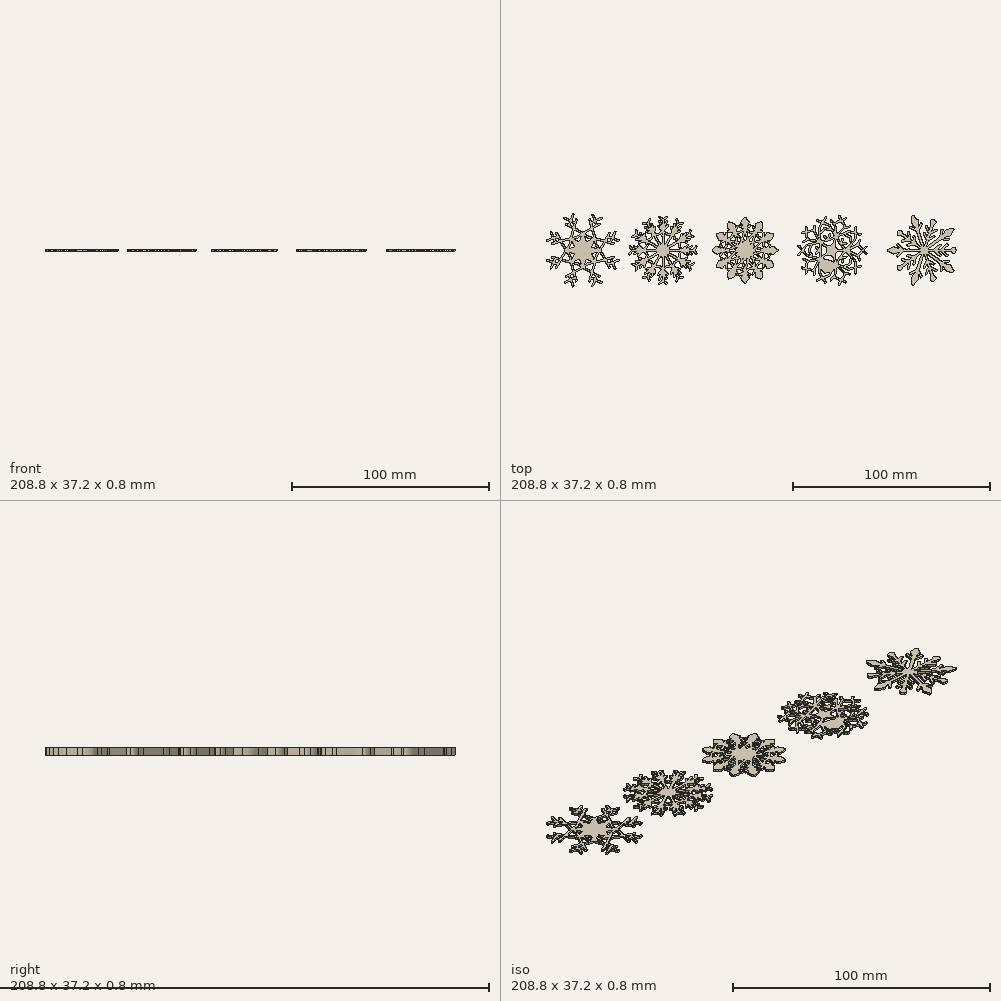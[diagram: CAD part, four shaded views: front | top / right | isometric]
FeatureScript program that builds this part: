
annotation { "Feature Type Name" : "Feature", "Feature Type Description" : "" }
export const myFeature = defineFeature(function(context is Context, id is Id, definition is map)
    precondition{}
    {
        {
            var Q0;
            Q0=qCreatedBy(makeId("Top.planeOp"),FACE);
            var sketch = newSketch(context, id + "F0", { "sketchPlane" : qUnion([Q0])});
            skFitSpline(sketch, "E0", {"points": [v(19, 0) * mm, v(18.91, 0.07) * mm, v(18.86, 0.12) * mm, v(18.83, 0.12) * mm]});
            skFitSpline(sketch, "E1", {"points": [v(18.83, 0.12) * mm, v(18.78, 0.1) * mm, v(18.72, 0.05) * mm, v(18.7, 0) * mm]});
            skFitSpline(sketch, "E2", {"points": [v(18.7, 0) * mm, v(18.68, -0.05) * mm, v(18.77, -0.14) * mm, v(18.83, -0.12) * mm]});
            skFitSpline(sketch, "E3", {"points": [v(18.83, -0.12) * mm, v(18.88, -0.1) * mm, v(18.92, -0.05) * mm, v(19, 0) * mm]});
            skFitSpline(sketch, "E4", {"points": [v(18, -11.04) * mm, v(17.67, -11.1) * mm, v(17.39, -11.14) * mm, v(17.1, -11.2) * mm]});
            skFitSpline(sketch, "E5", {"points": [v(17.1, -11.2) * mm, v(16.6, -11.32) * mm, v(16.09, -11.45) * mm, v(15.58, -11.59) * mm]});
            skFitSpline(sketch, "E6", {"points": [v(15.58, -11.59) * mm, v(15.26, -11.67) * mm, v(15, -11.51) * mm, v(14.74, -11.39) * mm]});
            skFitSpline(sketch, "E7", {"points": [v(14.74, -11.39) * mm, v(14.72, -11.38) * mm, v(14.7, -11.35) * mm, v(14.68, -11.32) * mm]});
            skFitSpline(sketch, "E8", {"points": [v(14.68, -11.32) * mm, v(14.51, -11.12) * mm, v(14.36, -10.92) * mm, v(14.2, -10.73) * mm]});
            skFitSpline(sketch, "E9", {"points": [v(14.2, -10.73) * mm, v(13.83, -10.31) * mm, v(13.46, -9.9) * mm, v(13.08, -9.5) * mm]});
            skFitSpline(sketch, "E10", {"points": [v(13.08, -9.5) * mm, v(13.07, -9.48) * mm, v(13.05, -9.48) * mm, v(13, -9.46) * mm]});
            skFitSpline(sketch, "E11", {"points": [v(13, -9.46) * mm, v(13, -9.5) * mm, v(13, -9.53) * mm, v(13, -9.56) * mm]});
            skFitSpline(sketch, "E12", {"points": [v(13, -9.56) * mm, v(12.96, -9.94) * mm, v(12.93, -10.33) * mm, v(12.9, -10.72) * mm]});
            skFitSpline(sketch, "E13", {"points": [v(12.9, -10.72) * mm, v(12.87, -10.96) * mm, v(12.92, -11.17) * mm, v(13.06, -11.37) * mm]});
            skFitSpline(sketch, "E14", {"points": [v(13.06, -11.37) * mm, v(13.44, -11.95) * mm, v(13.8, -12.55) * mm, v(14.18, -13.13) * mm]});
            skFitSpline(sketch, "E15", {"points": [v(14.18, -13.13) * mm, v(14.26, -13.26) * mm, v(14.36, -13.37) * mm, v(14.46, -13.5) * mm]});
            skFitSpline(sketch, "E16", {"points": [v(14.46, -13.5) * mm, v(14.84, -13.36) * mm, v(15.2, -13.22) * mm, v(15.56, -13.07) * mm]});
            skFitSpline(sketch, "E17", {"points": [v(15.56, -13.07) * mm, v(16.03, -12.9) * mm, v(16.5, -12.7) * mm, v(16.96, -12.52) * mm]});
            skFitSpline(sketch, "E18", {"points": [v(16.96, -12.52) * mm, v(17.05, -12.48) * mm, v(17.13, -12.42) * mm, v(17.18, -12.34) * mm]});
            skFitSpline(sketch, "E19", {"points": [v(17.18, -12.34) * mm, v(17.45, -11.93) * mm, v(17.7, -11.5) * mm, v(18, -11.04) * mm]});
            skFitSpline(sketch, "E20", {"points": [v(8.01, -2.6) * mm, v(8.03, -2.6) * mm, v(8.04, -2.57) * mm, v(8.06, -2.56) * mm]});
            skFitSpline(sketch, "E21", {"points": [v(8.06, -2.56) * mm, v(7.78, -2.08) * mm, v(7.5, -1.6) * mm, v(7.21, -1.12) * mm]});
            skFitSpline(sketch, "E22", {"points": [v(7.21, -1.12) * mm, v(7.08, -0.9) * mm, v(6.92, -0.68) * mm, v(6.78, -0.45) * mm]});
            skFitSpline(sketch, "E23", {"points": [v(6.78, -0.45) * mm, v(6.73, -0.36) * mm, v(6.71, -0.25) * mm, v(6.7, -0.14) * mm]});
            skFitSpline(sketch, "E24", {"points": [v(6.7, -0.14) * mm, v(6.68, -0.07) * mm, v(6.7, 0) * mm, v(6.7, 0.08) * mm]});
            skFitSpline(sketch, "E25", {"points": [v(6.7, 0.08) * mm, v(6.68, 0.23) * mm, v(6.73, 0.37) * mm, v(6.81, 0.5) * mm]});
            skFitSpline(sketch, "E26", {"points": [v(6.81, 0.5) * mm, v(7.2, 1.12) * mm, v(7.56, 1.74) * mm, v(7.94, 2.37) * mm]});
            skFitSpline(sketch, "E27", {"points": [v(7.94, 2.37) * mm, v(7.97, 2.43) * mm, v(8, 2.5) * mm, v(8.05, 2.6) * mm]});
            skFitSpline(sketch, "E28", {"points": [v(8.05, 2.6) * mm, v(7.98, 2.6) * mm, v(7.95, 2.6) * mm, v(7.9, 2.59) * mm]});
            skFitSpline(sketch, "E29", {"points": [v(7.9, 2.59) * mm, v(7.55, 2.5) * mm, v(7.2, 2.4) * mm, v(6.84, 2.33) * mm]});
            skFitSpline(sketch, "E30", {"points": [v(6.84, 2.33) * mm, v(6.57, 2.27) * mm, v(6.36, 2.15) * mm, v(6.19, 1.93) * mm]});
            skFitSpline(sketch, "E31", {"points": [v(6.19, 1.93) * mm, v(5.77, 1.4) * mm, v(5.34, 0.9) * mm, v(4.91, 0.38) * mm]});
            skFitSpline(sketch, "E32", {"points": [v(4.91, 0.38) * mm, v(4.81, 0.26) * mm, v(4.73, 0.12) * mm, v(4.63, -0.02) * mm]});
            skFitSpline(sketch, "E33", {"points": [v(4.63, -0.02) * mm, v(4.98, -0.45) * mm, v(5.31, -0.86) * mm, v(5.65, -1.28) * mm]});
            skFitSpline(sketch, "E34", {"points": [v(5.65, -1.28) * mm, v(5.88, -1.55) * mm, v(6.12, -1.82) * mm, v(6.35, -2.1) * mm]});
            skFitSpline(sketch, "E35", {"points": [v(6.35, -2.1) * mm, v(6.42, -2.18) * mm, v(6.5, -2.24) * mm, v(6.6, -2.26) * mm]});
            skFitSpline(sketch, "E36", {"points": [v(6.6, -2.26) * mm, v(6.92, -2.33) * mm, v(7.24, -2.41) * mm, v(7.55, -2.5) * mm]});
            skFitSpline(sketch, "E37", {"points": [v(7.55, -2.5) * mm, v(7.7, -2.53) * mm, v(7.86, -2.57) * mm, v(8.01, -2.6) * mm]});
            skFitSpline(sketch, "E38", {"points": [v(17.95, 11.02) * mm, v(17.96, 11.04) * mm, v(17.96, 11.06) * mm, v(17.97, 11.08) * mm]});
            skFitSpline(sketch, "E39", {"points": [v(17.97, 11.08) * mm, v(17.72, 11.48) * mm, v(17.46, 11.89) * mm, v(17.22, 12.3) * mm]});
            skFitSpline(sketch, "E40", {"points": [v(17.22, 12.3) * mm, v(17.15, 12.41) * mm, v(17.06, 12.49) * mm, v(16.93, 12.53) * mm]});
            skFitSpline(sketch, "E41", {"points": [v(16.93, 12.53) * mm, v(16.23, 12.8) * mm, v(15.54, 13.1) * mm, v(14.84, 13.37) * mm]});
            skFitSpline(sketch, "E42", {"points": [v(14.84, 13.37) * mm, v(14.71, 13.42) * mm, v(14.57, 13.45) * mm, v(14.42, 13.5) * mm]});
            skFitSpline(sketch, "E43", {"points": [v(14.42, 13.5) * mm, v(14.22, 13.18) * mm, v(14.03, 12.88) * mm, v(13.83, 12.58) * mm]});
            skFitSpline(sketch, "E44", {"points": [v(13.83, 12.58) * mm, v(13.55, 12.12) * mm, v(13.26, 11.67) * mm, v(12.97, 11.22) * mm]});
            skFitSpline(sketch, "E45", {"points": [v(12.97, 11.22) * mm, v(12.91, 11.13) * mm, v(12.89, 11.04) * mm, v(12.9, 10.93) * mm]});
            skFitSpline(sketch, "E46", {"points": [v(12.9, 10.93) * mm, v(12.93, 10.5) * mm, v(12.96, 10.06) * mm, v(12.99, 9.62) * mm]});
            skFitSpline(sketch, "E47", {"points": [v(12.99, 9.62) * mm, v(13, 9.57) * mm, v(13, 9.52) * mm, v(13.02, 9.43) * mm]});
            skFitSpline(sketch, "E48", {"points": [v(13.02, 9.43) * mm, v(13.3, 9.73) * mm, v(13.57, 10) * mm, v(13.81, 10.27) * mm]});
            skFitSpline(sketch, "E49", {"points": [v(13.81, 10.27) * mm, v(14.1, 10.6) * mm, v(14.37, 10.95) * mm, v(14.65, 11.29) * mm]});
            skFitSpline(sketch, "E50", {"points": [v(14.65, 11.29) * mm, v(14.74, 11.4) * mm, v(14.85, 11.49) * mm, v(15, 11.52) * mm]});
            skFitSpline(sketch, "E51", {"points": [v(15, 11.52) * mm, v(15.06, 11.53) * mm, v(15.12, 11.56) * mm, v(15.18, 11.57) * mm]});
            skFitSpline(sketch, "E52", {"points": [v(15.18, 11.57) * mm, v(15.3, 11.59) * mm, v(15.42, 11.62) * mm, v(15.53, 11.6) * mm]});
            skFitSpline(sketch, "E53", {"points": [v(15.53, 11.6) * mm, v(15.78, 11.55) * mm, v(16.01, 11.46) * mm, v(16.25, 11.4) * mm]});
            skFitSpline(sketch, "E54", {"points": [v(16.25, 11.4) * mm, v(16.82, 11.28) * mm, v(17.38, 11.15) * mm, v(17.95, 11.02) * mm]});
            skFitSpline(sketch, "E55", {"points": [v(26.01, 8.4) * mm, v(26.54, 8.18) * mm, v(27.04, 7.95) * mm, v(27.54, 7.74) * mm]});
            skFitSpline(sketch, "E56", {"points": [v(27.54, 7.74) * mm, v(27.8, 7.63) * mm, v(28.05, 7.55) * mm, v(28.3, 7.44) * mm]});
            skFitSpline(sketch, "E57", {"points": [v(28.3, 7.44) * mm, v(28.4, 7.4) * mm, v(28.49, 7.3) * mm, v(28.57, 7.22) * mm]});
            skFitSpline(sketch, "E58", {"points": [v(28.57, 7.22) * mm, v(28.62, 7.18) * mm, v(28.65, 7.1) * mm, v(28.7, 7.05) * mm]});
            skFitSpline(sketch, "E59", {"points": [v(28.7, 7.05) * mm, v(28.78, 6.96) * mm, v(28.82, 6.85) * mm, v(28.83, 6.73) * mm]});
            skFitSpline(sketch, "E60", {"points": [v(28.83, 6.73) * mm, v(28.85, 6.29) * mm, v(28.87, 5.85) * mm, v(28.9, 5.41) * mm]});
            skFitSpline(sketch, "E61", {"points": [v(28.9, 5.41) * mm, v(28.95, 5.02) * mm, v(29, 4.63) * mm, v(29.06, 4.24) * mm]});
            skFitSpline(sketch, "E62", {"points": [v(29.06, 4.24) * mm, v(29.1, 4.25) * mm, v(29.12, 4.26) * mm, v(29.13, 4.27) * mm]});
            skFitSpline(sketch, "E63", {"points": [v(29.13, 4.27) * mm, v(29.44, 4.64) * mm, v(29.76, 5.02) * mm, v(30.08, 5.4) * mm]});
            skFitSpline(sketch, "E64", {"points": [v(30.08, 5.4) * mm, v(30.11, 5.45) * mm, v(30.14, 5.51) * mm, v(30.15, 5.57) * mm]});
            skFitSpline(sketch, "E65", {"points": [v(30.15, 5.57) * mm, v(30.17, 5.74) * mm, v(30.19, 5.9) * mm, v(30.2, 6.07) * mm]});
            skFitSpline(sketch, "E66", {"points": [v(30.2, 6.07) * mm, v(30.23, 6.6) * mm, v(30.27, 7.14) * mm, v(30.3, 7.67) * mm]});
            skFitSpline(sketch, "E67", {"points": [v(30.3, 7.67) * mm, v(30.3, 7.9) * mm, v(30.3, 8.11) * mm, v(30.3, 8.34) * mm]});
            skFitSpline(sketch, "E68", {"points": [v(30.3, 8.34) * mm, v(30.19, 8.38) * mm, v(30.08, 8.42) * mm, v(29.97, 8.45) * mm]});
            skFitSpline(sketch, "E69", {"points": [v(29.97, 8.45) * mm, v(29.2, 8.65) * mm, v(28.41, 8.85) * mm, v(27.63, 9.04) * mm]});
            skFitSpline(sketch, "E70", {"points": [v(27.63, 9.04) * mm, v(27.57, 9.06) * mm, v(27.49, 9.05) * mm, v(27.43, 9.03) * mm]});
            skFitSpline(sketch, "E71", {"points": [v(27.43, 9.03) * mm, v(26.97, 8.85) * mm, v(26.52, 8.67) * mm, v(26.07, 8.48) * mm]});
            skFitSpline(sketch, "E72", {"points": [v(26.07, 8.48) * mm, v(26.06, 8.48) * mm, v(26.06, 8.46) * mm, v(26.01, 8.4) * mm]});
            skFitSpline(sketch, "E73", {"points": [v(29.1, -4.23) * mm, v(29.08, -4.24) * mm, v(29.06, -4.24) * mm, v(29.05, -4.24) * mm]});
            skFitSpline(sketch, "E74", {"points": [v(29.05, -4.24) * mm, v(28.99, -4.77) * mm, v(28.92, -5.3) * mm, v(28.88, -5.82) * mm]});
            skFitSpline(sketch, "E75", {"points": [v(28.88, -5.82) * mm, v(28.85, -6.14) * mm, v(28.85, -6.46) * mm, v(28.82, -6.78) * mm]});
            skFitSpline(sketch, "E76", {"points": [v(28.82, -6.78) * mm, v(28.81, -6.87) * mm, v(28.75, -6.95) * mm, v(28.71, -7.04) * mm]});
            skFitSpline(sketch, "E77", {"points": [v(28.71, -7.04) * mm, v(28.68, -7.1) * mm, v(28.62, -7.15) * mm, v(28.59, -7.2) * mm]});
            skFitSpline(sketch, "E78", {"points": [v(28.59, -7.2) * mm, v(28.52, -7.32) * mm, v(28.42, -7.4) * mm, v(28.3, -7.45) * mm]});
            skFitSpline(sketch, "E79", {"points": [v(28.3, -7.45) * mm, v(28.13, -7.52) * mm, v(27.96, -7.58) * mm, v(27.79, -7.65) * mm]});
            skFitSpline(sketch, "E80", {"points": [v(27.79, -7.65) * mm, v(27.23, -7.9) * mm, v(26.68, -8.13) * mm, v(26.12, -8.38) * mm]});
            skFitSpline(sketch, "E81", {"points": [v(26.12, -8.38) * mm, v(26.09, -8.4) * mm, v(26.06, -8.42) * mm, v(26.02, -8.45) * mm]});
            skFitSpline(sketch, "E82", {"points": [v(26.02, -8.45) * mm, v(26.48, -8.64) * mm, v(26.92, -8.82) * mm, v(27.36, -9) * mm]});
            skFitSpline(sketch, "E83", {"points": [v(27.36, -9) * mm, v(27.48, -9.06) * mm, v(27.59, -9.06) * mm, v(27.7, -9.03) * mm]});
            skFitSpline(sketch, "E84", {"points": [v(27.7, -9.03) * mm, v(28.44, -8.84) * mm, v(29.18, -8.66) * mm, v(29.91, -8.47) * mm]});
            skFitSpline(sketch, "E85", {"points": [v(29.91, -8.47) * mm, v(30.04, -8.44) * mm, v(30.17, -8.38) * mm, v(30.31, -8.33) * mm]});
            skFitSpline(sketch, "E86", {"points": [v(30.31, -8.33) * mm, v(30.31, -8.25) * mm, v(30.32, -8.17) * mm, v(30.31, -8.1) * mm]});
            skFitSpline(sketch, "E87", {"points": [v(30.31, -8.1) * mm, v(30.3, -7.84) * mm, v(30.28, -7.59) * mm, v(30.26, -7.33) * mm]});
            skFitSpline(sketch, "E88", {"points": [v(30.26, -7.33) * mm, v(30.23, -6.76) * mm, v(30.2, -6.19) * mm, v(30.15, -5.61) * mm]});
            skFitSpline(sketch, "E89", {"points": [v(30.15, -5.61) * mm, v(30.15, -5.53) * mm, v(30.1, -5.44) * mm, v(30.06, -5.38) * mm]});
            skFitSpline(sketch, "E90", {"points": [v(30.06, -5.38) * mm, v(29.85, -5.13) * mm, v(29.64, -4.88) * mm, v(29.42, -4.63) * mm]});
            skFitSpline(sketch, "E91", {"points": [v(29.42, -4.63) * mm, v(29.31, -4.5) * mm, v(29.2, -4.36) * mm, v(29.1, -4.23) * mm]});
            skFitSpline(sketch, "E92", {"points": [v(21.23, -5.73) * mm, v(21.28, -5.66) * mm, v(21.32, -5.61) * mm, v(21.35, -5.56) * mm]});
            skFitSpline(sketch, "E93", {"points": [v(21.35, -5.56) * mm, v(21.82, -4.8) * mm, v(22.27, -4.03) * mm, v(22.74, -3.26) * mm]});
            skFitSpline(sketch, "E94", {"points": [v(22.74, -3.26) * mm, v(22.85, -3.08) * mm, v(22.98, -2.9) * mm, v(23.11, -2.74) * mm]});
            skFitSpline(sketch, "E95", {"points": [v(23.11, -2.74) * mm, v(23.3, -2.52) * mm, v(23.49, -2.3) * mm, v(23.68, -2.09) * mm]});
            skFitSpline(sketch, "E96", {"points": [v(23.68, -2.09) * mm, v(24.08, -1.62) * mm, v(24.5, -1.15) * mm, v(24.9, -0.68) * mm]});
            skFitSpline(sketch, "E97", {"points": [v(24.9, -0.68) * mm, v(24.94, -0.63) * mm, v(24.97, -0.58) * mm, v(25.02, -0.5) * mm]});
            skFitSpline(sketch, "E98", {"points": [v(25.02, -0.5) * mm, v(24.9, -0.5) * mm, v(24.82, -0.5) * mm, v(24.74, -0.5) * mm]});
            skFitSpline(sketch, "E99", {"points": [v(24.74, -0.5) * mm, v(24.43, -0.51) * mm, v(24.1, -0.52) * mm, v(23.79, -0.52) * mm]});
            skFitSpline(sketch, "E100", {"points": [v(23.79, -0.52) * mm, v(23.37, -0.52) * mm, v(22.96, -0.5) * mm, v(22.54, -0.5) * mm]});
            skFitSpline(sketch, "E101", {"points": [v(22.54, -0.5) * mm, v(22.4, -0.5) * mm, v(22.26, -0.51) * mm, v(22.13, -0.6) * mm]});
            skFitSpline(sketch, "E102", {"points": [v(22.13, -0.6) * mm, v(21.76, -0.86) * mm, v(21.38, -1.12) * mm, v(21, -1.36) * mm]});
            skFitSpline(sketch, "E103", {"points": [v(21, -1.36) * mm, v(20.9, -1.43) * mm, v(20.83, -1.52) * mm, v(20.8, -1.64) * mm]});
            skFitSpline(sketch, "E104", {"points": [v(20.8, -1.64) * mm, v(20.68, -2.08) * mm, v(20.55, -2.52) * mm, v(20.42, -2.95) * mm]});
            skFitSpline(sketch, "E105", {"points": [v(20.42, -2.95) * mm, v(20.4, -3.06) * mm, v(20.4, -3.16) * mm, v(20.43, -3.26) * mm]});
            skFitSpline(sketch, "E106", {"points": [v(20.43, -3.26) * mm, v(20.69, -4.07) * mm, v(20.95, -4.88) * mm, v(21.23, -5.73) * mm]});
            skFitSpline(sketch, "E107", {"points": [v(20.24, -6.06) * mm, v(20.24, -6) * mm, v(20.24, -5.97) * mm, v(20.23, -5.95) * mm]});
            skFitSpline(sketch, "E108", {"points": [v(20.23, -5.95) * mm, v(19.97, -5.17) * mm, v(19.71, -4.38) * mm, v(19.45, -3.6) * mm]});
            skFitSpline(sketch, "E109", {"points": [v(19.45, -3.6) * mm, v(19.41, -3.5) * mm, v(19.34, -3.4) * mm, v(19.26, -3.33) * mm]});
            skFitSpline(sketch, "E110", {"points": [v(19.26, -3.33) * mm, v(18.92, -3.05) * mm, v(18.57, -2.78) * mm, v(18.23, -2.5) * mm]});
            skFitSpline(sketch, "E111", {"points": [v(18.23, -2.5) * mm, v(18.1, -2.41) * mm, v(17.98, -2.37) * mm, v(17.83, -2.38) * mm]});
            skFitSpline(sketch, "E112", {"points": [v(17.83, -2.38) * mm, v(17.44, -2.4) * mm, v(17.05, -2.42) * mm, v(16.66, -2.42) * mm]});
            skFitSpline(sketch, "E113", {"points": [v(16.66, -2.42) * mm, v(16.46, -2.42) * mm, v(16.3, -2.48) * mm, v(16.13, -2.6) * mm]});
            skFitSpline(sketch, "E114", {"points": [v(16.13, -2.6) * mm, v(15.5, -3.06) * mm, v(14.86, -3.5) * mm, v(14.22, -3.97) * mm]});
            skFitSpline(sketch, "E115", {"points": [v(14.22, -3.97) * mm, v(14.19, -3.99) * mm, v(14.16, -4.02) * mm, v(14.12, -4.06) * mm]});
            skFitSpline(sketch, "E116", {"points": [v(14.12, -4.06) * mm, v(14.2, -4.09) * mm, v(14.26, -4.1) * mm, v(14.32, -4.12) * mm]});
            skFitSpline(sketch, "E117", {"points": [v(14.32, -4.12) * mm, v(14.71, -4.2) * mm, v(15.1, -4.29) * mm, v(15.5, -4.38) * mm]});
            skFitSpline(sketch, "E118", {"points": [v(15.5, -4.38) * mm, v(16, -4.5) * mm, v(16.52, -4.62) * mm, v(17.03, -4.75) * mm]});
            skFitSpline(sketch, "E119", {"points": [v(17.03, -4.75) * mm, v(17.23, -4.8) * mm, v(17.43, -4.89) * mm, v(17.63, -4.96) * mm]});
            skFitSpline(sketch, "E120", {"points": [v(17.63, -4.96) * mm, v(17.83, -5.04) * mm, v(18.03, -5.13) * mm, v(18.23, -5.22) * mm]});
            skFitSpline(sketch, "E121", {"points": [v(18.23, -5.22) * mm, v(18.64, -5.39) * mm, v(19.05, -5.56) * mm, v(19.46, -5.74) * mm]});
            skFitSpline(sketch, "E122", {"points": [v(19.46, -5.74) * mm, v(19.7, -5.84) * mm, v(19.96, -5.95) * mm, v(20.24, -6.06) * mm]});
            skFitSpline(sketch, "E123", {"points": [v(13.52, -3.2) * mm, v(13.55, -3.2) * mm, v(13.57, -3.2) * mm, v(13.58, -3.19) * mm]});
            skFitSpline(sketch, "E124", {"points": [v(13.58, -3.19) * mm, v(14.26, -2.69) * mm, v(14.94, -2.19) * mm, v(15.62, -1.68) * mm]});
            skFitSpline(sketch, "E125", {"points": [v(15.62, -1.68) * mm, v(15.7, -1.62) * mm, v(15.76, -1.53) * mm, v(15.8, -1.44) * mm]});
            skFitSpline(sketch, "E126", {"points": [v(15.8, -1.44) * mm, v(15.95, -1.04) * mm, v(16.09, -0.64) * mm, v(16.24, -0.25) * mm]});
            skFitSpline(sketch, "E127", {"points": [v(16.24, -0.25) * mm, v(16.3, -0.08) * mm, v(16.31, 0.07) * mm, v(16.25, 0.24) * mm]});
            skFitSpline(sketch, "E128", {"points": [v(16.25, 0.24) * mm, v(16.1, 0.6) * mm, v(15.97, 0.95) * mm, v(15.85, 1.32) * mm]});
            skFitSpline(sketch, "E129", {"points": [v(15.85, 1.32) * mm, v(15.78, 1.52) * mm, v(15.67, 1.66) * mm, v(15.5, 1.78) * mm]});
            skFitSpline(sketch, "E130", {"points": [v(15.5, 1.78) * mm, v(14.87, 2.23) * mm, v(14.25, 2.7) * mm, v(13.63, 3.16) * mm]});
            skFitSpline(sketch, "E131", {"points": [v(13.63, 3.16) * mm, v(13.6, 3.18) * mm, v(13.56, 3.2) * mm, v(13.5, 3.23) * mm]});
            skFitSpline(sketch, "E132", {"points": [v(13.5, 3.23) * mm, v(13.51, 3) * mm, v(13.52, 2.8) * mm, v(13.54, 2.6) * mm]});
            skFitSpline(sketch, "E133", {"points": [v(13.54, 2.6) * mm, v(13.57, 2.24) * mm, v(13.62, 1.87) * mm, v(13.65, 1.5) * mm]});
            skFitSpline(sketch, "E134", {"points": [v(13.65, 1.5) * mm, v(13.68, 1.16) * mm, v(13.7, 0.8) * mm, v(13.72, 0.46) * mm]});
            skFitSpline(sketch, "E135", {"points": [v(13.72, 0.46) * mm, v(13.74, 0.21) * mm, v(13.76, -0.03) * mm, v(13.75, -0.28) * mm]});
            skFitSpline(sketch, "E136", {"points": [v(13.75, -0.28) * mm, v(13.73, -0.65) * mm, v(13.7, -1.03) * mm, v(13.66, -1.4) * mm]});
            skFitSpline(sketch, "E137", {"points": [v(13.66, -1.4) * mm, v(13.62, -1.82) * mm, v(13.56, -2.24) * mm, v(13.53, -2.66) * mm]});
            skFitSpline(sketch, "E138", {"points": [v(13.53, -2.66) * mm, v(13.51, -2.84) * mm, v(13.52, -3.02) * mm, v(13.52, -3.2) * mm]});
            skFitSpline(sketch, "E139", {"points": [v(14.11, 4.07) * mm, v(14.15, 4.03) * mm, v(14.16, 4) * mm, v(14.18, 4) * mm]});
            skFitSpline(sketch, "E140", {"points": [v(14.18, 4) * mm, v(14.85, 3.52) * mm, v(15.52, 3.04) * mm, v(16.18, 2.56) * mm]});
            skFitSpline(sketch, "E141", {"points": [v(16.18, 2.56) * mm, v(16.32, 2.46) * mm, v(16.46, 2.42) * mm, v(16.63, 2.42) * mm]});
            skFitSpline(sketch, "E142", {"points": [v(16.63, 2.42) * mm, v(16.97, 2.41) * mm, v(17.3, 2.4) * mm, v(17.63, 2.37) * mm]});
            skFitSpline(sketch, "E143", {"points": [v(17.63, 2.37) * mm, v(17.89, 2.36) * mm, v(18.11, 2.4) * mm, v(18.32, 2.57) * mm]});
            skFitSpline(sketch, "E144", {"points": [v(18.32, 2.57) * mm, v(18.6, 2.82) * mm, v(18.9, 3.05) * mm, v(19.2, 3.27) * mm]});
            skFitSpline(sketch, "E145", {"points": [v(19.2, 3.27) * mm, v(19.33, 3.37) * mm, v(19.42, 3.5) * mm, v(19.47, 3.65) * mm]});
            skFitSpline(sketch, "E146", {"points": [v(19.47, 3.65) * mm, v(19.71, 4.4) * mm, v(19.97, 5.15) * mm, v(20.22, 5.9) * mm]});
            skFitSpline(sketch, "E147", {"points": [v(20.22, 5.9) * mm, v(20.23, 5.94) * mm, v(20.23, 5.99) * mm, v(20.24, 6.06) * mm]});
            skFitSpline(sketch, "E148", {"points": [v(20.24, 6.06) * mm, v(20.11, 6) * mm, v(20, 5.97) * mm, v(19.9, 5.93) * mm]});
            skFitSpline(sketch, "E149", {"points": [v(19.9, 5.93) * mm, v(19.39, 5.7) * mm, v(18.86, 5.48) * mm, v(18.34, 5.26) * mm]});
            skFitSpline(sketch, "E150", {"points": [v(18.34, 5.26) * mm, v(18.08, 5.15) * mm, v(17.82, 5.03) * mm, v(17.55, 4.93) * mm]});
            skFitSpline(sketch, "E151", {"points": [v(17.55, 4.93) * mm, v(17.32, 4.84) * mm, v(17.08, 4.78) * mm, v(16.85, 4.7) * mm]});
            skFitSpline(sketch, "E152", {"points": [v(16.85, 4.7) * mm, v(16.67, 4.66) * mm, v(16.49, 4.63) * mm, v(16.3, 4.59) * mm]});
            skFitSpline(sketch, "E153", {"points": [v(16.3, 4.59) * mm, v(15.84, 4.48) * mm, v(15.38, 4.37) * mm, v(14.91, 4.26) * mm]});
            skFitSpline(sketch, "E154", {"points": [v(14.91, 4.26) * mm, v(14.65, 4.2) * mm, v(14.4, 4.14) * mm, v(14.11, 4.07) * mm]});
            skFitSpline(sketch, "E155", {"points": [v(25.03, 0.52) * mm, v(24.94, 0.63) * mm, v(24.87, 0.72) * mm, v(24.8, 0.8) * mm]});
            skFitSpline(sketch, "E156", {"points": [v(24.8, 0.8) * mm, v(24.4, 1.25) * mm, v(24.02, 1.7) * mm, v(23.63, 2.14) * mm]});
            skFitSpline(sketch, "E157", {"points": [v(23.63, 2.14) * mm, v(23.5, 2.3) * mm, v(23.37, 2.44) * mm, v(23.25, 2.6) * mm]});
            skFitSpline(sketch, "E158", {"points": [v(23.25, 2.6) * mm, v(23.05, 2.85) * mm, v(22.86, 3.1) * mm, v(22.68, 3.37) * mm]});
            skFitSpline(sketch, "E159", {"points": [v(22.68, 3.37) * mm, v(22.58, 3.5) * mm, v(22.5, 3.67) * mm, v(22.4, 3.82) * mm]});
            skFitSpline(sketch, "E160", {"points": [v(22.4, 3.82) * mm, v(22.16, 4.22) * mm, v(21.92, 4.62) * mm, v(21.68, 5.03) * mm]});
            skFitSpline(sketch, "E161", {"points": [v(21.68, 5.03) * mm, v(21.56, 5.22) * mm, v(21.45, 5.4) * mm, v(21.33, 5.6) * mm]});
            skFitSpline(sketch, "E162", {"points": [v(21.33, 5.6) * mm, v(21.3, 5.64) * mm, v(21.26, 5.67) * mm, v(21.22, 5.71) * mm]});
            skFitSpline(sketch, "E163", {"points": [v(21.22, 5.71) * mm, v(20.95, 4.88) * mm, v(20.69, 4.07) * mm, v(20.43, 3.26) * mm]});
            skFitSpline(sketch, "E164", {"points": [v(20.43, 3.26) * mm, v(20.4, 3.15) * mm, v(20.4, 3.06) * mm, v(20.42, 2.95) * mm]});
            skFitSpline(sketch, "E165", {"points": [v(20.42, 2.95) * mm, v(20.55, 2.52) * mm, v(20.68, 2.08) * mm, v(20.8, 1.64) * mm]});
            skFitSpline(sketch, "E166", {"points": [v(20.8, 1.64) * mm, v(20.83, 1.53) * mm, v(20.88, 1.44) * mm, v(20.98, 1.38) * mm]});
            skFitSpline(sketch, "E167", {"points": [v(20.98, 1.38) * mm, v(21.37, 1.12) * mm, v(21.75, 0.86) * mm, v(22.14, 0.6) * mm]});
            skFitSpline(sketch, "E168", {"points": [v(22.14, 0.6) * mm, v(22.23, 0.55) * mm, v(22.35, 0.51) * mm, v(22.45, 0.51) * mm]});
            skFitSpline(sketch, "E169", {"points": [v(22.45, 0.51) * mm, v(22.88, 0.5) * mm, v(23.3, 0.51) * mm, v(23.72, 0.52) * mm]});
            skFitSpline(sketch, "E170", {"points": [v(23.72, 0.52) * mm, v(23.82, 0.52) * mm, v(23.91, 0.52) * mm, v(24.01, 0.52) * mm]});
            skFitSpline(sketch, "E171", {"points": [v(24.01, 0.52) * mm, v(24.34, 0.52) * mm, v(24.66, 0.52) * mm, v(25.03, 0.52) * mm]});
            skFitSpline(sketch, "E172", {"points": [v(9.44, -9.57) * mm, v(9.7, -9.07) * mm, v(9.94, -8.58) * mm, v(10.2, -8.09) * mm]});
            skFitSpline(sketch, "E173", {"points": [v(10.2, -8.09) * mm, v(10.44, -7.6) * mm, v(10.7, -7.12) * mm, v(10.93, -6.64) * mm]});
            skFitSpline(sketch, "E174", {"points": [v(10.93, -6.64) * mm, v(11.18, -6.15) * mm, v(11.47, -5.7) * mm, v(11.72, -5.17) * mm]});
            skFitSpline(sketch, "E175", {"points": [v(11.72, -5.17) * mm, v(10.05, -5.45) * mm, v(8.43, -5.71) * mm, v(6.82, -5.98) * mm]});
            skFitSpline(sketch, "E176", {"points": [v(6.82, -5.98) * mm, v(6.6, -6.96) * mm, v(6.43, -7.93) * mm, v(6.57, -8.92) * mm]});
            skFitSpline(sketch, "E177", {"points": [v(6.57, -8.92) * mm, v(7.47, -9.3) * mm, v(8.43, -9.49) * mm, v(9.44, -9.57) * mm]});
            skFitSpline(sketch, "E178", {"points": [v(32.05, -2.22) * mm, v(32.8, -1.57) * mm, v(33.48, -0.86) * mm, v(34, 0) * mm]});
            skFitSpline(sketch, "E179", {"points": [v(34, 0) * mm, v(33.48, 0.86) * mm, v(32.8, 1.57) * mm, v(32.05, 2.22) * mm]});
            skFitSpline(sketch, "E180", {"points": [v(32.05, 2.22) * mm, v(30.57, 1.48) * mm, v(29.1, 0.74) * mm, v(27.63, 0) * mm]});
            skFitSpline(sketch, "E181", {"points": [v(27.63, 0) * mm, v(29.1, -0.74) * mm, v(30.58, -1.48) * mm, v(32.05, -2.22) * mm]});
            skFitSpline(sketch, "E182", {"points": [v(20.8, -13.26) * mm, v(21.67, -13.78) * mm, v(22.55, -14.2) * mm, v(23.51, -14.42) * mm]});
            skFitSpline(sketch, "E183", {"points": [v(23.51, -14.42) * mm, v(24.17, -13.67) * mm, v(24.64, -12.8) * mm, v(25.03, -11.87) * mm]});
            skFitSpline(sketch, "E184", {"points": [v(25.03, -11.87) * mm, v(24.64, -11.48) * mm, v(24.25, -11.1) * mm, v(23.86, -10.7) * mm]});
            skFitSpline(sketch, "E185", {"points": [v(23.86, -10.7) * mm, v(23.47, -10.32) * mm, v(23.08, -9.92) * mm, v(22.69, -9.54) * mm]});
            skFitSpline(sketch, "E186", {"points": [v(22.69, -9.54) * mm, v(22.3, -9.16) * mm, v(21.96, -8.73) * mm, v(21.54, -8.36) * mm]});
            skFitSpline(sketch, "E187", {"points": [v(21.54, -8.36) * mm, v(21.3, -10.01) * mm, v(21.05, -11.63) * mm, v(20.8, -13.26) * mm]});
            skFitSpline(sketch, "E188", {"points": [v(21.54, 8.37) * mm, v(22.7, 9.55) * mm, v(23.86, 10.72) * mm, v(25.02, 11.9) * mm]});
            skFitSpline(sketch, "E189", {"points": [v(25.02, 11.9) * mm, v(24.64, 12.8) * mm, v(24.17, 13.67) * mm, v(23.51, 14.42) * mm]});
            skFitSpline(sketch, "E190", {"points": [v(23.51, 14.42) * mm, v(22.54, 14.2) * mm, v(21.65, 13.78) * mm, v(20.8, 13.26) * mm]});
            skFitSpline(sketch, "E191", {"points": [v(20.8, 13.26) * mm, v(21.05, 11.63) * mm, v(21.3, 10) * mm, v(21.54, 8.37) * mm]});
            skFitSpline(sketch, "E192", {"points": [v(11.7, 5.17) * mm, v(10.94, 6.64) * mm, v(10.19, 8.1) * mm, v(9.43, 9.56) * mm]});
            skFitSpline(sketch, "E193", {"points": [v(9.43, 9.56) * mm, v(8.43, 9.5) * mm, v(7.46, 9.3) * mm, v(6.57, 8.92) * mm]});
            skFitSpline(sketch, "E194", {"points": [v(6.57, 8.92) * mm, v(6.43, 7.9) * mm, v(6.61, 6.94) * mm, v(6.82, 5.98) * mm]});
            skFitSpline(sketch, "E195", {"points": [v(6.82, 5.98) * mm, v(8.45, 5.7) * mm, v(10.07, 5.44) * mm, v(11.7, 5.17) * mm]});
            skFitSpline(sketch, "E196", {"points": [v(12.08, 0) * mm, v(11.97, 0.08) * mm, v(11.9, 0.13) * mm, v(11.83, 0.18) * mm]});
            skFitSpline(sketch, "E197", {"points": [v(11.83, 0.18) * mm, v(11.46, 0.47) * mm, v(11.08, 0.75) * mm, v(10.71, 1.04) * mm]});
            skFitSpline(sketch, "E198", {"points": [v(10.71, 1.04) * mm, v(10.64, 1.1) * mm, v(10.57, 1.17) * mm, v(10.52, 1.25) * mm]});
            skFitSpline(sketch, "E199", {"points": [v(10.52, 1.25) * mm, v(10.38, 1.46) * mm, v(10.43, 1.75) * mm, v(10.62, 1.9) * mm]});
            skFitSpline(sketch, "E200", {"points": [v(10.62, 1.9) * mm, v(10.82, 2.06) * mm, v(11.05, 2.04) * mm, v(11.26, 1.87) * mm]});
            skFitSpline(sketch, "E201", {"points": [v(11.26, 1.87) * mm, v(11.67, 1.54) * mm, v(12.1, 1.21) * mm, v(12.52, 0.89) * mm]});
            skFitSpline(sketch, "E202", {"points": [v(12.52, 0.89) * mm, v(12.57, 0.85) * mm, v(12.63, 0.82) * mm, v(12.7, 0.77) * mm]});
            skFitSpline(sketch, "E203", {"points": [v(12.7, 0.77) * mm, v(12.71, 1.74) * mm, v(12.51, 2.66) * mm, v(12.51, 3.6) * mm]});
            skFitSpline(sketch, "E204", {"points": [v(12.51, 3.6) * mm, v(11.3, 3.4) * mm, v(10.12, 3.1) * mm, v(8.94, 2.8) * mm]});
            skFitSpline(sketch, "E205", {"points": [v(8.94, 2.8) * mm, v(9.06, 2.6) * mm, v(9.08, 2.41) * mm, v(8.96, 2.22) * mm]});
            skFitSpline(sketch, "E206", {"points": [v(8.96, 2.22) * mm, v(8.61, 1.62) * mm, v(8.27, 1.02) * mm, v(7.91, 0.42) * mm]});
            skFitSpline(sketch, "E207", {"points": [v(7.91, 0.42) * mm, v(7.83, 0.28) * mm, v(7.74, 0.14) * mm, v(7.66, 0) * mm]});
            skFitSpline(sketch, "E208", {"points": [v(7.66, 0) * mm, v(7.71, -0.1) * mm, v(7.75, -0.19) * mm, v(7.81, -0.26) * mm]});
            skFitSpline(sketch, "E209", {"points": [v(7.81, -0.26) * mm, v(8.22, -0.83) * mm, v(8.55, -1.46) * mm, v(8.89, -2.07) * mm]});
            skFitSpline(sketch, "E210", {"points": [v(8.89, -2.07) * mm, v(9.02, -2.31) * mm, v(9.12, -2.55) * mm, v(8.94, -2.81) * mm]});
            skFitSpline(sketch, "E211", {"points": [v(8.94, -2.81) * mm, v(10.13, -3.1) * mm, v(11.3, -3.41) * mm, v(12.51, -3.6) * mm]});
            skFitSpline(sketch, "E212", {"points": [v(12.51, -3.6) * mm, v(12.51, -2.65) * mm, v(12.72, -1.73) * mm, v(12.7, -0.76) * mm]});
            skFitSpline(sketch, "E213", {"points": [v(12.7, -0.76) * mm, v(12.6, -0.83) * mm, v(12.55, -0.86) * mm, v(12.5, -0.9) * mm]});
            skFitSpline(sketch, "E214", {"points": [v(12.5, -0.9) * mm, v(12.08, -1.23) * mm, v(11.66, -1.55) * mm, v(11.25, -1.88) * mm]});
            skFitSpline(sketch, "E215", {"points": [v(11.25, -1.88) * mm, v(11.08, -2.01) * mm, v(10.9, -2.06) * mm, v(10.71, -1.96) * mm]});
            skFitSpline(sketch, "E216", {"points": [v(10.71, -1.96) * mm, v(10.53, -1.86) * mm, v(10.44, -1.7) * mm, v(10.45, -1.49) * mm]});
            skFitSpline(sketch, "E217", {"points": [v(10.45, -1.49) * mm, v(10.45, -1.31) * mm, v(10.54, -1.18) * mm, v(10.67, -1.08) * mm]});
            skFitSpline(sketch, "E218", {"points": [v(10.67, -1.08) * mm, v(10.98, -0.83) * mm, v(11.3, -0.58) * mm, v(11.61, -0.34) * mm]});
            skFitSpline(sketch, "E219", {"points": [v(11.61, -0.34) * mm, v(11.75, -0.23) * mm, v(11.9, -0.13) * mm, v(12.08, 0) * mm]});
            skFitSpline(sketch, "E220", {"points": [v(21.82, -6.62) * mm, v(22.45, -6.96) * mm, v(24.85, -7.99) * mm, v(25.17, -8.06) * mm]});
            skFitSpline(sketch, "E221", {"points": [v(25.17, -8.06) * mm, v(25.19, -7.84) * mm, v(25.3, -7.68) * mm, v(25.5, -7.6) * mm]});
            skFitSpline(sketch, "E222", {"points": [v(25.5, -7.6) * mm, v(26.12, -7.32) * mm, v(26.75, -7.04) * mm, v(27.38, -6.76) * mm]});
            skFitSpline(sketch, "E223", {"points": [v(27.38, -6.76) * mm, v(27.54, -6.7) * mm, v(27.7, -6.63) * mm, v(27.86, -6.57) * mm]});
            skFitSpline(sketch, "E224", {"points": [v(27.86, -6.57) * mm, v(27.88, -6.42) * mm, v(27.9, -6.3) * mm, v(27.9, -6.17) * mm]});
            skFitSpline(sketch, "E225", {"points": [v(27.9, -6.17) * mm, v(27.9, -5.95) * mm, v(27.9, -5.74) * mm, v(27.92, -5.52) * mm]});
            skFitSpline(sketch, "E226", {"points": [v(27.92, -5.52) * mm, v(27.97, -5.05) * mm, v(28.04, -4.59) * mm, v(28.09, -4.12) * mm]});
            skFitSpline(sketch, "E227", {"points": [v(28.09, -4.12) * mm, v(28.12, -3.85) * mm, v(28.2, -3.64) * mm, v(28.47, -3.53) * mm]});
            skFitSpline(sketch, "E228", {"points": [v(28.47, -3.53) * mm, v(27.68, -2.6) * mm, v(26.92, -1.66) * mm, v(26.04, -0.8) * mm]});
            skFitSpline(sketch, "E229", {"points": [v(26.04, -0.8) * mm, v(25.49, -1.58) * mm, v(24.78, -2.2) * mm, v(24.24, -2.96) * mm]});
            skFitSpline(sketch, "E230", {"points": [v(24.24, -2.96) * mm, v(24.27, -2.98) * mm, v(24.28, -3) * mm, v(24.3, -3) * mm]});
            skFitSpline(sketch, "E231", {"points": [v(24.3, -3) * mm, v(24.87, -3) * mm, v(25.44, -3.03) * mm, v(26.01, -2.94) * mm]});
            skFitSpline(sketch, "E232", {"points": [v(26.01, -2.94) * mm, v(26.28, -2.9) * mm, v(26.51, -3.04) * mm, v(26.58, -3.3) * mm]});
            skFitSpline(sketch, "E233", {"points": [v(26.58, -3.3) * mm, v(26.64, -3.54) * mm, v(26.5, -3.8) * mm, v(26.25, -3.88) * mm]});
            skFitSpline(sketch, "E234", {"points": [v(26.25, -3.88) * mm, v(26.15, -3.91) * mm, v(26.04, -3.93) * mm, v(25.94, -3.93) * mm]});
            skFitSpline(sketch, "E235", {"points": [v(25.94, -3.93) * mm, v(25.49, -3.94) * mm, v(25.03, -3.95) * mm, v(24.58, -3.96) * mm]});
            skFitSpline(sketch, "E236", {"points": [v(24.58, -3.96) * mm, v(24.5, -3.96) * mm, v(24.4, -3.96) * mm, v(24.29, -3.96) * mm]});
            skFitSpline(sketch, "E237", {"points": [v(24.29, -3.96) * mm, v(24.35, -4.17) * mm, v(24.41, -4.34) * mm, v(24.46, -4.51) * mm]});
            skFitSpline(sketch, "E238", {"points": [v(24.46, -4.51) * mm, v(24.58, -4.94) * mm, v(24.71, -5.36) * mm, v(24.8, -5.78) * mm]});
            skFitSpline(sketch, "E239", {"points": [v(24.8, -5.78) * mm, v(24.88, -6.14) * mm, v(24.53, -6.44) * mm, v(24.18, -6.33) * mm]});
            skFitSpline(sketch, "E240", {"points": [v(24.18, -6.33) * mm, v(23.96, -6.27) * mm, v(23.87, -6.1) * mm, v(23.83, -5.89) * mm]});
            skFitSpline(sketch, "E241", {"points": [v(23.83, -5.89) * mm, v(23.73, -5.32) * mm, v(23.52, -4.78) * mm, v(23.33, -4.2) * mm]});
            skFitSpline(sketch, "E242", {"points": [v(23.33, -4.2) * mm, v(22.76, -4.99) * mm, v(22.38, -5.85) * mm, v(21.82, -6.62) * mm]});
            skFitSpline(sketch, "E243", {"points": [v(18.44, 10.27) * mm, v(18.25, 10.04) * mm, v(18.01, 10.03) * mm, v(17.76, 10.08) * mm]});
            skFitSpline(sketch, "E244", {"points": [v(17.76, 10.08) * mm, v(17.05, 10.23) * mm, v(16.34, 10.33) * mm, v(15.66, 10.56) * mm]});
            skFitSpline(sketch, "E245", {"points": [v(15.66, 10.56) * mm, v(15.45, 10.63) * mm, v(15.3, 10.6) * mm, v(15.17, 10.4) * mm]});
            skFitSpline(sketch, "E246", {"points": [v(15.17, 10.4) * mm, v(14.77, 9.83) * mm, v(14.27, 9.33) * mm, v(13.79, 8.82) * mm]});
            skFitSpline(sketch, "E247", {"points": [v(13.79, 8.82) * mm, v(13.6, 8.61) * mm, v(13.4, 8.45) * mm, v(13.1, 8.54) * mm]});
            skFitSpline(sketch, "E248", {"points": [v(13.1, 8.54) * mm, v(13.18, 7.3) * mm, v(13.26, 6.1) * mm, v(13.45, 4.9) * mm]});
            skFitSpline(sketch, "E249", {"points": [v(13.45, 4.9) * mm, v(14.35, 5.19) * mm, v(15.3, 5.28) * mm, v(16.22, 5.59) * mm]});
            skFitSpline(sketch, "E250", {"points": [v(16.22, 5.59) * mm, v(15.7, 5.95) * mm, v(15.25, 6.33) * mm, v(14.73, 6.61) * mm]});
            skFitSpline(sketch, "E251", {"points": [v(14.73, 6.61) * mm, v(14.47, 6.75) * mm, v(14.38, 7.02) * mm, v(14.5, 7.26) * mm]});
            skFitSpline(sketch, "E252", {"points": [v(14.5, 7.26) * mm, v(14.62, 7.49) * mm, v(14.89, 7.6) * mm, v(15.14, 7.5) * mm]});
            skFitSpline(sketch, "E253", {"points": [v(15.14, 7.5) * mm, v(15.23, 7.46) * mm, v(15.31, 7.41) * mm, v(15.4, 7.36) * mm]});
            skFitSpline(sketch, "E254", {"points": [v(15.4, 7.36) * mm, v(15.76, 7.1) * mm, v(16.13, 6.85) * mm, v(16.5, 6.6) * mm]});
            skFitSpline(sketch, "E255", {"points": [v(16.5, 6.6) * mm, v(16.57, 6.54) * mm, v(16.65, 6.49) * mm, v(16.74, 6.42) * mm]});
            skFitSpline(sketch, "E256", {"points": [v(16.74, 6.42) * mm, v(16.77, 6.53) * mm, v(16.8, 6.6) * mm, v(16.83, 6.69) * mm]});
            skFitSpline(sketch, "E257", {"points": [v(16.83, 6.69) * mm, v(16.99, 7.13) * mm, v(17.14, 7.58) * mm, v(17.3, 8.02) * mm]});
            skFitSpline(sketch, "E258", {"points": [v(17.3, 8.02) * mm, v(17.33, 8.1) * mm, v(17.38, 8.2) * mm, v(17.43, 8.27) * mm]});
            skFitSpline(sketch, "E259", {"points": [v(17.43, 8.27) * mm, v(17.59, 8.47) * mm, v(17.87, 8.52) * mm, v(18.08, 8.4) * mm]});
            skFitSpline(sketch, "E260", {"points": [v(18.08, 8.4) * mm, v(18.3, 8.27) * mm, v(18.36, 8.02) * mm, v(18.27, 7.77) * mm]});
            skFitSpline(sketch, "E261", {"points": [v(18.27, 7.77) * mm, v(18.07, 7.25) * mm, v(17.88, 6.72) * mm, v(17.7, 6.2) * mm]});
            skFitSpline(sketch, "E262", {"points": [v(17.7, 6.2) * mm, v(17.68, 6.16) * mm, v(17.69, 6.11) * mm, v(17.68, 6.04) * mm]});
            skFitSpline(sketch, "E263", {"points": [v(17.68, 6.04) * mm, v(18.57, 6.41) * mm, v(19.42, 6.77) * mm, v(20.28, 7.13) * mm]});
            skFitSpline(sketch, "E264", {"points": [v(20.28, 7.13) * mm, v(19.74, 8.22) * mm, v(19.1, 9.23) * mm, v(18.44, 10.27) * mm]});
            skFitSpline(sketch, "E265", {"points": [v(24.22, 2.97) * mm, v(24.8, 2.2) * mm, v(25.5, 1.56) * mm, v(26.07, 0.77) * mm]});
            skFitSpline(sketch, "E266", {"points": [v(26.07, 0.77) * mm, v(26.9, 1.7) * mm, v(27.69, 2.61) * mm, v(28.5, 3.53) * mm]});
            skFitSpline(sketch, "E267", {"points": [v(28.5, 3.53) * mm, v(28.25, 3.63) * mm, v(28.13, 3.78) * mm, v(28.1, 4) * mm]});
            skFitSpline(sketch, "E268", {"points": [v(28.1, 4) * mm, v(28.03, 4.66) * mm, v(27.91, 5.3) * mm, v(27.91, 5.96) * mm]});
            skFitSpline(sketch, "E269", {"points": [v(27.91, 5.96) * mm, v(27.91, 6.16) * mm, v(27.88, 6.37) * mm, v(27.86, 6.57) * mm]});
            skFitSpline(sketch, "E270", {"points": [v(27.86, 6.57) * mm, v(27.74, 6.62) * mm, v(27.65, 6.67) * mm, v(27.55, 6.7) * mm]});
            skFitSpline(sketch, "E271", {"points": [v(27.55, 6.7) * mm, v(26.9, 6.91) * mm, v(26.3, 7.2) * mm, v(25.69, 7.5) * mm]});
            skFitSpline(sketch, "E272", {"points": [v(25.69, 7.5) * mm, v(25.56, 7.56) * mm, v(25.43, 7.62) * mm, v(25.34, 7.7) * mm]});
            skFitSpline(sketch, "E273", {"points": [v(25.34, 7.7) * mm, v(25.25, 7.8) * mm, v(25.2, 7.95) * mm, v(25.13, 8.07) * mm]});
            skFitSpline(sketch, "E274", {"points": [v(25.13, 8.07) * mm, v(24.03, 7.62) * mm, v(22.9, 7.19) * mm, v(21.84, 6.62) * mm]});
            skFitSpline(sketch, "E275", {"points": [v(21.84, 6.62) * mm, v(22.09, 6.21) * mm, v(22.34, 5.82) * mm, v(22.57, 5.42) * mm]});
            skFitSpline(sketch, "E276", {"points": [v(22.57, 5.42) * mm, v(22.8, 5.02) * mm, v(23.04, 4.62) * mm, v(23.33, 4.2) * mm]});
            skFitSpline(sketch, "E277", {"points": [v(23.33, 4.2) * mm, v(23.52, 4.8) * mm, v(23.74, 5.34) * mm, v(23.84, 5.91) * mm]});
            skFitSpline(sketch, "E278", {"points": [v(23.84, 5.91) * mm, v(23.9, 6.23) * mm, v(24.12, 6.4) * mm, v(24.42, 6.35) * mm]});
            skFitSpline(sketch, "E279", {"points": [v(24.42, 6.35) * mm, v(24.68, 6.3) * mm, v(24.87, 6.04) * mm, v(24.8, 5.76) * mm]});
            skFitSpline(sketch, "E280", {"points": [v(24.8, 5.76) * mm, v(24.69, 5.3) * mm, v(24.56, 4.86) * mm, v(24.43, 4.42) * mm]});
            skFitSpline(sketch, "E281", {"points": [v(24.43, 4.42) * mm, v(24.39, 4.28) * mm, v(24.34, 4.13) * mm, v(24.29, 3.97) * mm]});
            skFitSpline(sketch, "E282", {"points": [v(24.29, 3.97) * mm, v(24.4, 3.96) * mm, v(24.47, 3.96) * mm, v(24.55, 3.96) * mm]});
            skFitSpline(sketch, "E283", {"points": [v(24.55, 3.96) * mm, v(24.86, 3.96) * mm, v(25.17, 3.96) * mm, v(25.49, 3.95) * mm]});
            skFitSpline(sketch, "E284", {"points": [v(25.49, 3.95) * mm, v(25.72, 3.95) * mm, v(25.96, 3.93) * mm, v(26.2, 3.9) * mm]});
            skFitSpline(sketch, "E285", {"points": [v(26.2, 3.9) * mm, v(26.46, 3.85) * mm, v(26.63, 3.6) * mm, v(26.6, 3.35) * mm]});
            skFitSpline(sketch, "E286", {"points": [v(26.6, 3.35) * mm, v(26.55, 3.08) * mm, v(26.32, 2.9) * mm, v(26.04, 2.94) * mm]});
            skFitSpline(sketch, "E287", {"points": [v(26.04, 2.94) * mm, v(25.95, 2.95) * mm, v(25.87, 2.97) * mm, v(25.78, 2.97) * mm]});
            skFitSpline(sketch, "E288", {"points": [v(25.78, 2.97) * mm, v(25.32, 2.98) * mm, v(24.85, 3) * mm, v(24.4, 3) * mm]});
            skFitSpline(sketch, "E289", {"points": [v(24.4, 3) * mm, v(24.35, 3) * mm, v(24.3, 2.98) * mm, v(24.22, 2.97) * mm]});
            skFitSpline(sketch, "E290", {"points": [v(13.41, -4.9) * mm, v(13.3, -6.12) * mm, v(13.2, -7.31) * mm, v(13.08, -8.5) * mm]});
            skFitSpline(sketch, "E291", {"points": [v(13.08, -8.5) * mm, v(13.51, -8.53) * mm, v(13.51, -8.53) * mm, v(13.81, -8.84) * mm]});
            skFitSpline(sketch, "E292", {"points": [v(13.81, -8.84) * mm, v(14.29, -9.35) * mm, v(14.78, -9.84) * mm, v(15.18, -10.41) * mm]});
            skFitSpline(sketch, "E293", {"points": [v(15.18, -10.41) * mm, v(15.3, -10.59) * mm, v(15.44, -10.63) * mm, v(15.65, -10.57) * mm]});
            skFitSpline(sketch, "E294", {"points": [v(15.65, -10.57) * mm, v(16.33, -10.34) * mm, v(17.03, -10.22) * mm, v(17.73, -10.1) * mm]});
            skFitSpline(sketch, "E295", {"points": [v(17.73, -10.1) * mm, v(18, -10.05) * mm, v(18.25, -10.02) * mm, v(18.44, -10.27) * mm]});
            skFitSpline(sketch, "E296", {"points": [v(18.44, -10.27) * mm, v(18.89, -9.64) * mm, v(20.15, -7.48) * mm, v(20.28, -7.1) * mm]});
            skFitSpline(sketch, "E297", {"points": [v(20.28, -7.1) * mm, v(19.4, -6.83) * mm, v(18.58, -6.35) * mm, v(17.67, -6.06) * mm]});
            skFitSpline(sketch, "E298", {"points": [v(17.67, -6.06) * mm, v(17.69, -6.14) * mm, v(17.7, -6.2) * mm, v(17.71, -6.24) * mm]});
            skFitSpline(sketch, "E299", {"points": [v(17.71, -6.24) * mm, v(17.9, -6.76) * mm, v(18.08, -7.28) * mm, v(18.27, -7.8) * mm]});
            skFitSpline(sketch, "E300", {"points": [v(18.27, -7.8) * mm, v(18.36, -8.02) * mm, v(18.3, -8.24) * mm, v(18.12, -8.37) * mm]});
            skFitSpline(sketch, "E301", {"points": [v(18.12, -8.37) * mm, v(17.94, -8.5) * mm, v(17.67, -8.5) * mm, v(17.5, -8.34) * mm]});
            skFitSpline(sketch, "E302", {"points": [v(17.5, -8.34) * mm, v(17.42, -8.26) * mm, v(17.36, -8.16) * mm, v(17.32, -8.06) * mm]});
            skFitSpline(sketch, "E303", {"points": [v(17.32, -8.06) * mm, v(17.2, -7.74) * mm, v(17.08, -7.42) * mm, v(16.96, -7.1) * mm]});
            skFitSpline(sketch, "E304", {"points": [v(16.96, -7.1) * mm, v(16.89, -6.88) * mm, v(16.82, -6.66) * mm, v(16.74, -6.42) * mm]});
            skFitSpline(sketch, "E305", {"points": [v(16.74, -6.42) * mm, v(16.65, -6.49) * mm, v(16.57, -6.54) * mm, v(16.5, -6.6) * mm]});
            skFitSpline(sketch, "E306", {"points": [v(16.5, -6.6) * mm, v(16.13, -6.85) * mm, v(15.76, -7.1) * mm, v(15.4, -7.36) * mm]});
            skFitSpline(sketch, "E307", {"points": [v(15.4, -7.36) * mm, v(15.3, -7.42) * mm, v(15.21, -7.47) * mm, v(15.11, -7.5) * mm]});
            skFitSpline(sketch, "E308", {"points": [v(15.11, -7.5) * mm, v(14.86, -7.59) * mm, v(14.6, -7.47) * mm, v(14.5, -7.24) * mm]});
            skFitSpline(sketch, "E309", {"points": [v(14.5, -7.24) * mm, v(14.4, -7) * mm, v(14.49, -6.76) * mm, v(14.71, -6.62) * mm]});
            skFitSpline(sketch, "E310", {"points": [v(14.71, -6.62) * mm, v(15.18, -6.3) * mm, v(15.65, -5.98) * mm, v(16.12, -5.66) * mm]});
            skFitSpline(sketch, "E311", {"points": [v(16.12, -5.66) * mm, v(16.14, -5.64) * mm, v(16.16, -5.6) * mm, v(16.2, -5.56) * mm]});
            skFitSpline(sketch, "E312", {"points": [v(16.2, -5.56) * mm, v(15.27, -5.34) * mm, v(14.36, -5.13) * mm, v(13.41, -4.9) * mm]});
            skFitSpline(sketch, "E313", {"points": [v(31.35, -9.1) * mm, v(31.36, -9.3) * mm, v(31.36, -9.49) * mm, v(31.38, -9.67) * mm]});
            skFitSpline(sketch, "E314", {"points": [v(31.38, -9.67) * mm, v(31.41, -10.03) * mm, v(31.45, -10.4) * mm, v(31.5, -10.76) * mm]});
            skFitSpline(sketch, "E315", {"points": [v(31.5, -10.76) * mm, v(31.52, -11) * mm, v(31.56, -11.22) * mm, v(31.59, -11.45) * mm]});
            skFitSpline(sketch, "E316", {"points": [v(31.59, -11.45) * mm, v(31.62, -11.73) * mm, v(31.43, -12) * mm, v(31.18, -12.04) * mm]});
            skFitSpline(sketch, "E317", {"points": [v(31.18, -12.04) * mm, v(30.88, -12.08) * mm, v(30.64, -11.9) * mm, v(30.6, -11.6) * mm]});
            skFitSpline(sketch, "E318", {"points": [v(30.6, -11.6) * mm, v(30.56, -11.23) * mm, v(30.54, -10.87) * mm, v(30.5, -10.5) * mm]});
            skFitSpline(sketch, "E319", {"points": [v(30.5, -10.5) * mm, v(30.46, -10.13) * mm, v(30.42, -9.75) * mm, v(30.38, -9.35) * mm]});
            skFitSpline(sketch, "E320", {"points": [v(30.38, -9.35) * mm, v(29.8, -9.5) * mm, v(29.22, -9.66) * mm, v(28.65, -9.8) * mm]});
            skFitSpline(sketch, "E321", {"points": [v(28.65, -9.8) * mm, v(28.39, -9.87) * mm, v(28.13, -9.94) * mm, v(27.86, -10) * mm]});
            skFitSpline(sketch, "E322", {"points": [v(27.86, -10) * mm, v(27.57, -10.05) * mm, v(27.3, -10.04) * mm, v(27.02, -9.92) * mm]});
            skFitSpline(sketch, "E323", {"points": [v(27.02, -9.92) * mm, v(26.13, -9.54) * mm, v(25.24, -9.16) * mm, v(24.35, -8.8) * mm]});
            skFitSpline(sketch, "E324", {"points": [v(24.35, -8.8) * mm, v(23.83, -8.58) * mm, v(23.3, -8.37) * mm, v(22.73, -8.14) * mm]});
            skFitSpline(sketch, "E325", {"points": [v(22.73, -8.14) * mm, v(22.8, -8.23) * mm, v(22.84, -8.29) * mm, v(22.88, -8.33) * mm]});
            skFitSpline(sketch, "E326", {"points": [v(22.88, -8.33) * mm, v(23.42, -8.88) * mm, v(23.96, -9.43) * mm, v(24.5, -9.98) * mm]});
            skFitSpline(sketch, "E327", {"points": [v(24.5, -9.98) * mm, v(24.8, -10.29) * mm, v(25.11, -10.6) * mm, v(25.43, -10.9) * mm]});
            skFitSpline(sketch, "E328", {"points": [v(25.43, -10.9) * mm, v(25.51, -10.98) * mm, v(25.62, -11.06) * mm, v(25.73, -11.08) * mm]});
            skFitSpline(sketch, "E329", {"points": [v(25.73, -11.08) * mm, v(26.23, -11.2) * mm, v(26.73, -11.3) * mm, v(27.23, -11.41) * mm]});
            skFitSpline(sketch, "E330", {"points": [v(27.23, -11.41) * mm, v(27.43, -11.45) * mm, v(27.64, -11.47) * mm, v(27.84, -11.51) * mm]});
            skFitSpline(sketch, "E331", {"points": [v(27.84, -11.51) * mm, v(27.94, -11.53) * mm, v(28.04, -11.56) * mm, v(28.13, -11.61) * mm]});
            skFitSpline(sketch, "E332", {"points": [v(28.13, -11.61) * mm, v(28.34, -11.72) * mm, v(28.42, -11.95) * mm, v(28.36, -12.17) * mm]});
            skFitSpline(sketch, "E333", {"points": [v(28.36, -12.17) * mm, v(28.3, -12.37) * mm, v(28.12, -12.51) * mm, v(27.89, -12.5) * mm]});
            skFitSpline(sketch, "E334", {"points": [v(27.89, -12.5) * mm, v(27.67, -12.48) * mm, v(27.46, -12.44) * mm, v(27.25, -12.4) * mm]});
            skFitSpline(sketch, "E335", {"points": [v(27.25, -12.4) * mm, v(26.87, -12.33) * mm, v(26.5, -12.26) * mm, v(26.12, -12.19) * mm]});
            skFitSpline(sketch, "E336", {"points": [v(26.12, -12.19) * mm, v(26.08, -12.18) * mm, v(26.03, -12.18) * mm, v(25.97, -12.18) * mm]});
            skFitSpline(sketch, "E337", {"points": [v(25.97, -12.18) * mm, v(25.54, -13.12) * mm, v(25.11, -14.05) * mm, v(24.42, -14.84) * mm]});
            skFitSpline(sketch, "E338", {"points": [v(24.42, -14.84) * mm, v(24.63, -14.95) * mm, v(24.8, -15.05) * mm, v(25, -15.14) * mm]});
            skFitSpline(sketch, "E339", {"points": [v(25, -15.14) * mm, v(25.34, -15.32) * mm, v(25.69, -15.5) * mm, v(26.04, -15.67) * mm]});
            skFitSpline(sketch, "E340", {"points": [v(26.04, -15.67) * mm, v(26.3, -15.8) * mm, v(26.4, -16.08) * mm, v(26.28, -16.33) * mm]});
            skFitSpline(sketch, "E341", {"points": [v(26.28, -16.33) * mm, v(26.15, -16.6) * mm, v(25.85, -16.69) * mm, v(25.59, -16.55) * mm]});
            skFitSpline(sketch, "E342", {"points": [v(25.59, -16.55) * mm, v(25.17, -16.33) * mm, v(24.76, -16.1) * mm, v(24.34, -15.9) * mm]});
            skFitSpline(sketch, "E343", {"points": [v(24.34, -15.9) * mm, v(24.22, -15.83) * mm, v(24.08, -15.8) * mm, v(23.96, -15.76) * mm]});
            skFitSpline(sketch, "E344", {"points": [v(23.96, -15.76) * mm, v(23.7, -16.01) * mm, v(23.6, -16.33) * mm, v(23.45, -16.62) * mm]});
            skFitSpline(sketch, "E345", {"points": [v(23.45, -16.62) * mm, v(23.31, -16.88) * mm, v(23.2, -17.15) * mm, v(23.06, -17.41) * mm]});
            skFitSpline(sketch, "E346", {"points": [v(23.06, -17.41) * mm, v(22.93, -17.64) * mm, v(22.64, -17.72) * mm, v(22.41, -17.6) * mm]});
            skFitSpline(sketch, "E347", {"points": [v(22.41, -17.6) * mm, v(22.17, -17.48) * mm, v(22.07, -17.2) * mm, v(22.19, -16.95) * mm]});
            skFitSpline(sketch, "E348", {"points": [v(22.19, -16.95) * mm, v(22.34, -16.63) * mm, v(22.5, -16.32) * mm, v(22.66, -16) * mm]});
            skFitSpline(sketch, "E349", {"points": [v(22.66, -16) * mm, v(22.78, -15.78) * mm, v(22.9, -15.56) * mm, v(23.01, -15.33) * mm]});
            skFitSpline(sketch, "E350", {"points": [v(23.01, -15.33) * mm, v(22.54, -15.15) * mm, v(22.05, -15) * mm, v(21.59, -14.78) * mm]});
            skFitSpline(sketch, "E351", {"points": [v(21.59, -14.78) * mm, v(21.11, -14.57) * mm, v(20.66, -14.3) * mm, v(20.19, -14.06) * mm]});
            skFitSpline(sketch, "E352", {"points": [v(20.19, -14.06) * mm, v(20.15, -14.1) * mm, v(20.1, -14.13) * mm, v(20.06, -14.18) * mm]});
            skFitSpline(sketch, "E353", {"points": [v(20.06, -14.18) * mm, v(19.68, -14.58) * mm, v(19.3, -14.98) * mm, v(18.92, -15.38) * mm]});
            skFitSpline(sketch, "E354", {"points": [v(18.92, -15.38) * mm, v(18.73, -15.58) * mm, v(18.46, -15.6) * mm, v(18.25, -15.44) * mm]});
            skFitSpline(sketch, "E355", {"points": [v(18.25, -15.44) * mm, v(18.06, -15.28) * mm, v(18.02, -15.01) * mm, v(18.16, -14.79) * mm]});
            skFitSpline(sketch, "E356", {"points": [v(18.16, -14.79) * mm, v(18.2, -14.7) * mm, v(18.27, -14.63) * mm, v(18.34, -14.57) * mm]});
            skFitSpline(sketch, "E357", {"points": [v(18.34, -14.57) * mm, v(18.73, -14.15) * mm, v(19.12, -13.74) * mm, v(19.51, -13.33) * mm]});
            skFitSpline(sketch, "E358", {"points": [v(19.51, -13.33) * mm, v(19.58, -13.26) * mm, v(19.64, -13.19) * mm, v(19.7, -13.11) * mm]});
            skFitSpline(sketch, "E359", {"points": [v(19.7, -13.11) * mm, v(19.82, -12.97) * mm, v(19.88, -12.8) * mm, v(19.9, -12.62) * mm]});
            skFitSpline(sketch, "E360", {"points": [v(19.9, -12.62) * mm, v(20.06, -11.57) * mm, v(20.24, -10.52) * mm, v(20.4, -9.47) * mm]});
            skFitSpline(sketch, "E361", {"points": [v(20.4, -9.47) * mm, v(20.43, -9.3) * mm, v(20.44, -9.12) * mm, v(20.47, -8.91) * mm]});
            skFitSpline(sketch, "E362", {"points": [v(20.47, -8.91) * mm, v(20.43, -8.94) * mm, v(20.4, -8.95) * mm, v(20.4, -8.97) * mm]});
            skFitSpline(sketch, "E363", {"points": [v(20.4, -8.97) * mm, v(20.03, -9.56) * mm, v(19.67, -10.16) * mm, v(19.3, -10.75) * mm]});
            skFitSpline(sketch, "E364", {"points": [v(19.3, -10.75) * mm, v(19.01, -11.23) * mm, v(18.72, -11.72) * mm, v(18.42, -12.2) * mm]});
            skFitSpline(sketch, "E365", {"points": [v(18.42, -12.2) * mm, v(18.29, -12.41) * mm, v(18.14, -12.61) * mm, v(18.03, -12.83) * mm]});
            skFitSpline(sketch, "E366", {"points": [v(18.03, -12.83) * mm, v(17.89, -13.12) * mm, v(17.65, -13.28) * mm, v(17.38, -13.4) * mm]});
            skFitSpline(sketch, "E367", {"points": [v(17.38, -13.4) * mm, v(17, -13.57) * mm, v(16.6, -13.71) * mm, v(16.22, -13.87) * mm]});
            skFitSpline(sketch, "E368", {"points": [v(16.22, -13.87) * mm, v(15.81, -14.03) * mm, v(15.4, -14.19) * mm, v(14.98, -14.36) * mm]});
            skFitSpline(sketch, "E369", {"points": [v(14.98, -14.36) * mm, v(15.17, -14.69) * mm, v(15.35, -15) * mm, v(15.53, -15.33) * mm]});
            skFitSpline(sketch, "E370", {"points": [v(15.53, -15.33) * mm, v(15.72, -15.65) * mm, v(15.92, -15.97) * mm, v(16.1, -16.3) * mm]});
            skFitSpline(sketch, "E371", {"points": [v(16.1, -16.3) * mm, v(16.25, -16.56) * mm, v(16.18, -16.84) * mm, v(15.95, -16.98) * mm]});
            skFitSpline(sketch, "E372", {"points": [v(15.95, -16.98) * mm, v(15.7, -17.13) * mm, v(15.4, -17.04) * mm, v(15.25, -16.77) * mm]});
            skFitSpline(sketch, "E373", {"points": [v(15.25, -16.77) * mm, v(14.98, -16.31) * mm, v(14.71, -15.85) * mm, v(14.45, -15.38) * mm]});
            skFitSpline(sketch, "E374", {"points": [v(14.45, -15.38) * mm, v(14.32, -15.16) * mm, v(14.19, -14.95) * mm, v(14.05, -14.71) * mm]});
            skFitSpline(sketch, "E375", {"points": [v(14.05, -14.71) * mm, v(13.82, -14.8) * mm, v(13.62, -14.89) * mm, v(13.42, -14.98) * mm]});
            skFitSpline(sketch, "E376", {"points": [v(13.42, -14.98) * mm, v(13.1, -15.11) * mm, v(12.77, -15.25) * mm, v(12.45, -15.4) * mm]});
            skFitSpline(sketch, "E377", {"points": [v(12.45, -15.4) * mm, v(12.3, -15.47) * mm, v(12.14, -15.55) * mm, v(11.97, -15.62) * mm]});
            skFitSpline(sketch, "E378", {"points": [v(11.97, -15.62) * mm, v(11.86, -15.66) * mm, v(11.75, -15.7) * mm, v(11.63, -15.71) * mm]});
            skFitSpline(sketch, "E379", {"points": [v(11.63, -15.71) * mm, v(11.38, -15.73) * mm, v(11.22, -15.6) * mm, v(11.15, -15.37) * mm]});
            skFitSpline(sketch, "E380", {"points": [v(11.15, -15.37) * mm, v(11.09, -15.15) * mm, v(11.18, -14.93) * mm, v(11.38, -14.82) * mm]});
            skFitSpline(sketch, "E381", {"points": [v(11.38, -14.82) * mm, v(11.58, -14.71) * mm, v(11.79, -14.62) * mm, v(11.99, -14.53) * mm]});
            skFitSpline(sketch, "E382", {"points": [v(11.99, -14.53) * mm, v(12.45, -14.33) * mm, v(12.91, -14.13) * mm, v(13.37, -13.93) * mm]});
            skFitSpline(sketch, "E383", {"points": [v(13.37, -13.93) * mm, v(13.4, -13.92) * mm, v(13.44, -13.9) * mm, v(13.49, -13.86) * mm]});
            skFitSpline(sketch, "E384", {"points": [v(13.49, -13.86) * mm, v(13.3, -13.55) * mm, v(13.1, -13.25) * mm, v(12.91, -12.95) * mm]});
            skFitSpline(sketch, "E385", {"points": [v(12.91, -12.95) * mm, v(12.69, -12.6) * mm, v(12.48, -12.24) * mm, v(12.24, -11.9) * mm]});
            skFitSpline(sketch, "E386", {"points": [v(12.24, -11.9) * mm, v(11.93, -11.47) * mm, v(11.9, -11) * mm, v(11.94, -10.5) * mm]});
            skFitSpline(sketch, "E387", {"points": [v(11.94, -10.5) * mm, v(11.98, -10.15) * mm, v(12, -9.8) * mm, v(12.03, -9.44) * mm]});
            skFitSpline(sketch, "E388", {"points": [v(12.03, -9.44) * mm, v(12.06, -9.07) * mm, v(12.1, -8.7) * mm, v(12.13, -8.34) * mm]});
            skFitSpline(sketch, "E389", {"points": [v(12.13, -8.34) * mm, v(12.16, -7.92) * mm, v(12.2, -7.5) * mm, v(12.22, -7.08) * mm]});
            skFitSpline(sketch, "E390", {"points": [v(12.22, -7.08) * mm, v(12.25, -6.8) * mm, v(12.27, -6.54) * mm, v(12.3, -6.2) * mm]});
            skFitSpline(sketch, "E391", {"points": [v(12.3, -6.2) * mm, v(12.23, -6.3) * mm, v(12.2, -6.36) * mm, v(12.16, -6.42) * mm]});
            skFitSpline(sketch, "E392", {"points": [v(12.16, -6.42) * mm, v(11.8, -7.1) * mm, v(11.45, -7.78) * mm, v(11.1, -8.46) * mm]});
            skFitSpline(sketch, "E393", {"points": [v(11.1, -8.46) * mm, v(10.9, -8.84) * mm, v(10.73, -9.22) * mm, v(10.52, -9.6) * mm]});
            skFitSpline(sketch, "E394", {"points": [v(10.52, -9.6) * mm, v(10.4, -9.8) * mm, v(10.38, -10) * mm, v(10.4, -10.21) * mm]});
            skFitSpline(sketch, "E395", {"points": [v(10.4, -10.21) * mm, v(10.49, -10.84) * mm, v(10.58, -11.46) * mm, v(10.66, -12.09) * mm]});
            skFitSpline(sketch, "E396", {"points": [v(10.66, -12.09) * mm, v(10.67, -12.19) * mm, v(10.68, -12.3) * mm, v(10.67, -12.4) * mm]});
            skFitSpline(sketch, "E397", {"points": [v(10.67, -12.4) * mm, v(10.64, -12.65) * mm, v(10.42, -12.84) * mm, v(10.18, -12.83) * mm]});
            skFitSpline(sketch, "E398", {"points": [v(10.18, -12.83) * mm, v(9.94, -12.82) * mm, v(9.75, -12.64) * mm, v(9.71, -12.4) * mm]});
            skFitSpline(sketch, "E399", {"points": [v(9.71, -12.4) * mm, v(9.63, -11.8) * mm, v(9.55, -11.2) * mm, v(9.46, -10.57) * mm]});
            skFitSpline(sketch, "E400", {"points": [v(9.46, -10.57) * mm, v(8.45, -10.43) * mm, v(7.41, -10.33) * mm, v(6.42, -9.9) * mm]});
            skFitSpline(sketch, "E401", {"points": [v(6.42, -9.9) * mm, v(6.41, -10.02) * mm, v(6.41, -10.11) * mm, v(6.4, -10.2) * mm]});
            skFitSpline(sketch, "E402", {"points": [v(6.4, -10.2) * mm, v(6.33, -10.62) * mm, v(6.25, -11.03) * mm, v(6.18, -11.45) * mm]});
            skFitSpline(sketch, "E403", {"points": [v(6.18, -11.45) * mm, v(6.17, -11.52) * mm, v(6.17, -11.6) * mm, v(6.16, -11.66) * mm]});
            skFitSpline(sketch, "E404", {"points": [v(6.16, -11.66) * mm, v(6.12, -11.98) * mm, v(5.88, -12.18) * mm, v(5.58, -12.13) * mm]});
            skFitSpline(sketch, "E405", {"points": [v(5.58, -12.13) * mm, v(5.3, -12.1) * mm, v(5.12, -11.81) * mm, v(5.17, -11.5) * mm]});
            skFitSpline(sketch, "E406", {"points": [v(5.17, -11.5) * mm, v(5.26, -11.03) * mm, v(5.35, -10.55) * mm, v(5.43, -10.07) * mm]});
            skFitSpline(sketch, "E407", {"points": [v(5.43, -10.07) * mm, v(5.45, -9.97) * mm, v(5.41, -9.86) * mm, v(5.4, -9.74) * mm]});
            skFitSpline(sketch, "E408", {"points": [v(5.4, -9.74) * mm, v(5.08, -9.6) * mm, v(4.74, -9.59) * mm, v(4.42, -9.53) * mm]});
            skFitSpline(sketch, "E409", {"points": [v(4.42, -9.53) * mm, v(4.14, -9.48) * mm, v(3.86, -9.46) * mm, v(3.6, -9.4) * mm]});
            skFitSpline(sketch, "E410", {"points": [v(3.6, -9.4) * mm, v(3.3, -9.35) * mm, v(3.14, -9.1) * mm, v(3.2, -8.82) * mm]});
            skFitSpline(sketch, "E411", {"points": [v(3.2, -8.82) * mm, v(3.25, -8.56) * mm, v(3.5, -8.4) * mm, v(3.78, -8.44) * mm]});
            skFitSpline(sketch, "E412", {"points": [v(3.78, -8.44) * mm, v(4.28, -8.51) * mm, v(4.78, -8.6) * mm, v(5.29, -8.67) * mm]});
            skFitSpline(sketch, "E413", {"points": [v(5.29, -8.67) * mm, v(5.37, -8.68) * mm, v(5.46, -8.71) * mm, v(5.57, -8.74) * mm]});
            skFitSpline(sketch, "E414", {"points": [v(5.57, -8.74) * mm, v(5.47, -7.68) * mm, v(5.69, -6.66) * mm, v(5.89, -5.64) * mm]});
            skFitSpline(sketch, "E415", {"points": [v(5.89, -5.64) * mm, v(5.52, -5.47) * mm, v(5.16, -5.3) * mm, v(4.8, -5.12) * mm]});
            skFitSpline(sketch, "E416", {"points": [v(4.8, -5.12) * mm, v(4.6, -5.03) * mm, v(4.41, -4.94) * mm, v(4.22, -4.84) * mm]});
            skFitSpline(sketch, "E417", {"points": [v(4.22, -4.84) * mm, v(4, -4.72) * mm, v(3.89, -4.5) * mm, v(3.96, -4.26) * mm]});
            skFitSpline(sketch, "E418", {"points": [v(3.96, -4.26) * mm, v(4.04, -4.01) * mm, v(4.25, -3.88) * mm, v(4.52, -3.93) * mm]});
            skFitSpline(sketch, "E419", {"points": [v(4.52, -3.93) * mm, v(4.63, -3.95) * mm, v(4.74, -4) * mm, v(4.85, -4.06) * mm]});
            skFitSpline(sketch, "E420", {"points": [v(4.85, -4.06) * mm, v(5.35, -4.3) * mm, v(5.85, -4.53) * mm, v(6.34, -4.77) * mm]});
            skFitSpline(sketch, "E421", {"points": [v(6.34, -4.77) * mm, v(6.42, -4.8) * mm, v(6.5, -4.83) * mm, v(6.59, -4.87) * mm]});
            skFitSpline(sketch, "E422", {"points": [v(6.59, -4.87) * mm, v(6.78, -4.96) * mm, v(6.98, -4.96) * mm, v(7.2, -4.93) * mm]});
            skFitSpline(sketch, "E423", {"points": [v(7.2, -4.93) * mm, v(8.33, -4.73) * mm, v(9.48, -4.55) * mm, v(10.62, -4.36) * mm]});
            skFitSpline(sketch, "E424", {"points": [v(10.62, -4.36) * mm, v(10.7, -4.35) * mm, v(10.79, -4.33) * mm, v(10.92, -4.3) * mm]});
            skFitSpline(sketch, "E425", {"points": [v(10.92, -4.3) * mm, v(10.68, -4.24) * mm, v(10.5, -4.2) * mm, v(10.32, -4.15) * mm]});
            skFitSpline(sketch, "E426", {"points": [v(10.32, -4.15) * mm, v(9.2, -3.89) * mm, v(8.1, -3.62) * mm, v(6.99, -3.35) * mm]});
            skFitSpline(sketch, "E427", {"points": [v(6.99, -3.35) * mm, v(6.79, -3.3) * mm, v(6.59, -3.24) * mm, v(6.38, -3.21) * mm]});
            skFitSpline(sketch, "E428", {"points": [v(6.38, -3.21) * mm, v(6.06, -3.17) * mm, v(5.83, -2.98) * mm, v(5.62, -2.75) * mm]});
            skFitSpline(sketch, "E429", {"points": [v(5.62, -2.75) * mm, v(5.35, -2.44) * mm, v(5.09, -2.12) * mm, v(4.82, -1.8) * mm]});
            skFitSpline(sketch, "E430", {"points": [v(4.82, -1.8) * mm, v(4.55, -1.46) * mm, v(4.27, -1.13) * mm, v(3.98, -0.78) * mm]});
            skFitSpline(sketch, "E431", {"points": [v(3.98, -0.78) * mm, v(3.72, -1.07) * mm, v(3.46, -1.36) * mm, v(3.2, -1.65) * mm]});
            skFitSpline(sketch, "E432", {"points": [v(3.2, -1.65) * mm, v(2.95, -1.93) * mm, v(2.71, -2.2) * mm, v(2.46, -2.47) * mm]});
            skFitSpline(sketch, "E433", {"points": [v(2.46, -2.47) * mm, v(2.27, -2.67) * mm, v(2.01, -2.69) * mm, v(1.8, -2.53) * mm]});
            skFitSpline(sketch, "E434", {"points": [v(1.8, -2.53) * mm, v(1.61, -2.38) * mm, v(1.56, -2.12) * mm, v(1.7, -1.89) * mm]});
            skFitSpline(sketch, "E435", {"points": [v(1.7, -1.89) * mm, v(1.73, -1.82) * mm, v(1.8, -1.76) * mm, v(1.84, -1.7) * mm]});
            skFitSpline(sketch, "E436", {"points": [v(1.84, -1.7) * mm, v(2.05, -1.47) * mm, v(2.26, -1.24) * mm, v(2.47, -1) * mm]});
            skFitSpline(sketch, "E437", {"points": [v(2.47, -1) * mm, v(2.7, -0.74) * mm, v(2.94, -0.48) * mm, v(3.17, -0.22) * mm]});
            skFitSpline(sketch, "E438", {"points": [v(3.17, -0.22) * mm, v(3.23, -0.15) * mm, v(3.28, -0.09) * mm, v(3.35, 0) * mm]});
            skFitSpline(sketch, "E439", {"points": [v(3.35, 0) * mm, v(3.2, 0.18) * mm, v(3.04, 0.37) * mm, v(2.89, 0.54) * mm]});
            skFitSpline(sketch, "E440", {"points": [v(2.89, 0.54) * mm, v(2.66, 0.8) * mm, v(2.43, 1.06) * mm, v(2.2, 1.31) * mm]});
            skFitSpline(sketch, "E441", {"points": [v(2.2, 1.31) * mm, v(2.1, 1.44) * mm, v(1.97, 1.56) * mm, v(1.86, 1.68) * mm]});
            skFitSpline(sketch, "E442", {"points": [v(1.86, 1.68) * mm, v(1.8, 1.75) * mm, v(1.74, 1.81) * mm, v(1.7, 1.89) * mm]});
            skFitSpline(sketch, "E443", {"points": [v(1.7, 1.89) * mm, v(1.56, 2.11) * mm, v(1.61, 2.38) * mm, v(1.8, 2.53) * mm]});
            skFitSpline(sketch, "E444", {"points": [v(1.8, 2.53) * mm, v(2, 2.69) * mm, v(2.27, 2.67) * mm, v(2.46, 2.48) * mm]});
            skFitSpline(sketch, "E445", {"points": [v(2.46, 2.48) * mm, v(2.71, 2.2) * mm, v(2.95, 1.93) * mm, v(3.2, 1.66) * mm]});
            skFitSpline(sketch, "E446", {"points": [v(3.2, 1.66) * mm, v(3.45, 1.37) * mm, v(3.71, 1.08) * mm, v(3.98, 0.78) * mm]});
            skFitSpline(sketch, "E447", {"points": [v(3.98, 0.78) * mm, v(4.47, 1.38) * mm, v(4.95, 1.96) * mm, v(5.43, 2.53) * mm]});
            skFitSpline(sketch, "E448", {"points": [v(5.43, 2.53) * mm, v(5.54, 2.67) * mm, v(5.67, 2.8) * mm, v(5.79, 2.92) * mm]});
            skFitSpline(sketch, "E449", {"points": [v(5.79, 2.92) * mm, v(6, 3.14) * mm, v(6.28, 3.2) * mm, v(6.56, 3.26) * mm]});
            skFitSpline(sketch, "E450", {"points": [v(6.56, 3.26) * mm, v(7.1, 3.4) * mm, v(7.65, 3.53) * mm, v(8.2, 3.66) * mm]});
            skFitSpline(sketch, "E451", {"points": [v(8.2, 3.66) * mm, v(8.56, 3.74) * mm, v(8.93, 3.8) * mm, v(9.3, 3.9) * mm]});
            skFitSpline(sketch, "E452", {"points": [v(9.3, 3.9) * mm, v(9.82, 4.02) * mm, v(10.34, 4.16) * mm, v(10.87, 4.32) * mm]});
            skFitSpline(sketch, "E453", {"points": [v(10.87, 4.32) * mm, v(10.51, 4.38) * mm, v(10.15, 4.45) * mm, v(9.8, 4.5) * mm]});
            skFitSpline(sketch, "E454", {"points": [v(9.8, 4.5) * mm, v(9.21, 4.6) * mm, v(8.63, 4.7) * mm, v(8.05, 4.8) * mm]});
            skFitSpline(sketch, "E455", {"points": [v(8.05, 4.8) * mm, v(7.7, 4.85) * mm, v(7.37, 4.9) * mm, v(7.03, 4.94) * mm]});
            skFitSpline(sketch, "E456", {"points": [v(7.03, 4.94) * mm, v(6.93, 4.95) * mm, v(6.82, 4.95) * mm, v(6.73, 4.9) * mm]});
            skFitSpline(sketch, "E457", {"points": [v(6.73, 4.9) * mm, v(6.35, 4.76) * mm, v(5.97, 4.6) * mm, v(5.6, 4.43) * mm]});
            skFitSpline(sketch, "E458", {"points": [v(5.6, 4.43) * mm, v(5.34, 4.31) * mm, v(5.1, 4.17) * mm, v(4.83, 4.04) * mm]});
            skFitSpline(sketch, "E459", {"points": [v(4.83, 4.04) * mm, v(4.75, 4) * mm, v(4.67, 3.97) * mm, v(4.6, 3.94) * mm]});
            skFitSpline(sketch, "E460", {"points": [v(4.6, 3.94) * mm, v(4.32, 3.86) * mm, v(4.06, 3.98) * mm, v(3.97, 4.24) * mm]});
            skFitSpline(sketch, "E461", {"points": [v(3.97, 4.24) * mm, v(3.88, 4.48) * mm, v(3.99, 4.73) * mm, v(4.24, 4.85) * mm]});
            skFitSpline(sketch, "E462", {"points": [v(4.24, 4.85) * mm, v(4.76, 5.1) * mm, v(5.28, 5.34) * mm, v(5.8, 5.6) * mm]});
            skFitSpline(sketch, "E463", {"points": [v(5.8, 5.6) * mm, v(5.82, 5.6) * mm, v(5.85, 5.62) * mm, v(5.88, 5.64) * mm]});
            skFitSpline(sketch, "E464", {"points": [v(5.88, 5.64) * mm, v(5.7, 6.66) * mm, v(5.47, 7.68) * mm, v(5.57, 8.72) * mm]});
            skFitSpline(sketch, "E465", {"points": [v(5.57, 8.72) * mm, v(5.12, 8.65) * mm, v(4.69, 8.58) * mm, v(4.25, 8.51) * mm]});
            skFitSpline(sketch, "E466", {"points": [v(4.25, 8.51) * mm, v(4.08, 8.49) * mm, v(3.9, 8.45) * mm, v(3.74, 8.43) * mm]});
            skFitSpline(sketch, "E467", {"points": [v(3.74, 8.43) * mm, v(3.48, 8.4) * mm, v(3.23, 8.58) * mm, v(3.2, 8.83) * mm]});
            skFitSpline(sketch, "E468", {"points": [v(3.2, 8.83) * mm, v(3.15, 9.1) * mm, v(3.31, 9.35) * mm, v(3.58, 9.4) * mm]});
            skFitSpline(sketch, "E469", {"points": [v(3.58, 9.4) * mm, v(3.79, 9.45) * mm, v(4, 9.48) * mm, v(4.2, 9.5) * mm]});
            skFitSpline(sketch, "E470", {"points": [v(4.2, 9.5) * mm, v(4.44, 9.54) * mm, v(4.69, 9.56) * mm, v(4.93, 9.6) * mm]});
            skFitSpline(sketch, "E471", {"points": [v(4.93, 9.6) * mm, v(5.09, 9.63) * mm, v(5.24, 9.68) * mm, v(5.38, 9.72) * mm]});
            skFitSpline(sketch, "E472", {"points": [v(5.38, 9.72) * mm, v(5.45, 9.9) * mm, v(5.44, 10.06) * mm, v(5.4, 10.23) * mm]});
            skFitSpline(sketch, "E473", {"points": [v(5.4, 10.23) * mm, v(5.34, 10.5) * mm, v(5.31, 10.8) * mm, v(5.27, 11.08) * mm]});
            skFitSpline(sketch, "E474", {"points": [v(5.27, 11.08) * mm, v(5.24, 11.22) * mm, v(5.2, 11.36) * mm, v(5.18, 11.5) * mm]});
            skFitSpline(sketch, "E475", {"points": [v(5.18, 11.5) * mm, v(5.11, 11.8) * mm, v(5.3, 12.09) * mm, v(5.57, 12.13) * mm]});
            skFitSpline(sketch, "E476", {"points": [v(5.57, 12.13) * mm, v(5.87, 12.19) * mm, v(6.12, 11.98) * mm, v(6.16, 11.65) * mm]});
            skFitSpline(sketch, "E477", {"points": [v(6.16, 11.65) * mm, v(6.23, 11.2) * mm, v(6.3, 10.77) * mm, v(6.37, 10.33) * mm]});
            skFitSpline(sketch, "E478", {"points": [v(6.37, 10.33) * mm, v(6.4, 10.2) * mm, v(6.4, 10.08) * mm, v(6.42, 9.94) * mm]});
            skFitSpline(sketch, "E479", {"points": [v(6.42, 9.94) * mm, v(6.92, 10.08) * mm, v(7.4, 10.24) * mm, v(7.91, 10.34) * mm]});
            skFitSpline(sketch, "E480", {"points": [v(7.91, 10.34) * mm, v(8.42, 10.44) * mm, v(8.93, 10.5) * mm, v(9.47, 10.57) * mm]});
            skFitSpline(sketch, "E481", {"points": [v(9.47, 10.57) * mm, v(9.49, 10.72) * mm, v(9.5, 10.88) * mm, v(9.52, 11.04) * mm]});
            skFitSpline(sketch, "E482", {"points": [v(9.52, 11.04) * mm, v(9.59, 11.5) * mm, v(9.65, 11.98) * mm, v(9.72, 12.46) * mm]});
            skFitSpline(sketch, "E483", {"points": [v(9.72, 12.46) * mm, v(9.76, 12.68) * mm, v(9.99, 12.84) * mm, v(10.22, 12.83) * mm]});
            skFitSpline(sketch, "E484", {"points": [v(10.22, 12.83) * mm, v(10.45, 12.81) * mm, v(10.64, 12.63) * mm, v(10.67, 12.4) * mm]});
            skFitSpline(sketch, "E485", {"points": [v(10.67, 12.4) * mm, v(10.68, 12.3) * mm, v(10.67, 12.18) * mm, v(10.66, 12.07) * mm]});
            skFitSpline(sketch, "E486", {"points": [v(10.66, 12.07) * mm, v(10.57, 11.45) * mm, v(10.48, 10.82) * mm, v(10.4, 10.2) * mm]});
            skFitSpline(sketch, "E487", {"points": [v(10.4, 10.2) * mm, v(10.38, 10) * mm, v(10.41, 9.8) * mm, v(10.52, 9.6) * mm]});
            skFitSpline(sketch, "E488", {"points": [v(10.52, 9.6) * mm, v(11.06, 8.56) * mm, v(11.6, 7.51) * mm, v(12.13, 6.47) * mm]});
            skFitSpline(sketch, "E489", {"points": [v(12.13, 6.47) * mm, v(12.17, 6.4) * mm, v(12.22, 6.32) * mm, v(12.3, 6.26) * mm]});
            skFitSpline(sketch, "E490", {"points": [v(12.3, 6.26) * mm, v(12.23, 7.05) * mm, v(12.16, 7.85) * mm, v(12.09, 8.64) * mm]});
            skFitSpline(sketch, "E491", {"points": [v(12.09, 8.64) * mm, v(12.06, 8.95) * mm, v(12.04, 9.25) * mm, v(12.02, 9.55) * mm]});
            skFitSpline(sketch, "E492", {"points": [v(12.02, 9.55) * mm, v(11.99, 10) * mm, v(11.97, 10.44) * mm, v(11.93, 10.89) * mm]});
            skFitSpline(sketch, "E493", {"points": [v(11.93, 10.89) * mm, v(11.9, 11.17) * mm, v(11.97, 11.43) * mm, v(12.1, 11.66) * mm]});
            skFitSpline(sketch, "E494", {"points": [v(12.1, 11.66) * mm, v(12.36, 12.09) * mm, v(12.63, 12.5) * mm, v(12.9, 12.92) * mm]});
            skFitSpline(sketch, "E495", {"points": [v(12.9, 12.92) * mm, v(13.09, 13.23) * mm, v(13.28, 13.54) * mm, v(13.5, 13.87) * mm]});
            skFitSpline(sketch, "E496", {"points": [v(13.5, 13.87) * mm, v(13.21, 14) * mm, v(12.95, 14.13) * mm, v(12.68, 14.25) * mm]});
            skFitSpline(sketch, "E497", {"points": [v(12.68, 14.25) * mm, v(12.27, 14.43) * mm, v(11.86, 14.6) * mm, v(11.45, 14.78) * mm]});
            skFitSpline(sketch, "E498", {"points": [v(11.45, 14.78) * mm, v(11.2, 14.9) * mm, v(11.08, 15.13) * mm, v(11.15, 15.36) * mm]});
            skFitSpline(sketch, "E499", {"points": [v(11.15, 15.36) * mm, v(11.25, 15.72) * mm, v(11.58, 15.79) * mm, v(11.86, 15.67) * mm]});
            skFitSpline(sketch, "E500", {"points": [v(11.86, 15.67) * mm, v(12.36, 15.47) * mm, v(12.84, 15.24) * mm, v(13.33, 15.02) * mm]});
            skFitSpline(sketch, "E501", {"points": [v(13.33, 15.02) * mm, v(13.55, 14.92) * mm, v(13.78, 14.82) * mm, v(14.03, 14.71) * mm]});
            skFitSpline(sketch, "E502", {"points": [v(14.03, 14.71) * mm, v(14.08, 14.79) * mm, v(14.14, 14.85) * mm, v(14.18, 14.93) * mm]});
            skFitSpline(sketch, "E503", {"points": [v(14.18, 14.93) * mm, v(14.46, 15.4) * mm, v(14.75, 15.87) * mm, v(15.03, 16.35) * mm]});
            skFitSpline(sketch, "E504", {"points": [v(15.03, 16.35) * mm, v(15.08, 16.44) * mm, v(15.13, 16.55) * mm, v(15.18, 16.64) * mm]});
            skFitSpline(sketch, "E505", {"points": [v(15.18, 16.64) * mm, v(15.23, 16.73) * mm, v(15.27, 16.81) * mm, v(15.34, 16.88) * mm]});
            skFitSpline(sketch, "E506", {"points": [v(15.34, 16.88) * mm, v(15.5, 17.07) * mm, v(15.77, 17.1) * mm, v(15.97, 16.97) * mm]});
            skFitSpline(sketch, "E507", {"points": [v(15.97, 16.97) * mm, v(16.17, 16.83) * mm, v(16.25, 16.57) * mm, v(16.13, 16.34) * mm]});
            skFitSpline(sketch, "E508", {"points": [v(16.13, 16.34) * mm, v(15.95, 16.02) * mm, v(15.76, 15.7) * mm, v(15.58, 15.38) * mm]});
            skFitSpline(sketch, "E509", {"points": [v(15.58, 15.38) * mm, v(15.38, 15.05) * mm, v(15.18, 14.71) * mm, v(14.98, 14.36) * mm]});
            skFitSpline(sketch, "E510", {"points": [v(14.98, 14.36) * mm, v(15.32, 14.23) * mm, v(15.63, 14.1) * mm, v(15.95, 13.97) * mm]});
            skFitSpline(sketch, "E511", {"points": [v(15.95, 13.97) * mm, v(16.37, 13.8) * mm, v(16.8, 13.65) * mm, v(17.22, 13.47) * mm]});
            skFitSpline(sketch, "E512", {"points": [v(17.22, 13.47) * mm, v(17.42, 13.38) * mm, v(17.6, 13.27) * mm, v(17.78, 13.15) * mm]});
            skFitSpline(sketch, "E513", {"points": [v(17.78, 13.15) * mm, v(17.85, 13.11) * mm, v(17.9, 13.05) * mm, v(17.94, 12.98) * mm]});
            skFitSpline(sketch, "E514", {"points": [v(17.94, 12.98) * mm, v(18.46, 12.13) * mm, v(18.98, 11.27) * mm, v(19.5, 10.42) * mm]});
            skFitSpline(sketch, "E515", {"points": [v(19.5, 10.42) * mm, v(19.8, 9.92) * mm, v(20.11, 9.43) * mm, v(20.46, 8.94) * mm]});
            skFitSpline(sketch, "E516", {"points": [v(20.46, 8.94) * mm, v(20.45, 9.02) * mm, v(20.44, 9.1) * mm, v(20.43, 9.2) * mm]});
            skFitSpline(sketch, "E517", {"points": [v(20.43, 9.2) * mm, v(20.42, 9.28) * mm, v(20.42, 9.37) * mm, v(20.4, 9.45) * mm]});
            skFitSpline(sketch, "E518", {"points": [v(20.4, 9.45) * mm, v(20.23, 10.56) * mm, v(20.06, 11.66) * mm, v(19.88, 12.76) * mm]});
            skFitSpline(sketch, "E519", {"points": [v(19.88, 12.76) * mm, v(19.87, 12.84) * mm, v(19.83, 12.93) * mm, v(19.78, 13) * mm]});
            skFitSpline(sketch, "E520", {"points": [v(19.78, 13) * mm, v(19.52, 13.3) * mm, v(19.26, 13.6) * mm, v(19, 13.9) * mm]});
            skFitSpline(sketch, "E521", {"points": [v(19, 13.9) * mm, v(18.78, 14.13) * mm, v(18.55, 14.34) * mm, v(18.34, 14.57) * mm]});
            skFitSpline(sketch, "E522", {"points": [v(18.34, 14.57) * mm, v(18.27, 14.64) * mm, v(18.2, 14.72) * mm, v(18.15, 14.81) * mm]});
            skFitSpline(sketch, "E523", {"points": [v(18.15, 14.81) * mm, v(18.01, 15.04) * mm, v(18.07, 15.3) * mm, v(18.27, 15.45) * mm]});
            skFitSpline(sketch, "E524", {"points": [v(18.27, 15.45) * mm, v(18.47, 15.6) * mm, v(18.73, 15.58) * mm, v(18.9, 15.4) * mm]});
            skFitSpline(sketch, "E525", {"points": [v(18.9, 15.4) * mm, v(19.28, 15.02) * mm, v(19.64, 14.63) * mm, v(20, 14.25) * mm]});
            skFitSpline(sketch, "E526", {"points": [v(20, 14.25) * mm, v(20.06, 14.19) * mm, v(20.12, 14.12) * mm, v(20.19, 14.05) * mm]});
            skFitSpline(sketch, "E527", {"points": [v(20.19, 14.05) * mm, v(21.1, 14.57) * mm, v(22, 15.06) * mm, v(23.03, 15.3) * mm]});
            skFitSpline(sketch, "E528", {"points": [v(23.03, 15.3) * mm, v(22.75, 15.84) * mm, v(22.49, 16.36) * mm, v(22.22, 16.89) * mm]});
            skFitSpline(sketch, "E529", {"points": [v(22.22, 16.89) * mm, v(22.07, 17.17) * mm, v(22.15, 17.47) * mm, v(22.41, 17.6) * mm]});
            skFitSpline(sketch, "E530", {"points": [v(22.41, 17.6) * mm, v(22.67, 17.73) * mm, v(22.95, 17.63) * mm, v(23.1, 17.35) * mm]});
            skFitSpline(sketch, "E531", {"points": [v(23.1, 17.35) * mm, v(23.3, 16.93) * mm, v(23.5, 16.52) * mm, v(23.7, 16.1) * mm]});
            skFitSpline(sketch, "E532", {"points": [v(23.7, 16.1) * mm, v(23.76, 16) * mm, v(23.85, 15.9) * mm, v(23.93, 15.77) * mm]});
            skFitSpline(sketch, "E533", {"points": [v(23.93, 15.77) * mm, v(24.05, 15.8) * mm, v(24.17, 15.81) * mm, v(24.27, 15.86) * mm]});
            skFitSpline(sketch, "E534", {"points": [v(24.27, 15.86) * mm, v(24.48, 15.96) * mm, v(24.68, 16.08) * mm, v(24.89, 16.19) * mm]});
            skFitSpline(sketch, "E535", {"points": [v(24.89, 16.19) * mm, v(25.13, 16.32) * mm, v(25.38, 16.45) * mm, v(25.63, 16.57) * mm]});
            skFitSpline(sketch, "E536", {"points": [v(25.63, 16.57) * mm, v(25.88, 16.69) * mm, v(26.16, 16.58) * mm, v(26.28, 16.33) * mm]});
            skFitSpline(sketch, "E537", {"points": [v(26.28, 16.33) * mm, v(26.4, 16.1) * mm, v(26.31, 15.82) * mm, v(26.08, 15.7) * mm]});
            skFitSpline(sketch, "E538", {"points": [v(26.08, 15.7) * mm, v(25.75, 15.52) * mm, v(25.42, 15.36) * mm, v(25.1, 15.19) * mm]});
            skFitSpline(sketch, "E539", {"points": [v(25.1, 15.19) * mm, v(24.88, 15.08) * mm, v(24.66, 14.97) * mm, v(24.42, 14.85) * mm]});
            skFitSpline(sketch, "E540", {"points": [v(24.42, 14.85) * mm, v(25.1, 14.06) * mm, v(25.54, 13.12) * mm, v(25.98, 12.17) * mm]});
            skFitSpline(sketch, "E541", {"points": [v(25.98, 12.17) * mm, v(26.07, 12.18) * mm, v(26.15, 12.2) * mm, v(26.23, 12.21) * mm]});
            skFitSpline(sketch, "E542", {"points": [v(26.23, 12.21) * mm, v(26.74, 12.3) * mm, v(27.25, 12.4) * mm, v(27.77, 12.49) * mm]});
            skFitSpline(sketch, "E543", {"points": [v(27.77, 12.49) * mm, v(27.9, 12.51) * mm, v(28.05, 12.51) * mm, v(28.18, 12.42) * mm]});
            skFitSpline(sketch, "E544", {"points": [v(28.18, 12.42) * mm, v(28.49, 12.2) * mm, v(28.43, 11.73) * mm, v(28.07, 11.58) * mm]});
            skFitSpline(sketch, "E545", {"points": [v(28.07, 11.58) * mm, v(27.92, 11.52) * mm, v(27.75, 11.5) * mm, v(27.58, 11.47) * mm]});
            skFitSpline(sketch, "E546", {"points": [v(27.58, 11.47) * mm, v(26.96, 11.34) * mm, v(26.33, 11.22) * mm, v(25.71, 11.08) * mm]});
            skFitSpline(sketch, "E547", {"points": [v(25.71, 11.08) * mm, v(25.62, 11.06) * mm, v(25.52, 11) * mm, v(25.45, 10.92) * mm]});
            skFitSpline(sketch, "E548", {"points": [v(25.45, 10.92) * mm, v(24.6, 10.07) * mm, v(23.75, 9.21) * mm, v(22.9, 8.35) * mm]});
            skFitSpline(sketch, "E549", {"points": [v(22.9, 8.35) * mm, v(22.85, 8.3) * mm, v(22.8, 8.25) * mm, v(22.72, 8.16) * mm]});
            skFitSpline(sketch, "E550", {"points": [v(22.72, 8.16) * mm, v(22.82, 8.18) * mm, v(22.87, 8.2) * mm, v(22.9, 8.21) * mm]});
            skFitSpline(sketch, "E551", {"points": [v(22.9, 8.21) * mm, v(24.08, 8.7) * mm, v(25.24, 9.18) * mm, v(26.4, 9.66) * mm]});
            skFitSpline(sketch, "E552", {"points": [v(26.4, 9.66) * mm, v(26.62, 9.75) * mm, v(26.84, 9.83) * mm, v(27.04, 9.93) * mm]});
            skFitSpline(sketch, "E553", {"points": [v(27.04, 9.93) * mm, v(27.3, 10.06) * mm, v(27.56, 10.06) * mm, v(27.81, 10) * mm]});
            skFitSpline(sketch, "E554", {"points": [v(27.81, 10) * mm, v(28.37, 9.87) * mm, v(28.93, 9.72) * mm, v(29.49, 9.58) * mm]});
            skFitSpline(sketch, "E555", {"points": [v(29.49, 9.58) * mm, v(29.78, 9.5) * mm, v(30.07, 9.43) * mm, v(30.38, 9.36) * mm]});
            skFitSpline(sketch, "E556", {"points": [v(30.38, 9.36) * mm, v(30.42, 9.78) * mm, v(30.46, 10.18) * mm, v(30.5, 10.58) * mm]});
            skFitSpline(sketch, "E557", {"points": [v(30.5, 10.58) * mm, v(30.54, 10.93) * mm, v(30.56, 11.28) * mm, v(30.6, 11.63) * mm]});
            skFitSpline(sketch, "E558", {"points": [v(30.6, 11.63) * mm, v(30.65, 11.91) * mm, v(30.9, 12.08) * mm, v(31.18, 12.04) * mm]});
            skFitSpline(sketch, "E559", {"points": [v(31.18, 12.04) * mm, v(31.43, 12) * mm, v(31.62, 11.74) * mm, v(31.59, 11.47) * mm]});
            skFitSpline(sketch, "E560", {"points": [v(31.59, 11.47) * mm, v(31.52, 10.86) * mm, v(31.44, 10.25) * mm, v(31.37, 9.64) * mm]});
            skFitSpline(sketch, "E561", {"points": [v(31.37, 9.64) * mm, v(31.36, 9.47) * mm, v(31.37, 9.3) * mm, v(31.37, 9.09) * mm]});
            skFitSpline(sketch, "E562", {"points": [v(31.37, 9.09) * mm, v(31.58, 9.04) * mm, v(31.8, 8.98) * mm, v(32.02, 8.93) * mm]});
            skFitSpline(sketch, "E563", {"points": [v(32.02, 8.93) * mm, v(32.36, 8.85) * mm, v(32.7, 8.78) * mm, v(33.03, 8.71) * mm]});
            skFitSpline(sketch, "E564", {"points": [v(33.03, 8.71) * mm, v(33.22, 8.67) * mm, v(33.4, 8.63) * mm, v(33.6, 8.6) * mm]});
            skFitSpline(sketch, "E565", {"points": [v(33.6, 8.6) * mm, v(33.65, 8.58) * mm, v(33.72, 8.57) * mm, v(33.78, 8.55) * mm]});
            skFitSpline(sketch, "E566", {"points": [v(33.78, 8.55) * mm, v(34.03, 8.45) * mm, v(34.16, 8.2) * mm, v(34.08, 7.95) * mm]});
            skFitSpline(sketch, "E567", {"points": [v(34.08, 7.95) * mm, v(34, 7.72) * mm, v(33.77, 7.57) * mm, v(33.51, 7.62) * mm]});
            skFitSpline(sketch, "E568", {"points": [v(33.51, 7.62) * mm, v(33.15, 7.69) * mm, v(32.8, 7.77) * mm, v(32.44, 7.85) * mm]});
            skFitSpline(sketch, "E569", {"points": [v(32.44, 7.85) * mm, v(32.07, 7.93) * mm, v(31.7, 8) * mm, v(31.32, 8.09) * mm]});
            skFitSpline(sketch, "E570", {"points": [v(31.32, 8.09) * mm, v(31.3, 8.05) * mm, v(31.28, 8.03) * mm, v(31.28, 8.01) * mm]});
            skFitSpline(sketch, "E571", {"points": [v(31.28, 8.01) * mm, v(31.25, 7.55) * mm, v(31.24, 7.09) * mm, v(31.2, 6.62) * mm]});
            skFitSpline(sketch, "E572", {"points": [v(31.2, 6.62) * mm, v(31.18, 6.23) * mm, v(31.16, 5.83) * mm, v(31.1, 5.43) * mm]});
            skFitSpline(sketch, "E573", {"points": [v(31.1, 5.43) * mm, v(31.08, 5.15) * mm, v(30.96, 4.91) * mm, v(30.76, 4.69) * mm]});
            skFitSpline(sketch, "E574", {"points": [v(30.76, 4.69) * mm, v(30.23, 4.1) * mm, v(29.72, 3.48) * mm, v(29.2, 2.87) * mm]});
            skFitSpline(sketch, "E575", {"points": [v(29.2, 2.87) * mm, v(28.76, 2.35) * mm, v(28.3, 1.83) * mm, v(27.86, 1.3) * mm]});
            skFitSpline(sketch, "E576", {"points": [v(27.86, 1.3) * mm, v(27.84, 1.28) * mm, v(27.83, 1.26) * mm, v(27.78, 1.18) * mm]});
            skFitSpline(sketch, "E577", {"points": [v(27.78, 1.18) * mm, v(28.05, 1.3) * mm, v(28.26, 1.4) * mm, v(28.48, 1.5) * mm]});
            skFitSpline(sketch, "E578", {"points": [v(28.48, 1.5) * mm, v(29.4, 1.97) * mm, v(30.33, 2.45) * mm, v(31.25, 2.92) * mm]});
            skFitSpline(sketch, "E579", {"points": [v(31.25, 2.92) * mm, v(31.34, 2.97) * mm, v(31.44, 3.05) * mm, v(31.5, 3.13) * mm]});
            skFitSpline(sketch, "E580", {"points": [v(31.5, 3.13) * mm, v(31.83, 3.71) * mm, v(32.16, 4.3) * mm, v(32.49, 4.88) * mm]});
            skFitSpline(sketch, "E581", {"points": [v(32.49, 4.88) * mm, v(32.54, 4.98) * mm, v(32.6, 5.08) * mm, v(32.66, 5.17) * mm]});
            skFitSpline(sketch, "E582", {"points": [v(32.66, 5.17) * mm, v(32.83, 5.4) * mm, v(33.12, 5.46) * mm, v(33.34, 5.31) * mm]});
            skFitSpline(sketch, "E583", {"points": [v(33.34, 5.31) * mm, v(33.56, 5.16) * mm, v(33.6, 4.9) * mm, v(33.47, 4.63) * mm]});
            skFitSpline(sketch, "E584", {"points": [v(33.47, 4.63) * mm, v(33.18, 4.1) * mm, v(32.9, 3.58) * mm, v(32.61, 3.04) * mm]});
            skFitSpline(sketch, "E585", {"points": [v(32.61, 3.04) * mm, v(33.38, 2.34) * mm, v(34.14, 1.63) * mm, v(34.67, 0.73) * mm]});
            skFitSpline(sketch, "E586", {"points": [v(34.67, 0.73) * mm, v(35.1, 1.17) * mm, v(35.53, 1.6) * mm, v(35.95, 2.01) * mm]});
            skFitSpline(sketch, "E587", {"points": [v(35.95, 2.01) * mm, v(36.16, 2.22) * mm, v(36.46, 2.23) * mm, v(36.66, 2.04) * mm]});
            skFitSpline(sketch, "E588", {"points": [v(36.66, 2.04) * mm, v(36.87, 1.84) * mm, v(36.87, 1.54) * mm, v(36.66, 1.32) * mm]});
            skFitSpline(sketch, "E589", {"points": [v(36.66, 1.32) * mm, v(36.35, 1) * mm, v(36.03, 0.7) * mm, v(35.72, 0.4) * mm]});
            skFitSpline(sketch, "E590", {"points": [v(35.72, 0.4) * mm, v(35.6, 0.28) * mm, v(35.5, 0.16) * mm, v(35.4, 0.02) * mm]});
            skFitSpline(sketch, "E591", {"points": [v(35.4, 0.02) * mm, v(35.47, -0.1) * mm, v(35.52, -0.2) * mm, v(35.6, -0.29) * mm]});
            skFitSpline(sketch, "E592", {"points": [v(35.6, -0.29) * mm, v(35.76, -0.45) * mm, v(35.93, -0.6) * mm, v(36.1, -0.77) * mm]});
            skFitSpline(sketch, "E593", {"points": [v(36.1, -0.77) * mm, v(36.3, -0.96) * mm, v(36.5, -1.15) * mm, v(36.7, -1.36) * mm]});
            skFitSpline(sketch, "E594", {"points": [v(36.7, -1.36) * mm, v(36.87, -1.56) * mm, v(36.86, -1.85) * mm, v(36.67, -2.03) * mm]});
            skFitSpline(sketch, "E595", {"points": [v(36.67, -2.03) * mm, v(36.48, -2.22) * mm, v(36.18, -2.23) * mm, v(35.98, -2.04) * mm]});
            skFitSpline(sketch, "E596", {"points": [v(35.98, -2.04) * mm, v(35.72, -1.79) * mm, v(35.46, -1.52) * mm, v(35.2, -1.26) * mm]});
            skFitSpline(sketch, "E597", {"points": [v(35.2, -1.26) * mm, v(35.03, -1.1) * mm, v(34.87, -0.92) * mm, v(34.68, -0.73) * mm]});
            skFitSpline(sketch, "E598", {"points": [v(34.68, -0.73) * mm, v(34.14, -1.62) * mm, v(33.39, -2.33) * mm, v(32.6, -3.04) * mm]});
            skFitSpline(sketch, "E599", {"points": [v(32.6, -3.04) * mm, v(32.63, -3.09) * mm, v(32.66, -3.14) * mm, v(32.68, -3.19) * mm]});
            skFitSpline(sketch, "E600", {"points": [v(32.68, -3.19) * mm, v(32.95, -3.68) * mm, v(33.22, -4.17) * mm, v(33.48, -4.66) * mm]});
            skFitSpline(sketch, "E601", {"points": [v(33.48, -4.66) * mm, v(33.61, -4.9) * mm, v(33.54, -5.18) * mm, v(33.33, -5.31) * mm]});
            skFitSpline(sketch, "E602", {"points": [v(33.33, -5.31) * mm, v(33.12, -5.45) * mm, v(32.84, -5.4) * mm, v(32.67, -5.19) * mm]});
            skFitSpline(sketch, "E603", {"points": [v(32.67, -5.19) * mm, v(32.6, -5.1) * mm, v(32.56, -5.01) * mm, v(32.5, -4.92) * mm]});
            skFitSpline(sketch, "E604", {"points": [v(32.5, -4.92) * mm, v(32.23, -4.42) * mm, v(31.96, -3.9) * mm, v(31.68, -3.4) * mm]});
            skFitSpline(sketch, "E605", {"points": [v(31.68, -3.4) * mm, v(31.54, -3.14) * mm, v(31.34, -2.95) * mm, v(31.06, -2.81) * mm]});
            skFitSpline(sketch, "E606", {"points": [v(31.06, -2.81) * mm, v(30.05, -2.32) * mm, v(29.06, -1.8) * mm, v(28.06, -1.3) * mm]});
            skFitSpline(sketch, "E607", {"points": [v(28.06, -1.3) * mm, v(27.98, -1.27) * mm, v(27.9, -1.24) * mm, v(27.8, -1.23) * mm]});
            skFitSpline(sketch, "E608", {"points": [v(27.8, -1.23) * mm, v(27.95, -1.41) * mm, v(28.1, -1.59) * mm, v(28.26, -1.77) * mm]});
            skFitSpline(sketch, "E609", {"points": [v(28.26, -1.77) * mm, v(28.94, -2.56) * mm, v(29.62, -3.36) * mm, v(30.3, -4.15) * mm]});
            skFitSpline(sketch, "E610", {"points": [v(30.3, -4.15) * mm, v(30.47, -4.35) * mm, v(30.62, -4.56) * mm, v(30.8, -4.73) * mm]});
            skFitSpline(sketch, "E611", {"points": [v(30.8, -4.73) * mm, v(31, -4.94) * mm, v(31.09, -5.2) * mm, v(31.11, -5.47) * mm]});
            skFitSpline(sketch, "E612", {"points": [v(31.11, -5.47) * mm, v(31.16, -6.04) * mm, v(31.19, -6.61) * mm, v(31.22, -7.18) * mm]});
            skFitSpline(sketch, "E613", {"points": [v(31.22, -7.18) * mm, v(31.24, -7.48) * mm, v(31.27, -7.77) * mm, v(31.29, -8.08) * mm]});
            skFitSpline(sketch, "E614", {"points": [v(31.29, -8.08) * mm, v(31.36, -8.07) * mm, v(31.42, -8.07) * mm, v(31.48, -8.06) * mm]});
            skFitSpline(sketch, "E615", {"points": [v(31.48, -8.06) * mm, v(31.93, -7.96) * mm, v(32.38, -7.85) * mm, v(32.84, -7.76) * mm]});
            skFitSpline(sketch, "E616", {"points": [v(32.84, -7.76) * mm, v(33.07, -7.7) * mm, v(33.3, -7.65) * mm, v(33.54, -7.62) * mm]});
            skFitSpline(sketch, "E617", {"points": [v(33.54, -7.62) * mm, v(33.8, -7.58) * mm, v(34.01, -7.72) * mm, v(34.08, -7.95) * mm]});
            skFitSpline(sketch, "E618", {"points": [v(34.08, -7.95) * mm, v(34.15, -8.19) * mm, v(34.04, -8.44) * mm, v(33.8, -8.54) * mm]});
            skFitSpline(sketch, "E619", {"points": [v(33.8, -8.54) * mm, v(33.7, -8.58) * mm, v(33.61, -8.6) * mm, v(33.52, -8.61) * mm]});
            skFitSpline(sketch, "E620", {"points": [v(33.52, -8.61) * mm, v(32.84, -8.76) * mm, v(32.16, -8.9) * mm, v(31.49, -9.06) * mm]});
            skFitSpline(sketch, "E621", {"points": [v(31.49, -9.06) * mm, v(31.45, -9.06) * mm, v(31.41, -9.08) * mm, v(31.35, -9.1) * mm]});
            skFitSpline(sketch, "E622", {"points": [v(116.86, 7.45) * mm, v(116.25, 6.67) * mm, v(115.63, 5.9) * mm, v(114.98, 5.07) * mm]});
            skFitSpline(sketch, "E623", {"points": [v(114.98, 5.07) * mm, v(115.97, 5.44) * mm, v(116.9, 5.78) * mm, v(117.82, 6.12) * mm]});
            skFitSpline(sketch, "E624", {"points": [v(117.82, 6.12) * mm, v(117.9, 6.65) * mm, v(118.18, 7.06) * mm, v(118.37, 7.53) * mm]});
            skFitSpline(sketch, "E625", {"points": [v(118.37, 7.53) * mm, v(117.85, 7.49) * mm, v(117.37, 7.37) * mm, v(116.86, 7.45) * mm]});
            skFitSpline(sketch, "E626", {"points": [v(99.3, -0.02) * mm, v(99.3, 0) * mm, v(99.3, 0) * mm, v(99.31, 0.02) * mm]});
            skFitSpline(sketch, "E627", {"points": [v(99.31, 0.02) * mm, v(98.36, 0.29) * mm, v(97.4, 0.55) * mm, v(96.46, 0.82) * mm]});
            skFitSpline(sketch, "E628", {"points": [v(96.46, 0.82) * mm, v(96.1, 0.43) * mm, v(95.61, 0.28) * mm, v(95.19, 0) * mm]});
            skFitSpline(sketch, "E629", {"points": [v(95.19, 0) * mm, v(95.62, -0.27) * mm, v(96.1, -0.44) * mm, v(96.46, -0.82) * mm]});
            skFitSpline(sketch, "E630", {"points": [v(96.46, -0.82) * mm, v(97.4, -0.56) * mm, v(98.35, -0.29) * mm, v(99.3, -0.02) * mm]});
            skFitSpline(sketch, "E631", {"points": [v(105.33, -8.3) * mm, v(105.32, -8.29) * mm, v(105.3, -8.28) * mm, v(105.29, -8.28) * mm]});
            skFitSpline(sketch, "E632", {"points": [v(105.29, -8.28) * mm, v(104.74, -9.1) * mm, v(104.19, -9.92) * mm, v(103.66, -10.71) * mm]});
            skFitSpline(sketch, "E633", {"points": [v(103.66, -10.71) * mm, v(103.73, -10.88) * mm, v(103.8, -11.01) * mm, v(103.83, -11.15) * mm]});
            skFitSpline(sketch, "E634", {"points": [v(103.83, -11.15) * mm, v(103.9, -11.44) * mm, v(103.94, -11.74) * mm, v(104, -12.04) * mm]});
            skFitSpline(sketch, "E635", {"points": [v(104, -12.04) * mm, v(104, -12.09) * mm, v(104.03, -12.13) * mm, v(104.05, -12.18) * mm]});
            skFitSpline(sketch, "E636", {"points": [v(104.05, -12.18) * mm, v(104.44, -11.85) * mm, v(104.74, -11.44) * mm, v(105.22, -11.24) * mm]});
            skFitSpline(sketch, "E637", {"points": [v(105.22, -11.24) * mm, v(105.26, -10.26) * mm, v(105.3, -9.28) * mm, v(105.33, -8.3) * mm]});
            skFitSpline(sketch, "E638", {"points": [v(118.37, -7.53) * mm, v(118.17, -7.05) * mm, v(117.9, -6.63) * mm, v(117.82, -6.12) * mm]});
            skFitSpline(sketch, "E639", {"points": [v(117.82, -6.12) * mm, v(116.9, -5.78) * mm, v(115.96, -5.43) * mm, v(114.98, -5.07) * mm]});
            skFitSpline(sketch, "E640", {"points": [v(114.98, -5.07) * mm, v(115.63, -5.9) * mm, v(116.25, -6.68) * mm, v(116.86, -7.45) * mm]});
            skFitSpline(sketch, "E641", {"points": [v(116.86, -7.45) * mm, v(117.38, -7.36) * mm, v(117.86, -7.5) * mm, v(118.37, -7.53) * mm]});
            skFitSpline(sketch, "E642", {"points": [v(103.65, 10.72) * mm, v(104.2, 9.91) * mm, v(104.74, 9.1) * mm, v(105.29, 8.28) * mm]});
            skFitSpline(sketch, "E643", {"points": [v(105.29, 8.28) * mm, v(105.3, 8.28) * mm, v(105.32, 8.29) * mm, v(105.33, 8.3) * mm]});
            skFitSpline(sketch, "E644", {"points": [v(105.33, 8.3) * mm, v(105.3, 9.28) * mm, v(105.26, 10.26) * mm, v(105.22, 11.24) * mm]});
            skFitSpline(sketch, "E645", {"points": [v(105.22, 11.24) * mm, v(104.74, 11.45) * mm, v(104.43, 11.86) * mm, v(104.04, 12.18) * mm]});
            skFitSpline(sketch, "E646", {"points": [v(104.04, 12.18) * mm, v(103.91, 11.7) * mm, v(103.91, 11.2) * mm, v(103.65, 10.72) * mm]});
            skFitSpline(sketch, "E647", {"points": [v(91.84, 0.02) * mm, v(91.86, -0.01) * mm, v(91.86, -0.03) * mm, v(91.87, -0.04) * mm]});
            skFitSpline(sketch, "E648", {"points": [v(91.87, -0.04) * mm, v(92.7, -0.47) * mm, v(93.53, -0.9) * mm, v(94.36, -1.33) * mm]});
            skFitSpline(sketch, "E649", {"points": [v(94.36, -1.33) * mm, v(94.4, -1.35) * mm, v(94.45, -1.37) * mm, v(94.5, -1.36) * mm]});
            skFitSpline(sketch, "E650", {"points": [v(94.5, -1.36) * mm, v(94.73, -1.3) * mm, v(94.97, -1.27) * mm, v(95.22, -1.14) * mm]});
            skFitSpline(sketch, "E651", {"points": [v(95.22, -1.14) * mm, v(95.1, -1.07) * mm, v(95, -1.01) * mm, v(94.9, -0.96) * mm]});
            skFitSpline(sketch, "E652", {"points": [v(94.9, -0.96) * mm, v(94.7, -0.86) * mm, v(94.5, -0.77) * mm, v(94.3, -0.67) * mm]});
            skFitSpline(sketch, "E653", {"points": [v(94.3, -0.67) * mm, v(94.22, -0.63) * mm, v(94.14, -0.56) * mm, v(94.07, -0.5) * mm]});
            skFitSpline(sketch, "E654", {"points": [v(94.07, -0.5) * mm, v(93.88, -0.29) * mm, v(94.05, -0.02) * mm, v(93.98, 0.21) * mm]});
            skFitSpline(sketch, "E655", {"points": [v(93.98, 0.21) * mm, v(93.95, 0.3) * mm, v(94.02, 0.42) * mm, v(94.08, 0.5) * mm]});
            skFitSpline(sketch, "E656", {"points": [v(94.08, 0.5) * mm, v(94.15, 0.58) * mm, v(94.25, 0.64) * mm, v(94.34, 0.7) * mm]});
            skFitSpline(sketch, "E657", {"points": [v(94.34, 0.7) * mm, v(94.63, 0.84) * mm, v(94.91, 0.97) * mm, v(95.24, 1.14) * mm]});
            skFitSpline(sketch, "E658", {"points": [v(95.24, 1.14) * mm, v(94.97, 1.26) * mm, v(94.73, 1.3) * mm, v(94.49, 1.36) * mm]});
            skFitSpline(sketch, "E659", {"points": [v(94.49, 1.36) * mm, v(94.44, 1.37) * mm, v(94.38, 1.34) * mm, v(94.34, 1.31) * mm]});
            skFitSpline(sketch, "E660", {"points": [v(94.34, 1.31) * mm, v(93.81, 1.05) * mm, v(93.3, 0.8) * mm, v(92.78, 0.52) * mm]});
            skFitSpline(sketch, "E661", {"points": [v(92.78, 0.52) * mm, v(92.46, 0.36) * mm, v(92.15, 0.19) * mm, v(91.84, 0.02) * mm]});
            skFitSpline(sketch, "E662", {"points": [v(119, 6.57) * mm, v(119.16, 6.62) * mm, v(119.26, 6.66) * mm, v(119.37, 6.69) * mm]});
            skFitSpline(sketch, "E663", {"points": [v(119.37, 6.69) * mm, v(119.62, 6.77) * mm, v(119.81, 6.89) * mm, v(119.93, 7.17) * mm]});
            skFitSpline(sketch, "E664", {"points": [v(119.93, 7.17) * mm, v(120.16, 7.69) * mm, v(120.45, 8.18) * mm, v(120.7, 8.68) * mm]});
            skFitSpline(sketch, "E665", {"points": [v(120.7, 8.68) * mm, v(120.84, 8.95) * mm, v(120.96, 9.22) * mm, v(121.08, 9.5) * mm]});
            skFitSpline(sketch, "E666", {"points": [v(121.08, 9.5) * mm, v(121.05, 9.5) * mm, v(121.03, 9.5) * mm, v(121, 9.5) * mm]});
            skFitSpline(sketch, "E667", {"points": [v(121, 9.5) * mm, v(120.09, 9.37) * mm, v(119.17, 9.23) * mm, v(118.26, 9.1) * mm]});
            skFitSpline(sketch, "E668", {"points": [v(118.26, 9.1) * mm, v(118.22, 9.08) * mm, v(118.16, 9.07) * mm, v(118.13, 9.04) * mm]});
            skFitSpline(sketch, "E669", {"points": [v(118.13, 9.04) * mm, v(117.97, 8.86) * mm, v(117.8, 8.68) * mm, v(117.66, 8.43) * mm]});
            skFitSpline(sketch, "E670", {"points": [v(117.66, 8.43) * mm, v(117.8, 8.45) * mm, v(117.9, 8.45) * mm, v(118, 8.47) * mm]});
            skFitSpline(sketch, "E671", {"points": [v(118, 8.47) * mm, v(118.24, 8.51) * mm, v(118.48, 8.56) * mm, v(118.71, 8.6) * mm]});
            skFitSpline(sketch, "E672", {"points": [v(118.71, 8.6) * mm, v(119, 8.64) * mm, v(119.15, 8.56) * mm, v(119.28, 8.3) * mm]});
            skFitSpline(sketch, "E673", {"points": [v(119.28, 8.3) * mm, v(119.31, 8.25) * mm, v(119.35, 8.2) * mm, v(119.4, 8.16) * mm]});
            skFitSpline(sketch, "E674", {"points": [v(119.4, 8.16) * mm, v(119.59, 7.95) * mm, v(119.62, 7.78) * mm, v(119.5, 7.53) * mm]});
            skFitSpline(sketch, "E675", {"points": [v(119.5, 7.53) * mm, v(119.39, 7.33) * mm, v(119.28, 7.13) * mm, v(119.17, 6.94) * mm]});
            skFitSpline(sketch, "E676", {"points": [v(119.17, 6.94) * mm, v(119.12, 6.83) * mm, v(119.08, 6.73) * mm, v(119, 6.57) * mm]});
            skFitSpline(sketch, "E677", {"points": [v(121.1, -9.53) * mm, v(121.06, -9.43) * mm, v(121.03, -9.38) * mm, v(121, -9.33) * mm]});
            skFitSpline(sketch, "E678", {"points": [v(121, -9.33) * mm, v(120.61, -8.54) * mm, v(120.22, -7.75) * mm, v(119.82, -6.96) * mm]});
            skFitSpline(sketch, "E679", {"points": [v(119.82, -6.96) * mm, v(119.8, -6.9) * mm, v(119.76, -6.85) * mm, v(119.72, -6.83) * mm]});
            skFitSpline(sketch, "E680", {"points": [v(119.72, -6.83) * mm, v(119.5, -6.74) * mm, v(119.28, -6.66) * mm, v(119.06, -6.58) * mm]});
            skFitSpline(sketch, "E681", {"points": [v(119.06, -6.58) * mm, v(119.05, -6.6) * mm, v(119.04, -6.61) * mm, v(119.03, -6.63) * mm]});
            skFitSpline(sketch, "E682", {"points": [v(119.03, -6.63) * mm, v(119.07, -6.72) * mm, v(119.1, -6.81) * mm, v(119.15, -6.9) * mm]});
            skFitSpline(sketch, "E683", {"points": [v(119.15, -6.9) * mm, v(119.26, -7.1) * mm, v(119.38, -7.3) * mm, v(119.48, -7.51) * mm]});
            skFitSpline(sketch, "E684", {"points": [v(119.48, -7.51) * mm, v(119.62, -7.78) * mm, v(119.6, -7.95) * mm, v(119.39, -8.16) * mm]});
            skFitSpline(sketch, "E685", {"points": [v(119.39, -8.16) * mm, v(119.34, -8.2) * mm, v(119.3, -8.26) * mm, v(119.28, -8.31) * mm]});
            skFitSpline(sketch, "E686", {"points": [v(119.28, -8.31) * mm, v(119.15, -8.56) * mm, v(118.99, -8.64) * mm, v(118.7, -8.6) * mm]});
            skFitSpline(sketch, "E687", {"points": [v(118.7, -8.6) * mm, v(118.46, -8.56) * mm, v(118.2, -8.5) * mm, v(117.95, -8.47) * mm]});
            skFitSpline(sketch, "E688", {"points": [v(117.95, -8.47) * mm, v(117.87, -8.45) * mm, v(117.79, -8.45) * mm, v(117.64, -8.43) * mm]});
            skFitSpline(sketch, "E689", {"points": [v(117.64, -8.43) * mm, v(117.8, -8.64) * mm, v(117.94, -8.8) * mm, v(118.06, -8.97) * mm]});
            skFitSpline(sketch, "E690", {"points": [v(118.06, -8.97) * mm, v(118.13, -9.06) * mm, v(118.21, -9.1) * mm, v(118.32, -9.1) * mm]});
            skFitSpline(sketch, "E691", {"points": [v(118.32, -9.1) * mm, v(118.72, -9.16) * mm, v(119.12, -9.23) * mm, v(119.52, -9.3) * mm]});
            skFitSpline(sketch, "E692", {"points": [v(119.52, -9.3) * mm, v(120.04, -9.37) * mm, v(120.55, -9.45) * mm, v(121.1, -9.53) * mm]});
            skFitSpline(sketch, "E693", {"points": [v(103, 15.42) * mm, v(102.9, 14.92) * mm, v(102.83, 14.49) * mm, v(102.76, 14.05) * mm]});
            skFitSpline(sketch, "E694", {"points": [v(102.76, 14.05) * mm, v(102.67, 13.55) * mm, v(102.6, 13.04) * mm, v(102.51, 12.54) * mm]});
            skFitSpline(sketch, "E695", {"points": [v(102.51, 12.54) * mm, v(102.5, 12.51) * mm, v(102.5, 12.47) * mm, v(102.52, 12.45) * mm]});
            skFitSpline(sketch, "E696", {"points": [v(102.52, 12.45) * mm, v(102.65, 12.23) * mm, v(102.77, 12.01) * mm, v(102.97, 11.8) * mm]});
            skFitSpline(sketch, "E697", {"points": [v(102.97, 11.8) * mm, v(103, 11.91) * mm, v(103.01, 12) * mm, v(103.02, 12.07) * mm]});
            skFitSpline(sketch, "E698", {"points": [v(103.02, 12.07) * mm, v(103.06, 12.32) * mm, v(103.1, 12.57) * mm, v(103.13, 12.83) * mm]});
            skFitSpline(sketch, "E699", {"points": [v(103.13, 12.83) * mm, v(103.17, 13.1) * mm, v(103.3, 13.25) * mm, v(103.59, 13.3) * mm]});
            skFitSpline(sketch, "E700", {"points": [v(103.59, 13.3) * mm, v(103.64, 13.3) * mm, v(103.7, 13.32) * mm, v(103.74, 13.34) * mm]});
            skFitSpline(sketch, "E701", {"points": [v(103.74, 13.34) * mm, v(104.04, 13.49) * mm, v(104.2, 13.46) * mm, v(104.42, 13.22) * mm]});
            skFitSpline(sketch, "E702", {"points": [v(104.42, 13.22) * mm, v(104.58, 13.06) * mm, v(104.74, 12.89) * mm, v(104.9, 12.72) * mm]});
            skFitSpline(sketch, "E703", {"points": [v(104.9, 12.72) * mm, v(104.97, 12.65) * mm, v(105.05, 12.6) * mm, v(105.12, 12.53) * mm]});
            skFitSpline(sketch, "E704", {"points": [v(105.12, 12.53) * mm, v(105.14, 12.54) * mm, v(105.15, 12.54) * mm, v(105.17, 12.55) * mm]});
            skFitSpline(sketch, "E705", {"points": [v(105.17, 12.55) * mm, v(105.16, 12.8) * mm, v(105.14, 13.04) * mm, v(105.12, 13.28) * mm]});
            skFitSpline(sketch, "E706", {"points": [v(105.12, 13.28) * mm, v(105.12, 13.32) * mm, v(105.07, 13.36) * mm, v(105.04, 13.4) * mm]});
            skFitSpline(sketch, "E707", {"points": [v(105.04, 13.4) * mm, v(104.71, 13.72) * mm, v(104.39, 14.05) * mm, v(104.06, 14.37) * mm]});
            skFitSpline(sketch, "E708", {"points": [v(104.06, 14.37) * mm, v(103.72, 14.7) * mm, v(103.38, 15.04) * mm, v(103, 15.42) * mm]});
            skFitSpline(sketch, "E709", {"points": [v(102.98, -15.4) * mm, v(103.15, -15.25) * mm, v(103.28, -15.14) * mm, v(103.4, -15.02) * mm]});
            skFitSpline(sketch, "E710", {"points": [v(103.4, -15.02) * mm, v(103.95, -14.48) * mm, v(104.5, -13.93) * mm, v(105.05, -13.38) * mm]});
            skFitSpline(sketch, "E711", {"points": [v(105.05, -13.38) * mm, v(105.09, -13.34) * mm, v(105.12, -13.28) * mm, v(105.13, -13.22) * mm]});
            skFitSpline(sketch, "E712", {"points": [v(105.13, -13.22) * mm, v(105.15, -13.03) * mm, v(105.16, -12.84) * mm, v(105.17, -12.65) * mm]});
            skFitSpline(sketch, "E713", {"points": [v(105.17, -12.65) * mm, v(105.17, -12.61) * mm, v(105.14, -12.57) * mm, v(105.12, -12.52) * mm]});
            skFitSpline(sketch, "E714", {"points": [v(105.12, -12.52) * mm, v(105.07, -12.57) * mm, v(105.03, -12.6) * mm, v(105, -12.63) * mm]});
            skFitSpline(sketch, "E715", {"points": [v(105, -12.63) * mm, v(104.8, -12.83) * mm, v(104.61, -13.03) * mm, v(104.42, -13.23) * mm]});
            skFitSpline(sketch, "E716", {"points": [v(104.42, -13.23) * mm, v(104.2, -13.46) * mm, v(104.03, -13.49) * mm, v(103.75, -13.35) * mm]});
            skFitSpline(sketch, "E717", {"points": [v(103.75, -13.35) * mm, v(103.7, -13.32) * mm, v(103.64, -13.3) * mm, v(103.58, -13.29) * mm]});
            skFitSpline(sketch, "E718", {"points": [v(103.58, -13.29) * mm, v(103.31, -13.25) * mm, v(103.17, -13.1) * mm, v(103.13, -12.84) * mm]});
            skFitSpline(sketch, "E719", {"points": [v(103.13, -12.84) * mm, v(103.1, -12.59) * mm, v(103.06, -12.33) * mm, v(103.03, -12.08) * mm]});
            skFitSpline(sketch, "E720", {"points": [v(103.03, -12.08) * mm, v(103.01, -12) * mm, v(103, -11.92) * mm, v(102.97, -11.84) * mm]});
            skFitSpline(sketch, "E721", {"points": [v(102.97, -11.84) * mm, v(102.96, -11.83) * mm, v(102.94, -11.83) * mm, v(102.92, -11.82) * mm]});
            skFitSpline(sketch, "E722", {"points": [v(102.92, -11.82) * mm, v(102.79, -12.03) * mm, v(102.65, -12.23) * mm, v(102.52, -12.44) * mm]});
            skFitSpline(sketch, "E723", {"points": [v(102.52, -12.44) * mm, v(102.5, -12.47) * mm, v(102.51, -12.51) * mm, v(102.52, -12.55) * mm]});
            skFitSpline(sketch, "E724", {"points": [v(102.52, -12.55) * mm, v(102.54, -12.73) * mm, v(102.57, -12.91) * mm, v(102.6, -13.1) * mm]});
            skFitSpline(sketch, "E725", {"points": [v(102.6, -13.1) * mm, v(102.73, -13.85) * mm, v(102.85, -14.6) * mm, v(102.98, -15.4) * mm]});
            skFitSpline(sketch, "E726", {"points": [v(113.55, -12.28) * mm, v(112.83, -11.55) * mm, v(112.07, -10.88) * mm, v(111.3, -10.22) * mm]});
            skFitSpline(sketch, "E727", {"points": [v(111.3, -10.22) * mm, v(111.1, -11.22) * mm, v(110.91, -12.2) * mm, v(110.71, -13.16) * mm]});
            skFitSpline(sketch, "E728", {"points": [v(110.71, -13.16) * mm, v(111.1, -13.5) * mm, v(112.44, -14.39) * mm, v(112.73, -14.47) * mm]});
            skFitSpline(sketch, "E729", {"points": [v(112.73, -14.47) * mm, v(113.03, -13.75) * mm, v(113.34, -13.02) * mm, v(113.55, -12.28) * mm]});
            skFitSpline(sketch, "E730", {"points": [v(121.4, 1.5) * mm, v(120.49, 1) * mm, v(119.62, 0.5) * mm, v(118.73, 0) * mm]});
            skFitSpline(sketch, "E731", {"points": [v(118.73, 0) * mm, v(119.63, -0.51) * mm, v(120.5, -1) * mm, v(121.36, -1.49) * mm]});
            skFitSpline(sketch, "E732", {"points": [v(121.36, -1.49) * mm, v(121.93, -1.15) * mm, v(123.1, -0.2) * mm, v(123.23, 0.05) * mm]});
            skFitSpline(sketch, "E733", {"points": [v(123.23, 0.05) * mm, v(122.62, 0.53) * mm, v(122.01, 1.02) * mm, v(121.4, 1.5) * mm]});
            skFitSpline(sketch, "E734", {"points": [v(112.7, 14.48) * mm, v(112.34, 14.33) * mm, v(110.96, 13.4) * mm, v(110.72, 13.16) * mm]});
            skFitSpline(sketch, "E735", {"points": [v(110.72, 13.16) * mm, v(110.91, 12.18) * mm, v(111.1, 11.2) * mm, v(111.31, 10.2) * mm]});
            skFitSpline(sketch, "E736", {"points": [v(111.31, 10.2) * mm, v(112.07, 10.9) * mm, v(112.82, 11.58) * mm, v(113.55, 12.25) * mm]});
            skFitSpline(sketch, "E737", {"points": [v(113.55, 12.25) * mm, v(113.37, 12.91) * mm, v(112.87, 14.24) * mm, v(112.7, 14.48) * mm]});
            skFitSpline(sketch, "E738", {"points": [v(95.65, 8.97) * mm, v(95.85, 8.17) * mm, v(96.03, 7.4) * mm, v(96.3, 6.65) * mm]});
            skFitSpline(sketch, "E739", {"points": [v(96.3, 6.65) * mm, v(97.31, 6.53) * mm, v(98.3, 6.42) * mm, v(99.32, 6.3) * mm]});
            skFitSpline(sketch, "E740", {"points": [v(99.32, 6.3) * mm, v(98.9, 7.24) * mm, v(98.48, 8.15) * mm, v(98.06, 9.06) * mm]});
            skFitSpline(sketch, "E741", {"points": [v(98.06, 9.06) * mm, v(97.26, 9.11) * mm, v(96.48, 9.03) * mm, v(95.65, 8.97) * mm]});
            skFitSpline(sketch, "E742", {"points": [v(99.32, -6.3) * mm, v(98.3, -6.42) * mm, v(97.3, -6.54) * mm, v(96.33, -6.65) * mm]});
            skFitSpline(sketch, "E743", {"points": [v(96.33, -6.65) * mm, v(96.15, -7) * mm, v(95.7, -8.64) * mm, v(95.69, -8.97) * mm]});
            skFitSpline(sketch, "E744", {"points": [v(95.69, -8.97) * mm, v(96.48, -9.03) * mm, v(97.26, -9.12) * mm, v(98.06, -9.07) * mm]});
            skFitSpline(sketch, "E745", {"points": [v(98.06, -9.07) * mm, v(98.48, -8.14) * mm, v(98.9, -7.23) * mm, v(99.32, -6.3) * mm]});
            skFitSpline(sketch, "E746", {"points": [v(102.36, 17.36) * mm, v(102.4, 17.56) * mm, v(102.43, 17.7) * mm, v(102.45, 17.84) * mm]});
            skFitSpline(sketch, "E747", {"points": [v(102.45, 17.84) * mm, v(102.55, 18.37) * mm, v(102.65, 18.9) * mm, v(102.75, 19.44) * mm]});
            skFitSpline(sketch, "E748", {"points": [v(102.75, 19.44) * mm, v(102.8, 19.71) * mm, v(103, 19.87) * mm, v(103.25, 19.86) * mm]});
            skFitSpline(sketch, "E749", {"points": [v(103.25, 19.86) * mm, v(103.48, 19.85) * mm, v(103.67, 19.69) * mm, v(103.72, 19.45) * mm]});
            skFitSpline(sketch, "E750", {"points": [v(103.72, 19.45) * mm, v(103.73, 19.38) * mm, v(103.72, 19.3) * mm, v(103.7, 19.24) * mm]});
            skFitSpline(sketch, "E751", {"points": [v(103.7, 19.24) * mm, v(103.57, 18.51) * mm, v(103.43, 17.78) * mm, v(103.3, 17.05) * mm]});
            skFitSpline(sketch, "E752", {"points": [v(103.3, 17.05) * mm, v(103.28, 17) * mm, v(103.29, 16.92) * mm, v(103.26, 16.87) * mm]});
            skFitSpline(sketch, "E753", {"points": [v(103.26, 16.87) * mm, v(103.15, 16.6) * mm, v(103.3, 16.47) * mm, v(103.47, 16.3) * mm]});
            skFitSpline(sketch, "E754", {"points": [v(103.47, 16.3) * mm, v(103.94, 15.87) * mm, v(104.39, 15.41) * mm, v(104.84, 14.96) * mm]});
            skFitSpline(sketch, "E755", {"points": [v(104.84, 14.96) * mm, v(104.9, 14.9) * mm, v(104.97, 14.84) * mm, v(105.04, 14.77) * mm]});
            skFitSpline(sketch, "E756", {"points": [v(105.04, 14.77) * mm, v(105.05, 14.87) * mm, v(105.05, 14.94) * mm, v(105.06, 15) * mm]});
            skFitSpline(sketch, "E757", {"points": [v(105.06, 15) * mm, v(105.12, 15.27) * mm, v(105.33, 15.42) * mm, v(105.58, 15.4) * mm]});
            skFitSpline(sketch, "E758", {"points": [v(105.58, 15.4) * mm, v(105.83, 15.38) * mm, v(106.02, 15.18) * mm, v(106.04, 14.92) * mm]});
            skFitSpline(sketch, "E759", {"points": [v(106.04, 14.92) * mm, v(106.05, 14.76) * mm, v(106.05, 14.59) * mm, v(106.05, 14.42) * mm]});
            skFitSpline(sketch, "E760", {"points": [v(106.05, 14.42) * mm, v(106.07, 14.02) * mm, v(106.09, 13.6) * mm, v(106.1, 13.2) * mm]});
            skFitSpline(sketch, "E761", {"points": [v(106.1, 13.2) * mm, v(106.13, 12.53) * mm, v(106.16, 11.85) * mm, v(106.19, 11.17) * mm]});
            skFitSpline(sketch, "E762", {"points": [v(106.19, 11.17) * mm, v(106.2, 10.63) * mm, v(106.22, 10.09) * mm, v(106.25, 9.54) * mm]});
            skFitSpline(sketch, "E763", {"points": [v(106.25, 9.54) * mm, v(106.27, 9.12) * mm, v(106.3, 8.7) * mm, v(106.32, 8.28) * mm]});
            skFitSpline(sketch, "E764", {"points": [v(106.32, 8.28) * mm, v(106.35, 7.9) * mm, v(106.37, 7.53) * mm, v(106.39, 7.16) * mm]});
            skFitSpline(sketch, "E765", {"points": [v(106.39, 7.16) * mm, v(106.4, 6.96) * mm, v(106.4, 6.76) * mm, v(106.43, 6.56) * mm]});
            skFitSpline(sketch, "E766", {"points": [v(106.43, 6.56) * mm, v(106.43, 6.5) * mm, v(106.46, 6.42) * mm, v(106.5, 6.36) * mm]});
            skFitSpline(sketch, "E767", {"points": [v(106.5, 6.36) * mm, v(106.77, 5.93) * mm, v(107.04, 5.5) * mm, v(107.33, 5.07) * mm]});
            skFitSpline(sketch, "E768", {"points": [v(107.33, 5.07) * mm, v(107.69, 4.53) * mm, v(108.06, 4) * mm, v(108.44, 3.45) * mm]});
            skFitSpline(sketch, "E769", {"points": [v(108.44, 3.45) * mm, v(108.46, 3.41) * mm, v(108.5, 3.38) * mm, v(108.55, 3.3) * mm]});
            skFitSpline(sketch, "E770", {"points": [v(108.55, 3.3) * mm, v(108.62, 3.56) * mm, v(108.68, 3.77) * mm, v(108.73, 4) * mm]});
            skFitSpline(sketch, "E771", {"points": [v(108.73, 4) * mm, v(108.74, 4.04) * mm, v(108.69, 4.1) * mm, v(108.65, 4.16) * mm]});
            skFitSpline(sketch, "E772", {"points": [v(108.65, 4.16) * mm, v(108.17, 4.96) * mm, v(107.69, 5.76) * mm, v(107.2, 6.56) * mm]});
            skFitSpline(sketch, "E773", {"points": [v(107.2, 6.56) * mm, v(107.12, 6.7) * mm, v(107.06, 6.85) * mm, v(107.12, 7.01) * mm]});
            skFitSpline(sketch, "E774", {"points": [v(107.12, 7.01) * mm, v(107.23, 7.38) * mm, v(107.68, 7.49) * mm, v(107.94, 7.2) * mm]});
            skFitSpline(sketch, "E775", {"points": [v(107.94, 7.2) * mm, v(107.99, 7.16) * mm, v(108.02, 7.1) * mm, v(108.05, 7.05) * mm]});
            skFitSpline(sketch, "E776", {"points": [v(108.05, 7.05) * mm, v(108.39, 6.5) * mm, v(108.72, 5.94) * mm, v(109.06, 5.4) * mm]});
            skFitSpline(sketch, "E777", {"points": [v(109.06, 5.4) * mm, v(109.08, 5.36) * mm, v(109.1, 5.33) * mm, v(109.14, 5.28) * mm]});
            skFitSpline(sketch, "E778", {"points": [v(109.14, 5.28) * mm, v(109.23, 5.55) * mm, v(109.3, 5.79) * mm, v(109.37, 6.03) * mm]});
            skFitSpline(sketch, "E779", {"points": [v(109.37, 6.03) * mm, v(109.39, 6.08) * mm, v(109.37, 6.16) * mm, v(109.35, 6.2) * mm]});
            skFitSpline(sketch, "E780", {"points": [v(109.35, 6.2) * mm, v(109.15, 6.62) * mm, v(108.95, 7.03) * mm, v(108.75, 7.43) * mm]});
            skFitSpline(sketch, "E781", {"points": [v(108.75, 7.43) * mm, v(108.5, 7.91) * mm, v(108.25, 8.38) * mm, v(108, 8.86) * mm]});
            skFitSpline(sketch, "E782", {"points": [v(108, 8.86) * mm, v(107.9, 9.08) * mm, v(107.78, 9.3) * mm, v(107.7, 9.53) * mm]});
            skFitSpline(sketch, "E783", {"points": [v(107.7, 9.53) * mm, v(107.6, 9.78) * mm, v(107.73, 10.05) * mm, v(107.96, 10.15) * mm]});
            skFitSpline(sketch, "E784", {"points": [v(107.96, 10.15) * mm, v(108.2, 10.25) * mm, v(108.46, 10.16) * mm, v(108.58, 9.93) * mm]});
            skFitSpline(sketch, "E785", {"points": [v(108.58, 9.93) * mm, v(108.96, 9.19) * mm, v(109.32, 8.45) * mm, v(109.7, 7.7) * mm]});
            skFitSpline(sketch, "E786", {"points": [v(109.7, 7.7) * mm, v(109.74, 7.62) * mm, v(109.77, 7.54) * mm, v(109.83, 7.4) * mm]});
            skFitSpline(sketch, "E787", {"points": [v(109.83, 7.4) * mm, v(109.99, 7.79) * mm, v(110.14, 8.1) * mm, v(110, 8.5) * mm]});
            skFitSpline(sketch, "E788", {"points": [v(110, 8.5) * mm, v(109.67, 9.4) * mm, v(109.3, 10.3) * mm, v(108.84, 11.15) * mm]});
            skFitSpline(sketch, "E789", {"points": [v(108.84, 11.15) * mm, v(108.82, 11.19) * mm, v(108.8, 11.22) * mm, v(108.79, 11.26) * mm]});
            skFitSpline(sketch, "E790", {"points": [v(108.79, 11.26) * mm, v(108.6, 11.65) * mm, v(108.4, 12.05) * mm, v(108.22, 12.44) * mm]});
            skFitSpline(sketch, "E791", {"points": [v(108.22, 12.44) * mm, v(108.16, 12.55) * mm, v(108.1, 12.66) * mm, v(108.03, 12.77) * mm]});
            skFitSpline(sketch, "E792", {"points": [v(108.03, 12.77) * mm, v(107.9, 13.01) * mm, v(107.95, 13.3) * mm, v(108.16, 13.46) * mm]});
            skFitSpline(sketch, "E793", {"points": [v(108.16, 13.46) * mm, v(108.38, 13.61) * mm, v(108.66, 13.56) * mm, v(108.84, 13.34) * mm]});
            skFitSpline(sketch, "E794", {"points": [v(108.84, 13.34) * mm, v(108.88, 13.28) * mm, v(108.93, 13.22) * mm, v(108.96, 13.16) * mm]});
            skFitSpline(sketch, "E795", {"points": [v(108.96, 13.16) * mm, v(109.12, 12.85) * mm, v(109.29, 12.54) * mm, v(109.44, 12.22) * mm]});
            skFitSpline(sketch, "E796", {"points": [v(109.44, 12.22) * mm, v(109.67, 11.73) * mm, v(109.9, 11.24) * mm, v(110.13, 10.75) * mm]});
            skFitSpline(sketch, "E797", {"points": [v(110.13, 10.75) * mm, v(110.16, 10.68) * mm, v(110.2, 10.62) * mm, v(110.26, 10.57) * mm]});
            skFitSpline(sketch, "E798", {"points": [v(110.26, 10.57) * mm, v(110.24, 10.67) * mm, v(110.2, 10.78) * mm, v(110.18, 10.89) * mm]});
            skFitSpline(sketch, "E799", {"points": [v(110.18, 10.89) * mm, v(110.1, 11.35) * mm, v(110.01, 11.81) * mm, v(109.92, 12.27) * mm]});
            skFitSpline(sketch, "E800", {"points": [v(109.92, 12.27) * mm, v(109.87, 12.49) * mm, v(109.82, 12.7) * mm, v(109.75, 12.92) * mm]});
            skFitSpline(sketch, "E801", {"points": [v(109.75, 12.92) * mm, v(109.58, 13.48) * mm, v(109.73, 13.7) * mm, v(110.08, 13.93) * mm]});
            skFitSpline(sketch, "E802", {"points": [v(110.08, 13.93) * mm, v(110.78, 14.4) * mm, v(111.5, 14.87) * mm, v(112.2, 15.34) * mm]});
            skFitSpline(sketch, "E803", {"points": [v(112.2, 15.34) * mm, v(112.21, 15.35) * mm, v(112.23, 15.37) * mm, v(112.25, 15.39) * mm]});
            skFitSpline(sketch, "E804", {"points": [v(112.25, 15.39) * mm, v(112.08, 15.76) * mm, v(111.91, 16.13) * mm, v(111.73, 16.5) * mm]});
            skFitSpline(sketch, "E805", {"points": [v(111.73, 16.5) * mm, v(111.57, 16.81) * mm, v(111.4, 17.13) * mm, v(111.24, 17.45) * mm]});
            skFitSpline(sketch, "E806", {"points": [v(111.24, 17.45) * mm, v(111.2, 17.53) * mm, v(111.18, 17.62) * mm, v(111.18, 17.7) * mm]});
            skFitSpline(sketch, "E807", {"points": [v(111.18, 17.7) * mm, v(111.17, 17.9) * mm, v(111.3, 18.1) * mm, v(111.5, 18.16) * mm]});
            skFitSpline(sketch, "E808", {"points": [v(111.5, 18.16) * mm, v(111.69, 18.23) * mm, v(111.9, 18.17) * mm, v(112.03, 18) * mm]});
            skFitSpline(sketch, "E809", {"points": [v(112.03, 18) * mm, v(112.08, 17.95) * mm, v(112.11, 17.89) * mm, v(112.14, 17.82) * mm]});
            skFitSpline(sketch, "E810", {"points": [v(112.14, 17.82) * mm, v(112.38, 17.35) * mm, v(112.61, 16.88) * mm, v(112.85, 16.4) * mm]});
            skFitSpline(sketch, "E811", {"points": [v(112.85, 16.4) * mm, v(112.94, 16.22) * mm, v(113.04, 16.03) * mm, v(113.14, 15.81) * mm]});
            skFitSpline(sketch, "E812", {"points": [v(113.14, 15.81) * mm, v(113.34, 15.92) * mm, v(113.52, 16.02) * mm, v(113.7, 16.11) * mm]});
            skFitSpline(sketch, "E813", {"points": [v(113.7, 16.11) * mm, v(114.18, 16.36) * mm, v(114.65, 16.6) * mm, v(115.13, 16.85) * mm]});
            skFitSpline(sketch, "E814", {"points": [v(115.13, 16.85) * mm, v(115.2, 16.9) * mm, v(115.29, 16.93) * mm, v(115.37, 16.94) * mm]});
            skFitSpline(sketch, "E815", {"points": [v(115.37, 16.94) * mm, v(115.59, 16.98) * mm, v(115.78, 16.89) * mm, v(115.88, 16.7) * mm]});
            skFitSpline(sketch, "E816", {"points": [v(115.88, 16.7) * mm, v(115.98, 16.52) * mm, v(115.95, 16.28) * mm, v(115.79, 16.13) * mm]});
            skFitSpline(sketch, "E817", {"points": [v(115.79, 16.13) * mm, v(115.73, 16.07) * mm, v(115.65, 16.03) * mm, v(115.57, 15.99) * mm]});
            skFitSpline(sketch, "E818", {"points": [v(115.57, 15.99) * mm, v(114.94, 15.65) * mm, v(114.3, 15.32) * mm, v(113.66, 14.99) * mm]});
            skFitSpline(sketch, "E819", {"points": [v(113.66, 14.99) * mm, v(113.64, 14.97) * mm, v(113.63, 14.96) * mm, v(113.6, 14.94) * mm]});
            skFitSpline(sketch, "E820", {"points": [v(113.6, 14.94) * mm, v(113.76, 14.54) * mm, v(113.92, 14.15) * mm, v(114.06, 13.76) * mm]});
            skFitSpline(sketch, "E821", {"points": [v(114.06, 13.76) * mm, v(114.23, 13.31) * mm, v(114.39, 12.87) * mm, v(114.53, 12.42) * mm]});
            skFitSpline(sketch, "E822", {"points": [v(114.53, 12.42) * mm, v(114.66, 12.01) * mm, v(114.56, 11.78) * mm, v(114.22, 11.5) * mm]});
            skFitSpline(sketch, "E823", {"points": [v(114.22, 11.5) * mm, v(113.97, 11.32) * mm, v(113.75, 11.1) * mm, v(113.52, 10.89) * mm]});
            skFitSpline(sketch, "E824", {"points": [v(113.52, 10.89) * mm, v(113.22, 10.62) * mm, v(112.93, 10.35) * mm, v(112.63, 10.09) * mm]});
            skFitSpline(sketch, "E825", {"points": [v(112.63, 10.09) * mm, v(112.56, 10.03) * mm, v(112.5, 9.98) * mm, v(112.45, 9.9) * mm]});
            skFitSpline(sketch, "E826", {"points": [v(112.45, 9.9) * mm, v(112.48, 9.9) * mm, v(112.53, 9.9) * mm, v(112.56, 9.92) * mm]});
            skFitSpline(sketch, "E827", {"points": [v(112.56, 9.92) * mm, v(112.86, 10.08) * mm, v(113.16, 10.23) * mm, v(113.45, 10.4) * mm]});
            skFitSpline(sketch, "E828", {"points": [v(113.45, 10.4) * mm, v(113.6, 10.48) * mm, v(113.73, 10.58) * mm, v(113.88, 10.66) * mm]});
            skFitSpline(sketch, "E829", {"points": [v(113.88, 10.66) * mm, v(114.25, 10.85) * mm, v(114.63, 11.04) * mm, v(115.01, 11.23) * mm]});
            skFitSpline(sketch, "E830", {"points": [v(115.01, 11.23) * mm, v(115.1, 11.27) * mm, v(115.21, 11.29) * mm, v(115.31, 11.3) * mm]});
            skFitSpline(sketch, "E831", {"points": [v(115.31, 11.3) * mm, v(115.57, 11.3) * mm, v(115.73, 11.17) * mm, v(115.8, 10.92) * mm]});
            skFitSpline(sketch, "E832", {"points": [v(115.8, 10.92) * mm, v(115.85, 10.73) * mm, v(115.74, 10.48) * mm, v(115.54, 10.38) * mm]});
            skFitSpline(sketch, "E833", {"points": [v(115.54, 10.38) * mm, v(115.2, 10.22) * mm, v(114.87, 10.07) * mm, v(114.53, 9.9) * mm]});
            skFitSpline(sketch, "E834", {"points": [v(114.53, 9.9) * mm, v(114.26, 9.75) * mm, v(114, 9.59) * mm, v(113.72, 9.44) * mm]});
            skFitSpline(sketch, "E835", {"points": [v(113.72, 9.44) * mm, v(112.93, 9.03) * mm, v(112.17, 8.57) * mm, v(111.43, 8.08) * mm]});
            skFitSpline(sketch, "E836", {"points": [v(111.43, 8.08) * mm, v(111.07, 7.85) * mm, v(110.96, 7.5) * mm, v(110.88, 7.08) * mm]});
            skFitSpline(sketch, "E837", {"points": [v(110.88, 7.08) * mm, v(110.97, 7.13) * mm, v(111.03, 7.15) * mm, v(111.09, 7.19) * mm]});
            skFitSpline(sketch, "E838", {"points": [v(111.09, 7.19) * mm, v(111.64, 7.52) * mm, v(112.23, 7.8) * mm, v(112.82, 8.07) * mm]});
            skFitSpline(sketch, "E839", {"points": [v(112.82, 8.07) * mm, v(113, 8.15) * mm, v(113.16, 8.27) * mm, v(113.34, 8.36) * mm]});
            skFitSpline(sketch, "E840", {"points": [v(113.34, 8.36) * mm, v(113.53, 8.45) * mm, v(113.71, 8.44) * mm, v(113.88, 8.32) * mm]});
            skFitSpline(sketch, "E841", {"points": [v(113.88, 8.32) * mm, v(114.04, 8.2) * mm, v(114.09, 8.04) * mm, v(114.06, 7.85) * mm]});
            skFitSpline(sketch, "E842", {"points": [v(114.06, 7.85) * mm, v(114.03, 7.68) * mm, v(113.92, 7.56) * mm, v(113.77, 7.48) * mm]});
            skFitSpline(sketch, "E843", {"points": [v(113.77, 7.48) * mm, v(113.53, 7.35) * mm, v(113.28, 7.22) * mm, v(113.03, 7.1) * mm]});
            skFitSpline(sketch, "E844", {"points": [v(113.03, 7.1) * mm, v(112.53, 6.84) * mm, v(112.03, 6.57) * mm, v(111.52, 6.31) * mm]});
            skFitSpline(sketch, "E845", {"points": [v(111.52, 6.31) * mm, v(111.22, 6.15) * mm, v(110.92, 5.99) * mm, v(110.6, 5.84) * mm]});
            skFitSpline(sketch, "E846", {"points": [v(110.6, 5.84) * mm, v(110.5, 5.79) * mm, v(110.44, 5.74) * mm, v(110.4, 5.62) * mm]});
            skFitSpline(sketch, "E847", {"points": [v(110.4, 5.62) * mm, v(110.34, 5.4) * mm, v(110.27, 5.19) * mm, v(110.18, 4.94) * mm]});
            skFitSpline(sketch, "E848", {"points": [v(110.18, 4.94) * mm, v(110.26, 4.97) * mm, v(110.32, 4.99) * mm, v(110.38, 5) * mm]});
            skFitSpline(sketch, "E849", {"points": [v(110.38, 5) * mm, v(110.97, 5.26) * mm, v(111.55, 5.5) * mm, v(112.14, 5.75) * mm]});
            skFitSpline(sketch, "E850", {"points": [v(112.14, 5.75) * mm, v(112.54, 5.92) * mm, v(112.91, 5.65) * mm, v(112.86, 5.25) * mm]});
            skFitSpline(sketch, "E851", {"points": [v(112.86, 5.25) * mm, v(112.84, 5.07) * mm, v(112.73, 4.95) * mm, v(112.57, 4.87) * mm]});
            skFitSpline(sketch, "E852", {"points": [v(112.57, 4.87) * mm, v(112.45, 4.81) * mm, v(112.34, 4.77) * mm, v(112.22, 4.72) * mm]});
            skFitSpline(sketch, "E853", {"points": [v(112.22, 4.72) * mm, v(111.44, 4.39) * mm, v(110.66, 4.06) * mm, v(109.88, 3.74) * mm]});
            skFitSpline(sketch, "E854", {"points": [v(109.88, 3.74) * mm, v(109.79, 3.7) * mm, v(109.74, 3.65) * mm, v(109.71, 3.56) * mm]});
            skFitSpline(sketch, "E855", {"points": [v(109.71, 3.56) * mm, v(109.66, 3.38) * mm, v(109.58, 3.21) * mm, v(109.5, 3.01) * mm]});
            skFitSpline(sketch, "E856", {"points": [v(109.5, 3.01) * mm, v(109.58, 3.03) * mm, v(109.64, 3.04) * mm, v(109.7, 3.06) * mm]});
            skFitSpline(sketch, "E857", {"points": [v(109.7, 3.06) * mm, v(110.3, 3.27) * mm, v(110.89, 3.47) * mm, v(111.48, 3.7) * mm]});
            skFitSpline(sketch, "E858", {"points": [v(111.48, 3.7) * mm, v(111.96, 3.87) * mm, v(112.45, 4.06) * mm, v(112.93, 4.25) * mm]});
            skFitSpline(sketch, "E859", {"points": [v(112.93, 4.25) * mm, v(113.02, 4.3) * mm, v(113.1, 4.36) * mm, v(113.17, 4.44) * mm]});
            skFitSpline(sketch, "E860", {"points": [v(113.17, 4.44) * mm, v(114.28, 5.8) * mm, v(115.38, 7.17) * mm, v(116.48, 8.54) * mm]});
            skFitSpline(sketch, "E861", {"points": [v(116.48, 8.54) * mm, v(117.1, 9.3) * mm, v(117.7, 10.09) * mm, v(118.31, 10.85) * mm]});
            skFitSpline(sketch, "E862", {"points": [v(118.31, 10.85) * mm, v(118.39, 10.95) * mm, v(118.5, 11.04) * mm, v(118.6, 11.08) * mm]});
            skFitSpline(sketch, "E863", {"points": [v(118.6, 11.08) * mm, v(118.8, 11.16) * mm, v(119.02, 11.08) * mm, v(119.14, 10.92) * mm]});
            skFitSpline(sketch, "E864", {"points": [v(119.14, 10.92) * mm, v(119.27, 10.75) * mm, v(119.28, 10.57) * mm, v(119.18, 10.38) * mm]});
            skFitSpline(sketch, "E865", {"points": [v(119.18, 10.38) * mm, v(119.15, 10.34) * mm, v(119.12, 10.3) * mm, v(119.07, 10.22) * mm]});
            skFitSpline(sketch, "E866", {"points": [v(119.07, 10.22) * mm, v(119.18, 10.23) * mm, v(119.25, 10.23) * mm, v(119.32, 10.24) * mm]});
            skFitSpline(sketch, "E867", {"points": [v(119.32, 10.24) * mm, v(119.76, 10.3) * mm, v(120.2, 10.37) * mm, v(120.63, 10.43) * mm]});
            skFitSpline(sketch, "E868", {"points": [v(120.63, 10.43) * mm, v(120.9, 10.47) * mm, v(121.16, 10.52) * mm, v(121.43, 10.54) * mm]});
            skFitSpline(sketch, "E869", {"points": [v(121.43, 10.54) * mm, v(121.57, 10.56) * mm, v(121.64, 10.63) * mm, v(121.7, 10.75) * mm]});
            skFitSpline(sketch, "E870", {"points": [v(121.7, 10.75) * mm, v(122.05, 11.51) * mm, v(122.42, 12.28) * mm, v(122.78, 13.04) * mm]});
            skFitSpline(sketch, "E871", {"points": [v(122.78, 13.04) * mm, v(122.89, 13.27) * mm, v(123.07, 13.38) * mm, v(123.3, 13.35) * mm]});
            skFitSpline(sketch, "E872", {"points": [v(123.3, 13.35) * mm, v(123.51, 13.33) * mm, v(123.69, 13.19) * mm, v(123.72, 12.96) * mm]});
            skFitSpline(sketch, "E873", {"points": [v(123.72, 12.96) * mm, v(123.73, 12.85) * mm, v(123.7, 12.72) * mm, v(123.66, 12.62) * mm]});
            skFitSpline(sketch, "E874", {"points": [v(123.66, 12.62) * mm, v(123.45, 12.15) * mm, v(123.23, 11.7) * mm, v(123, 11.23) * mm]});
            skFitSpline(sketch, "E875", {"points": [v(123, 11.23) * mm, v(122.94, 11.08) * mm, v(122.87, 10.93) * mm, v(122.78, 10.74) * mm]});
            skFitSpline(sketch, "E876", {"points": [v(122.78, 10.74) * mm, v(122.94, 10.75) * mm, v(123.06, 10.76) * mm, v(123.19, 10.78) * mm]});
            skFitSpline(sketch, "E877", {"points": [v(123.19, 10.78) * mm, v(123.74, 10.85) * mm, v(124.3, 10.93) * mm, v(124.85, 10.99) * mm]});
            skFitSpline(sketch, "E878", {"points": [v(124.85, 10.99) * mm, v(125.18, 11.03) * mm, v(125.4, 10.86) * mm, v(125.43, 10.58) * mm]});
            skFitSpline(sketch, "E879", {"points": [v(125.43, 10.58) * mm, v(125.46, 10.27) * mm, v(125.27, 10.07) * mm, v(124.94, 10.03) * mm]});
            skFitSpline(sketch, "E880", {"points": [v(124.94, 10.03) * mm, v(124.45, 9.97) * mm, v(123.96, 9.9) * mm, v(123.47, 9.84) * mm]});
            skFitSpline(sketch, "E881", {"points": [v(123.47, 9.84) * mm, v(123.12, 9.8) * mm, v(122.77, 9.74) * mm, v(122.42, 9.7) * mm]});
            skFitSpline(sketch, "E882", {"points": [v(122.42, 9.7) * mm, v(122.31, 9.69) * mm, v(122.25, 9.65) * mm, v(122.2, 9.55) * mm]});
            skFitSpline(sketch, "E883", {"points": [v(122.2, 9.55) * mm, v(121.86, 8.86) * mm, v(121.52, 8.18) * mm, v(121.18, 7.49) * mm]});
            skFitSpline(sketch, "E884", {"points": [v(121.18, 7.49) * mm, v(121.17, 7.46) * mm, v(121.17, 7.43) * mm, v(121.16, 7.38) * mm]});
            skFitSpline(sketch, "E885", {"points": [v(121.16, 7.38) * mm, v(121.23, 7.4) * mm, v(121.27, 7.4) * mm, v(121.31, 7.42) * mm]});
            skFitSpline(sketch, "E886", {"points": [v(121.31, 7.42) * mm, v(121.56, 7.47) * mm, v(121.79, 7.35) * mm, v(121.88, 7.13) * mm]});
            skFitSpline(sketch, "E887", {"points": [v(121.88, 7.13) * mm, v(121.97, 6.9) * mm, v(121.88, 6.64) * mm, v(121.66, 6.51) * mm]});
            skFitSpline(sketch, "E888", {"points": [v(121.66, 6.51) * mm, v(121.63, 6.5) * mm, v(121.6, 6.48) * mm, v(121.57, 6.47) * mm]});
            skFitSpline(sketch, "E889", {"points": [v(121.57, 6.47) * mm, v(120.85, 6.2) * mm, v(120.13, 5.94) * mm, v(119.41, 5.68) * mm]});
            skFitSpline(sketch, "E890", {"points": [v(119.41, 5.68) * mm, v(119.08, 5.55) * mm, v(118.74, 5.42) * mm, v(118.4, 5.3) * mm]});
            skFitSpline(sketch, "E891", {"points": [v(118.4, 5.3) * mm, v(117.5, 4.96) * mm, v(116.58, 4.63) * mm, v(115.67, 4.28) * mm]});
            skFitSpline(sketch, "E892", {"points": [v(115.67, 4.28) * mm, v(115.02, 4.04) * mm, v(114.39, 3.78) * mm, v(113.75, 3.52) * mm]});
            skFitSpline(sketch, "E893", {"points": [v(113.75, 3.52) * mm, v(113.69, 3.49) * mm, v(113.62, 3.43) * mm, v(113.57, 3.37) * mm]});
            skFitSpline(sketch, "E894", {"points": [v(113.57, 3.37) * mm, v(113.27, 3.02) * mm, v(112.97, 2.67) * mm, v(112.68, 2.3) * mm]});
            skFitSpline(sketch, "E895", {"points": [v(112.68, 2.3) * mm, v(112.26, 1.76) * mm, v(111.85, 1.21) * mm, v(111.43, 0.67) * mm]});
            skFitSpline(sketch, "E896", {"points": [v(111.43, 0.67) * mm, v(111.4, 0.62) * mm, v(111.36, 0.57) * mm, v(111.32, 0.5) * mm]});
            skFitSpline(sketch, "E897", {"points": [v(111.32, 0.5) * mm, v(111.56, 0.5) * mm, v(111.77, 0.51) * mm, v(111.98, 0.53) * mm]});
            skFitSpline(sketch, "E898", {"points": [v(111.98, 0.53) * mm, v(112.03, 0.54) * mm, v(112.08, 0.58) * mm, v(112.12, 0.61) * mm]});
            skFitSpline(sketch, "E899", {"points": [v(112.12, 0.61) * mm, v(112.64, 1.22) * mm, v(113.16, 1.82) * mm, v(113.69, 2.43) * mm]});
            skFitSpline(sketch, "E900", {"points": [v(113.69, 2.43) * mm, v(113.8, 2.56) * mm, v(113.92, 2.7) * mm, v(114.05, 2.84) * mm]});
            skFitSpline(sketch, "E901", {"points": [v(114.05, 2.84) * mm, v(114.2, 3) * mm, v(114.38, 3.03) * mm, v(114.58, 2.98) * mm]});
            skFitSpline(sketch, "E902", {"points": [v(114.58, 2.98) * mm, v(114.75, 2.93) * mm, v(114.85, 2.8) * mm, v(114.9, 2.62) * mm]});
            skFitSpline(sketch, "E903", {"points": [v(114.9, 2.62) * mm, v(114.94, 2.43) * mm, v(114.85, 2.28) * mm, v(114.73, 2.14) * mm]});
            skFitSpline(sketch, "E904", {"points": [v(114.73, 2.14) * mm, v(114.3, 1.64) * mm, v(113.86, 1.14) * mm, v(113.43, 0.64) * mm]});
            skFitSpline(sketch, "E905", {"points": [v(113.43, 0.64) * mm, v(113.41, 0.61) * mm, v(113.4, 0.59) * mm, v(113.37, 0.55) * mm]});
            skFitSpline(sketch, "E906", {"points": [v(113.37, 0.55) * mm, v(113.65, 0.55) * mm, v(113.91, 0.55) * mm, v(114.17, 0.56) * mm]});
            skFitSpline(sketch, "E907", {"points": [v(114.17, 0.56) * mm, v(114.22, 0.56) * mm, v(114.28, 0.6) * mm, v(114.33, 0.65) * mm]});
            skFitSpline(sketch, "E908", {"points": [v(114.33, 0.65) * mm, v(114.65, 0.95) * mm, v(114.97, 1.26) * mm, v(115.3, 1.58) * mm]});
            skFitSpline(sketch, "E909", {"points": [v(115.3, 1.58) * mm, v(115.62, 1.9) * mm, v(115.94, 2.22) * mm, v(116.26, 2.54) * mm]});
            skFitSpline(sketch, "E910", {"points": [v(116.26, 2.54) * mm, v(116.47, 2.75) * mm, v(116.68, 2.96) * mm, v(116.89, 3.17) * mm]});
            skFitSpline(sketch, "E911", {"points": [v(116.89, 3.17) * mm, v(116.99, 3.27) * mm, v(117.1, 3.33) * mm, v(117.25, 3.33) * mm]});
            skFitSpline(sketch, "E912", {"points": [v(117.25, 3.33) * mm, v(117.45, 3.34) * mm, v(117.6, 3.26) * mm, v(117.7, 3.08) * mm]});
            skFitSpline(sketch, "E913", {"points": [v(117.7, 3.08) * mm, v(117.8, 2.9) * mm, v(117.78, 2.7) * mm, v(117.64, 2.54) * mm]});
            skFitSpline(sketch, "E914", {"points": [v(117.64, 2.54) * mm, v(117.59, 2.47) * mm, v(117.51, 2.42) * mm, v(117.45, 2.36) * mm]});
            skFitSpline(sketch, "E915", {"points": [v(117.45, 2.36) * mm, v(117.04, 1.94) * mm, v(116.63, 1.52) * mm, v(116.2, 1.1) * mm]});
            skFitSpline(sketch, "E916", {"points": [v(116.2, 1.1) * mm, v(116.02, 0.91) * mm, v(115.83, 0.74) * mm, v(115.62, 0.56) * mm]});
            skFitSpline(sketch, "E917", {"points": [v(115.62, 0.56) * mm, v(116.07, 0.47) * mm, v(116.44, 0.51) * mm, v(116.8, 0.8) * mm]});
            skFitSpline(sketch, "E918", {"points": [v(116.8, 0.8) * mm, v(117.5, 1.37) * mm, v(118.2, 1.96) * mm, v(118.82, 2.6) * mm]});
            skFitSpline(sketch, "E919", {"points": [v(118.82, 2.6) * mm, v(118.87, 2.65) * mm, v(118.91, 2.7) * mm, v(118.96, 2.74) * mm]});
            skFitSpline(sketch, "E920", {"points": [v(118.96, 2.74) * mm, v(119.27, 3.04) * mm, v(119.6, 3.34) * mm, v(119.9, 3.65) * mm]});
            skFitSpline(sketch, "E921", {"points": [v(119.9, 3.65) * mm, v(120, 3.74) * mm, v(120.08, 3.83) * mm, v(120.17, 3.93) * mm]});
            skFitSpline(sketch, "E922", {"points": [v(120.17, 3.93) * mm, v(120.31, 4.09) * mm, v(120.5, 4.13) * mm, v(120.7, 4.08) * mm]});
            skFitSpline(sketch, "E923", {"points": [v(120.7, 4.08) * mm, v(120.89, 4.03) * mm, v(121, 3.89) * mm, v(121.04, 3.7) * mm]});
            skFitSpline(sketch, "E924", {"points": [v(121.04, 3.7) * mm, v(121.07, 3.54) * mm, v(121.02, 3.4) * mm, v(120.92, 3.3) * mm]});
            skFitSpline(sketch, "E925", {"points": [v(120.92, 3.3) * mm, v(120.77, 3.12) * mm, v(120.6, 2.97) * mm, v(120.43, 2.8) * mm]});
            skFitSpline(sketch, "E926", {"points": [v(120.43, 2.8) * mm, v(119.88, 2.26) * mm, v(119.33, 1.72) * mm, v(118.74, 1.15) * mm]});
            skFitSpline(sketch, "E927", {"points": [v(118.74, 1.15) * mm, v(118.81, 1.17) * mm, v(118.85, 1.18) * mm, v(118.89, 1.2) * mm]});
            skFitSpline(sketch, "E928", {"points": [v(118.89, 1.2) * mm, v(119.15, 1.35) * mm, v(119.4, 1.52) * mm, v(119.66, 1.67) * mm]});
            skFitSpline(sketch, "E929", {"points": [v(119.66, 1.67) * mm, v(119.86, 1.78) * mm, v(120.07, 1.87) * mm, v(120.26, 1.97) * mm]});
            skFitSpline(sketch, "E930", {"points": [v(120.26, 1.97) * mm, v(120.46, 2.08) * mm, v(120.65, 2.2) * mm, v(120.83, 2.33) * mm]});
            skFitSpline(sketch, "E931", {"points": [v(120.83, 2.33) * mm, v(121.24, 2.62) * mm, v(121.49, 2.64) * mm, v(121.9, 2.33) * mm]});
            skFitSpline(sketch, "E932", {"points": [v(121.9, 2.33) * mm, v(122.58, 1.8) * mm, v(123.26, 1.27) * mm, v(123.96, 0.73) * mm]});
            skFitSpline(sketch, "E933", {"points": [v(123.96, 0.73) * mm, v(123.95, 0.73) * mm, v(123.98, 0.74) * mm, v(124, 0.76) * mm]});
            skFitSpline(sketch, "E934", {"points": [v(124, 0.76) * mm, v(124.53, 1.27) * mm, v(125.05, 1.78) * mm, v(125.57, 2.28) * mm]});
            skFitSpline(sketch, "E935", {"points": [v(125.57, 2.28) * mm, v(125.65, 2.36) * mm, v(125.75, 2.42) * mm, v(125.85, 2.45) * mm]});
            skFitSpline(sketch, "E936", {"points": [v(125.85, 2.45) * mm, v(126.07, 2.52) * mm, v(126.28, 2.43) * mm, v(126.39, 2.24) * mm]});
            skFitSpline(sketch, "E937", {"points": [v(126.39, 2.24) * mm, v(126.5, 2.06) * mm, v(126.47, 1.82) * mm, v(126.3, 1.65) * mm]});
            skFitSpline(sketch, "E938", {"points": [v(126.3, 1.65) * mm, v(125.94, 1.27) * mm, v(125.56, 0.9) * mm, v(125.18, 0.53) * mm]});
            skFitSpline(sketch, "E939", {"points": [v(125.18, 0.53) * mm, v(125, 0.36) * mm, v(124.84, 0.18) * mm, v(124.65, -0.02) * mm]});
            skFitSpline(sketch, "E940", {"points": [v(124.65, -0.02) * mm, v(124.8, -0.17) * mm, v(124.96, -0.32) * mm, v(125.12, -0.48) * mm]});
            skFitSpline(sketch, "E941", {"points": [v(125.12, -0.48) * mm, v(125.5, -0.85) * mm, v(125.88, -1.23) * mm, v(126.26, -1.6) * mm]});
            skFitSpline(sketch, "E942", {"points": [v(126.26, -1.6) * mm, v(126.37, -1.7) * mm, v(126.44, -1.82) * mm, v(126.45, -1.98) * mm]});
            skFitSpline(sketch, "E943", {"points": [v(126.45, -1.98) * mm, v(126.45, -2.17) * mm, v(126.38, -2.32) * mm, v(126.2, -2.41) * mm]});
            skFitSpline(sketch, "E944", {"points": [v(126.2, -2.41) * mm, v(126.04, -2.5) * mm, v(125.87, -2.5) * mm, v(125.7, -2.4) * mm]});
            skFitSpline(sketch, "E945", {"points": [v(125.7, -2.4) * mm, v(125.65, -2.37) * mm, v(125.6, -2.32) * mm, v(125.56, -2.27) * mm]});
            skFitSpline(sketch, "E946", {"points": [v(125.56, -2.27) * mm, v(125.04, -1.77) * mm, v(124.52, -1.26) * mm, v(124, -0.75) * mm]});
            skFitSpline(sketch, "E947", {"points": [v(124, -0.75) * mm, v(123.98, -0.74) * mm, v(123.96, -0.73) * mm, v(123.94, -0.72) * mm]});
            skFitSpline(sketch, "E948", {"points": [v(123.94, -0.72) * mm, v(123.56, -1.03) * mm, v(123.19, -1.34) * mm, v(122.8, -1.64) * mm]});
            skFitSpline(sketch, "E949", {"points": [v(122.8, -1.64) * mm, v(122.48, -1.9) * mm, v(122.14, -2.14) * mm, v(121.8, -2.39) * mm]});
            skFitSpline(sketch, "E950", {"points": [v(121.8, -2.39) * mm, v(121.55, -2.57) * mm, v(121.26, -2.63) * mm, v(121, -2.44) * mm]});
            skFitSpline(sketch, "E951", {"points": [v(121, -2.44) * mm, v(120.62, -2.15) * mm, v(120.18, -1.95) * mm, v(119.76, -1.72) * mm]});
            skFitSpline(sketch, "E952", {"points": [v(119.76, -1.72) * mm, v(119.48, -1.57) * mm, v(119.21, -1.4) * mm, v(118.94, -1.23) * mm]});
            skFitSpline(sketch, "E953", {"points": [v(118.94, -1.23) * mm, v(118.89, -1.2) * mm, v(118.83, -1.17) * mm, v(118.76, -1.13) * mm]});
            skFitSpline(sketch, "E954", {"points": [v(118.76, -1.13) * mm, v(118.88, -1.27) * mm, v(118.97, -1.38) * mm, v(119.08, -1.49) * mm]});
            skFitSpline(sketch, "E955", {"points": [v(119.08, -1.49) * mm, v(119.35, -1.75) * mm, v(119.63, -2) * mm, v(119.9, -2.25) * mm]});
            skFitSpline(sketch, "E956", {"points": [v(119.9, -2.25) * mm, v(120.14, -2.49) * mm, v(120.37, -2.73) * mm, v(120.6, -2.97) * mm]});
            skFitSpline(sketch, "E957", {"points": [v(120.6, -2.97) * mm, v(120.72, -3.08) * mm, v(120.84, -3.2) * mm, v(120.94, -3.32) * mm]});
            skFitSpline(sketch, "E958", {"points": [v(120.94, -3.32) * mm, v(121.03, -3.44) * mm, v(121.08, -3.58) * mm, v(121.03, -3.74) * mm]});
            skFitSpline(sketch, "E959", {"points": [v(121.03, -3.74) * mm, v(120.91, -4.1) * mm, v(120.47, -4.23) * mm, v(120.2, -3.96) * mm]});
            skFitSpline(sketch, "E960", {"points": [v(120.2, -3.96) * mm, v(119.94, -3.7) * mm, v(119.69, -3.42) * mm, v(119.43, -3.14) * mm]});
            skFitSpline(sketch, "E961", {"points": [v(119.43, -3.14) * mm, v(119.4, -3.1) * mm, v(119.35, -3.06) * mm, v(119.3, -3.03) * mm]});
            skFitSpline(sketch, "E962", {"points": [v(119.3, -3.03) * mm, v(118.9, -2.65) * mm, v(118.5, -2.26) * mm, v(118.08, -1.89) * mm]});
            skFitSpline(sketch, "E963", {"points": [v(118.08, -1.89) * mm, v(117.6, -1.47) * mm, v(117.11, -1.08) * mm, v(116.62, -0.68) * mm]});
            skFitSpline(sketch, "E964", {"points": [v(116.62, -0.68) * mm, v(116.45, -0.54) * mm, v(116.24, -0.49) * mm, v(116.01, -0.52) * mm]});
            skFitSpline(sketch, "E965", {"points": [v(116.01, -0.52) * mm, v(115.9, -0.53) * mm, v(115.77, -0.52) * mm, v(115.62, -0.52) * mm]});
            skFitSpline(sketch, "E966", {"points": [v(115.62, -0.52) * mm, v(115.66, -0.58) * mm, v(115.68, -0.62) * mm, v(115.71, -0.65) * mm]});
            skFitSpline(sketch, "E967", {"points": [v(115.71, -0.65) * mm, v(116.23, -1.1) * mm, v(116.71, -1.59) * mm, v(117.17, -2.1) * mm]});
            skFitSpline(sketch, "E968", {"points": [v(117.17, -2.1) * mm, v(117.3, -2.24) * mm, v(117.44, -2.35) * mm, v(117.58, -2.47) * mm]});
            skFitSpline(sketch, "E969", {"points": [v(117.58, -2.47) * mm, v(117.7, -2.59) * mm, v(117.77, -2.73) * mm, v(117.76, -2.9) * mm]});
            skFitSpline(sketch, "E970", {"points": [v(117.76, -2.9) * mm, v(117.74, -3.08) * mm, v(117.65, -3.22) * mm, v(117.48, -3.3) * mm]});
            skFitSpline(sketch, "E971", {"points": [v(117.48, -3.3) * mm, v(117.3, -3.37) * mm, v(117.12, -3.36) * mm, v(116.96, -3.23) * mm]});
            skFitSpline(sketch, "E972", {"points": [v(116.96, -3.23) * mm, v(116.8, -3.09) * mm, v(116.61, -2.94) * mm, v(116.47, -2.78) * mm]});
            skFitSpline(sketch, "E973", {"points": [v(116.47, -2.78) * mm, v(116.04, -2.3) * mm, v(115.6, -1.84) * mm, v(115.12, -1.42) * mm]});
            skFitSpline(sketch, "E974", {"points": [v(115.12, -1.42) * mm, v(114.85, -1.18) * mm, v(114.6, -0.91) * mm, v(114.34, -0.67) * mm]});
            skFitSpline(sketch, "E975", {"points": [v(114.34, -0.67) * mm, v(114.3, -0.62) * mm, v(114.23, -0.56) * mm, v(114.17, -0.56) * mm]});
            skFitSpline(sketch, "E976", {"points": [v(114.17, -0.56) * mm, v(113.91, -0.55) * mm, v(113.65, -0.56) * mm, v(113.36, -0.56) * mm]});
            skFitSpline(sketch, "E977", {"points": [v(113.36, -0.56) * mm, v(113.5, -0.7) * mm, v(113.62, -0.84) * mm, v(113.75, -0.98) * mm]});
            skFitSpline(sketch, "E978", {"points": [v(113.75, -0.98) * mm, v(114.1, -1.38) * mm, v(114.44, -1.78) * mm, v(114.77, -2.19) * mm]});
            skFitSpline(sketch, "E979", {"points": [v(114.77, -2.19) * mm, v(114.97, -2.42) * mm, v(114.94, -2.72) * mm, v(114.73, -2.9) * mm]});
            skFitSpline(sketch, "E980", {"points": [v(114.73, -2.9) * mm, v(114.52, -3.07) * mm, v(114.21, -3.03) * mm, v(114, -2.8) * mm]});
            skFitSpline(sketch, "E981", {"points": [v(114, -2.8) * mm, v(113.4, -2.1) * mm, v(112.78, -1.38) * mm, v(112.17, -0.67) * mm]});
            skFitSpline(sketch, "E982", {"points": [v(112.17, -0.67) * mm, v(112.08, -0.57) * mm, v(111.99, -0.52) * mm, v(111.85, -0.52) * mm]});
            skFitSpline(sketch, "E983", {"points": [v(111.85, -0.52) * mm, v(111.68, -0.53) * mm, v(111.52, -0.5) * mm, v(111.33, -0.5) * mm]});
            skFitSpline(sketch, "E984", {"points": [v(111.33, -0.5) * mm, v(111.35, -0.54) * mm, v(111.36, -0.57) * mm, v(111.38, -0.6) * mm]});
            skFitSpline(sketch, "E985", {"points": [v(111.38, -0.6) * mm, v(111.58, -0.87) * mm, v(111.79, -1.15) * mm, v(112, -1.42) * mm]});
            skFitSpline(sketch, "E986", {"points": [v(112, -1.42) * mm, v(112.45, -2) * mm, v(112.9, -2.56) * mm, v(113.35, -3.13) * mm]});
            skFitSpline(sketch, "E987", {"points": [v(113.35, -3.13) * mm, v(113.53, -3.35) * mm, v(113.73, -3.52) * mm, v(114, -3.62) * mm]});
            skFitSpline(sketch, "E988", {"points": [v(114, -3.62) * mm, v(115.75, -4.28) * mm, v(117.5, -4.96) * mm, v(119.24, -5.62) * mm]});
            skFitSpline(sketch, "E989", {"points": [v(119.24, -5.62) * mm, v(119.99, -5.9) * mm, v(120.74, -6.16) * mm, v(121.49, -6.44) * mm]});
            skFitSpline(sketch, "E990", {"points": [v(121.49, -6.44) * mm, v(121.56, -6.46) * mm, v(121.62, -6.5) * mm, v(121.68, -6.53) * mm]});
            skFitSpline(sketch, "E991", {"points": [v(121.68, -6.53) * mm, v(121.9, -6.66) * mm, v(121.97, -6.91) * mm, v(121.88, -7.14) * mm]});
            skFitSpline(sketch, "E992", {"points": [v(121.88, -7.14) * mm, v(121.79, -7.35) * mm, v(121.57, -7.47) * mm, v(121.33, -7.42) * mm]});
            skFitSpline(sketch, "E993", {"points": [v(121.33, -7.42) * mm, v(121.28, -7.41) * mm, v(121.22, -7.4) * mm, v(121.14, -7.38) * mm]});
            skFitSpline(sketch, "E994", {"points": [v(121.14, -7.38) * mm, v(121.19, -7.49) * mm, v(121.22, -7.57) * mm, v(121.26, -7.64) * mm]});
            skFitSpline(sketch, "E995", {"points": [v(121.26, -7.64) * mm, v(121.56, -8.25) * mm, v(121.87, -8.86) * mm, v(122.16, -9.47) * mm]});
            skFitSpline(sketch, "E996", {"points": [v(122.16, -9.47) * mm, v(122.23, -9.61) * mm, v(122.3, -9.69) * mm, v(122.47, -9.7) * mm]});
            skFitSpline(sketch, "E997", {"points": [v(122.47, -9.7) * mm, v(123.3, -9.8) * mm, v(124.14, -9.92) * mm, v(124.97, -10.03) * mm]});
            skFitSpline(sketch, "E998", {"points": [v(124.97, -10.03) * mm, v(125.27, -10.06) * mm, v(125.46, -10.29) * mm, v(125.43, -10.58) * mm]});
            skFitSpline(sketch, "E999", {"points": [v(125.43, -10.58) * mm, v(125.4, -10.86) * mm, v(125.18, -11.03) * mm, v(124.87, -11) * mm]});
            skFitSpline(sketch, "E1000", {"points": [v(124.87, -11) * mm, v(124.26, -10.92) * mm, v(123.66, -10.84) * mm, v(123.06, -10.76) * mm]});
            skFitSpline(sketch, "E1001", {"points": [v(123.06, -10.76) * mm, v(122.98, -10.76) * mm, v(122.9, -10.75) * mm, v(122.78, -10.74) * mm]});
            skFitSpline(sketch, "E1002", {"points": [v(122.78, -10.74) * mm, v(122.85, -10.89) * mm, v(122.9, -11) * mm, v(122.95, -11.13) * mm]});
            skFitSpline(sketch, "E1003", {"points": [v(122.95, -11.13) * mm, v(123.18, -11.6) * mm, v(123.41, -12.07) * mm, v(123.63, -12.55) * mm]});
            skFitSpline(sketch, "E1004", {"points": [v(123.63, -12.55) * mm, v(123.69, -12.67) * mm, v(123.73, -12.81) * mm, v(123.72, -12.94) * mm]});
            skFitSpline(sketch, "E1005", {"points": [v(123.72, -12.94) * mm, v(123.7, -13.16) * mm, v(123.54, -13.31) * mm, v(123.32, -13.35) * mm]});
            skFitSpline(sketch, "E1006", {"points": [v(123.32, -13.35) * mm, v(123.12, -13.38) * mm, v(122.92, -13.3) * mm, v(122.81, -13.1) * mm]});
            skFitSpline(sketch, "E1007", {"points": [v(122.81, -13.1) * mm, v(122.76, -13.02) * mm, v(122.73, -12.93) * mm, v(122.7, -12.84) * mm]});
            skFitSpline(sketch, "E1008", {"points": [v(122.7, -12.84) * mm, v(122.35, -12.13) * mm, v(122, -11.42) * mm, v(121.67, -10.7) * mm]});
            skFitSpline(sketch, "E1009", {"points": [v(121.67, -10.7) * mm, v(121.62, -10.59) * mm, v(121.54, -10.56) * mm, v(121.43, -10.55) * mm]});
            skFitSpline(sketch, "E1010", {"points": [v(121.43, -10.55) * mm, v(120.97, -10.49) * mm, v(120.51, -10.43) * mm, v(120.06, -10.36) * mm]});
            skFitSpline(sketch, "E1011", {"points": [v(120.06, -10.36) * mm, v(119.8, -10.33) * mm, v(119.55, -10.28) * mm, v(119.3, -10.24) * mm]});
            skFitSpline(sketch, "E1012", {"points": [v(119.3, -10.24) * mm, v(119.24, -10.23) * mm, v(119.17, -10.22) * mm, v(119.08, -10.21) * mm]});
            skFitSpline(sketch, "E1013", {"points": [v(119.08, -10.21) * mm, v(119.12, -10.28) * mm, v(119.14, -10.32) * mm, v(119.17, -10.37) * mm]});
            skFitSpline(sketch, "E1014", {"points": [v(119.17, -10.37) * mm, v(119.3, -10.6) * mm, v(119.26, -10.84) * mm, v(119.07, -11) * mm]});
            skFitSpline(sketch, "E1015", {"points": [v(119.07, -11) * mm, v(118.89, -11.15) * mm, v(118.6, -11.14) * mm, v(118.41, -10.98) * mm]});
            skFitSpline(sketch, "E1016", {"points": [v(118.41, -10.98) * mm, v(118.4, -10.95) * mm, v(118.37, -10.93) * mm, v(118.35, -10.9) * mm]});
            skFitSpline(sketch, "E1017", {"points": [v(118.35, -10.9) * mm, v(117.87, -10.3) * mm, v(117.4, -9.69) * mm, v(116.91, -9.08) * mm]});
            skFitSpline(sketch, "E1018", {"points": [v(116.91, -9.08) * mm, v(116.68, -8.78) * mm, v(116.44, -8.5) * mm, v(116.2, -8.2) * mm]});
            skFitSpline(sketch, "E1019", {"points": [v(116.2, -8.2) * mm, v(115.62, -7.45) * mm, v(115.04, -6.7) * mm, v(114.44, -5.96) * mm]});
            skFitSpline(sketch, "E1020", {"points": [v(114.44, -5.96) * mm, v(114.01, -5.43) * mm, v(113.57, -4.91) * mm, v(113.13, -4.4) * mm]});
            skFitSpline(sketch, "E1021", {"points": [v(113.13, -4.4) * mm, v(113.07, -4.33) * mm, v(112.99, -4.27) * mm, v(112.9, -4.24) * mm]});
            skFitSpline(sketch, "E1022", {"points": [v(112.9, -4.24) * mm, v(112.37, -4.03) * mm, v(111.83, -3.82) * mm, v(111.3, -3.63) * mm]});
            skFitSpline(sketch, "E1023", {"points": [v(111.3, -3.63) * mm, v(110.76, -3.43) * mm, v(110.22, -3.24) * mm, v(109.69, -3.05) * mm]});
            skFitSpline(sketch, "E1024", {"points": [v(109.69, -3.05) * mm, v(109.64, -3.04) * mm, v(109.59, -3.03) * mm, v(109.5, -3.01) * mm]});
            skFitSpline(sketch, "E1025", {"points": [v(109.5, -3.01) * mm, v(109.6, -3.24) * mm, v(109.66, -3.44) * mm, v(109.74, -3.63) * mm]});
            skFitSpline(sketch, "E1026", {"points": [v(109.74, -3.63) * mm, v(109.77, -3.69) * mm, v(109.85, -3.72) * mm, v(109.91, -3.74) * mm]});
            skFitSpline(sketch, "E1027", {"points": [v(109.91, -3.74) * mm, v(110.77, -4.11) * mm, v(111.63, -4.48) * mm, v(112.5, -4.84) * mm]});
            skFitSpline(sketch, "E1028", {"points": [v(112.5, -4.84) * mm, v(112.67, -4.91) * mm, v(112.81, -5.02) * mm, v(112.85, -5.22) * mm]});
            skFitSpline(sketch, "E1029", {"points": [v(112.85, -5.22) * mm, v(112.94, -5.6) * mm, v(112.6, -5.9) * mm, v(112.22, -5.78) * mm]});
            skFitSpline(sketch, "E1030", {"points": [v(112.22, -5.78) * mm, v(112.09, -5.74) * mm, v(111.96, -5.67) * mm, v(111.82, -5.61) * mm]});
            skFitSpline(sketch, "E1031", {"points": [v(111.82, -5.61) * mm, v(111.33, -5.4) * mm, v(110.84, -5.2) * mm, v(110.34, -5) * mm]});
            skFitSpline(sketch, "E1032", {"points": [v(110.34, -5) * mm, v(110.3, -4.98) * mm, v(110.26, -4.96) * mm, v(110.18, -4.93) * mm]});
            skFitSpline(sketch, "E1033", {"points": [v(110.18, -4.93) * mm, v(110.27, -5.21) * mm, v(110.35, -5.46) * mm, v(110.44, -5.7) * mm]});
            skFitSpline(sketch, "E1034", {"points": [v(110.44, -5.7) * mm, v(110.46, -5.75) * mm, v(110.53, -5.79) * mm, v(110.58, -5.82) * mm]});
            skFitSpline(sketch, "E1035", {"points": [v(110.58, -5.82) * mm, v(110.97, -6.03) * mm, v(111.36, -6.25) * mm, v(111.76, -6.45) * mm]});
            skFitSpline(sketch, "E1036", {"points": [v(111.76, -6.45) * mm, v(112.24, -6.7) * mm, v(112.72, -6.92) * mm, v(113.2, -7.16) * mm]});
            skFitSpline(sketch, "E1037", {"points": [v(113.2, -7.16) * mm, v(113.42, -7.28) * mm, v(113.65, -7.4) * mm, v(113.86, -7.54) * mm]});
            skFitSpline(sketch, "E1038", {"points": [v(113.86, -7.54) * mm, v(114.08, -7.7) * mm, v(114.13, -7.97) * mm, v(114, -8.18) * mm]});
            skFitSpline(sketch, "E1039", {"points": [v(114, -8.18) * mm, v(113.87, -8.4) * mm, v(113.6, -8.49) * mm, v(113.35, -8.36) * mm]});
            skFitSpline(sketch, "E1040", {"points": [v(113.35, -8.36) * mm, v(112.71, -8.04) * mm, v(112.07, -7.71) * mm, v(111.43, -7.38) * mm]});
            skFitSpline(sketch, "E1041", {"points": [v(111.43, -7.38) * mm, v(111.26, -7.3) * mm, v(111.09, -7.19) * mm, v(110.88, -7.07) * mm]});
            skFitSpline(sketch, "E1042", {"points": [v(110.88, -7.07) * mm, v(110.96, -7.45) * mm, v(111.02, -7.8) * mm, v(111.34, -8.01) * mm]});
            skFitSpline(sketch, "E1043", {"points": [v(111.34, -8.01) * mm, v(111.98, -8.45) * mm, v(112.63, -8.87) * mm, v(113.32, -9.23) * mm]});
            skFitSpline(sketch, "E1044", {"points": [v(113.32, -9.23) * mm, v(113.67, -9.4) * mm, v(114, -9.62) * mm, v(114.35, -9.8) * mm]});
            skFitSpline(sketch, "E1045", {"points": [v(114.35, -9.8) * mm, v(114.72, -10) * mm, v(115.1, -10.18) * mm, v(115.49, -10.35) * mm]});
            skFitSpline(sketch, "E1046", {"points": [v(115.49, -10.35) * mm, v(115.79, -10.5) * mm, v(115.9, -10.82) * mm, v(115.73, -11.08) * mm]});
            skFitSpline(sketch, "E1047", {"points": [v(115.73, -11.08) * mm, v(115.63, -11.25) * mm, v(115.47, -11.33) * mm, v(115.28, -11.3) * mm]});
            skFitSpline(sketch, "E1048", {"points": [v(115.28, -11.3) * mm, v(115.14, -11.27) * mm, v(115, -11.22) * mm, v(114.88, -11.16) * mm]});
            skFitSpline(sketch, "E1049", {"points": [v(114.88, -11.16) * mm, v(114.63, -11.05) * mm, v(114.4, -10.92) * mm, v(114.15, -10.8) * mm]});
            skFitSpline(sketch, "E1050", {"points": [v(114.15, -10.8) * mm, v(114.04, -10.74) * mm, v(113.92, -10.68) * mm, v(113.81, -10.62) * mm]});
            skFitSpline(sketch, "E1051", {"points": [v(113.81, -10.62) * mm, v(113.37, -10.37) * mm, v(112.93, -10.13) * mm, v(112.5, -9.89) * mm]});
            skFitSpline(sketch, "E1052", {"points": [v(112.5, -9.89) * mm, v(112.48, -9.88) * mm, v(112.46, -9.9) * mm, v(112.42, -9.9) * mm]});
            skFitSpline(sketch, "E1053", {"points": [v(112.42, -9.9) * mm, v(112.48, -9.95) * mm, v(112.52, -10) * mm, v(112.57, -10.04) * mm]});
            skFitSpline(sketch, "E1054", {"points": [v(112.57, -10.04) * mm, v(112.95, -10.39) * mm, v(113.32, -10.74) * mm, v(113.7, -11.08) * mm]});
            skFitSpline(sketch, "E1055", {"points": [v(113.7, -11.08) * mm, v(113.85, -11.22) * mm, v(114, -11.35) * mm, v(114.16, -11.47) * mm]});
            skFitSpline(sketch, "E1056", {"points": [v(114.16, -11.47) * mm, v(114.6, -11.78) * mm, v(114.66, -12) * mm, v(114.5, -12.54) * mm]});
            skFitSpline(sketch, "E1057", {"points": [v(114.5, -12.54) * mm, v(114.24, -13.34) * mm, v(113.94, -14.12) * mm, v(113.61, -14.9) * mm]});
            skFitSpline(sketch, "E1058", {"points": [v(113.61, -14.9) * mm, v(113.6, -14.9) * mm, v(113.6, -14.92) * mm, v(113.6, -14.95) * mm]});
            skFitSpline(sketch, "E1059", {"points": [v(113.6, -14.95) * mm, v(113.94, -15.13) * mm, v(114.28, -15.33) * mm, v(114.63, -15.51) * mm]});
            skFitSpline(sketch, "E1060", {"points": [v(114.63, -15.51) * mm, v(114.95, -15.68) * mm, v(115.28, -15.84) * mm, v(115.61, -16) * mm]});
            skFitSpline(sketch, "E1061", {"points": [v(115.61, -16) * mm, v(115.8, -16.1) * mm, v(115.92, -16.24) * mm, v(115.93, -16.45) * mm]});
            skFitSpline(sketch, "E1062", {"points": [v(115.93, -16.45) * mm, v(115.95, -16.75) * mm, v(115.7, -17) * mm, v(115.4, -16.95) * mm]});
            skFitSpline(sketch, "E1063", {"points": [v(115.4, -16.95) * mm, v(115.31, -16.94) * mm, v(115.23, -16.9) * mm, v(115.15, -16.87) * mm]});
            skFitSpline(sketch, "E1064", {"points": [v(115.15, -16.87) * mm, v(114.68, -16.62) * mm, v(114.2, -16.37) * mm, v(113.73, -16.12) * mm]});
            skFitSpline(sketch, "E1065", {"points": [v(113.73, -16.12) * mm, v(113.54, -16.02) * mm, v(113.35, -15.92) * mm, v(113.14, -15.81) * mm]});
            skFitSpline(sketch, "E1066", {"points": [v(113.14, -15.81) * mm, v(113.03, -16.04) * mm, v(112.92, -16.26) * mm, v(112.82, -16.47) * mm]});
            skFitSpline(sketch, "E1067", {"points": [v(112.82, -16.47) * mm, v(112.58, -16.95) * mm, v(112.35, -17.43) * mm, v(112.1, -17.9) * mm]});
            skFitSpline(sketch, "E1068", {"points": [v(112.1, -17.9) * mm, v(111.95, -18.18) * mm, v(111.7, -18.27) * mm, v(111.46, -18.15) * mm]});
            skFitSpline(sketch, "E1069", {"points": [v(111.46, -18.15) * mm, v(111.2, -18.02) * mm, v(111.1, -17.74) * mm, v(111.23, -17.46) * mm]});
            skFitSpline(sketch, "E1070", {"points": [v(111.23, -17.46) * mm, v(111.4, -17.14) * mm, v(111.56, -16.83) * mm, v(111.72, -16.52) * mm]});
            skFitSpline(sketch, "E1071", {"points": [v(111.72, -16.52) * mm, v(111.9, -16.15) * mm, v(112.07, -15.77) * mm, v(112.26, -15.38) * mm]});
            skFitSpline(sketch, "E1072", {"points": [v(112.26, -15.38) * mm, v(112.2, -15.35) * mm, v(112.15, -15.31) * mm, v(112.1, -15.28) * mm]});
            skFitSpline(sketch, "E1073", {"points": [v(112.1, -15.28) * mm, v(111.4, -14.82) * mm, v(110.71, -14.36) * mm, v(110.03, -13.9) * mm]});
            skFitSpline(sketch, "E1074", {"points": [v(110.03, -13.9) * mm, v(109.73, -13.69) * mm, v(109.58, -13.49) * mm, v(109.74, -12.98) * mm]});
            skFitSpline(sketch, "E1075", {"points": [v(109.74, -12.98) * mm, v(109.84, -12.66) * mm, v(109.9, -12.34) * mm, v(109.95, -12.02) * mm]});
            skFitSpline(sketch, "E1076", {"points": [v(109.95, -12.02) * mm, v(110.02, -11.56) * mm, v(110.14, -11.11) * mm, v(110.24, -10.66) * mm]});
            skFitSpline(sketch, "E1077", {"points": [v(110.24, -10.66) * mm, v(110.25, -10.63) * mm, v(110.25, -10.6) * mm, v(110.23, -10.55) * mm]});
            skFitSpline(sketch, "E1078", {"points": [v(110.23, -10.55) * mm, v(110.13, -10.75) * mm, v(110.02, -10.96) * mm, v(109.93, -11.16) * mm]});
            skFitSpline(sketch, "E1079", {"points": [v(109.93, -11.16) * mm, v(109.78, -11.47) * mm, v(109.65, -11.78) * mm, v(109.5, -12.08) * mm]});
            skFitSpline(sketch, "E1080", {"points": [v(109.5, -12.08) * mm, v(109.32, -12.46) * mm, v(109.12, -12.83) * mm, v(108.93, -13.2) * mm]});
            skFitSpline(sketch, "E1081", {"points": [v(108.93, -13.2) * mm, v(108.9, -13.27) * mm, v(108.85, -13.33) * mm, v(108.8, -13.38) * mm]});
            skFitSpline(sketch, "E1082", {"points": [v(108.8, -13.38) * mm, v(108.63, -13.57) * mm, v(108.38, -13.6) * mm, v(108.17, -13.47) * mm]});
            skFitSpline(sketch, "E1083", {"points": [v(108.17, -13.47) * mm, v(107.97, -13.33) * mm, v(107.89, -13.06) * mm, v(108, -12.83) * mm]});
            skFitSpline(sketch, "E1084", {"points": [v(108, -12.83) * mm, v(108.18, -12.5) * mm, v(108.36, -12.17) * mm, v(108.54, -11.84) * mm]});
            skFitSpline(sketch, "E1085", {"points": [v(108.54, -11.84) * mm, v(108.57, -11.79) * mm, v(108.6, -11.73) * mm, v(108.62, -11.67) * mm]});
            skFitSpline(sketch, "E1086", {"points": [v(108.62, -11.67) * mm, v(108.86, -11.16) * mm, v(109.1, -10.66) * mm, v(109.33, -10.15) * mm]});
            skFitSpline(sketch, "E1087", {"points": [v(109.33, -10.15) * mm, v(109.4, -9.98) * mm, v(109.5, -9.8) * mm, v(109.56, -9.63) * mm]});
            skFitSpline(sketch, "E1088", {"points": [v(109.56, -9.63) * mm, v(109.7, -9.25) * mm, v(109.84, -8.88) * mm, v(109.99, -8.5) * mm]});
            skFitSpline(sketch, "E1089", {"points": [v(109.99, -8.5) * mm, v(110.09, -8.26) * mm, v(110.1, -8.01) * mm, v(109.98, -7.77) * mm]});
            skFitSpline(sketch, "E1090", {"points": [v(109.98, -7.77) * mm, v(109.93, -7.67) * mm, v(109.9, -7.56) * mm, v(109.84, -7.42) * mm]});
            skFitSpline(sketch, "E1091", {"points": [v(109.84, -7.42) * mm, v(109.8, -7.5) * mm, v(109.77, -7.53) * mm, v(109.75, -7.58) * mm]});
            skFitSpline(sketch, "E1092", {"points": [v(109.75, -7.58) * mm, v(109.5, -8.2) * mm, v(109.18, -8.77) * mm, v(108.85, -9.35) * mm]});
            skFitSpline(sketch, "E1093", {"points": [v(108.85, -9.35) * mm, v(108.75, -9.52) * mm, v(108.69, -9.71) * mm, v(108.6, -9.9) * mm]});
            skFitSpline(sketch, "E1094", {"points": [v(108.6, -9.9) * mm, v(108.5, -10.1) * mm, v(108.29, -10.22) * mm, v(108.07, -10.18) * mm]});
            skFitSpline(sketch, "E1095", {"points": [v(108.07, -10.18) * mm, v(107.76, -10.12) * mm, v(107.58, -9.81) * mm, v(107.7, -9.5) * mm]});
            skFitSpline(sketch, "E1096", {"points": [v(107.7, -9.5) * mm, v(107.8, -9.27) * mm, v(107.91, -9.03) * mm, v(108.04, -8.81) * mm]});
            skFitSpline(sketch, "E1097", {"points": [v(108.04, -8.81) * mm, v(108.34, -8.27) * mm, v(108.63, -7.72) * mm, v(108.88, -7.14) * mm]});
            skFitSpline(sketch, "E1098", {"points": [v(108.88, -7.14) * mm, v(109, -6.84) * mm, v(109.16, -6.55) * mm, v(109.32, -6.27) * mm]});
            skFitSpline(sketch, "E1099", {"points": [v(109.32, -6.27) * mm, v(109.38, -6.16) * mm, v(109.4, -6.07) * mm, v(109.36, -5.95) * mm]});
            skFitSpline(sketch, "E1100", {"points": [v(109.36, -5.95) * mm, v(109.28, -5.74) * mm, v(109.22, -5.53) * mm, v(109.14, -5.29) * mm]});
            skFitSpline(sketch, "E1101", {"points": [v(109.14, -5.29) * mm, v(109.1, -5.35) * mm, v(109.06, -5.39) * mm, v(109.03, -5.44) * mm]});
            skFitSpline(sketch, "E1102", {"points": [v(109.03, -5.44) * mm, v(108.7, -5.98) * mm, v(108.37, -6.53) * mm, v(108.04, -7.08) * mm]});
            skFitSpline(sketch, "E1103", {"points": [v(108.04, -7.08) * mm, v(107.92, -7.27) * mm, v(107.76, -7.39) * mm, v(107.53, -7.36) * mm]});
            skFitSpline(sketch, "E1104", {"points": [v(107.53, -7.36) * mm, v(107.32, -7.34) * mm, v(107.2, -7.22) * mm, v(107.12, -7.03) * mm]});
            skFitSpline(sketch, "E1105", {"points": [v(107.12, -7.03) * mm, v(107.07, -6.89) * mm, v(107.1, -6.75) * mm, v(107.17, -6.62) * mm]});
            skFitSpline(sketch, "E1106", {"points": [v(107.17, -6.62) * mm, v(107.24, -6.5) * mm, v(107.31, -6.38) * mm, v(107.38, -6.27) * mm]});
            skFitSpline(sketch, "E1107", {"points": [v(107.38, -6.27) * mm, v(107.81, -5.56) * mm, v(108.24, -4.85) * mm, v(108.67, -4.14) * mm]});
            skFitSpline(sketch, "E1108", {"points": [v(108.67, -4.14) * mm, v(108.73, -4.05) * mm, v(108.74, -3.97) * mm, v(108.7, -3.87) * mm]});
            skFitSpline(sketch, "E1109", {"points": [v(108.7, -3.87) * mm, v(108.65, -3.7) * mm, v(108.6, -3.52) * mm, v(108.56, -3.31) * mm]});
            skFitSpline(sketch, "E1110", {"points": [v(108.56, -3.31) * mm, v(108.5, -3.38) * mm, v(108.45, -3.43) * mm, v(108.42, -3.48) * mm]});
            skFitSpline(sketch, "E1111", {"points": [v(108.42, -3.48) * mm, v(108.08, -3.97) * mm, v(107.74, -4.46) * mm, v(107.4, -4.96) * mm]});
            skFitSpline(sketch, "E1112", {"points": [v(107.4, -4.96) * mm, v(107.1, -5.42) * mm, v(106.8, -5.9) * mm, v(106.5, -6.37) * mm]});
            skFitSpline(sketch, "E1113", {"points": [v(106.5, -6.37) * mm, v(106.45, -6.43) * mm, v(106.43, -6.51) * mm, v(106.42, -6.59) * mm]});
            skFitSpline(sketch, "E1114", {"points": [v(106.42, -6.59) * mm, v(106.39, -7.13) * mm, v(106.35, -7.67) * mm, v(106.33, -8.21) * mm]});
            skFitSpline(sketch, "E1115", {"points": [v(106.33, -8.21) * mm, v(106.3, -8.91) * mm, v(106.26, -9.61) * mm, v(106.23, -10.32) * mm]});
            skFitSpline(sketch, "E1116", {"points": [v(106.23, -10.32) * mm, v(106.2, -10.92) * mm, v(106.17, -11.53) * mm, v(106.15, -12.13) * mm]});
            skFitSpline(sketch, "E1117", {"points": [v(106.15, -12.13) * mm, v(106.12, -12.58) * mm, v(106.1, -13.02) * mm, v(106.09, -13.47) * mm]});
            skFitSpline(sketch, "E1118", {"points": [v(106.09, -13.47) * mm, v(106.07, -13.94) * mm, v(106.05, -14.41) * mm, v(106.04, -14.88) * mm]});
            skFitSpline(sketch, "E1119", {"points": [v(106.04, -14.88) * mm, v(106.03, -15.2) * mm, v(105.82, -15.4) * mm, v(105.53, -15.4) * mm]});
            skFitSpline(sketch, "E1120", {"points": [v(105.53, -15.4) * mm, v(105.24, -15.4) * mm, v(105.06, -15.18) * mm, v(105.06, -14.86) * mm]});
            skFitSpline(sketch, "E1121", {"points": [v(105.06, -14.86) * mm, v(105.06, -14.84) * mm, v(105.06, -14.83) * mm, v(105.05, -14.79) * mm]});
            skFitSpline(sketch, "E1122", {"points": [v(105.05, -14.79) * mm, v(105, -14.82) * mm, v(104.96, -14.84) * mm, v(104.92, -14.88) * mm]});
            skFitSpline(sketch, "E1123", {"points": [v(104.92, -14.88) * mm, v(104.4, -15.4) * mm, v(103.87, -15.9) * mm, v(103.34, -16.42) * mm]});
            skFitSpline(sketch, "E1124", {"points": [v(103.34, -16.42) * mm, v(103.24, -16.51) * mm, v(103.2, -16.6) * mm, v(103.24, -16.75) * mm]});
            skFitSpline(sketch, "E1125", {"points": [v(103.24, -16.75) * mm, v(103.37, -17.4) * mm, v(103.48, -18.07) * mm, v(103.6, -18.73) * mm]});
            skFitSpline(sketch, "E1126", {"points": [v(103.6, -18.73) * mm, v(103.63, -18.9) * mm, v(103.68, -19.09) * mm, v(103.71, -19.27) * mm]});
            skFitSpline(sketch, "E1127", {"points": [v(103.71, -19.27) * mm, v(103.76, -19.54) * mm, v(103.6, -19.79) * mm, v(103.34, -19.85) * mm]});
            skFitSpline(sketch, "E1128", {"points": [v(103.34, -19.85) * mm, v(103.09, -19.9) * mm, v(102.84, -19.77) * mm, v(102.78, -19.5) * mm]});
            skFitSpline(sketch, "E1129", {"points": [v(102.78, -19.5) * mm, v(102.68, -19.14) * mm, v(102.62, -18.77) * mm, v(102.55, -18.4) * mm]});
            skFitSpline(sketch, "E1130", {"points": [v(102.55, -18.4) * mm, v(102.5, -18.12) * mm, v(102.45, -17.83) * mm, v(102.4, -17.55) * mm]});
            skFitSpline(sketch, "E1131", {"points": [v(102.4, -17.55) * mm, v(102.39, -17.5) * mm, v(102.37, -17.46) * mm, v(102.34, -17.39) * mm]});
            skFitSpline(sketch, "E1132", {"points": [v(102.34, -17.39) * mm, v(102.23, -17.49) * mm, v(102.13, -17.58) * mm, v(102.03, -17.67) * mm]});
            skFitSpline(sketch, "E1133", {"points": [v(102.03, -17.67) * mm, v(101.65, -18.03) * mm, v(101.27, -18.4) * mm, v(100.88, -18.76) * mm]});
            skFitSpline(sketch, "E1134", {"points": [v(100.88, -18.76) * mm, v(100.84, -18.8) * mm, v(100.79, -18.84) * mm, v(100.74, -18.88) * mm]});
            skFitSpline(sketch, "E1135", {"points": [v(100.74, -18.88) * mm, v(100.53, -19.01) * mm, v(100.3, -18.99) * mm, v(100.12, -18.82) * mm]});
            skFitSpline(sketch, "E1136", {"points": [v(100.12, -18.82) * mm, v(99.96, -18.65) * mm, v(99.94, -18.37) * mm, v(100.08, -18.18) * mm]});
            skFitSpline(sketch, "E1137", {"points": [v(100.08, -18.18) * mm, v(100.12, -18.13) * mm, v(100.17, -18.09) * mm, v(100.21, -18.04) * mm]});
            skFitSpline(sketch, "E1138", {"points": [v(100.21, -18.04) * mm, v(100.81, -17.48) * mm, v(101.4, -16.9) * mm, v(102, -16.35) * mm]});
            skFitSpline(sketch, "E1139", {"points": [v(102, -16.35) * mm, v(102.13, -16.24) * mm, v(102.14, -16.14) * mm, v(102.12, -16) * mm]});
            skFitSpline(sketch, "E1140", {"points": [v(102.12, -16) * mm, v(102, -15.3) * mm, v(101.88, -14.63) * mm, v(101.77, -13.94) * mm]});
            skFitSpline(sketch, "E1141", {"points": [v(101.77, -13.94) * mm, v(101.75, -13.87) * mm, v(101.73, -13.8) * mm, v(101.7, -13.69) * mm]});
            skFitSpline(sketch, "E1142", {"points": [v(101.7, -13.69) * mm, v(101.65, -13.76) * mm, v(101.61, -13.8) * mm, v(101.57, -13.85) * mm]});
            skFitSpline(sketch, "E1143", {"points": [v(101.57, -13.85) * mm, v(101.4, -14.03) * mm, v(101.16, -14.05) * mm, v(100.96, -13.92) * mm]});
            skFitSpline(sketch, "E1144", {"points": [v(100.96, -13.92) * mm, v(100.76, -13.8) * mm, v(100.68, -13.55) * mm, v(100.77, -13.33) * mm]});
            skFitSpline(sketch, "E1145", {"points": [v(100.77, -13.33) * mm, v(100.78, -13.28) * mm, v(100.81, -13.23) * mm, v(100.84, -13.19) * mm]});
            skFitSpline(sketch, "E1146", {"points": [v(100.84, -13.19) * mm, v(101.83, -11.7) * mm, v(102.83, -10.23) * mm, v(103.81, -8.74) * mm]});
            skFitSpline(sketch, "E1147", {"points": [v(103.81, -8.74) * mm, v(104.36, -7.9) * mm, v(104.9, -7.06) * mm, v(105.42, -6.21) * mm]});
            skFitSpline(sketch, "E1148", {"points": [v(105.42, -6.21) * mm, v(105.5, -6.08) * mm, v(105.5, -5.9) * mm, v(105.5, -5.73) * mm]});
            skFitSpline(sketch, "E1149", {"points": [v(105.5, -5.73) * mm, v(105.54, -5.08) * mm, v(105.55, -4.44) * mm, v(105.58, -3.8) * mm]});
            skFitSpline(sketch, "E1150", {"points": [v(105.58, -3.8) * mm, v(105.59, -3.38) * mm, v(105.6, -2.96) * mm, v(105.62, -2.55) * mm]});
            skFitSpline(sketch, "E1151", {"points": [v(105.62, -2.55) * mm, v(105.62, -2.5) * mm, v(105.61, -2.44) * mm, v(105.6, -2.36) * mm]});
            skFitSpline(sketch, "E1152", {"points": [v(105.6, -2.36) * mm, v(105.4, -2.52) * mm, v(105.23, -2.66) * mm, v(105.03, -2.82) * mm]});
            skFitSpline(sketch, "E1153", {"points": [v(105.03, -2.82) * mm, v(104.97, -3.58) * mm, v(104.9, -4.36) * mm, v(104.84, -5.14) * mm]});
            skFitSpline(sketch, "E1154", {"points": [v(104.84, -5.14) * mm, v(104.82, -5.36) * mm, v(104.8, -5.58) * mm, v(104.79, -5.8) * mm]});
            skFitSpline(sketch, "E1155", {"points": [v(104.79, -5.8) * mm, v(104.76, -6.11) * mm, v(104.52, -6.33) * mm, v(104.25, -6.3) * mm]});
            skFitSpline(sketch, "E1156", {"points": [v(104.25, -6.3) * mm, v(103.95, -6.27) * mm, v(103.77, -6) * mm, v(103.8, -5.67) * mm]});
            skFitSpline(sketch, "E1157", {"points": [v(103.8, -5.67) * mm, v(103.84, -5.4) * mm, v(103.86, -5.11) * mm, v(103.88, -4.84) * mm]});
            skFitSpline(sketch, "E1158", {"points": [v(103.88, -4.84) * mm, v(103.9, -4.53) * mm, v(103.93, -4.23) * mm, v(103.96, -3.93) * mm]});
            skFitSpline(sketch, "E1159", {"points": [v(103.96, -3.93) * mm, v(103.97, -3.83) * mm, v(103.98, -3.73) * mm, v(104, -3.59) * mm]});
            skFitSpline(sketch, "E1160", {"points": [v(104, -3.59) * mm, v(103.74, -3.77) * mm, v(103.53, -3.93) * mm, v(103.33, -4.09) * mm]});
            skFitSpline(sketch, "E1161", {"points": [v(103.33, -4.09) * mm, v(103.3, -4.11) * mm, v(103.26, -4.16) * mm, v(103.26, -4.2) * mm]});
            skFitSpline(sketch, "E1162", {"points": [v(103.26, -4.2) * mm, v(103.22, -4.88) * mm, v(103, -5.53) * mm, v(102.9, -6.2) * mm]});
            skFitSpline(sketch, "E1163", {"points": [v(102.9, -6.2) * mm, v(102.86, -6.52) * mm, v(102.83, -6.84) * mm, v(102.79, -7.15) * mm]});
            skFitSpline(sketch, "E1164", {"points": [v(102.79, -7.15) * mm, v(102.75, -7.4) * mm, v(102.71, -7.64) * mm, v(102.65, -7.88) * mm]});
            skFitSpline(sketch, "E1165", {"points": [v(102.65, -7.88) * mm, v(102.57, -8.16) * mm, v(102.3, -8.3) * mm, v(102.05, -8.23) * mm]});
            skFitSpline(sketch, "E1166", {"points": [v(102.05, -8.23) * mm, v(101.8, -8.16) * mm, v(101.66, -7.91) * mm, v(101.7, -7.63) * mm]});
            skFitSpline(sketch, "E1167", {"points": [v(101.7, -7.63) * mm, v(101.8, -7.08) * mm, v(101.87, -6.51) * mm, v(101.96, -5.96) * mm]});
            skFitSpline(sketch, "E1168", {"points": [v(101.96, -5.96) * mm, v(102.01, -5.67) * mm, v(102.08, -5.38) * mm, v(102.14, -5.09) * mm]});
            skFitSpline(sketch, "E1169", {"points": [v(102.14, -5.09) * mm, v(102.14, -5.04) * mm, v(102.15, -5) * mm, v(102.15, -4.93) * mm]});
            skFitSpline(sketch, "E1170", {"points": [v(102.15, -4.93) * mm, v(101.78, -5.13) * mm, v(101.5, -5.34) * mm, v(101.37, -5.77) * mm]});
            skFitSpline(sketch, "E1171", {"points": [v(101.37, -5.77) * mm, v(101.11, -6.7) * mm, v(100.9, -7.62) * mm, v(100.76, -8.57) * mm]});
            skFitSpline(sketch, "E1172", {"points": [v(100.76, -8.57) * mm, v(100.76, -8.6) * mm, v(100.75, -8.62) * mm, v(100.75, -8.64) * mm]});
            skFitSpline(sketch, "E1173", {"points": [v(100.75, -8.64) * mm, v(100.6, -9.2) * mm, v(100.54, -9.77) * mm, v(100.47, -10.34) * mm]});
            skFitSpline(sketch, "E1174", {"points": [v(100.47, -10.34) * mm, v(100.43, -10.62) * mm, v(100.2, -10.8) * mm, v(99.94, -10.8) * mm]});
            skFitSpline(sketch, "E1175", {"points": [v(99.94, -10.8) * mm, v(99.69, -10.78) * mm, v(99.48, -10.57) * mm, v(99.49, -10.3) * mm]});
            skFitSpline(sketch, "E1176", {"points": [v(99.49, -10.3) * mm, v(99.5, -10.08) * mm, v(99.55, -9.86) * mm, v(99.58, -9.64) * mm]});
            skFitSpline(sketch, "E1177", {"points": [v(99.58, -9.64) * mm, v(99.6, -9.46) * mm, v(99.62, -9.27) * mm, v(99.65, -9.1) * mm]});
            skFitSpline(sketch, "E1178", {"points": [v(99.65, -9.1) * mm, v(99.76, -8.51) * mm, v(99.88, -7.94) * mm, v(99.99, -7.36) * mm]});
            skFitSpline(sketch, "E1179", {"points": [v(99.99, -7.36) * mm, v(100, -7.32) * mm, v(100, -7.28) * mm, v(99.97, -7.23) * mm]});
            skFitSpline(sketch, "E1180", {"points": [v(99.97, -7.23) * mm, v(99.94, -7.3) * mm, v(99.9, -7.35) * mm, v(99.88, -7.41) * mm]});
            skFitSpline(sketch, "E1181", {"points": [v(99.88, -7.41) * mm, v(99.66, -7.9) * mm, v(99.44, -8.37) * mm, v(99.22, -8.85) * mm]});
            skFitSpline(sketch, "E1182", {"points": [v(99.22, -8.85) * mm, v(99.13, -9.04) * mm, v(99.05, -9.23) * mm, v(98.99, -9.43) * mm]});
            skFitSpline(sketch, "E1183", {"points": [v(98.99, -9.43) * mm, v(98.84, -9.9) * mm, v(98.64, -10.05) * mm, v(98.15, -10.05) * mm]});
            skFitSpline(sketch, "E1184", {"points": [v(98.15, -10.05) * mm, v(97.3, -10.06) * mm, v(96.45, -10.02) * mm, v(95.6, -9.93) * mm]});
            skFitSpline(sketch, "E1185", {"points": [v(95.6, -9.93) * mm, v(95.57, -9.93) * mm, v(95.55, -9.94) * mm, v(95.51, -9.95) * mm]});
            skFitSpline(sketch, "E1186", {"points": [v(95.51, -9.95) * mm, v(95.43, -10.41) * mm, v(95.34, -10.88) * mm, v(95.26, -11.35) * mm]});
            skFitSpline(sketch, "E1187", {"points": [v(95.26, -11.35) * mm, v(95.2, -11.65) * mm, v(95.16, -11.95) * mm, v(95.11, -12.25) * mm]});
            skFitSpline(sketch, "E1188", {"points": [v(95.11, -12.25) * mm, v(95.07, -12.5) * mm, v(94.85, -12.68) * mm, v(94.6, -12.66) * mm]});
            skFitSpline(sketch, "E1189", {"points": [v(94.6, -12.66) * mm, v(94.34, -12.65) * mm, v(94.14, -12.44) * mm, v(94.16, -12.16) * mm]});
            skFitSpline(sketch, "E1190", {"points": [v(94.16, -12.16) * mm, v(94.18, -11.9) * mm, v(94.22, -11.64) * mm, v(94.27, -11.38) * mm]});
            skFitSpline(sketch, "E1191", {"points": [v(94.27, -11.38) * mm, v(94.34, -10.92) * mm, v(94.43, -10.46) * mm, v(94.52, -10) * mm]});
            skFitSpline(sketch, "E1192", {"points": [v(94.52, -10) * mm, v(94.53, -9.93) * mm, v(94.53, -9.87) * mm, v(94.54, -9.78) * mm]});
            skFitSpline(sketch, "E1193", {"points": [v(94.54, -9.78) * mm, v(94.35, -9.75) * mm, v(94.17, -9.72) * mm, v(94, -9.69) * mm]});
            skFitSpline(sketch, "E1194", {"points": [v(94, -9.69) * mm, v(93.43, -9.6) * mm, v(92.86, -9.53) * mm, v(92.3, -9.44) * mm]});
            skFitSpline(sketch, "E1195", {"points": [v(92.3, -9.44) * mm, v(92.24, -9.44) * mm, v(92.2, -9.42) * mm, v(92.15, -9.4) * mm]});
            skFitSpline(sketch, "E1196", {"points": [v(92.15, -9.4) * mm, v(91.91, -9.33) * mm, v(91.77, -9.1) * mm, v(91.8, -8.87) * mm]});
            skFitSpline(sketch, "E1197", {"points": [v(91.8, -8.87) * mm, v(91.85, -8.64) * mm, v(92.04, -8.48) * mm, v(92.28, -8.47) * mm]});
            skFitSpline(sketch, "E1198", {"points": [v(92.28, -8.47) * mm, v(92.38, -8.47) * mm, v(92.48, -8.5) * mm, v(92.59, -8.5) * mm]});
            skFitSpline(sketch, "E1199", {"points": [v(92.59, -8.5) * mm, v(93.28, -8.6) * mm, v(93.97, -8.7) * mm, v(94.68, -8.81) * mm]});
            skFitSpline(sketch, "E1200", {"points": [v(94.68, -8.81) * mm, v(94.7, -8.74) * mm, v(94.72, -8.7) * mm, v(94.73, -8.64) * mm]});
            skFitSpline(sketch, "E1201", {"points": [v(94.73, -8.64) * mm, v(94.93, -7.83) * mm, v(95.14, -7.02) * mm, v(95.41, -6.22) * mm]});
            skFitSpline(sketch, "E1202", {"points": [v(95.41, -6.22) * mm, v(95.55, -5.8) * mm, v(95.76, -5.66) * mm, v(96.2, -5.66) * mm]});
            skFitSpline(sketch, "E1203", {"points": [v(96.2, -5.66) * mm, v(96.52, -5.67) * mm, v(96.83, -5.62) * mm, v(97.15, -5.57) * mm]});
            skFitSpline(sketch, "E1204", {"points": [v(97.15, -5.57) * mm, v(97.52, -5.5) * mm, v(97.9, -5.49) * mm, v(98.29, -5.45) * mm]});
            skFitSpline(sketch, "E1205", {"points": [v(98.29, -5.45) * mm, v(98.42, -5.44) * mm, v(98.55, -5.42) * mm, v(98.7, -5.38) * mm]});
            skFitSpline(sketch, "E1206", {"points": [v(98.7, -5.38) * mm, v(98.45, -5.35) * mm, v(98.2, -5.3) * mm, v(97.95, -5.28) * mm]});
            skFitSpline(sketch, "E1207", {"points": [v(97.95, -5.28) * mm, v(97.57, -5.23) * mm, v(97.18, -5.19) * mm, v(96.8, -5.13) * mm]});
            skFitSpline(sketch, "E1208", {"points": [v(96.8, -5.13) * mm, v(96.45, -5.09) * mm, v(96.11, -5.03) * mm, v(95.78, -4.98) * mm]});
            skFitSpline(sketch, "E1209", {"points": [v(95.78, -4.98) * mm, v(95.7, -4.96) * mm, v(95.6, -4.93) * mm, v(95.53, -4.9) * mm]});
            skFitSpline(sketch, "E1210", {"points": [v(95.53, -4.9) * mm, v(95.29, -4.79) * mm, v(95.18, -4.56) * mm, v(95.26, -4.3) * mm]});
            skFitSpline(sketch, "E1211", {"points": [v(95.26, -4.3) * mm, v(95.32, -4.08) * mm, v(95.56, -3.93) * mm, v(95.8, -3.97) * mm]});
            skFitSpline(sketch, "E1212", {"points": [v(95.8, -3.97) * mm, v(96.17, -4.03) * mm, v(96.54, -4.1) * mm, v(96.9, -4.17) * mm]});
            skFitSpline(sketch, "E1213", {"points": [v(96.9, -4.17) * mm, v(96.95, -4.18) * mm, v(97, -4.2) * mm, v(97.05, -4.2) * mm]});
            skFitSpline(sketch, "E1214", {"points": [v(97.05, -4.2) * mm, v(97.73, -4.28) * mm, v(98.42, -4.37) * mm, v(99.11, -4.44) * mm]});
            skFitSpline(sketch, "E1215", {"points": [v(99.11, -4.44) * mm, v(99.55, -4.5) * mm, v(100, -4.5) * mm, v(100.45, -4.54) * mm]});
            skFitSpline(sketch, "E1216", {"points": [v(100.45, -4.54) * mm, v(100.88, -4.56) * mm, v(101.2, -4.35) * mm, v(101.5, -4.03) * mm]});
            skFitSpline(sketch, "E1217", {"points": [v(101.5, -4.03) * mm, v(101.13, -3.98) * mm, v(100.78, -3.94) * mm, v(100.44, -3.9) * mm]});
            skFitSpline(sketch, "E1218", {"points": [v(100.44, -3.9) * mm, v(100.14, -3.85) * mm, v(99.85, -3.79) * mm, v(99.56, -3.74) * mm]});
            skFitSpline(sketch, "E1219", {"points": [v(99.56, -3.74) * mm, v(99.3, -3.7) * mm, v(99.03, -3.66) * mm, v(98.76, -3.62) * mm]});
            skFitSpline(sketch, "E1220", {"points": [v(98.76, -3.62) * mm, v(98.41, -3.56) * mm, v(98.23, -3.21) * mm, v(98.4, -2.91) * mm]});
            skFitSpline(sketch, "E1221", {"points": [v(98.4, -2.91) * mm, v(98.48, -2.76) * mm, v(98.62, -2.66) * mm, v(98.8, -2.67) * mm]});
            skFitSpline(sketch, "E1222", {"points": [v(98.8, -2.67) * mm, v(99.05, -2.68) * mm, v(99.31, -2.69) * mm, v(99.56, -2.74) * mm]});
            skFitSpline(sketch, "E1223", {"points": [v(99.56, -2.74) * mm, v(100.3, -2.9) * mm, v(101.04, -3) * mm, v(101.78, -3.07) * mm]});
            skFitSpline(sketch, "E1224", {"points": [v(101.78, -3.07) * mm, v(102, -3.1) * mm, v(102.23, -3.13) * mm, v(102.44, -3.19) * mm]});
            skFitSpline(sketch, "E1225", {"points": [v(102.44, -3.19) * mm, v(102.58, -3.22) * mm, v(102.67, -3.2) * mm, v(102.78, -3.12) * mm]});
            skFitSpline(sketch, "E1226", {"points": [v(102.78, -3.12) * mm, v(102.95, -2.98) * mm, v(103.13, -2.86) * mm, v(103.34, -2.7) * mm]});
            skFitSpline(sketch, "E1227", {"points": [v(103.34, -2.7) * mm, v(103.16, -2.66) * mm, v(103, -2.63) * mm, v(102.86, -2.6) * mm]});
            skFitSpline(sketch, "E1228", {"points": [v(102.86, -2.6) * mm, v(102.32, -2.47) * mm, v(101.78, -2.34) * mm, v(101.25, -2.21) * mm]});
            skFitSpline(sketch, "E1229", {"points": [v(101.25, -2.21) * mm, v(100.96, -2.14) * mm, v(100.79, -1.89) * mm, v(100.84, -1.65) * mm]});
            skFitSpline(sketch, "E1230", {"points": [v(100.84, -1.65) * mm, v(100.91, -1.35) * mm, v(101.17, -1.19) * mm, v(101.48, -1.26) * mm]});
            skFitSpline(sketch, "E1231", {"points": [v(101.48, -1.26) * mm, v(101.92, -1.37) * mm, v(102.36, -1.49) * mm, v(102.8, -1.6) * mm]});
            skFitSpline(sketch, "E1232", {"points": [v(102.8, -1.6) * mm, v(103.3, -1.7) * mm, v(103.79, -1.8) * mm, v(104.28, -1.92) * mm]});
            skFitSpline(sketch, "E1233", {"points": [v(104.28, -1.92) * mm, v(104.38, -1.94) * mm, v(104.46, -1.92) * mm, v(104.54, -1.86) * mm]});
            skFitSpline(sketch, "E1234", {"points": [v(104.54, -1.86) * mm, v(104.69, -1.75) * mm, v(104.85, -1.66) * mm, v(105.01, -1.55) * mm]});
            skFitSpline(sketch, "E1235", {"points": [v(105.01, -1.55) * mm, v(104.97, -1.53) * mm, v(104.94, -1.5) * mm, v(104.91, -1.5) * mm]});
            skFitSpline(sketch, "E1236", {"points": [v(104.91, -1.5) * mm, v(104, -1.24) * mm, v(103.09, -0.98) * mm, v(102.17, -0.72) * mm]});
            skFitSpline(sketch, "E1237", {"points": [v(102.17, -0.72) * mm, v(101.96, -0.66) * mm, v(101.75, -0.6) * mm, v(101.53, -0.54) * mm]});
            skFitSpline(sketch, "E1238", {"points": [v(101.53, -0.54) * mm, v(101.43, -0.52) * mm, v(101.32, -0.53) * mm, v(101.22, -0.55) * mm]});
            skFitSpline(sketch, "E1239", {"points": [v(101.22, -0.55) * mm, v(100.6, -0.7) * mm, v(99.98, -0.85) * mm, v(99.36, -1.01) * mm]});
            skFitSpline(sketch, "E1240", {"points": [v(99.36, -1.01) * mm, v(98.73, -1.18) * mm, v(98.1, -1.37) * mm, v(97.47, -1.55) * mm]});
            skFitSpline(sketch, "E1241", {"points": [v(97.47, -1.55) * mm, v(96.91, -1.7) * mm, v(96.35, -1.85) * mm, v(95.8, -2.01) * mm]});
            skFitSpline(sketch, "E1242", {"points": [v(95.8, -2.01) * mm, v(95.37, -2.13) * mm, v(94.95, -2.26) * mm, v(94.53, -2.38) * mm]});
            skFitSpline(sketch, "E1243", {"points": [v(94.53, -2.38) * mm, v(94.09, -2.5) * mm, v(93.65, -2.63) * mm, v(93.21, -2.74) * mm]});
            skFitSpline(sketch, "E1244", {"points": [v(93.21, -2.74) * mm, v(92.9, -2.82) * mm, v(92.65, -2.66) * mm, v(92.57, -2.38) * mm]});
            skFitSpline(sketch, "E1245", {"points": [v(92.57, -2.38) * mm, v(92.5, -2.14) * mm, v(92.66, -1.9) * mm, v(92.95, -1.8) * mm]});
            skFitSpline(sketch, "E1246", {"points": [v(92.95, -1.8) * mm, v(92.97, -1.8) * mm, v(92.99, -1.78) * mm, v(93.03, -1.76) * mm]});
            skFitSpline(sketch, "E1247", {"points": [v(93.03, -1.76) * mm, v(92.96, -1.71) * mm, v(92.9, -1.67) * mm, v(92.83, -1.64) * mm]});
            skFitSpline(sketch, "E1248", {"points": [v(92.83, -1.64) * mm, v(92.2, -1.3) * mm, v(91.58, -0.99) * mm, v(90.97, -0.65) * mm]});
            skFitSpline(sketch, "E1249", {"points": [v(90.97, -0.65) * mm, v(90.83, -0.58) * mm, v(90.73, -0.57) * mm, v(90.6, -0.65) * mm]});
            skFitSpline(sketch, "E1250", {"points": [v(90.6, -0.65) * mm, v(89.86, -1.06) * mm, v(89.11, -1.47) * mm, v(88.37, -1.87) * mm]});
            skFitSpline(sketch, "E1251", {"points": [v(88.37, -1.87) * mm, v(88.18, -1.97) * mm, v(88, -1.97) * mm, v(87.82, -1.85) * mm]});
            skFitSpline(sketch, "E1252", {"points": [v(87.82, -1.85) * mm, v(87.66, -1.73) * mm, v(87.6, -1.57) * mm, v(87.62, -1.37) * mm]});
            skFitSpline(sketch, "E1253", {"points": [v(87.62, -1.37) * mm, v(87.65, -1.2) * mm, v(87.75, -1.1) * mm, v(87.89, -1.02) * mm]});
            skFitSpline(sketch, "E1254", {"points": [v(87.89, -1.02) * mm, v(88.2, -0.84) * mm, v(88.51, -0.66) * mm, v(88.83, -0.49) * mm]});
            skFitSpline(sketch, "E1255", {"points": [v(88.83, -0.49) * mm, v(89.12, -0.33) * mm, v(89.4, -0.18) * mm, v(89.74, 0) * mm]});
            skFitSpline(sketch, "E1256", {"points": [v(89.74, 0) * mm, v(89.6, 0.08) * mm, v(89.5, 0.14) * mm, v(89.38, 0.2) * mm]});
            skFitSpline(sketch, "E1257", {"points": [v(89.38, 0.2) * mm, v(88.93, 0.45) * mm, v(88.48, 0.69) * mm, v(88.04, 0.93) * mm]});
            skFitSpline(sketch, "E1258", {"points": [v(88.04, 0.93) * mm, v(87.97, 0.97) * mm, v(87.9, 1) * mm, v(87.85, 1.04) * mm]});
            skFitSpline(sketch, "E1259", {"points": [v(87.85, 1.04) * mm, v(87.62, 1.2) * mm, v(87.55, 1.47) * mm, v(87.68, 1.7) * mm]});
            skFitSpline(sketch, "E1260", {"points": [v(87.68, 1.7) * mm, v(87.8, 1.92) * mm, v(88.1, 2) * mm, v(88.34, 1.88) * mm]});
            skFitSpline(sketch, "E1261", {"points": [v(88.34, 1.88) * mm, v(88.44, 1.84) * mm, v(88.52, 1.78) * mm, v(88.62, 1.73) * mm]});
            skFitSpline(sketch, "E1262", {"points": [v(88.62, 1.73) * mm, v(89.3, 1.36) * mm, v(89.98, 1) * mm, v(90.66, 0.62) * mm]});
            skFitSpline(sketch, "E1263", {"points": [v(90.66, 0.62) * mm, v(90.77, 0.56) * mm, v(90.85, 0.6) * mm, v(90.94, 0.64) * mm]});
            skFitSpline(sketch, "E1264", {"points": [v(90.94, 0.64) * mm, v(91.23, 0.8) * mm, v(91.5, 0.95) * mm, v(91.79, 1.1) * mm]});
            skFitSpline(sketch, "E1265", {"points": [v(91.79, 1.1) * mm, v(92.12, 1.28) * mm, v(92.45, 1.45) * mm, v(92.79, 1.62) * mm]});
            skFitSpline(sketch, "E1266", {"points": [v(92.79, 1.62) * mm, v(92.86, 1.66) * mm, v(92.94, 1.7) * mm, v(93.05, 1.75) * mm]});
            skFitSpline(sketch, "E1267", {"points": [v(93.05, 1.75) * mm, v(92.96, 1.79) * mm, v(92.9, 1.8) * mm, v(92.84, 1.84) * mm]});
            skFitSpline(sketch, "E1268", {"points": [v(92.84, 1.84) * mm, v(92.64, 1.93) * mm, v(92.53, 2.16) * mm, v(92.57, 2.35) * mm]});
            skFitSpline(sketch, "E1269", {"points": [v(92.57, 2.35) * mm, v(92.62, 2.58) * mm, v(92.8, 2.74) * mm, v(93.02, 2.75) * mm]});
            skFitSpline(sketch, "E1270", {"points": [v(93.02, 2.75) * mm, v(93.11, 2.76) * mm, v(93.2, 2.74) * mm, v(93.3, 2.72) * mm]});
            skFitSpline(sketch, "E1271", {"points": [v(93.3, 2.72) * mm, v(93.88, 2.56) * mm, v(94.45, 2.4) * mm, v(95.03, 2.23) * mm]});
            skFitSpline(sketch, "E1272", {"points": [v(95.03, 2.23) * mm, v(96.15, 1.92) * mm, v(97.27, 1.6) * mm, v(98.4, 1.29) * mm]});
            skFitSpline(sketch, "E1273", {"points": [v(98.4, 1.29) * mm, v(99.34, 1.03) * mm, v(100.3, 0.79) * mm, v(101.25, 0.54) * mm]});
            skFitSpline(sketch, "E1274", {"points": [v(101.25, 0.54) * mm, v(101.35, 0.52) * mm, v(101.47, 0.53) * mm, v(101.57, 0.56) * mm]});
            skFitSpline(sketch, "E1275", {"points": [v(101.57, 0.56) * mm, v(102.14, 0.7) * mm, v(102.7, 0.86) * mm, v(103.26, 1.01) * mm]});
            skFitSpline(sketch, "E1276", {"points": [v(103.26, 1.01) * mm, v(103.77, 1.16) * mm, v(104.28, 1.31) * mm, v(104.8, 1.47) * mm]});
            skFitSpline(sketch, "E1277", {"points": [v(104.8, 1.47) * mm, v(104.86, 1.48) * mm, v(104.93, 1.51) * mm, v(105.02, 1.54) * mm]});
            skFitSpline(sketch, "E1278", {"points": [v(105.02, 1.54) * mm, v(104.82, 1.68) * mm, v(104.65, 1.8) * mm, v(104.48, 1.9) * mm]});
            skFitSpline(sketch, "E1279", {"points": [v(104.48, 1.9) * mm, v(104.43, 1.93) * mm, v(104.35, 1.93) * mm, v(104.3, 1.92) * mm]});
            skFitSpline(sketch, "E1280", {"points": [v(104.3, 1.92) * mm, v(103.5, 1.74) * mm, v(102.72, 1.55) * mm, v(101.94, 1.37) * mm]});
            skFitSpline(sketch, "E1281", {"points": [v(101.94, 1.37) * mm, v(101.78, 1.33) * mm, v(101.63, 1.29) * mm, v(101.47, 1.26) * mm]});
            skFitSpline(sketch, "E1282", {"points": [v(101.47, 1.26) * mm, v(101.37, 1.25) * mm, v(101.26, 1.25) * mm, v(101.17, 1.28) * mm]});
            skFitSpline(sketch, "E1283", {"points": [v(101.17, 1.28) * mm, v(100.97, 1.33) * mm, v(100.83, 1.54) * mm, v(100.83, 1.73) * mm]});
            skFitSpline(sketch, "E1284", {"points": [v(100.83, 1.73) * mm, v(100.83, 1.93) * mm, v(101, 2.14) * mm, v(101.21, 2.2) * mm]});
            skFitSpline(sketch, "E1285", {"points": [v(101.21, 2.2) * mm, v(101.43, 2.26) * mm, v(101.65, 2.3) * mm, v(101.86, 2.36) * mm]});
            skFitSpline(sketch, "E1286", {"points": [v(101.86, 2.36) * mm, v(102.34, 2.47) * mm, v(102.82, 2.59) * mm, v(103.34, 2.71) * mm]});
            skFitSpline(sketch, "E1287", {"points": [v(103.34, 2.71) * mm, v(103.1, 2.88) * mm, v(102.89, 3.03) * mm, v(102.67, 3.18) * mm]});
            skFitSpline(sketch, "E1288", {"points": [v(102.67, 3.18) * mm, v(102.63, 3.2) * mm, v(102.57, 3.21) * mm, v(102.53, 3.2) * mm]});
            skFitSpline(sketch, "E1289", {"points": [v(102.53, 3.2) * mm, v(101.92, 3.05) * mm, v(101.28, 3.04) * mm, v(100.66, 2.95) * mm]});
            skFitSpline(sketch, "E1290", {"points": [v(100.66, 2.95) * mm, v(100.4, 2.9) * mm, v(100.14, 2.85) * mm, v(99.88, 2.8) * mm]});
            skFitSpline(sketch, "E1291", {"points": [v(99.88, 2.8) * mm, v(99.58, 2.76) * mm, v(99.28, 2.71) * mm, v(98.99, 2.67) * mm]});
            skFitSpline(sketch, "E1292", {"points": [v(98.99, 2.67) * mm, v(98.92, 2.66) * mm, v(98.86, 2.66) * mm, v(98.8, 2.66) * mm]});
            skFitSpline(sketch, "E1293", {"points": [v(98.8, 2.66) * mm, v(98.53, 2.68) * mm, v(98.34, 2.88) * mm, v(98.33, 3.13) * mm]});
            skFitSpline(sketch, "E1294", {"points": [v(98.33, 3.13) * mm, v(98.32, 3.36) * mm, v(98.5, 3.58) * mm, v(98.74, 3.62) * mm]});
            skFitSpline(sketch, "E1295", {"points": [v(98.74, 3.62) * mm, v(99.6, 3.75) * mm, v(100.48, 3.87) * mm, v(101.34, 4) * mm]});
            skFitSpline(sketch, "E1296", {"points": [v(101.34, 4) * mm, v(101.39, 4) * mm, v(101.43, 4.02) * mm, v(101.51, 4.03) * mm]});
            skFitSpline(sketch, "E1297", {"points": [v(101.51, 4.03) * mm, v(101.2, 4.33) * mm, v(100.9, 4.57) * mm, v(100.45, 4.52) * mm]});
            skFitSpline(sketch, "E1298", {"points": [v(100.45, 4.52) * mm, v(99.98, 4.47) * mm, v(99.5, 4.48) * mm, v(99.04, 4.43) * mm]});
            skFitSpline(sketch, "E1299", {"points": [v(99.04, 4.43) * mm, v(98.6, 4.4) * mm, v(98.16, 4.32) * mm, v(97.71, 4.26) * mm]});
            skFitSpline(sketch, "E1300", {"points": [v(97.71, 4.26) * mm, v(97.52, 4.24) * mm, v(97.33, 4.22) * mm, v(97.14, 4.2) * mm]});
            skFitSpline(sketch, "E1301", {"points": [v(97.14, 4.2) * mm, v(97.1, 4.2) * mm, v(97.05, 4.2) * mm, v(97, 4.18) * mm]});
            skFitSpline(sketch, "E1302", {"points": [v(97, 4.18) * mm, v(96.62, 4.12) * mm, v(96.23, 4.05) * mm, v(95.85, 3.98) * mm]});
            skFitSpline(sketch, "E1303", {"points": [v(95.85, 3.98) * mm, v(95.6, 3.93) * mm, v(95.33, 4.05) * mm, v(95.27, 4.28) * mm]});
            skFitSpline(sketch, "E1304", {"points": [v(95.27, 4.28) * mm, v(95.2, 4.51) * mm, v(95.23, 4.8) * mm, v(95.55, 4.9) * mm]});
            skFitSpline(sketch, "E1305", {"points": [v(95.55, 4.9) * mm, v(95.79, 4.98) * mm, v(96.05, 5) * mm, v(96.3, 5.04) * mm]});
            skFitSpline(sketch, "E1306", {"points": [v(96.3, 5.04) * mm, v(96.92, 5.13) * mm, v(97.54, 5.22) * mm, v(98.17, 5.3) * mm]});
            skFitSpline(sketch, "E1307", {"points": [v(98.17, 5.3) * mm, v(98.34, 5.33) * mm, v(98.5, 5.35) * mm, v(98.68, 5.41) * mm]});
            skFitSpline(sketch, "E1308", {"points": [v(98.68, 5.41) * mm, v(98.5, 5.43) * mm, v(98.32, 5.44) * mm, v(98.13, 5.47) * mm]});
            skFitSpline(sketch, "E1309", {"points": [v(98.13, 5.47) * mm, v(97.68, 5.52) * mm, v(97.23, 5.58) * mm, v(96.78, 5.63) * mm]});
            skFitSpline(sketch, "E1310", {"points": [v(96.78, 5.63) * mm, v(96.58, 5.65) * mm, v(96.38, 5.66) * mm, v(96.18, 5.66) * mm]});
            skFitSpline(sketch, "E1311", {"points": [v(96.18, 5.66) * mm, v(95.76, 5.67) * mm, v(95.56, 5.8) * mm, v(95.43, 6.19) * mm]});
            skFitSpline(sketch, "E1312", {"points": [v(95.43, 6.19) * mm, v(95.3, 6.58) * mm, v(95.17, 6.98) * mm, v(95.06, 7.38) * mm]});
            skFitSpline(sketch, "E1313", {"points": [v(95.06, 7.38) * mm, v(94.93, 7.84) * mm, v(94.81, 8.3) * mm, v(94.69, 8.8) * mm]});
            skFitSpline(sketch, "E1314", {"points": [v(94.69, 8.8) * mm, v(94.5, 8.77) * mm, v(94.29, 8.75) * mm, v(94.09, 8.73) * mm]});
            skFitSpline(sketch, "E1315", {"points": [v(94.09, 8.73) * mm, v(93.55, 8.65) * mm, v(93.01, 8.57) * mm, v(92.48, 8.49) * mm]});
            skFitSpline(sketch, "E1316", {"points": [v(92.48, 8.49) * mm, v(92.4, 8.48) * mm, v(92.32, 8.46) * mm, v(92.24, 8.47) * mm]});
            skFitSpline(sketch, "E1317", {"points": [v(92.24, 8.47) * mm, v(92.01, 8.5) * mm, v(91.84, 8.67) * mm, v(91.8, 8.89) * mm]});
            skFitSpline(sketch, "E1318", {"points": [v(91.8, 8.89) * mm, v(91.78, 9.12) * mm, v(91.91, 9.35) * mm, v(92.14, 9.4) * mm]});
            skFitSpline(sketch, "E1319", {"points": [v(92.14, 9.4) * mm, v(92.4, 9.47) * mm, v(92.68, 9.5) * mm, v(92.95, 9.55) * mm]});
            skFitSpline(sketch, "E1320", {"points": [v(92.95, 9.55) * mm, v(93.43, 9.62) * mm, v(93.9, 9.68) * mm, v(94.4, 9.75) * mm]});
            skFitSpline(sketch, "E1321", {"points": [v(94.4, 9.75) * mm, v(94.44, 9.75) * mm, v(94.48, 9.77) * mm, v(94.55, 9.8) * mm]});
            skFitSpline(sketch, "E1322", {"points": [v(94.55, 9.8) * mm, v(94.5, 10.1) * mm, v(94.43, 10.4) * mm, v(94.38, 10.71) * mm]});
            skFitSpline(sketch, "E1323", {"points": [v(94.38, 10.71) * mm, v(94.3, 11.16) * mm, v(94.23, 11.6) * mm, v(94.16, 12.06) * mm]});
            skFitSpline(sketch, "E1324", {"points": [v(94.16, 12.06) * mm, v(94.15, 12.14) * mm, v(94.15, 12.24) * mm, v(94.17, 12.32) * mm]});
            skFitSpline(sketch, "E1325", {"points": [v(94.17, 12.32) * mm, v(94.23, 12.52) * mm, v(94.43, 12.67) * mm, v(94.64, 12.67) * mm]});
            skFitSpline(sketch, "E1326", {"points": [v(94.64, 12.67) * mm, v(94.87, 12.66) * mm, v(95.07, 12.5) * mm, v(95.11, 12.26) * mm]});
            skFitSpline(sketch, "E1327", {"points": [v(95.11, 12.26) * mm, v(95.18, 11.88) * mm, v(95.23, 11.49) * mm, v(95.3, 11.1) * mm]});
            skFitSpline(sketch, "E1328", {"points": [v(95.3, 11.1) * mm, v(95.36, 10.72) * mm, v(95.44, 10.34) * mm, v(95.52, 9.94) * mm]});
            skFitSpline(sketch, "E1329", {"points": [v(95.52, 9.94) * mm, v(95.77, 9.95) * mm, v(96.03, 9.97) * mm, v(96.28, 9.98) * mm]});
            skFitSpline(sketch, "E1330", {"points": [v(96.28, 9.98) * mm, v(96.92, 10) * mm, v(97.55, 10.04) * mm, v(98.2, 10.05) * mm]});
            skFitSpline(sketch, "E1331", {"points": [v(98.2, 10.05) * mm, v(98.64, 10.05) * mm, v(98.83, 9.89) * mm, v(98.98, 9.46) * mm]});
            skFitSpline(sketch, "E1332", {"points": [v(98.98, 9.46) * mm, v(99.08, 9.18) * mm, v(99.21, 8.92) * mm, v(99.33, 8.65) * mm]});
            skFitSpline(sketch, "E1333", {"points": [v(99.33, 8.65) * mm, v(99.5, 8.25) * mm, v(99.68, 7.86) * mm, v(99.86, 7.47) * mm]});
            skFitSpline(sketch, "E1334", {"points": [v(99.86, 7.47) * mm, v(99.9, 7.38) * mm, v(99.93, 7.3) * mm, v(100, 7.22) * mm]});
            skFitSpline(sketch, "E1335", {"points": [v(100, 7.22) * mm, v(99.95, 7.52) * mm, v(99.9, 7.82) * mm, v(99.84, 8.12) * mm]});
            skFitSpline(sketch, "E1336", {"points": [v(99.84, 8.12) * mm, v(99.78, 8.44) * mm, v(99.71, 8.75) * mm, v(99.65, 9.08) * mm]});
            skFitSpline(sketch, "E1337", {"points": [v(99.65, 9.08) * mm, v(99.6, 9.42) * mm, v(99.54, 9.77) * mm, v(99.49, 10.11) * mm]});
            skFitSpline(sketch, "E1338", {"points": [v(99.49, 10.11) * mm, v(99.48, 10.2) * mm, v(99.48, 10.27) * mm, v(99.49, 10.35) * mm]});
            skFitSpline(sketch, "E1339", {"points": [v(99.49, 10.35) * mm, v(99.51, 10.59) * mm, v(99.7, 10.77) * mm, v(99.92, 10.8) * mm]});
            skFitSpline(sketch, "E1340", {"points": [v(99.92, 10.8) * mm, v(100.16, 10.82) * mm, v(100.4, 10.67) * mm, v(100.44, 10.43) * mm]});
            skFitSpline(sketch, "E1341", {"points": [v(100.44, 10.43) * mm, v(100.5, 10.11) * mm, v(100.54, 9.8) * mm, v(100.58, 9.48) * mm]});
            skFitSpline(sketch, "E1342", {"points": [v(100.58, 9.48) * mm, v(100.6, 9.33) * mm, v(100.62, 9.18) * mm, v(100.65, 9.03) * mm]});
            skFitSpline(sketch, "E1343", {"points": [v(100.65, 9.03) * mm, v(100.72, 8.66) * mm, v(100.79, 8.3) * mm, v(100.87, 7.93) * mm]});
            skFitSpline(sketch, "E1344", {"points": [v(100.87, 7.93) * mm, v(100.97, 7.42) * mm, v(101.09, 6.92) * mm, v(101.2, 6.41) * mm]});
            skFitSpline(sketch, "E1345", {"points": [v(101.2, 6.41) * mm, v(101.26, 6.19) * mm, v(101.33, 5.97) * mm, v(101.39, 5.74) * mm]});
            skFitSpline(sketch, "E1346", {"points": [v(101.39, 5.74) * mm, v(101.45, 5.46) * mm, v(101.6, 5.25) * mm, v(101.86, 5.11) * mm]});
            skFitSpline(sketch, "E1347", {"points": [v(101.86, 5.11) * mm, v(101.95, 5.06) * mm, v(102.04, 5) * mm, v(102.16, 4.92) * mm]});
            skFitSpline(sketch, "E1348", {"points": [v(102.16, 4.92) * mm, v(102.1, 5.23) * mm, v(102.04, 5.5) * mm, v(102, 5.78) * mm]});
            skFitSpline(sketch, "E1349", {"points": [v(102, 5.78) * mm, v(101.94, 6.16) * mm, v(101.89, 6.53) * mm, v(101.83, 6.91) * mm]});
            skFitSpline(sketch, "E1350", {"points": [v(101.83, 6.91) * mm, v(101.8, 7.15) * mm, v(101.76, 7.38) * mm, v(101.71, 7.62) * mm]});
            skFitSpline(sketch, "E1351", {"points": [v(101.71, 7.62) * mm, v(101.65, 7.92) * mm, v(101.8, 8.16) * mm, v(102.06, 8.23) * mm]});
            skFitSpline(sketch, "E1352", {"points": [v(102.06, 8.23) * mm, v(102.32, 8.3) * mm, v(102.59, 8.15) * mm, v(102.66, 7.85) * mm]});
            skFitSpline(sketch, "E1353", {"points": [v(102.66, 7.85) * mm, v(102.73, 7.52) * mm, v(102.78, 7.2) * mm, v(102.82, 6.86) * mm]});
            skFitSpline(sketch, "E1354", {"points": [v(102.82, 6.86) * mm, v(102.88, 6.27) * mm, v(103, 5.7) * mm, v(103.12, 5.12) * mm]});
            skFitSpline(sketch, "E1355", {"points": [v(103.12, 5.12) * mm, v(103.18, 4.84) * mm, v(103.21, 4.55) * mm, v(103.26, 4.27) * mm]});
            skFitSpline(sketch, "E1356", {"points": [v(103.26, 4.27) * mm, v(103.27, 4.2) * mm, v(103.28, 4.13) * mm, v(103.32, 4.1) * mm]});
            skFitSpline(sketch, "E1357", {"points": [v(103.32, 4.1) * mm, v(103.53, 3.93) * mm, v(103.74, 3.77) * mm, v(104, 3.59) * mm]});
            skFitSpline(sketch, "E1358", {"points": [v(104, 3.59) * mm, v(103.97, 3.85) * mm, v(103.94, 4.06) * mm, v(103.93, 4.27) * mm]});
            skFitSpline(sketch, "E1359", {"points": [v(103.93, 4.27) * mm, v(103.9, 4.61) * mm, v(103.87, 4.95) * mm, v(103.85, 5.3) * mm]});
            skFitSpline(sketch, "E1360", {"points": [v(103.85, 5.3) * mm, v(103.84, 5.42) * mm, v(103.83, 5.55) * mm, v(103.8, 5.68) * mm]});
            skFitSpline(sketch, "E1361", {"points": [v(103.8, 5.68) * mm, v(103.77, 5.99) * mm, v(103.95, 6.26) * mm, v(104.23, 6.3) * mm]});
            skFitSpline(sketch, "E1362", {"points": [v(104.23, 6.3) * mm, v(104.51, 6.34) * mm, v(104.76, 6.12) * mm, v(104.79, 5.8) * mm]});
            skFitSpline(sketch, "E1363", {"points": [v(104.79, 5.8) * mm, v(104.82, 5.42) * mm, v(104.82, 5.05) * mm, v(104.86, 4.67) * mm]});
            skFitSpline(sketch, "E1364", {"points": [v(104.86, 4.67) * mm, v(104.9, 4.15) * mm, v(104.96, 3.63) * mm, v(105, 3.1) * mm]});
            skFitSpline(sketch, "E1365", {"points": [v(105, 3.1) * mm, v(105.02, 3.01) * mm, v(105.03, 2.92) * mm, v(105.04, 2.81) * mm]});
            skFitSpline(sketch, "E1366", {"points": [v(105.04, 2.81) * mm, v(105.22, 2.67) * mm, v(105.4, 2.53) * mm, v(105.6, 2.36) * mm]});
            skFitSpline(sketch, "E1367", {"points": [v(105.6, 2.36) * mm, v(105.6, 2.44) * mm, v(105.62, 2.5) * mm, v(105.62, 2.56) * mm]});
            skFitSpline(sketch, "E1368", {"points": [v(105.62, 2.56) * mm, v(105.6, 3.24) * mm, v(105.6, 3.93) * mm, v(105.57, 4.61) * mm]});
            skFitSpline(sketch, "E1369", {"points": [v(105.57, 4.61) * mm, v(105.55, 5.1) * mm, v(105.51, 5.59) * mm, v(105.47, 6.07) * mm]});
            skFitSpline(sketch, "E1370", {"points": [v(105.47, 6.07) * mm, v(105.47, 6.14) * mm, v(105.43, 6.2) * mm, v(105.4, 6.26) * mm]});
            skFitSpline(sketch, "E1371", {"points": [v(105.4, 6.26) * mm, v(104.33, 7.9) * mm, v(103.27, 9.53) * mm, v(102.2, 11.16) * mm]});
            skFitSpline(sketch, "E1372", {"points": [v(102.2, 11.16) * mm, v(101.76, 11.84) * mm, v(101.3, 12.5) * mm, v(100.85, 13.17) * mm]});
            skFitSpline(sketch, "E1373", {"points": [v(100.85, 13.17) * mm, v(100.74, 13.34) * mm, v(100.69, 13.52) * mm, v(100.78, 13.71) * mm]});
            skFitSpline(sketch, "E1374", {"points": [v(100.78, 13.71) * mm, v(100.92, 14.02) * mm, v(101.31, 14.1) * mm, v(101.56, 13.86) * mm]});
            skFitSpline(sketch, "E1375", {"points": [v(101.56, 13.86) * mm, v(101.6, 13.82) * mm, v(101.64, 13.77) * mm, v(101.7, 13.7) * mm]});
            skFitSpline(sketch, "E1376", {"points": [v(101.7, 13.7) * mm, v(101.79, 13.91) * mm, v(101.78, 14.13) * mm, v(101.82, 14.33) * mm]});
            skFitSpline(sketch, "E1377", {"points": [v(101.82, 14.33) * mm, v(101.92, 14.87) * mm, v(102, 15.41) * mm, v(102.1, 15.95) * mm]});
            skFitSpline(sketch, "E1378", {"points": [v(102.1, 15.95) * mm, v(102.14, 16.12) * mm, v(102.13, 16.24) * mm, v(101.99, 16.37) * mm]});
            skFitSpline(sketch, "E1379", {"points": [v(101.99, 16.37) * mm, v(101.37, 16.93) * mm, v(100.78, 17.52) * mm, v(100.17, 18.08) * mm]});
            skFitSpline(sketch, "E1380", {"points": [v(100.17, 18.08) * mm, v(99.93, 18.3) * mm, v(99.91, 18.78) * mm, v(100.29, 18.93) * mm]});
            skFitSpline(sketch, "E1381", {"points": [v(100.29, 18.93) * mm, v(100.48, 19) * mm, v(100.65, 18.96) * mm, v(100.8, 18.83) * mm]});
            skFitSpline(sketch, "E1382", {"points": [v(100.8, 18.83) * mm, v(101.07, 18.58) * mm, v(101.34, 18.33) * mm, v(101.61, 18.08) * mm]});
            skFitSpline(sketch, "E1383", {"points": [v(101.61, 18.08) * mm, v(101.85, 17.86) * mm, v(102.08, 17.63) * mm, v(102.36, 17.36) * mm]});
            skFitSpline(sketch, "E1384", {"points": [v(68.38, -10.22) * mm, v(68.28, -10.43) * mm, v(68.2, -10.58) * mm, v(68.14, -10.72) * mm]});
            skFitSpline(sketch, "E1385", {"points": [v(68.14, -10.72) * mm, v(67.9, -11.21) * mm, v(67.67, -11.7) * mm, v(67.44, -12.19) * mm]});
            skFitSpline(sketch, "E1386", {"points": [v(67.44, -12.19) * mm, v(67.4, -12.25) * mm, v(67.38, -12.3) * mm, v(67.33, -12.35) * mm]});
            skFitSpline(sketch, "E1387", {"points": [v(67.33, -12.35) * mm, v(67.16, -12.56) * mm, v(66.81, -12.61) * mm, v(66.58, -12.46) * mm]});
            skFitSpline(sketch, "E1388", {"points": [v(66.58, -12.46) * mm, v(66.34, -12.3) * mm, v(66.26, -12) * mm, v(66.4, -11.73) * mm]});
            skFitSpline(sketch, "E1389", {"points": [v(66.4, -11.73) * mm, v(66.67, -11.17) * mm, v(66.94, -10.61) * mm, v(67.22, -10.05) * mm]});
            skFitSpline(sketch, "E1390", {"points": [v(67.22, -10.05) * mm, v(67.35, -9.79) * mm, v(67.47, -9.52) * mm, v(67.61, -9.27) * mm]});
            skFitSpline(sketch, "E1391", {"points": [v(67.61, -9.27) * mm, v(67.7, -9.1) * mm, v(67.81, -8.97) * mm, v(67.96, -8.75) * mm]});
            skFitSpline(sketch, "E1392", {"points": [v(67.96, -8.75) * mm, v(67.8, -8.16) * mm, v(67.6, -7.5) * mm, v(67.4, -6.79) * mm]});
            skFitSpline(sketch, "E1393", {"points": [v(67.4, -6.79) * mm, v(67.34, -6.88) * mm, v(67.3, -6.94) * mm, v(67.27, -7) * mm]});
            skFitSpline(sketch, "E1394", {"points": [v(67.27, -7) * mm, v(67, -7.56) * mm, v(66.73, -8.12) * mm, v(66.46, -8.68) * mm]});
            skFitSpline(sketch, "E1395", {"points": [v(66.46, -8.68) * mm, v(66.42, -8.76) * mm, v(66.39, -8.83) * mm, v(66.34, -8.9) * mm]});
            skFitSpline(sketch, "E1396", {"points": [v(66.34, -8.9) * mm, v(66.15, -9.13) * mm, v(65.84, -9.19) * mm, v(65.6, -9.04) * mm]});
            skFitSpline(sketch, "E1397", {"points": [v(65.6, -9.04) * mm, v(65.36, -8.9) * mm, v(65.26, -8.61) * mm, v(65.38, -8.34) * mm]});
            skFitSpline(sketch, "E1398", {"points": [v(65.38, -8.34) * mm, v(65.57, -7.92) * mm, v(65.77, -7.5) * mm, v(65.97, -7.07) * mm]});
            skFitSpline(sketch, "E1399", {"points": [v(65.97, -7.07) * mm, v(66.24, -6.5) * mm, v(66.51, -5.9) * mm, v(66.8, -5.33) * mm]});
            skFitSpline(sketch, "E1400", {"points": [v(66.8, -5.33) * mm, v(66.86, -5.18) * mm, v(66.86, -5.05) * mm, v(66.8, -4.9) * mm]});
            skFitSpline(sketch, "E1401", {"points": [v(66.8, -4.9) * mm, v(66.75, -4.76) * mm, v(66.7, -4.62) * mm, v(66.65, -4.47) * mm]});
            skFitSpline(sketch, "E1402", {"points": [v(66.65, -4.47) * mm, v(66.45, -3.84) * mm, v(66.25, -3.21) * mm, v(66.05, -2.58) * mm]});
            skFitSpline(sketch, "E1403", {"points": [v(66.05, -2.58) * mm, v(65.98, -2.38) * mm, v(65.9, -2.18) * mm, v(65.8, -1.94) * mm]});
            skFitSpline(sketch, "E1404", {"points": [v(65.8, -1.94) * mm, v(65.77, -2.03) * mm, v(65.75, -2.08) * mm, v(65.73, -2.13) * mm]});
            skFitSpline(sketch, "E1405", {"points": [v(65.73, -2.13) * mm, v(65.42, -3.21) * mm, v(65.1, -4.3) * mm, v(64.79, -5.38) * mm]});
            skFitSpline(sketch, "E1406", {"points": [v(64.79, -5.38) * mm, v(64.6, -6.03) * mm, v(64.46, -6.7) * mm, v(64.23, -7.33) * mm]});
            skFitSpline(sketch, "E1407", {"points": [v(64.23, -7.33) * mm, v(63.94, -8.14) * mm, v(63.72, -8.98) * mm, v(63.43, -9.79) * mm]});
            skFitSpline(sketch, "E1408", {"points": [v(63.43, -9.79) * mm, v(63.31, -10.1) * mm, v(63.35, -10.32) * mm, v(63.52, -10.57) * mm]});
            skFitSpline(sketch, "E1409", {"points": [v(63.52, -10.57) * mm, v(63.94, -11.18) * mm, v(64.27, -11.84) * mm, v(64.53, -12.53) * mm]});
            skFitSpline(sketch, "E1410", {"points": [v(64.53, -12.53) * mm, v(64.62, -12.77) * mm, v(64.77, -12.98) * mm, v(64.88, -13.21) * mm]});
            skFitSpline(sketch, "E1411", {"points": [v(64.88, -13.21) * mm, v(65.04, -13.57) * mm, v(64.85, -13.94) * mm, v(64.47, -14.01) * mm]});
            skFitSpline(sketch, "E1412", {"points": [v(64.47, -14.01) * mm, v(64.24, -14.06) * mm, v(63.97, -13.93) * mm, v(63.85, -13.7) * mm]});
            skFitSpline(sketch, "E1413", {"points": [v(63.85, -13.7) * mm, v(63.69, -13.35) * mm, v(63.54, -13) * mm, v(63.37, -12.65) * mm]});
            skFitSpline(sketch, "E1414", {"points": [v(63.37, -12.65) * mm, v(63.2, -12.3) * mm, v(63.03, -11.94) * mm, v(62.86, -11.6) * mm]});
            skFitSpline(sketch, "E1415", {"points": [v(62.86, -11.6) * mm, v(62.84, -11.6) * mm, v(62.82, -11.6) * mm, v(62.8, -11.6) * mm]});
            skFitSpline(sketch, "E1416", {"points": [v(62.8, -11.6) * mm, v(62.8, -11.76) * mm, v(62.79, -11.92) * mm, v(62.79, -12.08) * mm]});
            skFitSpline(sketch, "E1417", {"points": [v(62.79, -12.08) * mm, v(62.8, -12.73) * mm, v(62.84, -13.38) * mm, v(62.83, -14.03) * mm]});
            skFitSpline(sketch, "E1418", {"points": [v(62.83, -14.03) * mm, v(62.83, -14.38) * mm, v(62.86, -14.72) * mm, v(62.86, -15.07) * mm]});
            skFitSpline(sketch, "E1419", {"points": [v(62.86, -15.07) * mm, v(62.86, -15.26) * mm, v(62.8, -15.4) * mm, v(62.67, -15.54) * mm]});
            skFitSpline(sketch, "E1420", {"points": [v(62.67, -15.54) * mm, v(62.27, -15.93) * mm, v(61.87, -16.32) * mm, v(61.48, -16.72) * mm]});
            skFitSpline(sketch, "E1421", {"points": [v(61.48, -16.72) * mm, v(61.27, -16.95) * mm, v(61.06, -17.19) * mm, v(60.87, -17.43) * mm]});
            skFitSpline(sketch, "E1422", {"points": [v(60.87, -17.43) * mm, v(60.59, -17.79) * mm, v(60.3, -17.86) * mm, v(59.9, -17.65) * mm]});
            skFitSpline(sketch, "E1423", {"points": [v(59.9, -17.65) * mm, v(59.71, -17.55) * mm, v(59.6, -17.4) * mm, v(59.6, -17.17) * mm]});
            skFitSpline(sketch, "E1424", {"points": [v(59.6, -17.17) * mm, v(59.6, -16.62) * mm, v(59.5, -16.08) * mm, v(59.4, -15.54) * mm]});
            skFitSpline(sketch, "E1425", {"points": [v(59.4, -15.54) * mm, v(59.33, -15.16) * mm, v(59.28, -14.78) * mm, v(59.22, -14.4) * mm]});
            skFitSpline(sketch, "E1426", {"points": [v(59.22, -14.4) * mm, v(59.18, -14.16) * mm, v(59.28, -13.97) * mm, v(59.42, -13.8) * mm]});
            skFitSpline(sketch, "E1427", {"points": [v(59.42, -13.8) * mm, v(60.07, -12.95) * mm, v(60.72, -12.1) * mm, v(61.36, -11.26) * mm]});
            skFitSpline(sketch, "E1428", {"points": [v(61.36, -11.26) * mm, v(61.38, -11.23) * mm, v(61.4, -11.2) * mm, v(61.43, -11.13) * mm]});
            skFitSpline(sketch, "E1429", {"points": [v(61.43, -11.13) * mm, v(61.35, -11.16) * mm, v(61.29, -11.17) * mm, v(61.24, -11.2) * mm]});
            skFitSpline(sketch, "E1430", {"points": [v(61.24, -11.2) * mm, v(60.86, -11.4) * mm, v(60.49, -11.62) * mm, v(60.1, -11.83) * mm]});
            skFitSpline(sketch, "E1431", {"points": [v(60.1, -11.83) * mm, v(59.85, -11.97) * mm, v(59.6, -12.11) * mm, v(59.33, -12.24) * mm]});
            skFitSpline(sketch, "E1432", {"points": [v(59.33, -12.24) * mm, v(59.05, -12.38) * mm, v(58.71, -12.26) * mm, v(58.57, -12) * mm]});
            skFitSpline(sketch, "E1433", {"points": [v(58.57, -12) * mm, v(58.42, -11.73) * mm, v(58.5, -11.39) * mm, v(58.8, -11.24) * mm]});
            skFitSpline(sketch, "E1434", {"points": [v(58.8, -11.24) * mm, v(59.71, -10.8) * mm, v(60.55, -10.19) * mm, v(61.52, -9.87) * mm]});
            skFitSpline(sketch, "E1435", {"points": [v(61.52, -9.87) * mm, v(61.76, -9.79) * mm, v(61.9, -9.65) * mm, v(61.97, -9.38) * mm]});
            skFitSpline(sketch, "E1436", {"points": [v(61.97, -9.38) * mm, v(62.1, -8.9) * mm, v(62.3, -8.42) * mm, v(62.46, -7.95) * mm]});
            skFitSpline(sketch, "E1437", {"points": [v(62.46, -7.95) * mm, v(62.67, -7.3) * mm, v(62.85, -6.62) * mm, v(63.08, -5.98) * mm]});
            skFitSpline(sketch, "E1438", {"points": [v(63.08, -5.98) * mm, v(63.57, -4.59) * mm, v(64.1, -3.2) * mm, v(64.6, -1.82) * mm]});
            skFitSpline(sketch, "E1439", {"points": [v(64.6, -1.82) * mm, v(64.63, -1.75) * mm, v(64.65, -1.69) * mm, v(64.63, -1.59) * mm]});
            skFitSpline(sketch, "E1440", {"points": [v(64.63, -1.59) * mm, v(64.2, -1.9) * mm, v(63.76, -2.2) * mm, v(63.33, -2.5) * mm]});
            skFitSpline(sketch, "E1441", {"points": [v(63.33, -2.5) * mm, v(62.96, -2.78) * mm, v(62.58, -3.07) * mm, v(62.2, -3.33) * mm]});
            skFitSpline(sketch, "E1442", {"points": [v(62.2, -3.33) * mm, v(62.03, -3.45) * mm, v(61.9, -3.59) * mm, v(61.87, -3.8) * mm]});
            skFitSpline(sketch, "E1443", {"points": [v(61.87, -3.8) * mm, v(61.75, -4.5) * mm, v(61.62, -5.2) * mm, v(61.48, -5.89) * mm]});
            skFitSpline(sketch, "E1444", {"points": [v(61.48, -5.89) * mm, v(61.41, -6.25) * mm, v(61.34, -6.6) * mm, v(61.26, -6.96) * mm]});
            skFitSpline(sketch, "E1445", {"points": [v(61.26, -6.96) * mm, v(61.19, -7.31) * mm, v(60.93, -7.5) * mm, v(60.6, -7.43) * mm]});
            skFitSpline(sketch, "E1446", {"points": [v(60.6, -7.43) * mm, v(60.3, -7.37) * mm, v(60.11, -7.07) * mm, v(60.17, -6.74) * mm]});
            skFitSpline(sketch, "E1447", {"points": [v(60.17, -6.74) * mm, v(60.22, -6.45) * mm, v(60.3, -6.16) * mm, v(60.35, -5.88) * mm]});
            skFitSpline(sketch, "E1448", {"points": [v(60.35, -5.88) * mm, v(60.42, -5.49) * mm, v(60.48, -5.1) * mm, v(60.54, -4.71) * mm]});
            skFitSpline(sketch, "E1449", {"points": [v(60.54, -4.71) * mm, v(60.54, -4.68) * mm, v(60.53, -4.64) * mm, v(60.53, -4.57) * mm]});
            skFitSpline(sketch, "E1450", {"points": [v(60.53, -4.57) * mm, v(59.96, -5.01) * mm, v(59.42, -5.43) * mm, v(58.88, -5.86) * mm]});
            skFitSpline(sketch, "E1451", {"points": [v(58.88, -5.86) * mm, v(59.01, -6.18) * mm, v(58.9, -6.48) * mm, v(58.86, -6.77) * mm]});
            skFitSpline(sketch, "E1452", {"points": [v(58.86, -6.77) * mm, v(58.74, -7.44) * mm, v(58.6, -8.1) * mm, v(58.48, -8.77) * mm]});
            skFitSpline(sketch, "E1453", {"points": [v(58.48, -8.77) * mm, v(58.46, -8.88) * mm, v(58.46, -8.99) * mm, v(58.45, -9.1) * mm]});
            skFitSpline(sketch, "E1454", {"points": [v(58.45, -9.1) * mm, v(58.43, -9.41) * mm, v(58.16, -9.66) * mm, v(57.87, -9.64) * mm]});
            skFitSpline(sketch, "E1455", {"points": [v(57.87, -9.64) * mm, v(57.57, -9.62) * mm, v(57.3, -9.36) * mm, v(57.34, -9.05) * mm]});
            skFitSpline(sketch, "E1456", {"points": [v(57.34, -9.05) * mm, v(57.38, -8.63) * mm, v(57.46, -8.22) * mm, v(57.53, -7.8) * mm]});
            skFitSpline(sketch, "E1457", {"points": [v(57.53, -7.8) * mm, v(57.59, -7.48) * mm, v(57.66, -7.16) * mm, v(57.74, -6.77) * mm]});
            skFitSpline(sketch, "E1458", {"points": [v(57.74, -6.77) * mm, v(56.77, -7.38) * mm, v(55.93, -8.07) * mm, v(55.03, -8.68) * mm]});
            skFitSpline(sketch, "E1459", {"points": [v(55.03, -8.68) * mm, v(55.03, -8.77) * mm, v(55.03, -8.85) * mm, v(55.03, -8.93) * mm]});
            skFitSpline(sketch, "E1460", {"points": [v(55.03, -8.93) * mm, v(55.02, -9.19) * mm, v(54.95, -9.42) * mm, v(54.77, -9.6) * mm]});
            skFitSpline(sketch, "E1461", {"points": [v(54.77, -9.6) * mm, v(54.66, -9.71) * mm, v(54.56, -9.82) * mm, v(54.47, -9.93) * mm]});
            skFitSpline(sketch, "E1462", {"points": [v(54.47, -9.93) * mm, v(54.1, -10.4) * mm, v(53.48, -10.37) * mm, v(53.05, -10.11) * mm]});
            skFitSpline(sketch, "E1463", {"points": [v(53.05, -10.11) * mm, v(52.62, -9.87) * mm, v(52.35, -9.49) * mm, v(52.25, -9) * mm]});
            skFitSpline(sketch, "E1464", {"points": [v(52.25, -9) * mm, v(52.15, -8.53) * mm, v(52.3, -7.93) * mm, v(52.84, -7.72) * mm]});
            skFitSpline(sketch, "E1465", {"points": [v(52.84, -7.72) * mm, v(52.93, -7.7) * mm, v(53.01, -7.66) * mm, v(53.1, -7.6) * mm]});
            skFitSpline(sketch, "E1466", {"points": [v(53.1, -7.6) * mm, v(53.42, -7.42) * mm, v(53.77, -7.4) * mm, v(54.13, -7.52) * mm]});
            skFitSpline(sketch, "E1467", {"points": [v(54.13, -7.52) * mm, v(54.22, -7.55) * mm, v(54.28, -7.54) * mm, v(54.35, -7.48) * mm]});
            skFitSpline(sketch, "E1468", {"points": [v(54.35, -7.48) * mm, v(55.15, -6.9) * mm, v(55.95, -6.3) * mm, v(56.74, -5.71) * mm]});
            skFitSpline(sketch, "E1469", {"points": [v(56.74, -5.71) * mm, v(56.77, -5.7) * mm, v(56.81, -5.68) * mm, v(56.85, -5.67) * mm]});
            skFitSpline(sketch, "E1470", {"points": [v(56.85, -5.67) * mm, v(56.84, -5.64) * mm, v(56.83, -5.61) * mm, v(56.82, -5.59) * mm]});
            skFitSpline(sketch, "E1471", {"points": [v(56.82, -5.59) * mm, v(56.62, -5.56) * mm, v(56.42, -5.54) * mm, v(56.23, -5.51) * mm]});
            skFitSpline(sketch, "E1472", {"points": [v(56.23, -5.51) * mm, v(55.72, -5.44) * mm, v(55.2, -5.39) * mm, v(54.7, -5.3) * mm]});
            skFitSpline(sketch, "E1473", {"points": [v(54.7, -5.3) * mm, v(54.37, -5.26) * mm, v(54.19, -5.03) * mm, v(54.19, -4.73) * mm]});
            skFitSpline(sketch, "E1474", {"points": [v(54.19, -4.73) * mm, v(54.19, -4.38) * mm, v(54.46, -4.13) * mm, v(54.8, -4.18) * mm]});
            skFitSpline(sketch, "E1475", {"points": [v(54.8, -4.18) * mm, v(55.75, -4.3) * mm, v(56.7, -4.45) * mm, v(57.65, -4.6) * mm]});
            skFitSpline(sketch, "E1476", {"points": [v(57.65, -4.6) * mm, v(57.8, -4.61) * mm, v(57.95, -4.7) * mm, v(58.13, -4.76) * mm]});
            skFitSpline(sketch, "E1477", {"points": [v(58.13, -4.76) * mm, v(58.67, -4.4) * mm, v(59.24, -4.02) * mm, v(59.8, -3.64) * mm]});
            skFitSpline(sketch, "E1478", {"points": [v(59.8, -3.64) * mm, v(59.8, -3.62) * mm, v(59.8, -3.6) * mm, v(59.8, -3.58) * mm]});
            skFitSpline(sketch, "E1479", {"points": [v(59.8, -3.58) * mm, v(59.41, -3.52) * mm, v(59.03, -3.45) * mm, v(58.65, -3.4) * mm]});
            skFitSpline(sketch, "E1480", {"points": [v(58.65, -3.4) * mm, v(58.34, -3.35) * mm, v(58.03, -3.32) * mm, v(57.72, -3.29) * mm]});
            skFitSpline(sketch, "E1481", {"points": [v(57.72, -3.29) * mm, v(57.67, -3.28) * mm, v(57.61, -3.27) * mm, v(57.56, -3.26) * mm]});
            skFitSpline(sketch, "E1482", {"points": [v(57.56, -3.26) * mm, v(57.26, -3.17) * mm, v(57.08, -2.89) * mm, v(57.14, -2.6) * mm]});
            skFitSpline(sketch, "E1483", {"points": [v(57.14, -2.6) * mm, v(57.2, -2.3) * mm, v(57.49, -2.12) * mm, v(57.8, -2.17) * mm]});
            skFitSpline(sketch, "E1484", {"points": [v(57.8, -2.17) * mm, v(58.89, -2.3) * mm, v(59.97, -2.44) * mm, v(61.05, -2.58) * mm]});
            skFitSpline(sketch, "E1485", {"points": [v(61.05, -2.58) * mm, v(61.2, -2.6) * mm, v(61.32, -2.56) * mm, v(61.43, -2.47) * mm]});
            skFitSpline(sketch, "E1486", {"points": [v(61.43, -2.47) * mm, v(61.56, -2.37) * mm, v(61.7, -2.27) * mm, v(61.83, -2.18) * mm]});
            skFitSpline(sketch, "E1487", {"points": [v(61.83, -2.18) * mm, v(62.36, -1.79) * mm, v(62.9, -1.4) * mm, v(63.43, -1.02) * mm]});
            skFitSpline(sketch, "E1488", {"points": [v(63.43, -1.02) * mm, v(63.6, -0.9) * mm, v(63.75, -0.77) * mm, v(63.94, -0.62) * mm]});
            skFitSpline(sketch, "E1489", {"points": [v(63.94, -0.62) * mm, v(63.69, -0.54) * mm, v(63.47, -0.6) * mm, v(63.26, -0.61) * mm]});
            skFitSpline(sketch, "E1490", {"points": [v(63.26, -0.61) * mm, v(62.83, -0.61) * mm, v(62.4, -0.65) * mm, v(61.97, -0.66) * mm]});
            skFitSpline(sketch, "E1491", {"points": [v(61.97, -0.66) * mm, v(61.28, -0.68) * mm, v(60.6, -0.7) * mm, v(59.9, -0.72) * mm]});
            skFitSpline(sketch, "E1492", {"points": [v(59.9, -0.72) * mm, v(59.42, -0.73) * mm, v(58.94, -0.76) * mm, v(58.45, -0.77) * mm]});
            skFitSpline(sketch, "E1493", {"points": [v(58.45, -0.77) * mm, v(58.19, -0.77) * mm, v(57.92, -0.73) * mm, v(57.66, -0.72) * mm]});
            skFitSpline(sketch, "E1494", {"points": [v(57.66, -0.72) * mm, v(57.3, -0.72) * mm, v(56.94, -0.74) * mm, v(56.58, -0.75) * mm]});
            skFitSpline(sketch, "E1495", {"points": [v(56.58, -0.75) * mm, v(56.25, -0.76) * mm, v(55.93, -0.77) * mm, v(55.6, -0.75) * mm]});
            skFitSpline(sketch, "E1496", {"points": [v(55.6, -0.75) * mm, v(55.44, -0.75) * mm, v(55.33, -0.78) * mm, v(55.23, -0.9) * mm]});
            skFitSpline(sketch, "E1497", {"points": [v(55.23, -0.9) * mm, v(55.15, -0.99) * mm, v(55.06, -1.09) * mm, v(54.98, -1.18) * mm]});
            skFitSpline(sketch, "E1498", {"points": [v(54.98, -1.18) * mm, v(54.65, -1.54) * mm, v(54.32, -1.9) * mm, v(53.98, -2.24) * mm]});
            skFitSpline(sketch, "E1499", {"points": [v(53.98, -2.24) * mm, v(53.65, -2.57) * mm, v(53.3, -2.87) * mm, v(52.97, -3.18) * mm]});
            skFitSpline(sketch, "E1500", {"points": [v(52.97, -3.18) * mm, v(52.71, -3.42) * mm, v(52.38, -3.42) * mm, v(52.16, -3.18) * mm]});
            skFitSpline(sketch, "E1501", {"points": [v(52.16, -3.18) * mm, v(51.93, -2.93) * mm, v(51.95, -2.58) * mm, v(52.2, -2.34) * mm]});
            skFitSpline(sketch, "E1502", {"points": [v(52.2, -2.34) * mm, v(52.7, -1.88) * mm, v(53.2, -1.41) * mm, v(53.7, -0.95) * mm]});
            skFitSpline(sketch, "E1503", {"points": [v(53.7, -0.95) * mm, v(53.76, -0.89) * mm, v(53.81, -0.82) * mm, v(53.84, -0.72) * mm]});
            skFitSpline(sketch, "E1504", {"points": [v(53.84, -0.72) * mm, v(53.66, -0.78) * mm, v(53.48, -0.84) * mm, v(53.3, -0.9) * mm]});
            skFitSpline(sketch, "E1505", {"points": [v(53.3, -0.9) * mm, v(52.7, -1.1) * mm, v(52.08, -1.31) * mm, v(51.48, -1.53) * mm]});
            skFitSpline(sketch, "E1506", {"points": [v(51.48, -1.53) * mm, v(51.25, -1.6) * mm, v(51.01, -1.7) * mm, v(50.79, -1.8) * mm]});
            skFitSpline(sketch, "E1507", {"points": [v(50.79, -1.8) * mm, v(50.5, -1.92) * mm, v(50.25, -1.92) * mm, v(49.97, -1.77) * mm]});
            skFitSpline(sketch, "E1508", {"points": [v(49.97, -1.77) * mm, v(49.37, -1.44) * mm, v(48.75, -1.14) * mm, v(48.13, -0.84) * mm]});
            skFitSpline(sketch, "E1509", {"points": [v(48.13, -0.84) * mm, v(47.96, -0.75) * mm, v(47.77, -0.7) * mm, v(47.6, -0.64) * mm]});
            skFitSpline(sketch, "E1510", {"points": [v(47.6, -0.64) * mm, v(47.3, -0.52) * mm, v(47.2, -0.32) * mm, v(47.19, 0.02) * mm]});
            skFitSpline(sketch, "E1511", {"points": [v(47.19, 0.02) * mm, v(47.18, 0.32) * mm, v(47.32, 0.54) * mm, v(47.6, 0.63) * mm]});
            skFitSpline(sketch, "E1512", {"points": [v(47.6, 0.63) * mm, v(48.43, 0.91) * mm, v(49.18, 1.36) * mm, v(49.95, 1.76) * mm]});
            skFitSpline(sketch, "E1513", {"points": [v(49.95, 1.76) * mm, v(50.25, 1.91) * mm, v(50.52, 1.92) * mm, v(50.82, 1.78) * mm]});
            skFitSpline(sketch, "E1514", {"points": [v(50.82, 1.78) * mm, v(51.02, 1.68) * mm, v(51.24, 1.6) * mm, v(51.46, 1.54) * mm]});
            skFitSpline(sketch, "E1515", {"points": [v(51.46, 1.54) * mm, v(52.17, 1.29) * mm, v(52.88, 1.05) * mm, v(53.6, 0.8) * mm]});
            skFitSpline(sketch, "E1516", {"points": [v(53.6, 0.8) * mm, v(53.68, 0.77) * mm, v(53.76, 0.75) * mm, v(53.85, 0.73) * mm]});
            skFitSpline(sketch, "E1517", {"points": [v(53.85, 0.73) * mm, v(53.58, 1.01) * mm, v(53.33, 1.3) * mm, v(53.05, 1.56) * mm]});
            skFitSpline(sketch, "E1518", {"points": [v(53.05, 1.56) * mm, v(52.77, 1.84) * mm, v(52.47, 2.1) * mm, v(52.18, 2.37) * mm]});
            skFitSpline(sketch, "E1519", {"points": [v(52.18, 2.37) * mm, v(51.94, 2.6) * mm, v(51.94, 2.95) * mm, v(52.17, 3.18) * mm]});
            skFitSpline(sketch, "E1520", {"points": [v(52.17, 3.18) * mm, v(52.38, 3.41) * mm, v(52.7, 3.42) * mm, v(52.95, 3.2) * mm]});
            skFitSpline(sketch, "E1521", {"points": [v(52.95, 3.2) * mm, v(53.33, 2.85) * mm, v(53.72, 2.5) * mm, v(54.08, 2.15) * mm]});
            skFitSpline(sketch, "E1522", {"points": [v(54.08, 2.15) * mm, v(54.42, 1.8) * mm, v(54.74, 1.43) * mm, v(55.07, 1.07) * mm]});
            skFitSpline(sketch, "E1523", {"points": [v(55.07, 1.07) * mm, v(55.14, 1) * mm, v(55.21, 0.9) * mm, v(55.3, 0.84) * mm]});
            skFitSpline(sketch, "E1524", {"points": [v(55.3, 0.84) * mm, v(55.36, 0.79) * mm, v(55.44, 0.74) * mm, v(55.52, 0.75) * mm]});
            skFitSpline(sketch, "E1525", {"points": [v(55.52, 0.75) * mm, v(56.04, 0.77) * mm, v(56.56, 0.74) * mm, v(57.08, 0.72) * mm]});
            skFitSpline(sketch, "E1526", {"points": [v(57.08, 0.72) * mm, v(57.43, 0.71) * mm, v(57.8, 0.77) * mm, v(58.15, 0.77) * mm]});
            skFitSpline(sketch, "E1527", {"points": [v(58.15, 0.77) * mm, v(58.8, 0.76) * mm, v(59.45, 0.72) * mm, v(60.1, 0.7) * mm]});
            skFitSpline(sketch, "E1528", {"points": [v(60.1, 0.7) * mm, v(60.4, 0.69) * mm, v(60.72, 0.67) * mm, v(61.03, 0.66) * mm]});
            skFitSpline(sketch, "E1529", {"points": [v(61.03, 0.66) * mm, v(61.61, 0.65) * mm, v(62.19, 0.65) * mm, v(62.77, 0.63) * mm]});
            skFitSpline(sketch, "E1530", {"points": [v(62.77, 0.63) * mm, v(63.06, 0.62) * mm, v(63.35, 0.6) * mm, v(63.64, 0.58) * mm]});
            skFitSpline(sketch, "E1531", {"points": [v(63.64, 0.58) * mm, v(63.74, 0.58) * mm, v(63.83, 0.58) * mm, v(63.97, 0.58) * mm]});
            skFitSpline(sketch, "E1532", {"points": [v(63.97, 0.58) * mm, v(63.8, 0.72) * mm, v(63.67, 0.84) * mm, v(63.52, 0.95) * mm]});
            skFitSpline(sketch, "E1533", {"points": [v(63.52, 0.95) * mm, v(63.16, 1.21) * mm, v(62.79, 1.46) * mm, v(62.42, 1.73) * mm]});
            skFitSpline(sketch, "E1534", {"points": [v(62.42, 1.73) * mm, v(62.11, 1.95) * mm, v(61.8, 2.19) * mm, v(61.5, 2.43) * mm]});
            skFitSpline(sketch, "E1535", {"points": [v(61.5, 2.43) * mm, v(61.34, 2.55) * mm, v(61.18, 2.6) * mm, v(60.97, 2.57) * mm]});
            skFitSpline(sketch, "E1536", {"points": [v(60.97, 2.57) * mm, v(60.2, 2.46) * mm, v(59.44, 2.37) * mm, v(58.68, 2.28) * mm]});
            skFitSpline(sketch, "E1537", {"points": [v(58.68, 2.28) * mm, v(58.39, 2.24) * mm, v(58.1, 2.2) * mm, v(57.8, 2.17) * mm]});
            skFitSpline(sketch, "E1538", {"points": [v(57.8, 2.17) * mm, v(57.47, 2.12) * mm, v(57.2, 2.32) * mm, v(57.14, 2.63) * mm]});
            skFitSpline(sketch, "E1539", {"points": [v(57.14, 2.63) * mm, v(57.09, 2.94) * mm, v(57.3, 3.22) * mm, v(57.64, 3.27) * mm]});
            skFitSpline(sketch, "E1540", {"points": [v(57.64, 3.27) * mm, v(58.26, 3.36) * mm, v(58.9, 3.44) * mm, v(59.52, 3.53) * mm]});
            skFitSpline(sketch, "E1541", {"points": [v(59.52, 3.53) * mm, v(59.61, 3.54) * mm, v(59.7, 3.57) * mm, v(59.86, 3.6) * mm]});
            skFitSpline(sketch, "E1542", {"points": [v(59.86, 3.6) * mm, v(59.24, 4.01) * mm, v(58.68, 4.4) * mm, v(58.1, 4.78) * mm]});
            skFitSpline(sketch, "E1543", {"points": [v(58.1, 4.78) * mm, v(57.73, 4.52) * mm, v(57.3, 4.54) * mm, v(56.9, 4.47) * mm]});
            skFitSpline(sketch, "E1544", {"points": [v(56.9, 4.47) * mm, v(56.4, 4.4) * mm, v(55.91, 4.36) * mm, v(55.42, 4.3) * mm]});
            skFitSpline(sketch, "E1545", {"points": [v(55.42, 4.3) * mm, v(55.27, 4.28) * mm, v(55.12, 4.24) * mm, v(54.96, 4.2) * mm]});
            skFitSpline(sketch, "E1546", {"points": [v(54.96, 4.2) * mm, v(54.58, 4.12) * mm, v(54.27, 4.27) * mm, v(54.2, 4.58) * mm]});
            skFitSpline(sketch, "E1547", {"points": [v(54.2, 4.58) * mm, v(54.12, 4.95) * mm, v(54.33, 5.25) * mm, v(54.72, 5.31) * mm]});
            skFitSpline(sketch, "E1548", {"points": [v(54.72, 5.31) * mm, v(55.24, 5.39) * mm, v(55.76, 5.45) * mm, v(56.28, 5.51) * mm]});
            skFitSpline(sketch, "E1549", {"points": [v(56.28, 5.51) * mm, v(56.46, 5.54) * mm, v(56.63, 5.56) * mm, v(56.87, 5.6) * mm]});
            skFitSpline(sketch, "E1550", {"points": [v(56.87, 5.6) * mm, v(56, 6.32) * mm, v(55.1, 6.9) * mm, v(54.25, 7.55) * mm]});
            skFitSpline(sketch, "E1551", {"points": [v(54.25, 7.55) * mm, v(54.17, 7.53) * mm, v(54.1, 7.5) * mm, v(54.01, 7.49) * mm]});
            skFitSpline(sketch, "E1552", {"points": [v(54.01, 7.49) * mm, v(53.73, 7.42) * mm, v(53.45, 7.42) * mm, v(53.18, 7.57) * mm]});
            skFitSpline(sketch, "E1553", {"points": [v(53.18, 7.57) * mm, v(53.07, 7.63) * mm, v(52.95, 7.68) * mm, v(52.83, 7.73) * mm]});
            skFitSpline(sketch, "E1554", {"points": [v(52.83, 7.73) * mm, v(52.3, 7.93) * mm, v(52.14, 8.57) * mm, v(52.26, 9.04) * mm]});
            skFitSpline(sketch, "E1555", {"points": [v(52.26, 9.04) * mm, v(52.37, 9.5) * mm, v(52.63, 9.86) * mm, v(53.03, 10.1) * mm]});
            skFitSpline(sketch, "E1556", {"points": [v(53.03, 10.1) * mm, v(53.47, 10.37) * mm, v(54.09, 10.4) * mm, v(54.46, 9.95) * mm]});
            skFitSpline(sketch, "E1557", {"points": [v(54.46, 9.95) * mm, v(54.53, 9.86) * mm, v(54.6, 9.78) * mm, v(54.68, 9.7) * mm]});
            skFitSpline(sketch, "E1558", {"points": [v(54.68, 9.7) * mm, v(54.94, 9.46) * mm, v(55.05, 9.17) * mm, v(55.03, 8.82) * mm]});
            skFitSpline(sketch, "E1559", {"points": [v(55.03, 8.82) * mm, v(55.03, 8.77) * mm, v(55.04, 8.73) * mm, v(55.04, 8.67) * mm]});
            skFitSpline(sketch, "E1560", {"points": [v(55.04, 8.67) * mm, v(55.92, 8.04) * mm, v(56.8, 7.41) * mm, v(57.67, 6.78) * mm]});
            skFitSpline(sketch, "E1561", {"points": [v(57.67, 6.78) * mm, v(57.7, 6.8) * mm, v(57.7, 6.8) * mm, v(57.72, 6.82) * mm]});
            skFitSpline(sketch, "E1562", {"points": [v(57.72, 6.82) * mm, v(57.66, 7.15) * mm, v(57.59, 7.48) * mm, v(57.53, 7.81) * mm]});
            skFitSpline(sketch, "E1563", {"points": [v(57.53, 7.81) * mm, v(57.46, 8.2) * mm, v(57.4, 8.6) * mm, v(57.33, 9) * mm]});
            skFitSpline(sketch, "E1564", {"points": [v(57.33, 9) * mm, v(57.3, 9.25) * mm, v(57.41, 9.43) * mm, v(57.62, 9.56) * mm]});
            skFitSpline(sketch, "E1565", {"points": [v(57.62, 9.56) * mm, v(58, 9.8) * mm, v(58.4, 9.47) * mm, v(58.45, 9.17) * mm]});
            skFitSpline(sketch, "E1566", {"points": [v(58.45, 9.17) * mm, v(58.56, 8.49) * mm, v(58.69, 7.8) * mm, v(58.8, 7.12) * mm]});
            skFitSpline(sketch, "E1567", {"points": [v(58.8, 7.12) * mm, v(58.85, 6.86) * mm, v(58.9, 6.6) * mm, v(58.93, 6.33) * mm]});
            skFitSpline(sketch, "E1568", {"points": [v(58.93, 6.33) * mm, v(58.95, 6.19) * mm, v(58.93, 6.04) * mm, v(58.93, 5.9) * mm]});
            skFitSpline(sketch, "E1569", {"points": [v(58.93, 5.9) * mm, v(58.91, 5.89) * mm, v(58.9, 5.88) * mm, v(58.87, 5.87) * mm]});
            skFitSpline(sketch, "E1570", {"points": [v(58.87, 5.87) * mm, v(59.42, 5.44) * mm, v(59.96, 5.01) * mm, v(60.5, 4.59) * mm]});
            skFitSpline(sketch, "E1571", {"points": [v(60.5, 4.59) * mm, v(60.52, 4.6) * mm, v(60.54, 4.6) * mm, v(60.56, 4.62) * mm]});
            skFitSpline(sketch, "E1572", {"points": [v(60.56, 4.62) * mm, v(60.49, 5.04) * mm, v(60.42, 5.46) * mm, v(60.35, 5.88) * mm]});
            skFitSpline(sketch, "E1573", {"points": [v(60.35, 5.88) * mm, v(60.3, 6.17) * mm, v(60.22, 6.45) * mm, v(60.17, 6.74) * mm]});
            skFitSpline(sketch, "E1574", {"points": [v(60.17, 6.74) * mm, v(60.11, 7.07) * mm, v(60.3, 7.37) * mm, v(60.6, 7.43) * mm]});
            skFitSpline(sketch, "E1575", {"points": [v(60.6, 7.43) * mm, v(60.92, 7.5) * mm, v(61.2, 7.31) * mm, v(61.26, 6.96) * mm]});
            skFitSpline(sketch, "E1576", {"points": [v(61.26, 6.96) * mm, v(61.4, 6.3) * mm, v(61.5, 5.63) * mm, v(61.63, 4.96) * mm]});
            skFitSpline(sketch, "E1577", {"points": [v(61.63, 4.96) * mm, v(61.72, 4.52) * mm, v(61.81, 4.08) * mm, v(61.92, 3.65) * mm]});
            skFitSpline(sketch, "E1578", {"points": [v(61.92, 3.65) * mm, v(61.94, 3.57) * mm, v(62, 3.49) * mm, v(62.07, 3.44) * mm]});
            skFitSpline(sketch, "E1579", {"points": [v(62.07, 3.44) * mm, v(62.24, 3.3) * mm, v(62.42, 3.2) * mm, v(62.59, 3.07) * mm]});
            skFitSpline(sketch, "E1580", {"points": [v(62.59, 3.07) * mm, v(63.1, 2.7) * mm, v(63.6, 2.32) * mm, v(64.12, 1.95) * mm]});
            skFitSpline(sketch, "E1581", {"points": [v(64.12, 1.95) * mm, v(64.29, 1.82) * mm, v(64.47, 1.72) * mm, v(64.68, 1.58) * mm]});
            skFitSpline(sketch, "E1582", {"points": [v(64.68, 1.58) * mm, v(64.64, 1.7) * mm, v(64.62, 1.78) * mm, v(64.6, 1.85) * mm]});
            skFitSpline(sketch, "E1583", {"points": [v(64.6, 1.85) * mm, v(64.24, 2.84) * mm, v(63.88, 3.84) * mm, v(63.52, 4.83) * mm]});
            skFitSpline(sketch, "E1584", {"points": [v(63.52, 4.83) * mm, v(63.3, 5.43) * mm, v(63.06, 6.03) * mm, v(62.85, 6.63) * mm]});
            skFitSpline(sketch, "E1585", {"points": [v(62.85, 6.63) * mm, v(62.53, 7.6) * mm, v(62.23, 8.59) * mm, v(61.91, 9.57) * mm]});
            skFitSpline(sketch, "E1586", {"points": [v(61.91, 9.57) * mm, v(61.9, 9.64) * mm, v(61.83, 9.71) * mm, v(61.76, 9.75) * mm]});
            skFitSpline(sketch, "E1587", {"points": [v(61.76, 9.75) * mm, v(61.64, 9.82) * mm, v(61.5, 9.88) * mm, v(61.36, 9.93) * mm]});
            skFitSpline(sketch, "E1588", {"points": [v(61.36, 9.93) * mm, v(60.72, 10.18) * mm, v(60.1, 10.5) * mm, v(59.53, 10.87) * mm]});
            skFitSpline(sketch, "E1589", {"points": [v(59.53, 10.87) * mm, v(59.31, 11) * mm, v(59.07, 11.1) * mm, v(58.84, 11.22) * mm]});
            skFitSpline(sketch, "E1590", {"points": [v(58.84, 11.22) * mm, v(58.66, 11.3) * mm, v(58.53, 11.45) * mm, v(58.5, 11.66) * mm]});
            skFitSpline(sketch, "E1591", {"points": [v(58.5, 11.66) * mm, v(58.48, 11.88) * mm, v(58.56, 12.06) * mm, v(58.74, 12.19) * mm]});
            skFitSpline(sketch, "E1592", {"points": [v(58.74, 12.19) * mm, v(58.92, 12.32) * mm, v(59.13, 12.34) * mm, v(59.33, 12.24) * mm]});
            skFitSpline(sketch, "E1593", {"points": [v(59.33, 12.24) * mm, v(59.67, 12.07) * mm, v(60, 11.87) * mm, v(60.32, 11.7) * mm]});
            skFitSpline(sketch, "E1594", {"points": [v(60.32, 11.7) * mm, v(60.67, 11.5) * mm, v(61.02, 11.3) * mm, v(61.37, 11.12) * mm]});
            skFitSpline(sketch, "E1595", {"points": [v(61.37, 11.12) * mm, v(61.39, 11.13) * mm, v(61.4, 11.15) * mm, v(61.41, 11.16) * mm]});
            skFitSpline(sketch, "E1596", {"points": [v(61.41, 11.16) * mm, v(61.38, 11.22) * mm, v(61.35, 11.28) * mm, v(61.3, 11.33) * mm]});
            skFitSpline(sketch, "E1597", {"points": [v(61.3, 11.33) * mm, v(60.78, 12.05) * mm, v(60.25, 12.76) * mm, v(59.7, 13.47) * mm]});
            skFitSpline(sketch, "E1598", {"points": [v(59.7, 13.47) * mm, v(59.62, 13.59) * mm, v(59.51, 13.69) * mm, v(59.42, 13.8) * mm]});
            skFitSpline(sketch, "E1599", {"points": [v(59.42, 13.8) * mm, v(59.25, 14) * mm, v(59.19, 14.21) * mm, v(59.23, 14.49) * mm]});
            skFitSpline(sketch, "E1600", {"points": [v(59.23, 14.49) * mm, v(59.37, 15.25) * mm, v(59.47, 16.02) * mm, v(59.59, 16.8) * mm]});
            skFitSpline(sketch, "E1601", {"points": [v(59.59, 16.8) * mm, v(59.6, 16.9) * mm, v(59.6, 17.01) * mm, v(59.6, 17.13) * mm]});
            skFitSpline(sketch, "E1602", {"points": [v(59.6, 17.13) * mm, v(59.59, 17.4) * mm, v(59.72, 17.58) * mm, v(59.96, 17.68) * mm]});
            skFitSpline(sketch, "E1603", {"points": [v(59.96, 17.68) * mm, v(60.22, 17.8) * mm, v(60.48, 17.82) * mm, v(60.7, 17.6) * mm]});
            skFitSpline(sketch, "E1604", {"points": [v(60.7, 17.6) * mm, v(60.74, 17.59) * mm, v(60.76, 17.56) * mm, v(60.78, 17.53) * mm]});
            skFitSpline(sketch, "E1605", {"points": [v(60.78, 17.53) * mm, v(61.28, 16.84) * mm, v(61.92, 16.28) * mm, v(62.52, 15.7) * mm]});
            skFitSpline(sketch, "E1606", {"points": [v(62.52, 15.7) * mm, v(62.79, 15.44) * mm, v(62.92, 15.17) * mm, v(62.86, 14.82) * mm]});
            skFitSpline(sketch, "E1607", {"points": [v(62.86, 14.82) * mm, v(62.8, 14.49) * mm, v(62.85, 14.16) * mm, v(62.84, 13.83) * mm]});
            skFitSpline(sketch, "E1608", {"points": [v(62.84, 13.83) * mm, v(62.82, 13.17) * mm, v(62.8, 12.51) * mm, v(62.79, 11.85) * mm]});
            skFitSpline(sketch, "E1609", {"points": [v(62.79, 11.85) * mm, v(62.79, 11.77) * mm, v(62.79, 11.69) * mm, v(62.79, 11.55) * mm]});
            skFitSpline(sketch, "E1610", {"points": [v(62.79, 11.55) * mm, v(62.85, 11.63) * mm, v(62.89, 11.66) * mm, v(62.9, 11.7) * mm]});
            skFitSpline(sketch, "E1611", {"points": [v(62.9, 11.7) * mm, v(63.1, 12.1) * mm, v(63.28, 12.51) * mm, v(63.47, 12.92) * mm]});
            skFitSpline(sketch, "E1612", {"points": [v(63.47, 12.92) * mm, v(63.6, 13.2) * mm, v(63.73, 13.47) * mm, v(63.87, 13.73) * mm]});
            skFitSpline(sketch, "E1613", {"points": [v(63.87, 13.73) * mm, v(64.02, 14) * mm, v(64.37, 14.1) * mm, v(64.64, 13.96) * mm]});
            skFitSpline(sketch, "E1614", {"points": [v(64.64, 13.96) * mm, v(64.9, 13.81) * mm, v(65.03, 13.5) * mm, v(64.88, 13.23) * mm]});
            skFitSpline(sketch, "E1615", {"points": [v(64.88, 13.23) * mm, v(64.4, 12.34) * mm, v(64.1, 11.36) * mm, v(63.5, 10.53) * mm]});
            skFitSpline(sketch, "E1616", {"points": [v(63.5, 10.53) * mm, v(63.44, 10.44) * mm, v(63.39, 10.35) * mm, v(63.35, 10.24) * mm]});
            skFitSpline(sketch, "E1617", {"points": [v(63.35, 10.24) * mm, v(63.33, 10.18) * mm, v(63.33, 10.1) * mm, v(63.34, 10.04) * mm]});
            skFitSpline(sketch, "E1618", {"points": [v(63.34, 10.04) * mm, v(63.52, 9.47) * mm, v(63.69, 8.91) * mm, v(63.87, 8.36) * mm]});
            skFitSpline(sketch, "E1619", {"points": [v(63.87, 8.36) * mm, v(64.1, 7.69) * mm, v(64.35, 7.03) * mm, v(64.54, 6.35) * mm]});
            skFitSpline(sketch, "E1620", {"points": [v(64.54, 6.35) * mm, v(64.96, 4.94) * mm, v(65.34, 3.53) * mm, v(65.74, 2.11) * mm]});
            skFitSpline(sketch, "E1621", {"points": [v(65.74, 2.11) * mm, v(65.75, 2.07) * mm, v(65.77, 2.03) * mm, v(65.8, 1.93) * mm]});
            skFitSpline(sketch, "E1622", {"points": [v(65.8, 1.93) * mm, v(65.94, 2.29) * mm, v(66.06, 2.6) * mm, v(66.16, 2.91) * mm]});
            skFitSpline(sketch, "E1623", {"points": [v(66.16, 2.91) * mm, v(66.39, 3.6) * mm, v(66.6, 4.27) * mm, v(66.82, 4.95) * mm]});
            skFitSpline(sketch, "E1624", {"points": [v(66.82, 4.95) * mm, v(66.86, 5.07) * mm, v(66.86, 5.18) * mm, v(66.8, 5.3) * mm]});
            skFitSpline(sketch, "E1625", {"points": [v(66.8, 5.3) * mm, v(66.55, 5.83) * mm, v(66.31, 6.36) * mm, v(66.06, 6.9) * mm]});
            skFitSpline(sketch, "E1626", {"points": [v(66.06, 6.9) * mm, v(65.84, 7.37) * mm, v(65.61, 7.84) * mm, v(65.4, 8.31) * mm]});
            skFitSpline(sketch, "E1627", {"points": [v(65.4, 8.31) * mm, v(65.25, 8.62) * mm, v(65.36, 8.93) * mm, v(65.63, 9.06) * mm]});
            skFitSpline(sketch, "E1628", {"points": [v(65.63, 9.06) * mm, v(65.92, 9.2) * mm, v(66.25, 9.1) * mm, v(66.4, 8.79) * mm]});
            skFitSpline(sketch, "E1629", {"points": [v(66.4, 8.79) * mm, v(66.52, 8.56) * mm, v(66.62, 8.32) * mm, v(66.73, 8.1) * mm]});
            skFitSpline(sketch, "E1630", {"points": [v(66.73, 8.1) * mm, v(66.93, 7.69) * mm, v(67.13, 7.29) * mm, v(67.33, 6.88) * mm]});
            skFitSpline(sketch, "E1631", {"points": [v(67.33, 6.88) * mm, v(67.34, 6.86) * mm, v(67.37, 6.85) * mm, v(67.4, 6.81) * mm]});
            skFitSpline(sketch, "E1632", {"points": [v(67.4, 6.81) * mm, v(67.6, 7.49) * mm, v(67.79, 8.14) * mm, v(67.98, 8.81) * mm]});
            skFitSpline(sketch, "E1633", {"points": [v(67.98, 8.81) * mm, v(67.75, 8.97) * mm, v(67.64, 9.2) * mm, v(67.53, 9.43) * mm]});
            skFitSpline(sketch, "E1634", {"points": [v(67.53, 9.43) * mm, v(67.3, 9.92) * mm, v(67.06, 10.41) * mm, v(66.83, 10.9) * mm]});
            skFitSpline(sketch, "E1635", {"points": [v(66.83, 10.9) * mm, v(66.7, 11.16) * mm, v(66.57, 11.42) * mm, v(66.43, 11.68) * mm]});
            skFitSpline(sketch, "E1636", {"points": [v(66.43, 11.68) * mm, v(66.33, 11.85) * mm, v(66.3, 12.02) * mm, v(66.37, 12.2) * mm]});
            skFitSpline(sketch, "E1637", {"points": [v(66.37, 12.2) * mm, v(66.45, 12.4) * mm, v(66.6, 12.52) * mm, v(66.8, 12.54) * mm]});
            skFitSpline(sketch, "E1638", {"points": [v(66.8, 12.54) * mm, v(67.06, 12.56) * mm, v(67.27, 12.5) * mm, v(67.4, 12.27) * mm]});
            skFitSpline(sketch, "E1639", {"points": [v(67.4, 12.27) * mm, v(67.52, 12.04) * mm, v(67.64, 11.81) * mm, v(67.75, 11.58) * mm]});
            skFitSpline(sketch, "E1640", {"points": [v(67.75, 11.58) * mm, v(67.89, 11.3) * mm, v(68.01, 11) * mm, v(68.15, 10.7) * mm]});
            skFitSpline(sketch, "E1641", {"points": [v(68.15, 10.7) * mm, v(68.21, 10.57) * mm, v(68.28, 10.43) * mm, v(68.37, 10.24) * mm]});
            skFitSpline(sketch, "E1642", {"points": [v(68.37, 10.24) * mm, v(68.45, 10.44) * mm, v(68.52, 10.6) * mm, v(68.58, 10.75) * mm]});
            skFitSpline(sketch, "E1643", {"points": [v(68.58, 10.75) * mm, v(68.85, 11.57) * mm, v(69.12, 12.39) * mm, v(69.38, 13.2) * mm]});
            skFitSpline(sketch, "E1644", {"points": [v(69.38, 13.2) * mm, v(69.4, 13.27) * mm, v(69.4, 13.36) * mm, v(69.37, 13.4) * mm]});
            skFitSpline(sketch, "E1645", {"points": [v(69.37, 13.4) * mm, v(69.03, 13.81) * mm, v(69.09, 14.27) * mm, v(69.15, 14.74) * mm]});
            skFitSpline(sketch, "E1646", {"points": [v(69.15, 14.74) * mm, v(69.23, 15.33) * mm, v(69.66, 15.6) * mm, v(70.1, 15.67) * mm]});
            skFitSpline(sketch, "E1647", {"points": [v(70.1, 15.67) * mm, v(70.64, 15.76) * mm, v(71.13, 15.6) * mm, v(71.53, 15.23) * mm]});
            skFitSpline(sketch, "E1648", {"points": [v(71.53, 15.23) * mm, v(71.88, 14.9) * mm, v(72.06, 14.33) * mm, v(71.76, 13.86) * mm]});
            skFitSpline(sketch, "E1649", {"points": [v(71.76, 13.86) * mm, v(71.72, 13.8) * mm, v(71.7, 13.75) * mm, v(71.66, 13.7) * mm]});
            skFitSpline(sketch, "E1650", {"points": [v(71.66, 13.7) * mm, v(71.5, 13.32) * mm, v(71.23, 13.06) * mm, v(70.83, 12.95) * mm]});
            skFitSpline(sketch, "E1651", {"points": [v(70.83, 12.95) * mm, v(70.77, 12.93) * mm, v(70.71, 12.86) * mm, v(70.7, 12.8) * mm]});
            skFitSpline(sketch, "E1652", {"points": [v(70.7, 12.8) * mm, v(70.39, 11.84) * mm, v(70.09, 10.87) * mm, v(69.79, 9.91) * mm]});
            skFitSpline(sketch, "E1653", {"points": [v(69.79, 9.91) * mm, v(69.78, 9.89) * mm, v(69.79, 9.86) * mm, v(69.79, 9.8) * mm]});
            skFitSpline(sketch, "E1654", {"points": [v(69.79, 9.8) * mm, v(69.93, 9.88) * mm, v(70.06, 9.95) * mm, v(70.19, 10.01) * mm]});
            skFitSpline(sketch, "E1655", {"points": [v(70.19, 10.01) * mm, v(70.7, 10.29) * mm, v(71.2, 10.56) * mm, v(71.71, 10.84) * mm]});
            skFitSpline(sketch, "E1656", {"points": [v(71.71, 10.84) * mm, v(71.9, 10.94) * mm, v(72.08, 10.93) * mm, v(72.26, 10.83) * mm]});
            skFitSpline(sketch, "E1657", {"points": [v(72.26, 10.83) * mm, v(72.65, 10.6) * mm, v(72.67, 10.07) * mm, v(72.28, 9.86) * mm]});
            skFitSpline(sketch, "E1658", {"points": [v(72.28, 9.86) * mm, v(71.41, 9.4) * mm, v(70.54, 8.94) * mm, v(69.67, 8.5) * mm]});
            skFitSpline(sketch, "E1659", {"points": [v(69.67, 8.5) * mm, v(69.55, 8.43) * mm, v(69.4, 8.42) * mm, v(69.24, 8.37) * mm]});
            skFitSpline(sketch, "E1660", {"points": [v(69.24, 8.37) * mm, v(69.01, 7.76) * mm, v(68.77, 7.12) * mm, v(68.52, 6.44) * mm]});
            skFitSpline(sketch, "E1661", {"points": [v(68.52, 6.44) * mm, v(68.6, 6.46) * mm, v(68.66, 6.48) * mm, v(68.71, 6.5) * mm]});
            skFitSpline(sketch, "E1662", {"points": [v(68.71, 6.5) * mm, v(69.27, 6.8) * mm, v(69.83, 7.1) * mm, v(70.39, 7.4) * mm]});
            skFitSpline(sketch, "E1663", {"points": [v(70.39, 7.4) * mm, v(70.53, 7.48) * mm, v(70.67, 7.53) * mm, v(70.83, 7.52) * mm]});
            skFitSpline(sketch, "E1664", {"points": [v(70.83, 7.52) * mm, v(71.06, 7.5) * mm, v(71.26, 7.36) * mm, v(71.32, 7.14) * mm]});
            skFitSpline(sketch, "E1665", {"points": [v(71.32, 7.14) * mm, v(71.39, 6.92) * mm, v(71.34, 6.72) * mm, v(71.16, 6.56) * mm]});
            skFitSpline(sketch, "E1666", {"points": [v(71.16, 6.56) * mm, v(71.12, 6.53) * mm, v(71.08, 6.5) * mm, v(71.03, 6.47) * mm]});
            skFitSpline(sketch, "E1667", {"points": [v(71.03, 6.47) * mm, v(70.57, 6.22) * mm, v(70.1, 5.97) * mm, v(69.65, 5.72) * mm]});
            skFitSpline(sketch, "E1668", {"points": [v(69.65, 5.72) * mm, v(69.14, 5.43) * mm, v(68.63, 5.14) * mm, v(68.11, 4.86) * mm]});
            skFitSpline(sketch, "E1669", {"points": [v(68.11, 4.86) * mm, v(68, 4.8) * mm, v(67.95, 4.72) * mm, v(67.92, 4.61) * mm]});
            skFitSpline(sketch, "E1670", {"points": [v(67.92, 4.61) * mm, v(67.87, 4.46) * mm, v(67.83, 4.31) * mm, v(67.78, 4.17) * mm]});
            skFitSpline(sketch, "E1671", {"points": [v(67.78, 4.17) * mm, v(67.57, 3.51) * mm, v(67.35, 2.86) * mm, v(67.14, 2.2) * mm]});
            skFitSpline(sketch, "E1672", {"points": [v(67.14, 2.2) * mm, v(67.08, 2.01) * mm, v(67.03, 1.82) * mm, v(66.97, 1.57) * mm]});
            skFitSpline(sketch, "E1673", {"points": [v(66.97, 1.57) * mm, v(67.07, 1.64) * mm, v(67.13, 1.68) * mm, v(67.18, 1.72) * mm]});
            skFitSpline(sketch, "E1674", {"points": [v(67.18, 1.72) * mm, v(67.97, 2.33) * mm, v(68.76, 2.95) * mm, v(69.55, 3.56) * mm]});
            skFitSpline(sketch, "E1675", {"points": [v(69.55, 3.56) * mm, v(70.12, 4) * mm, v(70.68, 4.47) * mm, v(71.26, 4.9) * mm]});
            skFitSpline(sketch, "E1676", {"points": [v(71.26, 4.9) * mm, v(71.68, 5.22) * mm, v(72.13, 5.51) * mm, v(72.57, 5.82) * mm]});
            skFitSpline(sketch, "E1677", {"points": [v(72.57, 5.82) * mm, v(72.95, 6.1) * mm, v(73.32, 6.38) * mm, v(73.7, 6.65) * mm]});
            skFitSpline(sketch, "E1678", {"points": [v(73.7, 6.65) * mm, v(73.83, 6.74) * mm, v(73.85, 6.88) * mm, v(73.86, 7) * mm]});
            skFitSpline(sketch, "E1679", {"points": [v(73.86, 7) * mm, v(73.9, 7.25) * mm, v(73.9, 7.48) * mm, v(73.92, 7.72) * mm]});
            skFitSpline(sketch, "E1680", {"points": [v(73.92, 7.72) * mm, v(73.98, 8.14) * mm, v(74.04, 8.56) * mm, v(74.11, 8.97) * mm]});
            skFitSpline(sketch, "E1681", {"points": [v(74.11, 8.97) * mm, v(74.17, 9.34) * mm, v(74.26, 9.7) * mm, v(74.32, 10.07) * mm]});
            skFitSpline(sketch, "E1682", {"points": [v(74.32, 10.07) * mm, v(74.38, 10.37) * mm, v(74.53, 10.55) * mm, v(74.78, 10.6) * mm]});
            skFitSpline(sketch, "E1683", {"points": [v(74.78, 10.6) * mm, v(75.2, 10.67) * mm, v(75.53, 10.31) * mm, v(75.44, 9.89) * mm]});
            skFitSpline(sketch, "E1684", {"points": [v(75.44, 9.89) * mm, v(75.33, 9.35) * mm, v(75.22, 8.81) * mm, v(75.12, 8.27) * mm]});
            skFitSpline(sketch, "E1685", {"points": [v(75.12, 8.27) * mm, v(75.08, 8.07) * mm, v(75.05, 7.86) * mm, v(75.02, 7.65) * mm]});
            skFitSpline(sketch, "E1686", {"points": [v(75.02, 7.65) * mm, v(75.05, 7.63) * mm, v(75.07, 7.62) * mm, v(75.1, 7.6) * mm]});
            skFitSpline(sketch, "E1687", {"points": [v(75.1, 7.6) * mm, v(75.12, 7.65) * mm, v(75.15, 7.7) * mm, v(75.18, 7.76) * mm]});
            skFitSpline(sketch, "E1688", {"points": [v(75.18, 7.76) * mm, v(75.7, 8.5) * mm, v(76.23, 9.24) * mm, v(76.75, 9.99) * mm]});
            skFitSpline(sketch, "E1689", {"points": [v(76.75, 9.99) * mm, v(76.84, 10.1) * mm, v(76.9, 10.24) * mm, v(76.97, 10.37) * mm]});
            skFitSpline(sketch, "E1690", {"points": [v(76.97, 10.37) * mm, v(77.1, 10.56) * mm, v(77.26, 10.69) * mm, v(77.5, 10.72) * mm]});
            skFitSpline(sketch, "E1691", {"points": [v(77.5, 10.72) * mm, v(78.06, 10.8) * mm, v(78.63, 10.88) * mm, v(79.19, 10.98) * mm]});
            skFitSpline(sketch, "E1692", {"points": [v(79.19, 10.98) * mm, v(79.5, 11.03) * mm, v(79.8, 11.12) * mm, v(80.1, 11.2) * mm]});
            skFitSpline(sketch, "E1693", {"points": [v(80.1, 11.2) * mm, v(80.48, 11.3) * mm, v(80.7, 11.23) * mm, v(80.92, 10.9) * mm]});
            skFitSpline(sketch, "E1694", {"points": [v(80.92, 10.9) * mm, v(81.07, 10.67) * mm, v(81.09, 10.42) * mm, v(80.93, 10.2) * mm]});
            skFitSpline(sketch, "E1695", {"points": [v(80.93, 10.2) * mm, v(80.4, 9.46) * mm, v(80.06, 8.63) * mm, v(79.65, 7.83) * mm]});
            skFitSpline(sketch, "E1696", {"points": [v(79.65, 7.83) * mm, v(79.53, 7.61) * mm, v(79.37, 7.48) * mm, v(79.13, 7.4) * mm]});
            skFitSpline(sketch, "E1697", {"points": [v(79.13, 7.4) * mm, v(78.45, 7.2) * mm, v(77.76, 7) * mm, v(77.08, 6.8) * mm]});
            skFitSpline(sketch, "E1698", {"points": [v(77.08, 6.8) * mm, v(76.7, 6.68) * mm, v(76.3, 6.57) * mm, v(75.92, 6.41) * mm]});
            skFitSpline(sketch, "E1699", {"points": [v(75.92, 6.41) * mm, v(75.98, 6.4) * mm, v(76.04, 6.37) * mm, v(76.1, 6.37) * mm]});
            skFitSpline(sketch, "E1700", {"points": [v(76.1, 6.37) * mm, v(76.56, 6.3) * mm, v(77.03, 6.25) * mm, v(77.5, 6.2) * mm]});
            skFitSpline(sketch, "E1701", {"points": [v(77.5, 6.2) * mm, v(77.74, 6.17) * mm, v(77.98, 6.15) * mm, v(78.23, 6.1) * mm]});
            skFitSpline(sketch, "E1702", {"points": [v(78.23, 6.1) * mm, v(78.56, 6.05) * mm, v(78.78, 5.74) * mm, v(78.72, 5.42) * mm]});
            skFitSpline(sketch, "E1703", {"points": [v(78.72, 5.42) * mm, v(78.67, 5.12) * mm, v(78.4, 4.93) * mm, v(78.07, 4.97) * mm]});
            skFitSpline(sketch, "E1704", {"points": [v(78.07, 4.97) * mm, v(77.55, 5.04) * mm, v(77.03, 5.09) * mm, v(76.52, 5.17) * mm]});
            skFitSpline(sketch, "E1705", {"points": [v(76.52, 5.17) * mm, v(76.01, 5.26) * mm, v(75.51, 5.37) * mm, v(75.01, 5.48) * mm]});
            skFitSpline(sketch, "E1706", {"points": [v(75.01, 5.48) * mm, v(74.8, 5.53) * mm, v(74.66, 5.5) * mm, v(74.48, 5.37) * mm]});
            skFitSpline(sketch, "E1707", {"points": [v(74.48, 5.37) * mm, v(74.05, 5.03) * mm, v(73.58, 4.73) * mm, v(73.14, 4.41) * mm]});
            skFitSpline(sketch, "E1708", {"points": [v(73.14, 4.41) * mm, v(72.57, 4) * mm, v(72.03, 3.56) * mm, v(71.45, 3.17) * mm]});
            skFitSpline(sketch, "E1709", {"points": [v(71.45, 3.17) * mm, v(70.24, 2.34) * mm, v(69.01, 1.53) * mm, v(67.8, 0.72) * mm]});
            skFitSpline(sketch, "E1710", {"points": [v(67.8, 0.72) * mm, v(67.75, 0.7) * mm, v(67.72, 0.67) * mm, v(67.66, 0.62) * mm]});
            skFitSpline(sketch, "E1711", {"points": [v(67.66, 0.62) * mm, v(67.71, 0.6) * mm, v(67.74, 0.58) * mm, v(67.77, 0.58) * mm]});
            skFitSpline(sketch, "E1712", {"points": [v(67.77, 0.58) * mm, v(68.39, 0.6) * mm, v(69, 0.52) * mm, v(69.61, 0.6) * mm]});
            skFitSpline(sketch, "E1713", {"points": [v(69.61, 0.6) * mm, v(70, 0.64) * mm, v(70.38, 0.6) * mm, v(70.77, 0.57) * mm]});
            skFitSpline(sketch, "E1714", {"points": [v(70.77, 0.57) * mm, v(70.94, 0.57) * mm, v(71.08, 0.61) * mm, v(71.21, 0.74) * mm]});
            skFitSpline(sketch, "E1715", {"points": [v(71.21, 0.74) * mm, v(71.64, 1.16) * mm, v(72.1, 1.57) * mm, v(72.53, 1.98) * mm]});
            skFitSpline(sketch, "E1716", {"points": [v(72.53, 1.98) * mm, v(72.89, 2.32) * mm, v(73.24, 2.65) * mm, v(73.6, 2.98) * mm]});
            skFitSpline(sketch, "E1717", {"points": [v(73.6, 2.98) * mm, v(73.85, 3.2) * mm, v(74.15, 3.2) * mm, v(74.37, 2.98) * mm]});
            skFitSpline(sketch, "E1718", {"points": [v(74.37, 2.98) * mm, v(74.59, 2.77) * mm, v(74.6, 2.41) * mm, v(74.38, 2.18) * mm]});
            skFitSpline(sketch, "E1719", {"points": [v(74.38, 2.18) * mm, v(74.17, 1.97) * mm, v(73.93, 1.78) * mm, v(73.72, 1.56) * mm]});
            skFitSpline(sketch, "E1720", {"points": [v(73.72, 1.56) * mm, v(73.41, 1.25) * mm, v(73.12, 0.92) * mm, v(72.8, 0.59) * mm]});
            skFitSpline(sketch, "E1721", {"points": [v(72.8, 0.59) * mm, v(73.48, 0.61) * mm, v(74.17, 0.63) * mm, v(74.79, 0.65) * mm]});
            skFitSpline(sketch, "E1722", {"points": [v(74.79, 0.65) * mm, v(74.98, 0.9) * mm, v(75.13, 1.1) * mm, v(75.3, 1.26) * mm]});
            skFitSpline(sketch, "E1723", {"points": [v(75.3, 1.26) * mm, v(75.74, 1.7) * mm, v(76.2, 2.11) * mm, v(76.64, 2.54) * mm]});
            skFitSpline(sketch, "E1724", {"points": [v(76.64, 2.54) * mm, v(76.8, 2.69) * mm, v(76.95, 2.85) * mm, v(77.1, 3) * mm]});
            skFitSpline(sketch, "E1725", {"points": [v(77.1, 3) * mm, v(77.35, 3.29) * mm, v(77.67, 3.33) * mm, v(77.92, 3.1) * mm]});
            skFitSpline(sketch, "E1726", {"points": [v(77.92, 3.1) * mm, v(78.17, 2.89) * mm, v(78.19, 2.51) * mm, v(77.93, 2.25) * mm]});
            skFitSpline(sketch, "E1727", {"points": [v(77.93, 2.25) * mm, v(77.53, 1.85) * mm, v(77.1, 1.47) * mm, v(76.7, 1.07) * mm]});
            skFitSpline(sketch, "E1728", {"points": [v(76.7, 1.07) * mm, v(76.59, 0.96) * mm, v(76.48, 0.85) * mm, v(76.38, 0.74) * mm]});
            skFitSpline(sketch, "E1729", {"points": [v(76.38, 0.74) * mm, v(76.38, 0.73) * mm, v(76.39, 0.72) * mm, v(76.4, 0.71) * mm]});
            skFitSpline(sketch, "E1730", {"points": [v(76.4, 0.71) * mm, v(76.4, 0.7) * mm, v(76.4, 0.7) * mm, v(76.41, 0.7) * mm]});
            skFitSpline(sketch, "E1731", {"points": [v(76.41, 0.7) * mm, v(77.48, 0.7) * mm, v(78.54, 0.7) * mm, v(79.6, 0.7) * mm]});
            skFitSpline(sketch, "E1732", {"points": [v(79.6, 0.7) * mm, v(79.7, 0.8) * mm, v(79.79, 0.9) * mm, v(79.88, 1) * mm]});
            skFitSpline(sketch, "E1733", {"points": [v(79.88, 1) * mm, v(80.04, 1.16) * mm, v(80.22, 1.26) * mm, v(80.45, 1.3) * mm]});
            skFitSpline(sketch, "E1734", {"points": [v(80.45, 1.3) * mm, v(80.6, 1.31) * mm, v(80.74, 1.35) * mm, v(80.89, 1.38) * mm]});
            skFitSpline(sketch, "E1735", {"points": [v(80.89, 1.38) * mm, v(81.45, 1.5) * mm, v(81.87, 1.15) * mm, v(82.08, 0.7) * mm]});
            skFitSpline(sketch, "E1736", {"points": [v(82.08, 0.7) * mm, v(82.28, 0.25) * mm, v(82.28, -0.24) * mm, v(82.08, -0.7) * mm]});
            skFitSpline(sketch, "E1737", {"points": [v(82.08, -0.7) * mm, v(81.9, -1.11) * mm, v(81.44, -1.51) * mm, v(80.9, -1.38) * mm]});
            skFitSpline(sketch, "E1738", {"points": [v(80.9, -1.38) * mm, v(80.8, -1.36) * mm, v(80.72, -1.33) * mm, v(80.62, -1.33) * mm]});
            skFitSpline(sketch, "E1739", {"points": [v(80.62, -1.33) * mm, v(80.22, -1.3) * mm, v(79.92, -1.1) * mm, v(79.68, -0.78) * mm]});
            skFitSpline(sketch, "E1740", {"points": [v(79.68, -0.78) * mm, v(79.64, -0.73) * mm, v(79.56, -0.7) * mm, v(79.5, -0.7) * mm]});
            skFitSpline(sketch, "E1741", {"points": [v(79.5, -0.7) * mm, v(78.57, -0.7) * mm, v(77.64, -0.7) * mm, v(76.71, -0.71) * mm]});
            skFitSpline(sketch, "E1742", {"points": [v(76.71, -0.71) * mm, v(76.6, -0.71) * mm, v(76.5, -0.71) * mm, v(76.33, -0.71) * mm]});
            skFitSpline(sketch, "E1743", {"points": [v(76.33, -0.71) * mm, v(76.49, -0.87) * mm, v(76.6, -0.97) * mm, v(76.7, -1.08) * mm]});
            skFitSpline(sketch, "E1744", {"points": [v(76.7, -1.08) * mm, v(77.1, -1.46) * mm, v(77.52, -1.85) * mm, v(77.92, -2.24) * mm]});
            skFitSpline(sketch, "E1745", {"points": [v(77.92, -2.24) * mm, v(78.06, -2.36) * mm, v(78.12, -2.52) * mm, v(78.11, -2.7) * mm]});
            skFitSpline(sketch, "E1746", {"points": [v(78.11, -2.7) * mm, v(78.1, -2.94) * mm, v(77.98, -3.1) * mm, v(77.77, -3.2) * mm]});
            skFitSpline(sketch, "E1747", {"points": [v(77.77, -3.2) * mm, v(77.56, -3.3) * mm, v(77.35, -3.26) * mm, v(77.18, -3.1) * mm]});
            skFitSpline(sketch, "E1748", {"points": [v(77.18, -3.1) * mm, v(76.48, -2.42) * mm, v(75.79, -1.75) * mm, v(75.1, -1.06) * mm]});
            skFitSpline(sketch, "E1749", {"points": [v(75.1, -1.06) * mm, v(75, -0.96) * mm, v(74.93, -0.82) * mm, v(74.83, -0.66) * mm]});
            skFitSpline(sketch, "E1750", {"points": [v(74.83, -0.66) * mm, v(74.18, -0.64) * mm, v(73.5, -0.6) * mm, v(72.77, -0.58) * mm]});
            skFitSpline(sketch, "E1751", {"points": [v(72.77, -0.58) * mm, v(72.83, -0.66) * mm, v(72.85, -0.71) * mm, v(72.9, -0.75) * mm]});
            skFitSpline(sketch, "E1752", {"points": [v(72.9, -0.75) * mm, v(73.35, -1.2) * mm, v(73.8, -1.63) * mm, v(74.27, -2.07) * mm]});
            skFitSpline(sketch, "E1753", {"points": [v(74.27, -2.07) * mm, v(74.39, -2.18) * mm, v(74.5, -2.3) * mm, v(74.53, -2.48) * mm]});
            skFitSpline(sketch, "E1754", {"points": [v(74.53, -2.48) * mm, v(74.56, -2.73) * mm, v(74.46, -2.95) * mm, v(74.26, -3.06) * mm]});
            skFitSpline(sketch, "E1755", {"points": [v(74.26, -3.06) * mm, v(74.04, -3.19) * mm, v(73.8, -3.16) * mm, v(73.6, -2.98) * mm]});
            skFitSpline(sketch, "E1756", {"points": [v(73.6, -2.98) * mm, v(73.23, -2.63) * mm, v(72.86, -2.29) * mm, v(72.5, -1.94) * mm]});
            skFitSpline(sketch, "E1757", {"points": [v(72.5, -1.94) * mm, v(72.05, -1.53) * mm, v(71.6, -1.12) * mm, v(71.16, -0.7) * mm]});
            skFitSpline(sketch, "E1758", {"points": [v(71.16, -0.7) * mm, v(71.07, -0.6) * mm, v(70.97, -0.58) * mm, v(70.84, -0.58) * mm]});
            skFitSpline(sketch, "E1759", {"points": [v(70.84, -0.58) * mm, v(70.49, -0.6) * mm, v(70.13, -0.6) * mm, v(69.77, -0.6) * mm]});
            skFitSpline(sketch, "E1760", {"points": [v(69.77, -0.6) * mm, v(69.54, -0.6) * mm, v(69.31, -0.55) * mm, v(69.09, -0.55) * mm]});
            skFitSpline(sketch, "E1761", {"points": [v(69.09, -0.55) * mm, v(68.65, -0.55) * mm, v(68.2, -0.57) * mm, v(67.77, -0.59) * mm]});
            skFitSpline(sketch, "E1762", {"points": [v(67.77, -0.59) * mm, v(67.74, -0.59) * mm, v(67.72, -0.6) * mm, v(67.67, -0.62) * mm]});
            skFitSpline(sketch, "E1763", {"points": [v(67.67, -0.62) * mm, v(67.75, -0.68) * mm, v(67.82, -0.73) * mm, v(67.88, -0.77) * mm]});
            skFitSpline(sketch, "E1764", {"points": [v(67.88, -0.77) * mm, v(68.7, -1.33) * mm, v(69.54, -1.9) * mm, v(70.36, -2.46) * mm]});
            skFitSpline(sketch, "E1765", {"points": [v(70.36, -2.46) * mm, v(70.98, -2.87) * mm, v(71.6, -3.27) * mm, v(72.21, -3.7) * mm]});
            skFitSpline(sketch, "E1766", {"points": [v(72.21, -3.7) * mm, v(73, -4.27) * mm, v(73.78, -4.85) * mm, v(74.56, -5.43) * mm]});
            skFitSpline(sketch, "E1767", {"points": [v(74.56, -5.43) * mm, v(74.7, -5.53) * mm, v(74.84, -5.52) * mm, v(74.98, -5.49) * mm]});
            skFitSpline(sketch, "E1768", {"points": [v(74.98, -5.49) * mm, v(75.4, -5.4) * mm, v(75.82, -5.3) * mm, v(76.24, -5.22) * mm]});
            skFitSpline(sketch, "E1769", {"points": [v(76.24, -5.22) * mm, v(76.51, -5.17) * mm, v(76.79, -5.16) * mm, v(77.06, -5.12) * mm]});
            skFitSpline(sketch, "E1770", {"points": [v(77.06, -5.12) * mm, v(77.37, -5.08) * mm, v(77.68, -5.04) * mm, v(77.99, -4.99) * mm]});
            skFitSpline(sketch, "E1771", {"points": [v(77.99, -4.99) * mm, v(78.38, -4.92) * mm, v(78.68, -5.1) * mm, v(78.73, -5.44) * mm]});
            skFitSpline(sketch, "E1772", {"points": [v(78.73, -5.44) * mm, v(78.78, -5.8) * mm, v(78.51, -6.07) * mm, v(78.12, -6.12) * mm]});
            skFitSpline(sketch, "E1773", {"points": [v(78.12, -6.12) * mm, v(77.43, -6.2) * mm, v(76.74, -6.29) * mm, v(76.05, -6.38) * mm]});
            skFitSpline(sketch, "E1774", {"points": [v(76.05, -6.38) * mm, v(76, -6.38) * mm, v(75.96, -6.4) * mm, v(75.87, -6.42) * mm]});
            skFitSpline(sketch, "E1775", {"points": [v(75.87, -6.42) * mm, v(75.98, -6.46) * mm, v(76.04, -6.49) * mm, v(76.1, -6.51) * mm]});
            skFitSpline(sketch, "E1776", {"points": [v(76.1, -6.51) * mm, v(76.97, -6.78) * mm, v(77.84, -7.05) * mm, v(78.7, -7.32) * mm]});
            skFitSpline(sketch, "E1777", {"points": [v(78.7, -7.32) * mm, v(78.8, -7.35) * mm, v(78.9, -7.37) * mm, v(79, -7.38) * mm]});
            skFitSpline(sketch, "E1778", {"points": [v(79, -7.38) * mm, v(79.3, -7.43) * mm, v(79.52, -7.58) * mm, v(79.66, -7.86) * mm]});
            skFitSpline(sketch, "E1779", {"points": [v(79.66, -7.86) * mm, v(79.96, -8.48) * mm, v(80.28, -9.09) * mm, v(80.6, -9.7) * mm]});
            skFitSpline(sketch, "E1780", {"points": [v(80.6, -9.7) * mm, v(80.68, -9.85) * mm, v(80.8, -9.99) * mm, v(80.9, -10.13) * mm]});
            skFitSpline(sketch, "E1781", {"points": [v(80.9, -10.13) * mm, v(81.09, -10.43) * mm, v(81.09, -10.66) * mm, v(80.88, -10.95) * mm]});
            skFitSpline(sketch, "E1782", {"points": [v(80.88, -10.95) * mm, v(80.68, -11.23) * mm, v(80.47, -11.3) * mm, v(80.12, -11.2) * mm]});
            skFitSpline(sketch, "E1783", {"points": [v(80.12, -11.2) * mm, v(79.65, -11.1) * mm, v(79.19, -11) * mm, v(78.72, -10.92) * mm]});
            skFitSpline(sketch, "E1784", {"points": [v(78.72, -10.92) * mm, v(78.33, -10.84) * mm, v(77.94, -10.78) * mm, v(77.55, -10.73) * mm]});
            skFitSpline(sketch, "E1785", {"points": [v(77.55, -10.73) * mm, v(77.27, -10.7) * mm, v(77.1, -10.54) * mm, v(76.94, -10.32) * mm]});
            skFitSpline(sketch, "E1786", {"points": [v(76.94, -10.32) * mm, v(76.34, -9.44) * mm, v(75.73, -8.56) * mm, v(75.13, -7.69) * mm]});
            skFitSpline(sketch, "E1787", {"points": [v(75.13, -7.69) * mm, v(75.11, -7.67) * mm, v(75.09, -7.66) * mm, v(75.02, -7.6) * mm]});
            skFitSpline(sketch, "E1788", {"points": [v(75.02, -7.6) * mm, v(75.05, -7.77) * mm, v(75.06, -7.89) * mm, v(75.08, -8) * mm]});
            skFitSpline(sketch, "E1789", {"points": [v(75.08, -8) * mm, v(75.15, -8.35) * mm, v(75.23, -8.7) * mm, v(75.3, -9.05) * mm]});
            skFitSpline(sketch, "E1790", {"points": [v(75.3, -9.05) * mm, v(75.35, -9.36) * mm, v(75.42, -9.66) * mm, v(75.46, -9.97) * mm]});
            skFitSpline(sketch, "E1791", {"points": [v(75.46, -9.97) * mm, v(75.5, -10.26) * mm, v(75.28, -10.54) * mm, v(75, -10.6) * mm]});
            skFitSpline(sketch, "E1792", {"points": [v(75, -10.6) * mm, v(74.69, -10.65) * mm, v(74.42, -10.48) * mm, v(74.34, -10.18) * mm]});
            skFitSpline(sketch, "E1793", {"points": [v(74.34, -10.18) * mm, v(74.31, -10.05) * mm, v(74.31, -9.92) * mm, v(74.29, -9.8) * mm]});
            skFitSpline(sketch, "E1794", {"points": [v(74.29, -9.8) * mm, v(74.18, -9.23) * mm, v(74.06, -8.66) * mm, v(73.97, -8.1) * mm]});
            skFitSpline(sketch, "E1795", {"points": [v(73.97, -8.1) * mm, v(73.92, -7.84) * mm, v(73.91, -7.59) * mm, v(73.89, -7.33) * mm]});
            skFitSpline(sketch, "E1796", {"points": [v(73.89, -7.33) * mm, v(73.87, -7.17) * mm, v(73.86, -7) * mm, v(73.83, -6.84) * mm]});
            skFitSpline(sketch, "E1797", {"points": [v(73.83, -6.84) * mm, v(73.81, -6.78) * mm, v(73.77, -6.7) * mm, v(73.71, -6.67) * mm]});
            skFitSpline(sketch, "E1798", {"points": [v(73.71, -6.67) * mm, v(73.29, -6.35) * mm, v(72.86, -6.03) * mm, v(72.43, -5.72) * mm]});
            skFitSpline(sketch, "E1799", {"points": [v(72.43, -5.72) * mm, v(71.83, -5.29) * mm, v(71.22, -4.89) * mm, v(70.64, -4.44) * mm]});
            skFitSpline(sketch, "E1800", {"points": [v(70.64, -4.44) * mm, v(69.47, -3.54) * mm, v(68.31, -2.61) * mm, v(67.15, -1.7) * mm]});
            skFitSpline(sketch, "E1801", {"points": [v(67.15, -1.7) * mm, v(67.11, -1.66) * mm, v(67.07, -1.63) * mm, v(66.98, -1.56) * mm]});
            skFitSpline(sketch, "E1802", {"points": [v(66.98, -1.56) * mm, v(67, -1.68) * mm, v(67.01, -1.75) * mm, v(67.03, -1.8) * mm]});
            skFitSpline(sketch, "E1803", {"points": [v(67.03, -1.8) * mm, v(67.32, -2.74) * mm, v(67.62, -3.66) * mm, v(67.9, -4.59) * mm]});
            skFitSpline(sketch, "E1804", {"points": [v(67.9, -4.59) * mm, v(67.95, -4.72) * mm, v(68.02, -4.8) * mm, v(68.14, -4.88) * mm]});
            skFitSpline(sketch, "E1805", {"points": [v(68.14, -4.88) * mm, v(68.68, -5.17) * mm, v(69.22, -5.47) * mm, v(69.75, -5.77) * mm]});
            skFitSpline(sketch, "E1806", {"points": [v(69.75, -5.77) * mm, v(70.16, -6) * mm, v(70.57, -6.23) * mm, v(70.98, -6.44) * mm]});
            skFitSpline(sketch, "E1807", {"points": [v(70.98, -6.44) * mm, v(71.36, -6.63) * mm, v(71.42, -7) * mm, v(71.28, -7.24) * mm]});
            skFitSpline(sketch, "E1808", {"points": [v(71.28, -7.24) * mm, v(71.1, -7.54) * mm, v(70.76, -7.6) * mm, v(70.4, -7.41) * mm]});
            skFitSpline(sketch, "E1809", {"points": [v(70.4, -7.41) * mm, v(69.86, -7.11) * mm, v(69.31, -6.82) * mm, v(68.76, -6.52) * mm]});
            skFitSpline(sketch, "E1810", {"points": [v(68.76, -6.52) * mm, v(68.7, -6.49) * mm, v(68.63, -6.47) * mm, v(68.52, -6.41) * mm]});
            skFitSpline(sketch, "E1811", {"points": [v(68.52, -6.41) * mm, v(68.77, -7.1) * mm, v(69, -7.76) * mm, v(69.22, -8.33) * mm]});
            skFitSpline(sketch, "E1812", {"points": [v(69.22, -8.33) * mm, v(69.49, -8.44) * mm, v(69.7, -8.5) * mm, v(69.9, -8.6) * mm]});
            skFitSpline(sketch, "E1813", {"points": [v(69.9, -8.6) * mm, v(70.43, -8.88) * mm, v(70.96, -9.18) * mm, v(71.49, -9.46) * mm]});
            skFitSpline(sketch, "E1814", {"points": [v(71.49, -9.46) * mm, v(71.72, -9.59) * mm, v(71.97, -9.7) * mm, v(72.2, -9.82) * mm]});
            skFitSpline(sketch, "E1815", {"points": [v(72.2, -9.82) * mm, v(72.43, -9.93) * mm, v(72.56, -10.1) * mm, v(72.56, -10.36) * mm]});
            skFitSpline(sketch, "E1816", {"points": [v(72.56, -10.36) * mm, v(72.55, -10.6) * mm, v(72.38, -10.8) * mm, v(72.13, -10.88) * mm]});
            skFitSpline(sketch, "E1817", {"points": [v(72.13, -10.88) * mm, v(71.98, -10.93) * mm, v(71.84, -10.9) * mm, v(71.71, -10.84) * mm]});
            skFitSpline(sketch, "E1818", {"points": [v(71.71, -10.84) * mm, v(71.3, -10.62) * mm, v(70.88, -10.4) * mm, v(70.47, -10.17) * mm]});
            skFitSpline(sketch, "E1819", {"points": [v(70.47, -10.17) * mm, v(70.25, -10.05) * mm, v(70.03, -9.93) * mm, v(69.76, -9.78) * mm]});
            skFitSpline(sketch, "E1820", {"points": [v(69.76, -9.78) * mm, v(69.82, -10.02) * mm, v(69.86, -10.2) * mm, v(69.92, -10.38) * mm]});
            skFitSpline(sketch, "E1821", {"points": [v(69.92, -10.38) * mm, v(70.17, -11.18) * mm, v(70.43, -11.97) * mm, v(70.68, -12.77) * mm]});
            skFitSpline(sketch, "E1822", {"points": [v(70.68, -12.77) * mm, v(70.71, -12.88) * mm, v(70.77, -12.93) * mm, v(70.88, -12.96) * mm]});
            skFitSpline(sketch, "E1823", {"points": [v(70.88, -12.96) * mm, v(71.2, -13.07) * mm, v(71.45, -13.25) * mm, v(71.6, -13.57) * mm]});
            skFitSpline(sketch, "E1824", {"points": [v(71.6, -13.57) * mm, v(71.64, -13.68) * mm, v(71.7, -13.78) * mm, v(71.77, -13.88) * mm]});
            skFitSpline(sketch, "E1825", {"points": [v(71.77, -13.88) * mm, v(72.07, -14.35) * mm, v(71.86, -14.95) * mm, v(71.49, -15.27) * mm]});
            skFitSpline(sketch, "E1826", {"points": [v(71.49, -15.27) * mm, v(71.14, -15.56) * mm, v(70.74, -15.72) * mm, v(70.27, -15.69) * mm]});
            skFitSpline(sketch, "E1827", {"points": [v(70.27, -15.69) * mm, v(69.87, -15.66) * mm, v(69.54, -15.51) * mm, v(69.3, -15.18) * mm]});
            skFitSpline(sketch, "E1828", {"points": [v(69.3, -15.18) * mm, v(69.25, -15.1) * mm, v(69.2, -14.98) * mm, v(69.19, -14.88) * mm]});
            skFitSpline(sketch, "E1829", {"points": [v(69.19, -14.88) * mm, v(69.14, -14.65) * mm, v(69.11, -14.4) * mm, v(69.1, -14.17) * mm]});
            skFitSpline(sketch, "E1830", {"points": [v(69.1, -14.17) * mm, v(69.07, -13.91) * mm, v(69.2, -13.69) * mm, v(69.33, -13.48) * mm]});
            skFitSpline(sketch, "E1831", {"points": [v(69.33, -13.48) * mm, v(69.4, -13.37) * mm, v(69.41, -13.28) * mm, v(69.37, -13.16) * mm]});
            skFitSpline(sketch, "E1832", {"points": [v(69.37, -13.16) * mm, v(69.12, -12.43) * mm, v(68.89, -11.7) * mm, v(68.64, -10.96) * mm]});
            skFitSpline(sketch, "E1833", {"points": [v(68.64, -10.96) * mm, v(68.57, -10.74) * mm, v(68.48, -10.51) * mm, v(68.38, -10.22) * mm]});
            skFitSpline(sketch, "E1834", {"points": [v(-21.97, 2.88) * mm, v(-21.94, 3.07) * mm, v(-21.9, 3.25) * mm, v(-21.87, 3.46) * mm]});
            skFitSpline(sketch, "E1835", {"points": [v(-21.87, 3.46) * mm, v(-22.07, 3.42) * mm, v(-22.26, 3.38) * mm, v(-22.45, 3.35) * mm]});
            skFitSpline(sketch, "E1836", {"points": [v(-22.45, 3.35) * mm, v(-22.4, 3.07) * mm, v(-22.25, 2.9) * mm, v(-21.97, 2.88) * mm]});
            skFitSpline(sketch, "E1837", {"points": [v(-24.05, -4.72) * mm, v(-23.98, -4.5) * mm, v(-23.92, -4.33) * mm, v(-23.86, -4.16) * mm]});
            skFitSpline(sketch, "E1838", {"points": [v(-23.86, -4.16) * mm, v(-24.14, -4.06) * mm, v(-24.34, -4.12) * mm, v(-24.5, -4.33) * mm]});
            skFitSpline(sketch, "E1839", {"points": [v(-24.5, -4.33) * mm, v(-24.36, -4.46) * mm, v(-24.21, -4.58) * mm, v(-24.05, -4.72) * mm]});
            skFitSpline(sketch, "E1840", {"points": [v(-21.98, -2.87) * mm, v(-22.26, -2.92) * mm, v(-22.4, -3.08) * mm, v(-22.45, -3.35) * mm]});
            skFitSpline(sketch, "E1841", {"points": [v(-22.45, -3.35) * mm, v(-22.26, -3.38) * mm, v(-22.07, -3.42) * mm, v(-21.87, -3.45) * mm]});
            skFitSpline(sketch, "E1842", {"points": [v(-21.87, -3.45) * mm, v(-21.9, -3.25) * mm, v(-21.94, -3.06) * mm, v(-21.98, -2.87) * mm]});
            skFitSpline(sketch, "E1843", {"points": [v(-23.85, 4.15) * mm, v(-23.92, 4.34) * mm, v(-23.99, 4.53) * mm, v(-24.06, 4.72) * mm]});
            skFitSpline(sketch, "E1844", {"points": [v(-24.06, 4.72) * mm, v(-24.22, 4.58) * mm, v(-24.36, 4.46) * mm, v(-24.5, 4.34) * mm]});
            skFitSpline(sketch, "E1845", {"points": [v(-24.5, 4.34) * mm, v(-24.25, 4.08) * mm, v(-24.25, 4.08) * mm, v(-23.85, 4.15) * mm]});
            skFitSpline(sketch, "E1846", {"points": [v(-29.65, 0.81) * mm, v(-29.44, 0.99) * mm, v(-29.38, 1.2) * mm, v(-29.47, 1.46) * mm]});
            skFitSpline(sketch, "E1847", {"points": [v(-29.47, 1.46) * mm, v(-29.66, 1.4) * mm, v(-29.84, 1.34) * mm, v(-30.04, 1.27) * mm]});
            skFitSpline(sketch, "E1848", {"points": [v(-30.04, 1.27) * mm, v(-29.9, 1.11) * mm, v(-29.78, 0.96) * mm, v(-29.65, 0.81) * mm]});
            skFitSpline(sketch, "E1849", {"points": [v(-26.13, -4.33) * mm, v(-26.3, -4.1) * mm, v(-26.52, -4.07) * mm, v(-26.79, -4.15) * mm]});
            skFitSpline(sketch, "E1850", {"points": [v(-26.79, -4.15) * mm, v(-26.72, -4.34) * mm, v(-26.65, -4.52) * mm, v(-26.58, -4.72) * mm]});
            skFitSpline(sketch, "E1851", {"points": [v(-26.58, -4.72) * mm, v(-26.42, -4.58) * mm, v(-26.28, -4.46) * mm, v(-26.13, -4.33) * mm]});
            skFitSpline(sketch, "E1852", {"points": [v(-29.65, -0.81) * mm, v(-29.78, -0.96) * mm, v(-29.91, -1.11) * mm, v(-30.04, -1.27) * mm]});
            skFitSpline(sketch, "E1853", {"points": [v(-30.04, -1.27) * mm, v(-29.83, -1.34) * mm, v(-29.65, -1.4) * mm, v(-29.47, -1.46) * mm]});
            skFitSpline(sketch, "E1854", {"points": [v(-29.47, -1.46) * mm, v(-29.38, -1.2) * mm, v(-29.44, -0.99) * mm, v(-29.65, -0.81) * mm]});
            skFitSpline(sketch, "E1855", {"points": [v(-28.78, 3.45) * mm, v(-28.74, 3.25) * mm, v(-28.7, 3.06) * mm, v(-28.67, 2.87) * mm]});
            skFitSpline(sketch, "E1856", {"points": [v(-28.67, 2.87) * mm, v(-28.38, 2.92) * mm, v(-28.23, 3.07) * mm, v(-28.2, 3.35) * mm]});
            skFitSpline(sketch, "E1857", {"points": [v(-28.2, 3.35) * mm, v(-28.39, 3.38) * mm, v(-28.57, 3.42) * mm, v(-28.78, 3.45) * mm]});
            skFitSpline(sketch, "E1858", {"points": [v(-28.19, -3.35) * mm, v(-28.24, -3.07) * mm, v(-28.38, -2.91) * mm, v(-28.67, -2.87) * mm]});
            skFitSpline(sketch, "E1859", {"points": [v(-28.67, -2.87) * mm, v(-28.7, -3.07) * mm, v(-28.74, -3.26) * mm, v(-28.77, -3.45) * mm]});
            skFitSpline(sketch, "E1860", {"points": [v(-28.77, -3.45) * mm, v(-28.56, -3.42) * mm, v(-28.38, -3.39) * mm, v(-28.19, -3.35) * mm]});
            skFitSpline(sketch, "E1861", {"points": [v(-20.99, 0.81) * mm, v(-20.86, 0.96) * mm, v(-20.73, 1.12) * mm, v(-20.6, 1.27) * mm]});
            skFitSpline(sketch, "E1862", {"points": [v(-20.6, 1.27) * mm, v(-20.8, 1.34) * mm, v(-20.98, 1.4) * mm, v(-21.16, 1.46) * mm]});
            skFitSpline(sketch, "E1863", {"points": [v(-21.16, 1.46) * mm, v(-21.28, 1.2) * mm, v(-21.2, 1) * mm, v(-20.99, 0.81) * mm]});
            skFitSpline(sketch, "E1864", {"points": [v(-20.6, -1.27) * mm, v(-20.73, -1.1) * mm, v(-20.86, -0.96) * mm, v(-20.99, -0.81) * mm]});
            skFitSpline(sketch, "E1865", {"points": [v(-20.99, -0.81) * mm, v(-21.2, -1) * mm, v(-21.28, -1.2) * mm, v(-21.16, -1.46) * mm]});
            skFitSpline(sketch, "E1866", {"points": [v(-21.16, -1.46) * mm, v(-20.98, -1.4) * mm, v(-20.8, -1.34) * mm, v(-20.6, -1.27) * mm]});
            skFitSpline(sketch, "E1867", {"points": [v(-26.13, 4.34) * mm, v(-26.29, 4.47) * mm, v(-26.43, 4.6) * mm, v(-26.59, 4.72) * mm]});
            skFitSpline(sketch, "E1868", {"points": [v(-26.59, 4.72) * mm, v(-26.66, 4.53) * mm, v(-26.72, 4.34) * mm, v(-26.79, 4.15) * mm]});
            skFitSpline(sketch, "E1869", {"points": [v(-26.79, 4.15) * mm, v(-26.53, 4.05) * mm, v(-26.32, 4.11) * mm, v(-26.13, 4.34) * mm]});
            skFitSpline(sketch, "E1870", {"points": [v(-26.2, -5.73) * mm, v(-25.9, -6.74) * mm, v(-25.61, -7.7) * mm, v(-25.31, -8.7) * mm]});
            skFitSpline(sketch, "E1871", {"points": [v(-25.31, -8.7) * mm, v(-25.28, -8.59) * mm, v(-25.25, -8.5) * mm, v(-25.22, -8.4) * mm]});
            skFitSpline(sketch, "E1872", {"points": [v(-25.22, -8.4) * mm, v(-25.06, -7.82) * mm, v(-24.9, -7.23) * mm, v(-24.72, -6.64) * mm]});
            skFitSpline(sketch, "E1873", {"points": [v(-24.72, -6.64) * mm, v(-24.65, -6.4) * mm, v(-24.55, -6.15) * mm, v(-24.47, -5.9) * mm]});
            skFitSpline(sketch, "E1874", {"points": [v(-24.47, -5.9) * mm, v(-24.45, -5.84) * mm, v(-24.46, -5.74) * mm, v(-24.5, -5.7) * mm]});
            skFitSpline(sketch, "E1875", {"points": [v(-24.5, -5.7) * mm, v(-24.74, -5.42) * mm, v(-25, -5.16) * mm, v(-25.35, -4.94) * mm]});
            skFitSpline(sketch, "E1876", {"points": [v(-25.35, -4.94) * mm, v(-25.64, -5.21) * mm, v(-25.93, -5.48) * mm, v(-26.2, -5.73) * mm]});
            skFitSpline(sketch, "E1877", {"points": [v(-20.4, 0) * mm, v(-20.14, -0.29) * mm, v(-19.9, -0.53) * mm, v(-19.67, -0.79) * mm]});
            skFitSpline(sketch, "E1878", {"points": [v(-19.67, -0.79) * mm, v(-19.6, -0.88) * mm, v(-19.5, -0.89) * mm, v(-19.4, -0.85) * mm]});
            skFitSpline(sketch, "E1879", {"points": [v(-19.4, -0.85) * mm, v(-19.23, -0.78) * mm, v(-19.05, -0.71) * mm, v(-18.88, -0.66) * mm]});
            skFitSpline(sketch, "E1880", {"points": [v(-18.88, -0.66) * mm, v(-18.2, -0.46) * mm, v(-17.51, -0.27) * mm, v(-16.83, -0.08) * mm]});
            skFitSpline(sketch, "E1881", {"points": [v(-16.83, -0.08) * mm, v(-16.78, -0.06) * mm, v(-16.72, -0.04) * mm, v(-16.67, -0.02) * mm]});
            skFitSpline(sketch, "E1882", {"points": [v(-16.67, -0.02) * mm, v(-16.75, 0.05) * mm, v(-16.83, 0.07) * mm, v(-16.9, 0.1) * mm]});
            skFitSpline(sketch, "E1883", {"points": [v(-16.9, 0.1) * mm, v(-17.5, 0.26) * mm, v(-18.08, 0.42) * mm, v(-18.66, 0.6) * mm]});
            skFitSpline(sketch, "E1884", {"points": [v(-18.66, 0.6) * mm, v(-18.9, 0.67) * mm, v(-19.16, 0.76) * mm, v(-19.4, 0.85) * mm]});
            skFitSpline(sketch, "E1885", {"points": [v(-19.4, 0.85) * mm, v(-19.5, 0.88) * mm, v(-19.58, 0.88) * mm, v(-19.66, 0.8) * mm]});
            skFitSpline(sketch, "E1886", {"points": [v(-19.66, 0.8) * mm, v(-19.9, 0.54) * mm, v(-20.14, 0.29) * mm, v(-20.4, 0) * mm]});
            skFitSpline(sketch, "E1887", {"points": [v(-22.84, -4.3) * mm, v(-23.02, -4.64) * mm, v(-23.1, -4.98) * mm, v(-23.19, -5.33) * mm]});
            skFitSpline(sketch, "E1888", {"points": [v(-23.19, -5.33) * mm, v(-23.2, -5.41) * mm, v(-23.19, -5.47) * mm, v(-23.12, -5.52) * mm]});
            skFitSpline(sketch, "E1889", {"points": [v(-23.12, -5.52) * mm, v(-22.96, -5.66) * mm, v(-22.8, -5.8) * mm, v(-22.64, -5.94) * mm]});
            skFitSpline(sketch, "E1890", {"points": [v(-22.64, -5.94) * mm, v(-22.13, -6.43) * mm, v(-21.63, -6.92) * mm, v(-21.12, -7.4) * mm]});
            skFitSpline(sketch, "E1891", {"points": [v(-21.12, -7.4) * mm, v(-21.09, -7.44) * mm, v(-21.04, -7.47) * mm, v(-20.97, -7.53) * mm]});
            skFitSpline(sketch, "E1892", {"points": [v(-20.97, -7.53) * mm, v(-20.99, -7.43) * mm, v(-21, -7.38) * mm, v(-21, -7.32) * mm]});
            skFitSpline(sketch, "E1893", {"points": [v(-21, -7.32) * mm, v(-21.09, -7) * mm, v(-21.17, -6.7) * mm, v(-21.25, -6.38) * mm]});
            skFitSpline(sketch, "E1894", {"points": [v(-21.25, -6.38) * mm, v(-21.34, -6.03) * mm, v(-21.43, -5.68) * mm, v(-21.5, -5.33) * mm]});
            skFitSpline(sketch, "E1895", {"points": [v(-21.5, -5.33) * mm, v(-21.56, -5.12) * mm, v(-21.6, -4.9) * mm, v(-21.64, -4.68) * mm]});
            skFitSpline(sketch, "E1896", {"points": [v(-21.64, -4.68) * mm, v(-21.65, -4.6) * mm, v(-21.67, -4.54) * mm, v(-21.75, -4.52) * mm]});
            skFitSpline(sketch, "E1897", {"points": [v(-21.75, -4.52) * mm, v(-22.1, -4.42) * mm, v(-22.45, -4.3) * mm, v(-22.84, -4.3) * mm]});
            skFitSpline(sketch, "E1898", {"points": [v(-20.98, 7.52) * mm, v(-21.07, 7.44) * mm, v(-21.12, 7.4) * mm, v(-21.17, 7.35) * mm]});
            skFitSpline(sketch, "E1899", {"points": [v(-21.17, 7.35) * mm, v(-21.63, 6.92) * mm, v(-22.08, 6.47) * mm, v(-22.53, 6.04) * mm]});
            skFitSpline(sketch, "E1900", {"points": [v(-22.53, 6.04) * mm, v(-22.72, 5.86) * mm, v(-22.92, 5.7) * mm, v(-23.1, 5.53) * mm]});
            skFitSpline(sketch, "E1901", {"points": [v(-23.1, 5.53) * mm, v(-23.16, 5.49) * mm, v(-23.21, 5.44) * mm, v(-23.2, 5.35) * mm]});
            skFitSpline(sketch, "E1902", {"points": [v(-23.2, 5.35) * mm, v(-23.1, 5) * mm, v(-23.02, 4.63) * mm, v(-22.84, 4.3) * mm]});
            skFitSpline(sketch, "E1903", {"points": [v(-22.84, 4.3) * mm, v(-22.43, 4.31) * mm, v(-22.05, 4.43) * mm, v(-21.69, 4.54) * mm]});
            skFitSpline(sketch, "E1904", {"points": [v(-21.69, 4.54) * mm, v(-21.45, 5.53) * mm, v(-21.22, 6.5) * mm, v(-20.98, 7.52) * mm]});
            skFitSpline(sketch, "E1905", {"points": [v(-33.96, 0.03) * mm, v(-33.96, 0) * mm, v(-33.96, 0) * mm, v(-33.96, -0.02) * mm]});
            skFitSpline(sketch, "E1906", {"points": [v(-33.96, -0.02) * mm, v(-33.89, -0.05) * mm, v(-33.82, -0.07) * mm, v(-33.74, -0.1) * mm]});
            skFitSpline(sketch, "E1907", {"points": [v(-33.74, -0.1) * mm, v(-33.15, -0.26) * mm, v(-32.56, -0.42) * mm, v(-31.97, -0.6) * mm]});
            skFitSpline(sketch, "E1908", {"points": [v(-31.97, -0.6) * mm, v(-31.72, -0.67) * mm, v(-31.48, -0.76) * mm, v(-31.23, -0.85) * mm]});
            skFitSpline(sketch, "E1909", {"points": [v(-31.23, -0.85) * mm, v(-31.15, -0.87) * mm, v(-31.08, -0.9) * mm, v(-31, -0.82) * mm]});
            skFitSpline(sketch, "E1910", {"points": [v(-31, -0.82) * mm, v(-30.74, -0.57) * mm, v(-30.48, -0.32) * mm, v(-30.27, 0) * mm]});
            skFitSpline(sketch, "E1911", {"points": [v(-30.27, 0) * mm, v(-30.37, 0.13) * mm, v(-30.45, 0.25) * mm, v(-30.55, 0.36) * mm]});
            skFitSpline(sketch, "E1912", {"points": [v(-30.55, 0.36) * mm, v(-30.68, 0.5) * mm, v(-30.81, 0.62) * mm, v(-30.94, 0.76) * mm]});
            skFitSpline(sketch, "E1913", {"points": [v(-30.94, 0.76) * mm, v(-31.03, 0.87) * mm, v(-31.13, 0.88) * mm, v(-31.27, 0.84) * mm]});
            skFitSpline(sketch, "E1914", {"points": [v(-31.27, 0.84) * mm, v(-31.92, 0.63) * mm, v(-32.58, 0.43) * mm, v(-33.23, 0.23) * mm]});
            skFitSpline(sketch, "E1915", {"points": [v(-33.23, 0.23) * mm, v(-33.47, 0.15) * mm, v(-33.72, 0.1) * mm, v(-33.96, 0.03) * mm]});
            skFitSpline(sketch, "E1916", {"points": [v(-32.83, 4.34) * mm, v(-32.13, 3.6) * mm, v(-31.44, 2.86) * mm, v(-30.72, 2.1) * mm]});
            skFitSpline(sketch, "E1917", {"points": [v(-30.72, 2.1) * mm, v(-30.36, 2.21) * mm, v(-30, 2.33) * mm, v(-29.64, 2.44) * mm]});
            skFitSpline(sketch, "E1918", {"points": [v(-29.64, 2.44) * mm, v(-29.6, 2.75) * mm, v(-29.75, 3.37) * mm, v(-29.88, 3.64) * mm]});
            skFitSpline(sketch, "E1919", {"points": [v(-29.88, 3.64) * mm, v(-30.87, 3.87) * mm, v(-31.84, 4.1) * mm, v(-32.83, 4.34) * mm]});
            skFitSpline(sketch, "E1920", {"points": [v(-25.31, 8.7) * mm, v(-25.61, 7.7) * mm, v(-25.9, 6.73) * mm, v(-26.2, 5.73) * mm]});
            skFitSpline(sketch, "E1921", {"points": [v(-26.2, 5.73) * mm, v(-25.93, 5.47) * mm, v(-25.63, 5.2) * mm, v(-25.34, 4.93) * mm]});
            skFitSpline(sketch, "E1922", {"points": [v(-25.34, 4.93) * mm, v(-25.17, 5.07) * mm, v(-25.02, 5.17) * mm, v(-24.89, 5.3) * mm]});
            skFitSpline(sketch, "E1923", {"points": [v(-24.89, 5.3) * mm, v(-24.75, 5.42) * mm, v(-24.63, 5.56) * mm, v(-24.5, 5.69) * mm]});
            skFitSpline(sketch, "E1924", {"points": [v(-24.5, 5.69) * mm, v(-24.44, 5.75) * mm, v(-24.43, 5.8) * mm, v(-24.46, 5.88) * mm]});
            skFitSpline(sketch, "E1925", {"points": [v(-24.46, 5.88) * mm, v(-24.53, 6.07) * mm, v(-24.6, 6.25) * mm, v(-24.66, 6.45) * mm]});
            skFitSpline(sketch, "E1926", {"points": [v(-24.66, 6.45) * mm, v(-24.86, 7.12) * mm, v(-25.05, 7.8) * mm, v(-25.24, 8.47) * mm]});
            skFitSpline(sketch, "E1927", {"points": [v(-25.24, 8.47) * mm, v(-25.26, 8.53) * mm, v(-25.28, 8.6) * mm, v(-25.31, 8.7) * mm]});
            skFitSpline(sketch, "E1928", {"points": [v(-28.96, -4.54) * mm, v(-29.2, -5.55) * mm, v(-29.42, -6.53) * mm, v(-29.66, -7.5) * mm]});
            skFitSpline(sketch, "E1929", {"points": [v(-29.66, -7.5) * mm, v(-28.92, -6.81) * mm, v(-28.18, -6.12) * mm, v(-27.44, -5.42) * mm]});
            skFitSpline(sketch, "E1930", {"points": [v(-27.44, -5.42) * mm, v(-27.52, -5.05) * mm, v(-27.6, -4.66) * mm, v(-27.8, -4.3) * mm]});
            skFitSpline(sketch, "E1931", {"points": [v(-27.8, -4.3) * mm, v(-28.2, -4.3) * mm, v(-28.59, -4.42) * mm, v(-28.96, -4.54) * mm]});
            skFitSpline(sketch, "E1932", {"points": [v(-21.03, -2.45) * mm, v(-21.01, -2.86) * mm, v(-20.9, -3.2) * mm, v(-20.8, -3.55) * mm]});
            skFitSpline(sketch, "E1933", {"points": [v(-20.8, -3.55) * mm, v(-20.78, -3.66) * mm, v(-20.7, -3.67) * mm, v(-20.62, -3.7) * mm]});
            skFitSpline(sketch, "E1934", {"points": [v(-20.62, -3.7) * mm, v(-20, -3.83) * mm, v(-19.37, -3.97) * mm, v(-18.75, -4.12) * mm]});
            skFitSpline(sketch, "E1935", {"points": [v(-18.75, -4.12) * mm, v(-18.44, -4.2) * mm, v(-18.12, -4.27) * mm, v(-17.8, -4.35) * mm]});
            skFitSpline(sketch, "E1936", {"points": [v(-17.8, -4.35) * mm, v(-18.5, -3.6) * mm, v(-19.2, -2.87) * mm, v(-19.92, -2.1) * mm]});
            skFitSpline(sketch, "E1937", {"points": [v(-19.92, -2.1) * mm, v(-20.27, -2.21) * mm, v(-20.65, -2.33) * mm, v(-21.03, -2.45) * mm]});
            skFitSpline(sketch, "E1938", {"points": [v(-27.44, 5.42) * mm, v(-28.19, 6.13) * mm, v(-28.92, 6.82) * mm, v(-29.66, 7.51) * mm]});
            skFitSpline(sketch, "E1939", {"points": [v(-29.66, 7.51) * mm, v(-29.42, 6.52) * mm, v(-29.2, 5.54) * mm, v(-28.96, 4.54) * mm]});
            skFitSpline(sketch, "E1940", {"points": [v(-28.96, 4.54) * mm, v(-28.59, 4.43) * mm, v(-28.2, 4.3) * mm, v(-27.8, 4.3) * mm]});
            skFitSpline(sketch, "E1941", {"points": [v(-27.8, 4.3) * mm, v(-27.61, 4.65) * mm, v(-27.52, 5.04) * mm, v(-27.44, 5.42) * mm]});
            skFitSpline(sketch, "E1942", {"points": [v(-30.72, -2.1) * mm, v(-31.45, -2.87) * mm, v(-32.13, -3.6) * mm, v(-32.84, -4.35) * mm]});
            skFitSpline(sketch, "E1943", {"points": [v(-32.84, -4.35) * mm, v(-32.39, -4.24) * mm, v(-31.97, -4.13) * mm, v(-31.56, -4.03) * mm]});
            skFitSpline(sketch, "E1944", {"points": [v(-31.56, -4.03) * mm, v(-31.04, -3.91) * mm, v(-30.53, -3.8) * mm, v(-30.02, -3.7) * mm]});
            skFitSpline(sketch, "E1945", {"points": [v(-30.02, -3.7) * mm, v(-29.9, -3.67) * mm, v(-29.85, -3.62) * mm, v(-29.82, -3.52) * mm]});
            skFitSpline(sketch, "E1946", {"points": [v(-29.82, -3.52) * mm, v(-29.78, -3.36) * mm, v(-29.72, -3.21) * mm, v(-29.7, -3.06) * mm]});
            skFitSpline(sketch, "E1947", {"points": [v(-29.7, -3.06) * mm, v(-29.66, -2.86) * mm, v(-29.64, -2.67) * mm, v(-29.6, -2.45) * mm]});
            skFitSpline(sketch, "E1948", {"points": [v(-29.6, -2.45) * mm, v(-30, -2.32) * mm, v(-30.37, -2.21) * mm, v(-30.72, -2.1) * mm]});
            skFitSpline(sketch, "E1949", {"points": [v(-19.9, 2.12) * mm, v(-19.19, 2.87) * mm, v(-18.5, 3.6) * mm, v(-17.8, 4.34) * mm]});
            skFitSpline(sketch, "E1950", {"points": [v(-17.8, 4.34) * mm, v(-18.8, 4.1) * mm, v(-19.78, 3.87) * mm, v(-20.78, 3.63) * mm]});
            skFitSpline(sketch, "E1951", {"points": [v(-20.78, 3.63) * mm, v(-20.9, 3.26) * mm, v(-21.02, 2.89) * mm, v(-21.03, 2.48) * mm]});
            skFitSpline(sketch, "E1952", {"points": [v(-21.03, 2.48) * mm, v(-20.66, 2.3) * mm, v(-20.28, 2.2) * mm, v(-19.9, 2.12) * mm]});
            skFitSpline(sketch, "E1953", {"points": [v(-30, -4.68) * mm, v(-31.19, -4.9) * mm, v(-32.3, -5.24) * mm, v(-33.46, -5.53) * mm]});
            skFitSpline(sketch, "E1954", {"points": [v(-33.46, -5.53) * mm, v(-33.36, -5.58) * mm, v(-33.3, -5.62) * mm, v(-33.22, -5.66) * mm]});
            skFitSpline(sketch, "E1955", {"points": [v(-33.22, -5.66) * mm, v(-32.9, -5.81) * mm, v(-32.58, -5.97) * mm, v(-32.25, -6.12) * mm]});
            skFitSpline(sketch, "E1956", {"points": [v(-32.25, -6.12) * mm, v(-32.1, -6.2) * mm, v(-31.94, -6.29) * mm, v(-31.87, -6.47) * mm]});
            skFitSpline(sketch, "E1957", {"points": [v(-31.87, -6.47) * mm, v(-31.86, -6.5) * mm, v(-31.82, -6.54) * mm, v(-31.78, -6.56) * mm]});
            skFitSpline(sketch, "E1958", {"points": [v(-31.78, -6.56) * mm, v(-31.61, -6.63) * mm, v(-31.53, -6.76) * mm, v(-31.46, -6.9) * mm]});
            skFitSpline(sketch, "E1959", {"points": [v(-31.46, -6.9) * mm, v(-31.3, -7.24) * mm, v(-31.13, -7.58) * mm, v(-30.97, -7.91) * mm]});
            skFitSpline(sketch, "E1960", {"points": [v(-30.97, -7.91) * mm, v(-30.94, -7.98) * mm, v(-30.9, -8.04) * mm, v(-30.85, -8.14) * mm]});
            skFitSpline(sketch, "E1961", {"points": [v(-30.85, -8.14) * mm, v(-30.56, -6.98) * mm, v(-30.23, -5.88) * mm, v(-30, -4.68) * mm]});
            skFitSpline(sketch, "E1962", {"points": [v(-29.56, 8.87) * mm, v(-28.74, 8.03) * mm, v(-27.95, 7.17) * mm, v(-27.03, 6.4) * mm]});
            skFitSpline(sketch, "E1963", {"points": [v(-27.03, 6.4) * mm, v(-26.63, 7.53) * mm, v(-26.37, 8.66) * mm, v(-26.04, 9.82) * mm]});
            skFitSpline(sketch, "E1964", {"points": [v(-26.04, 9.82) * mm, v(-26.15, 9.75) * mm, v(-26.2, 9.71) * mm, v(-26.27, 9.67) * mm]});
            skFitSpline(sketch, "E1965", {"points": [v(-26.27, 9.67) * mm, v(-26.57, 9.47) * mm, v(-26.88, 9.26) * mm, v(-27.18, 9.05) * mm]});
            skFitSpline(sketch, "E1966", {"points": [v(-27.18, 9.05) * mm, v(-27.31, 8.96) * mm, v(-27.45, 8.92) * mm, v(-27.62, 8.9) * mm]});
            skFitSpline(sketch, "E1967", {"points": [v(-27.62, 8.9) * mm, v(-27.78, 8.9) * mm, v(-27.93, 8.8) * mm, v(-28.08, 8.76) * mm]});
            skFitSpline(sketch, "E1968", {"points": [v(-28.08, 8.76) * mm, v(-28.1, 8.75) * mm, v(-28.12, 8.76) * mm, v(-28.13, 8.76) * mm]});
            skFitSpline(sketch, "E1969", {"points": [v(-28.13, 8.76) * mm, v(-28.6, 8.8) * mm, v(-29.08, 8.83) * mm, v(-29.56, 8.87) * mm]});
            skFitSpline(sketch, "E1970", {"points": [v(-17.18, -5.53) * mm, v(-17.77, -5.38) * mm, v(-18.3, -5.23) * mm, v(-18.83, -5.1) * mm]});
            skFitSpline(sketch, "E1971", {"points": [v(-18.83, -5.1) * mm, v(-19.08, -5.02) * mm, v(-19.34, -4.96) * mm, v(-19.6, -4.9) * mm]});
            skFitSpline(sketch, "E1972", {"points": [v(-19.6, -4.9) * mm, v(-19.93, -4.83) * mm, v(-20.25, -4.73) * mm, v(-20.62, -4.7) * mm]});
            skFitSpline(sketch, "E1973", {"points": [v(-20.62, -4.7) * mm, v(-20.6, -4.84) * mm, v(-20.6, -4.95) * mm, v(-20.57, -5.05) * mm]});
            skFitSpline(sketch, "E1974", {"points": [v(-20.57, -5.05) * mm, v(-20.33, -6.03) * mm, v(-20.08, -7) * mm, v(-19.84, -7.98) * mm]});
            skFitSpline(sketch, "E1975", {"points": [v(-19.84, -7.98) * mm, v(-19.83, -8.01) * mm, v(-19.8, -8.05) * mm, v(-19.77, -8.1) * mm]});
            skFitSpline(sketch, "E1976", {"points": [v(-19.77, -8.1) * mm, v(-19.57, -7.7) * mm, v(-19.38, -7.3) * mm, v(-19.19, -6.92) * mm]});
            skFitSpline(sketch, "E1977", {"points": [v(-19.19, -6.92) * mm, v(-19.12, -6.76) * mm, v(-19.03, -6.62) * mm, v(-18.86, -6.56) * mm]});
            skFitSpline(sketch, "E1978", {"points": [v(-18.86, -6.56) * mm, v(-18.82, -6.55) * mm, v(-18.79, -6.51) * mm, v(-18.77, -6.48) * mm]});
            skFitSpline(sketch, "E1979", {"points": [v(-18.77, -6.48) * mm, v(-18.7, -6.27) * mm, v(-18.52, -6.19) * mm, v(-18.34, -6.1) * mm]});
            skFitSpline(sketch, "E1980", {"points": [v(-18.34, -6.1) * mm, v(-17.96, -5.92) * mm, v(-17.6, -5.74) * mm, v(-17.18, -5.53) * mm]});
            skFitSpline(sketch, "E1981", {"points": [v(-16.46, -4.3) * mm, v(-16.49, -3.82) * mm, v(-16.5, -3.4) * mm, v(-16.54, -2.97) * mm]});
            skFitSpline(sketch, "E1982", {"points": [v(-16.54, -2.97) * mm, v(-16.56, -2.77) * mm, v(-16.57, -2.6) * mm, v(-16.43, -2.43) * mm]});
            skFitSpline(sketch, "E1983", {"points": [v(-16.43, -2.43) * mm, v(-16.41, -2.4) * mm, v(-16.4, -2.36) * mm, v(-16.41, -2.32) * mm]});
            skFitSpline(sketch, "E1984", {"points": [v(-16.41, -2.32) * mm, v(-16.44, -2.15) * mm, v(-16.37, -2.01) * mm, v(-16.28, -1.88) * mm]});
            skFitSpline(sketch, "E1985", {"points": [v(-16.28, -1.88) * mm, v(-16.06, -1.55) * mm, v(-15.84, -1.23) * mm, v(-15.62, -0.9) * mm]});
            skFitSpline(sketch, "E1986", {"points": [v(-15.62, -0.9) * mm, v(-15.59, -0.86) * mm, v(-15.57, -0.8) * mm, v(-15.52, -0.72) * mm]});
            skFitSpline(sketch, "E1987", {"points": [v(-15.52, -0.72) * mm, v(-16.67, -1.05) * mm, v(-17.8, -1.3) * mm, v(-18.92, -1.72) * mm]});
            skFitSpline(sketch, "E1988", {"points": [v(-18.92, -1.72) * mm, v(-18.15, -2.64) * mm, v(-17.3, -3.42) * mm, v(-16.46, -4.3) * mm]});
            skFitSpline(sketch, "E1989", {"points": [v(-18.92, 1.72) * mm, v(-18.74, 1.66) * mm, v(-18.6, 1.6) * mm, v(-18.47, 1.56) * mm]});
            skFitSpline(sketch, "E1990", {"points": [v(-18.47, 1.56) * mm, v(-17.66, 1.32) * mm, v(-16.85, 1.1) * mm, v(-16.03, 0.87) * mm]});
            skFitSpline(sketch, "E1991", {"points": [v(-16.03, 0.87) * mm, v(-15.87, 0.82) * mm, v(-15.7, 0.78) * mm, v(-15.5, 0.72) * mm]});
            skFitSpline(sketch, "E1992", {"points": [v(-15.5, 0.72) * mm, v(-15.6, 0.87) * mm, v(-15.68, 0.99) * mm, v(-15.75, 1.1) * mm]});
            skFitSpline(sketch, "E1993", {"points": [v(-15.75, 1.1) * mm, v(-15.93, 1.36) * mm, v(-16.12, 1.62) * mm, v(-16.28, 1.9) * mm]});
            skFitSpline(sketch, "E1994", {"points": [v(-16.28, 1.9) * mm, v(-16.35, 2) * mm, v(-16.4, 2.14) * mm, v(-16.41, 2.27) * mm]});
            skFitSpline(sketch, "E1995", {"points": [v(-16.41, 2.27) * mm, v(-16.42, 2.35) * mm, v(-16.43, 2.41) * mm, v(-16.47, 2.49) * mm]});
            skFitSpline(sketch, "E1996", {"points": [v(-16.47, 2.49) * mm, v(-16.52, 2.6) * mm, v(-16.56, 2.72) * mm, v(-16.56, 2.83) * mm]});
            skFitSpline(sketch, "E1997", {"points": [v(-16.56, 2.83) * mm, v(-16.53, 3.3) * mm, v(-16.5, 3.77) * mm, v(-16.45, 4.3) * mm]});
            skFitSpline(sketch, "E1998", {"points": [v(-16.45, 4.3) * mm, v(-17.3, 3.43) * mm, v(-18.14, 2.64) * mm, v(-18.92, 1.72) * mm]});
            skFitSpline(sketch, "E1999", {"points": [v(-24.55, 9.79) * mm, v(-24.27, 8.65) * mm, v(-24.01, 7.53) * mm, v(-23.6, 6.41) * mm]});
            skFitSpline(sketch, "E2000", {"points": [v(-23.6, 6.41) * mm, v(-23.48, 6.52) * mm, v(-23.36, 6.6) * mm, v(-23.26, 6.7) * mm]});
            skFitSpline(sketch, "E2001", {"points": [v(-23.26, 6.7) * mm, v(-22.56, 7.37) * mm, v(-21.87, 8.04) * mm, v(-21.18, 8.72) * mm]});
            skFitSpline(sketch, "E2002", {"points": [v(-21.18, 8.72) * mm, v(-21.13, 8.76) * mm, v(-21.1, 8.8) * mm, v(-21.05, 8.86) * mm]});
            skFitSpline(sketch, "E2003", {"points": [v(-21.05, 8.86) * mm, v(-21.53, 8.83) * mm, v(-21.98, 8.81) * mm, v(-22.43, 8.77) * mm]});
            skFitSpline(sketch, "E2004", {"points": [v(-22.43, 8.77) * mm, v(-22.59, 8.76) * mm, v(-22.72, 8.78) * mm, v(-22.85, 8.86) * mm]});
            skFitSpline(sketch, "E2005", {"points": [v(-22.85, 8.86) * mm, v(-22.9, 8.88) * mm, v(-22.95, 8.92) * mm, v(-23, 8.91) * mm]});
            skFitSpline(sketch, "E2006", {"points": [v(-23, 8.91) * mm, v(-23.2, 8.88) * mm, v(-23.35, 8.97) * mm, v(-23.5, 9.08) * mm]});
            skFitSpline(sketch, "E2007", {"points": [v(-23.5, 9.08) * mm, v(-23.85, 9.32) * mm, v(-24.2, 9.55) * mm, v(-24.55, 9.79) * mm]});
            skFitSpline(sketch, "E2008", {"points": [v(-30.85, 8.13) * mm, v(-30.9, 8.05) * mm, v(-30.92, 8.02) * mm, v(-30.93, 7.98) * mm]});
            skFitSpline(sketch, "E2009", {"points": [v(-30.93, 7.98) * mm, v(-31.1, 7.63) * mm, v(-31.3, 7.27) * mm, v(-31.45, 6.9) * mm]});
            skFitSpline(sketch, "E2010", {"points": [v(-31.45, 6.9) * mm, v(-31.56, 6.63) * mm, v(-31.88, 6.56) * mm, v(-32, 6.3) * mm]});
            skFitSpline(sketch, "E2011", {"points": [v(-32, 6.3) * mm, v(-32.02, 6.23) * mm, v(-32.12, 6.2) * mm, v(-32.19, 6.16) * mm]});
            skFitSpline(sketch, "E2012", {"points": [v(-32.19, 6.16) * mm, v(-32.47, 6.02) * mm, v(-32.75, 5.89) * mm, v(-33.03, 5.75) * mm]});
            skFitSpline(sketch, "E2013", {"points": [v(-33.03, 5.75) * mm, v(-33.16, 5.69) * mm, v(-33.3, 5.62) * mm, v(-33.44, 5.55) * mm]});
            skFitSpline(sketch, "E2014", {"points": [v(-33.44, 5.55) * mm, v(-33.4, 5.52) * mm, v(-33.38, 5.5) * mm, v(-33.36, 5.5) * mm]});
            skFitSpline(sketch, "E2015", {"points": [v(-33.36, 5.5) * mm, v(-32.35, 5.25) * mm, v(-31.35, 5) * mm, v(-30.34, 4.74) * mm]});
            skFitSpline(sketch, "E2016", {"points": [v(-30.34, 4.74) * mm, v(-30.24, 4.72) * mm, v(-30.13, 4.68) * mm, v(-30.01, 4.74) * mm]});
            skFitSpline(sketch, "E2017", {"points": [v(-30.01, 4.74) * mm, v(-30.23, 5.87) * mm, v(-30.55, 6.97) * mm, v(-30.85, 8.13) * mm]});
            skFitSpline(sketch, "E2018", {"points": [v(-34.19, -4.26) * mm, v(-33.7, -3.88) * mm, v(-31.88, -1.96) * mm, v(-31.77, -1.7) * mm]});
            skFitSpline(sketch, "E2019", {"points": [v(-31.77, -1.7) * mm, v(-32.86, -1.31) * mm, v(-33.98, -1.05) * mm, v(-35.13, -0.72) * mm]});
            skFitSpline(sketch, "E2020", {"points": [v(-35.13, -0.72) * mm, v(-35.07, -0.82) * mm, v(-35.04, -0.88) * mm, v(-35, -0.93) * mm]});
            skFitSpline(sketch, "E2021", {"points": [v(-35, -0.93) * mm, v(-34.8, -1.24) * mm, v(-34.59, -1.54) * mm, v(-34.38, -1.85) * mm]});
            skFitSpline(sketch, "E2022", {"points": [v(-34.38, -1.85) * mm, v(-34.29, -1.98) * mm, v(-34.23, -2.12) * mm, v(-34.22, -2.29) * mm]});
            skFitSpline(sketch, "E2023", {"points": [v(-34.22, -2.29) * mm, v(-34.2, -2.44) * mm, v(-34.13, -2.6) * mm, v(-34.08, -2.75) * mm]});
            skFitSpline(sketch, "E2024", {"points": [v(-34.08, -2.75) * mm, v(-34.07, -2.79) * mm, v(-34.09, -2.83) * mm, v(-34.09, -2.87) * mm]});
            skFitSpline(sketch, "E2025", {"points": [v(-34.09, -2.87) * mm, v(-34.12, -3.32) * mm, v(-34.15, -3.78) * mm, v(-34.19, -4.26) * mm]});
            skFitSpline(sketch, "E2026", {"points": [v(-26.07, -9.8) * mm, v(-26.14, -9.29) * mm, v(-26.9, -6.72) * mm, v(-27.05, -6.44) * mm]});
            skFitSpline(sketch, "E2027", {"points": [v(-27.05, -6.44) * mm, v(-27.36, -6.64) * mm, v(-29.35, -8.55) * mm, v(-29.57, -8.87) * mm]});
            skFitSpline(sketch, "E2028", {"points": [v(-29.57, -8.87) * mm, v(-29.2, -8.84) * mm, v(-28.84, -8.8) * mm, v(-28.47, -8.79) * mm]});
            skFitSpline(sketch, "E2029", {"points": [v(-28.47, -8.79) * mm, v(-28.22, -8.78) * mm, v(-27.96, -8.7) * mm, v(-27.74, -8.9) * mm]});
            skFitSpline(sketch, "E2030", {"points": [v(-27.74, -8.9) * mm, v(-27.72, -8.91) * mm, v(-27.68, -8.92) * mm, v(-27.65, -8.91) * mm]});
            skFitSpline(sketch, "E2031", {"points": [v(-27.65, -8.91) * mm, v(-27.44, -8.88) * mm, v(-27.28, -8.98) * mm, v(-27.12, -9.09) * mm]});
            skFitSpline(sketch, "E2032", {"points": [v(-27.12, -9.09) * mm, v(-26.78, -9.32) * mm, v(-26.44, -9.55) * mm, v(-26.07, -9.8) * mm]});
            skFitSpline(sketch, "E2033", {"points": [v(-17.2, 5.54) * mm, v(-17.28, 5.59) * mm, v(-17.35, 5.63) * mm, v(-17.42, 5.66) * mm]});
            skFitSpline(sketch, "E2034", {"points": [v(-17.42, 5.66) * mm, v(-17.75, 5.82) * mm, v(-18.08, 6) * mm, v(-18.42, 6.13) * mm]});
            skFitSpline(sketch, "E2035", {"points": [v(-18.42, 6.13) * mm, v(-18.7, 6.24) * mm, v(-18.76, 6.57) * mm, v(-19.03, 6.68) * mm]});
            skFitSpline(sketch, "E2036", {"points": [v(-19.03, 6.68) * mm, v(-19.09, 6.7) * mm, v(-19.12, 6.79) * mm, v(-19.15, 6.85) * mm]});
            skFitSpline(sketch, "E2037", {"points": [v(-19.15, 6.85) * mm, v(-19.29, 7.12) * mm, v(-19.42, 7.4) * mm, v(-19.55, 7.67) * mm]});
            skFitSpline(sketch, "E2038", {"points": [v(-19.55, 7.67) * mm, v(-19.62, 7.8) * mm, v(-19.7, 7.95) * mm, v(-19.77, 8.12) * mm]});
            skFitSpline(sketch, "E2039", {"points": [v(-19.77, 8.12) * mm, v(-19.8, 8.05) * mm, v(-19.82, 8.02) * mm, v(-19.83, 7.98) * mm]});
            skFitSpline(sketch, "E2040", {"points": [v(-19.83, 7.98) * mm, v(-20, 7.38) * mm, v(-20.15, 6.77) * mm, v(-20.3, 6.16) * mm]});
            skFitSpline(sketch, "E2041", {"points": [v(-20.3, 6.16) * mm, v(-20.4, 5.78) * mm, v(-20.5, 5.41) * mm, v(-20.58, 5.04) * mm]});
            skFitSpline(sketch, "E2042", {"points": [v(-20.58, 5.04) * mm, v(-20.6, 4.93) * mm, v(-20.6, 4.82) * mm, v(-20.61, 4.72) * mm]});
            skFitSpline(sketch, "E2043", {"points": [v(-20.61, 4.72) * mm, v(-20.27, 4.73) * mm, v(-17.6, 5.38) * mm, v(-17.2, 5.54) * mm]});
            skFitSpline(sketch, "E2044", {"points": [v(-21.06, -8.87) * mm, v(-21.38, -8.45) * mm, v(-23.34, -6.6) * mm, v(-23.6, -6.45) * mm]});
            skFitSpline(sketch, "E2045", {"points": [v(-23.6, -6.45) * mm, v(-23.78, -6.8) * mm, v(-24.54, -9.44) * mm, v(-24.57, -9.8) * mm]});
            skFitSpline(sketch, "E2046", {"points": [v(-24.57, -9.8) * mm, v(-24.5, -9.75) * mm, v(-24.42, -9.7) * mm, v(-24.36, -9.66) * mm]});
            skFitSpline(sketch, "E2047", {"points": [v(-24.36, -9.66) * mm, v(-24.06, -9.46) * mm, v(-23.76, -9.26) * mm, v(-23.47, -9.06) * mm]});
            skFitSpline(sketch, "E2048", {"points": [v(-23.47, -9.06) * mm, v(-23.33, -8.96) * mm, v(-23.2, -8.92) * mm, v(-23.03, -8.9) * mm]});
            skFitSpline(sketch, "E2049", {"points": [v(-23.03, -8.9) * mm, v(-22.87, -8.89) * mm, v(-22.72, -8.8) * mm, v(-22.56, -8.76) * mm]});
            skFitSpline(sketch, "E2050", {"points": [v(-22.56, -8.76) * mm, v(-22.52, -8.75) * mm, v(-22.48, -8.77) * mm, v(-22.44, -8.77) * mm]});
            skFitSpline(sketch, "E2051", {"points": [v(-22.44, -8.77) * mm, v(-21.99, -8.8) * mm, v(-21.54, -8.83) * mm, v(-21.06, -8.87) * mm]});
            skFitSpline(sketch, "E2052", {"points": [v(-31.75, 1.7) * mm, v(-31.98, 2.06) * mm, v(-33.95, 4.1) * mm, v(-34.19, 4.24) * mm]});
            skFitSpline(sketch, "E2053", {"points": [v(-34.19, 4.24) * mm, v(-34.16, 3.87) * mm, v(-34.13, 3.5) * mm, v(-34.1, 3.14) * mm]});
            skFitSpline(sketch, "E2054", {"points": [v(-34.1, 3.14) * mm, v(-34.1, 2.9) * mm, v(-34.02, 2.65) * mm, v(-34.2, 2.43) * mm]});
            skFitSpline(sketch, "E2055", {"points": [v(-34.2, 2.43) * mm, v(-34.23, 2.4) * mm, v(-34.23, 2.34) * mm, v(-34.23, 2.3) * mm]});
            skFitSpline(sketch, "E2056", {"points": [v(-34.23, 2.3) * mm, v(-34.21, 2.14) * mm, v(-34.27, 2.01) * mm, v(-34.35, 1.89) * mm]});
            skFitSpline(sketch, "E2057", {"points": [v(-34.35, 1.89) * mm, v(-34.58, 1.56) * mm, v(-34.8, 1.23) * mm, v(-35.02, 0.9) * mm]});
            skFitSpline(sketch, "E2058", {"points": [v(-35.02, 0.9) * mm, v(-35.06, 0.85) * mm, v(-35.08, 0.8) * mm, v(-35.12, 0.72) * mm]});
            skFitSpline(sketch, "E2059", {"points": [v(-35.12, 0.72) * mm, v(-33.98, 1.05) * mm, v(-32.86, 1.31) * mm, v(-31.75, 1.7) * mm]});
            skFitSpline(sketch, "E2060", {"points": [v(-24.19, -12.23) * mm, v(-24.15, -12.3) * mm, v(-24.12, -12.37) * mm, v(-24.08, -12.44) * mm]});
            skFitSpline(sketch, "E2061", {"points": [v(-24.08, -12.44) * mm, v(-23.81, -12.9) * mm, v(-23.54, -13.36) * mm, v(-23.28, -13.83) * mm]});
            skFitSpline(sketch, "E2062", {"points": [v(-23.28, -13.83) * mm, v(-23.08, -14.17) * mm, v(-23.1, -14.3) * mm, v(-23.34, -14.6) * mm]});
            skFitSpline(sketch, "E2063", {"points": [v(-23.34, -14.6) * mm, v(-23.53, -14.85) * mm, v(-23.69, -15.12) * mm, v(-23.88, -15.36) * mm]});
            skFitSpline(sketch, "E2064", {"points": [v(-23.88, -15.36) * mm, v(-24.2, -15.75) * mm, v(-24.53, -16.11) * mm, v(-24.85, -16.5) * mm]});
            skFitSpline(sketch, "E2065", {"points": [v(-24.85, -16.5) * mm, v(-25.04, -16.73) * mm, v(-25.59, -16.73) * mm, v(-25.8, -16.5) * mm]});
            skFitSpline(sketch, "E2066", {"points": [v(-25.8, -16.5) * mm, v(-26.16, -16.09) * mm, v(-26.54, -15.7) * mm, v(-26.84, -15.24) * mm]});
            skFitSpline(sketch, "E2067", {"points": [v(-26.84, -15.24) * mm, v(-27, -15) * mm, v(-27.18, -14.78) * mm, v(-27.35, -14.55) * mm]});
            skFitSpline(sketch, "E2068", {"points": [v(-27.35, -14.55) * mm, v(-27.53, -14.32) * mm, v(-27.55, -14.16) * mm, v(-27.4, -13.89) * mm]});
            skFitSpline(sketch, "E2069", {"points": [v(-27.4, -13.89) * mm, v(-27.12, -13.4) * mm, v(-26.84, -12.92) * mm, v(-26.56, -12.43) * mm]});
            skFitSpline(sketch, "E2070", {"points": [v(-26.56, -12.43) * mm, v(-26.52, -12.37) * mm, v(-26.49, -12.3) * mm, v(-26.49, -12.2) * mm]});
            skFitSpline(sketch, "E2071", {"points": [v(-26.49, -12.2) * mm, v(-26.73, -12.35) * mm, v(-26.98, -12.51) * mm, v(-27.23, -12.67) * mm]});
            skFitSpline(sketch, "E2072", {"points": [v(-27.23, -12.67) * mm, v(-27.37, -12.75) * mm, v(-27.51, -12.84) * mm, v(-27.66, -12.92) * mm]});
            skFitSpline(sketch, "E2073", {"points": [v(-27.66, -12.92) * mm, v(-27.92, -13.07) * mm, v(-28.2, -13) * mm, v(-28.34, -12.76) * mm]});
            skFitSpline(sketch, "E2074", {"points": [v(-28.34, -12.76) * mm, v(-28.48, -12.52) * mm, v(-28.4, -12.23) * mm, v(-28.16, -12.08) * mm]});
            skFitSpline(sketch, "E2075", {"points": [v(-28.16, -12.08) * mm, v(-27.87, -11.9) * mm, v(-27.57, -11.72) * mm, v(-27.28, -11.53) * mm]});
            skFitSpline(sketch, "E2076", {"points": [v(-27.28, -11.53) * mm, v(-26.94, -11.32) * mm, v(-26.6, -11.1) * mm, v(-26.25, -10.88) * mm]});
            skFitSpline(sketch, "E2077", {"points": [v(-26.25, -10.88) * mm, v(-26.3, -10.84) * mm, v(-26.34, -10.8) * mm, v(-26.4, -10.77) * mm]});
            skFitSpline(sketch, "E2078", {"points": [v(-26.4, -10.77) * mm, v(-26.87, -10.44) * mm, v(-27.35, -10.1) * mm, v(-27.84, -9.78) * mm]});
            skFitSpline(sketch, "E2079", {"points": [v(-27.84, -9.78) * mm, v(-27.88, -9.75) * mm, v(-27.93, -9.74) * mm, v(-27.98, -9.72) * mm]});
            skFitSpline(sketch, "E2080", {"points": [v(-27.98, -9.72) * mm, v(-28, -9.72) * mm, v(-28.02, -9.73) * mm, v(-28.03, -9.73) * mm]});
            skFitSpline(sketch, "E2081", {"points": [v(-28.03, -9.73) * mm, v(-28.67, -9.77) * mm, v(-29.3, -9.82) * mm, v(-29.97, -9.87) * mm]});
            skFitSpline(sketch, "E2082", {"points": [v(-29.97, -9.87) * mm, v(-29.9, -10) * mm, v(-29.83, -10.12) * mm, v(-29.77, -10.24) * mm]});
            skFitSpline(sketch, "E2083", {"points": [v(-29.77, -10.24) * mm, v(-29.56, -10.65) * mm, v(-29.35, -11.06) * mm, v(-29.14, -11.47) * mm]});
            skFitSpline(sketch, "E2084", {"points": [v(-29.14, -11.47) * mm, v(-29.07, -11.6) * mm, v(-29, -11.72) * mm, v(-28.92, -11.85) * mm]});
            skFitSpline(sketch, "E2085", {"points": [v(-28.92, -11.85) * mm, v(-28.76, -12.12) * mm, v(-28.85, -12.45) * mm, v(-29.12, -12.58) * mm]});
            skFitSpline(sketch, "E2086", {"points": [v(-29.12, -12.58) * mm, v(-29.35, -12.7) * mm, v(-29.6, -12.62) * mm, v(-29.74, -12.39) * mm]});
            skFitSpline(sketch, "E2087", {"points": [v(-29.74, -12.39) * mm, v(-29.9, -12.12) * mm, v(-30.04, -11.84) * mm, v(-30.19, -11.56) * mm]});
            skFitSpline(sketch, "E2088", {"points": [v(-30.19, -11.56) * mm, v(-30.27, -11.42) * mm, v(-30.35, -11.27) * mm, v(-30.46, -11.13) * mm]});
            skFitSpline(sketch, "E2089", {"points": [v(-30.46, -11.13) * mm, v(-30.47, -11.18) * mm, v(-30.48, -11.23) * mm, v(-30.48, -11.28) * mm]});
            skFitSpline(sketch, "E2090", {"points": [v(-30.48, -11.28) * mm, v(-30.48, -11.86) * mm, v(-30.48, -12.45) * mm, v(-30.48, -13.03) * mm]});
            skFitSpline(sketch, "E2091", {"points": [v(-30.48, -13.03) * mm, v(-30.48, -13.41) * mm, v(-30.55, -13.5) * mm, v(-30.9, -13.64) * mm]});
            skFitSpline(sketch, "E2092", {"points": [v(-30.9, -13.64) * mm, v(-31.11, -13.72) * mm, v(-31.33, -13.81) * mm, v(-31.53, -13.92) * mm]});
            skFitSpline(sketch, "E2093", {"points": [v(-31.53, -13.92) * mm, v(-32.04, -14.18) * mm, v(-32.58, -14.35) * mm, v(-33.12, -14.5) * mm]});
            skFitSpline(sketch, "E2094", {"points": [v(-33.12, -14.5) * mm, v(-33.49, -14.62) * mm, v(-33.9, -14.4) * mm, v(-33.99, -14) * mm]});
            skFitSpline(sketch, "E2095", {"points": [v(-33.99, -14) * mm, v(-34.13, -13.42) * mm, v(-34.25, -12.83) * mm, v(-34.28, -12.22) * mm]});
            skFitSpline(sketch, "E2096", {"points": [v(-34.28, -12.22) * mm, v(-34.28, -12) * mm, v(-34.32, -11.8) * mm, v(-34.35, -11.6) * mm]});
            skFitSpline(sketch, "E2097", {"points": [v(-34.35, -11.6) * mm, v(-34.4, -11.3) * mm, v(-34.33, -11.14) * mm, v(-34.06, -10.98) * mm]});
            skFitSpline(sketch, "E2098", {"points": [v(-34.06, -10.98) * mm, v(-33.57, -10.7) * mm, v(-33.09, -10.42) * mm, v(-32.6, -10.14) * mm]});
            skFitSpline(sketch, "E2099", {"points": [v(-32.6, -10.14) * mm, v(-32.54, -10.1) * mm, v(-32.47, -10.06) * mm, v(-32.41, -9.99) * mm]});
            skFitSpline(sketch, "E2100", {"points": [v(-32.41, -9.99) * mm, v(-32.57, -9.99) * mm, v(-32.72, -9.98) * mm, v(-32.87, -9.99) * mm]});
            skFitSpline(sketch, "E2101", {"points": [v(-32.87, -9.99) * mm, v(-33.2, -10) * mm, v(-33.53, -10.02) * mm, v(-33.86, -10.02) * mm]});
            skFitSpline(sketch, "E2102", {"points": [v(-33.86, -10.02) * mm, v(-34.09, -10.02) * mm, v(-34.27, -9.85) * mm, v(-34.31, -9.63) * mm]});
            skFitSpline(sketch, "E2103", {"points": [v(-34.31, -9.63) * mm, v(-34.36, -9.42) * mm, v(-34.24, -9.2) * mm, v(-34.04, -9.1) * mm]});
            skFitSpline(sketch, "E2104", {"points": [v(-34.04, -9.1) * mm, v(-33.95, -9.06) * mm, v(-33.85, -9.05) * mm, v(-33.76, -9.05) * mm]});
            skFitSpline(sketch, "E2105", {"points": [v(-33.76, -9.05) * mm, v(-33.23, -9.03) * mm, v(-32.7, -9.01) * mm, v(-32.18, -9) * mm]});
            skFitSpline(sketch, "E2106", {"points": [v(-32.18, -9) * mm, v(-31.98, -8.99) * mm, v(-31.79, -8.97) * mm, v(-31.57, -8.96) * mm]});
            skFitSpline(sketch, "E2107", {"points": [v(-31.57, -8.96) * mm, v(-31.6, -8.9) * mm, v(-31.6, -8.84) * mm, v(-31.64, -8.78) * mm]});
            skFitSpline(sketch, "E2108", {"points": [v(-31.64, -8.78) * mm, v(-31.89, -8.26) * mm, v(-32.14, -7.73) * mm, v(-32.4, -7.2) * mm]});
            skFitSpline(sketch, "E2109", {"points": [v(-32.4, -7.2) * mm, v(-32.42, -7.16) * mm, v(-32.46, -7.1) * mm, v(-32.51, -7.08) * mm]});
            skFitSpline(sketch, "E2110", {"points": [v(-32.51, -7.08) * mm, v(-33.07, -6.8) * mm, v(-33.62, -6.54) * mm, v(-34.18, -6.28) * mm]});
            skFitSpline(sketch, "E2111", {"points": [v(-34.18, -6.28) * mm, v(-34.2, -6.27) * mm, v(-34.23, -6.26) * mm, v(-34.27, -6.25) * mm]});
            skFitSpline(sketch, "E2112", {"points": [v(-34.27, -6.25) * mm, v(-34.3, -6.57) * mm, v(-34.32, -6.9) * mm, v(-34.33, -7.2) * mm]});
            skFitSpline(sketch, "E2113", {"points": [v(-34.33, -7.2) * mm, v(-34.35, -7.64) * mm, v(-34.36, -8.07) * mm, v(-34.37, -8.5) * mm]});
            skFitSpline(sketch, "E2114", {"points": [v(-34.37, -8.5) * mm, v(-34.38, -8.78) * mm, v(-34.58, -8.99) * mm, v(-34.85, -9) * mm]});
            skFitSpline(sketch, "E2115", {"points": [v(-34.85, -9) * mm, v(-35.12, -9) * mm, v(-35.34, -8.81) * mm, v(-35.34, -8.52) * mm]});
            skFitSpline(sketch, "E2116", {"points": [v(-35.34, -8.52) * mm, v(-35.34, -8.19) * mm, v(-35.31, -7.85) * mm, v(-35.3, -7.52) * mm]});
            skFitSpline(sketch, "E2117", {"points": [v(-35.3, -7.52) * mm, v(-35.3, -7.38) * mm, v(-35.3, -7.24) * mm, v(-35.34, -7.1) * mm]});
            skFitSpline(sketch, "E2118", {"points": [v(-35.34, -7.1) * mm, v(-35.37, -7.14) * mm, v(-35.4, -7.19) * mm, v(-35.44, -7.24) * mm]});
            skFitSpline(sketch, "E2119", {"points": [v(-35.44, -7.24) * mm, v(-35.72, -7.72) * mm, v(-36, -8.2) * mm, v(-36.28, -8.7) * mm]});
            skFitSpline(sketch, "E2120", {"points": [v(-36.28, -8.7) * mm, v(-36.47, -9.02) * mm, v(-36.58, -9.07) * mm, v(-36.97, -9.02) * mm]});
            skFitSpline(sketch, "E2121", {"points": [v(-36.97, -9.02) * mm, v(-37.42, -8.97) * mm, v(-37.87, -8.94) * mm, v(-38.32, -8.87) * mm]});
            skFitSpline(sketch, "E2122", {"points": [v(-38.32, -8.87) * mm, v(-38.67, -8.82) * mm, v(-39, -8.72) * mm, v(-39.35, -8.66) * mm]});
            skFitSpline(sketch, "E2123", {"points": [v(-39.35, -8.66) * mm, v(-39.68, -8.6) * mm, v(-39.95, -8.21) * mm, v(-39.83, -7.82) * mm]});
            skFitSpline(sketch, "E2124", {"points": [v(-39.83, -7.82) * mm, v(-39.68, -7.35) * mm, v(-39.51, -6.89) * mm, v(-39.34, -6.43) * mm]});
            skFitSpline(sketch, "E2125", {"points": [v(-39.34, -6.43) * mm, v(-39.21, -6.1) * mm, v(-39.06, -5.8) * mm, v(-38.93, -5.48) * mm]});
            skFitSpline(sketch, "E2126", {"points": [v(-38.93, -5.48) * mm, v(-38.83, -5.27) * mm, v(-38.68, -5.16) * mm, v(-38.44, -5.16) * mm]});
            skFitSpline(sketch, "E2127", {"points": [v(-38.44, -5.16) * mm, v(-37.86, -5.16) * mm, v(-37.28, -5.16) * mm, v(-36.7, -5.16) * mm]});
            skFitSpline(sketch, "E2128", {"points": [v(-36.7, -5.16) * mm, v(-36.62, -5.16) * mm, v(-36.54, -5.16) * mm, v(-36.46, -5.16) * mm]});
            skFitSpline(sketch, "E2129", {"points": [v(-36.46, -5.16) * mm, v(-36.46, -5.14) * mm, v(-36.45, -5.13) * mm, v(-36.45, -5.1) * mm]});
            skFitSpline(sketch, "E2130", {"points": [v(-36.45, -5.1) * mm, v(-36.6, -5.03) * mm, v(-36.74, -4.94) * mm, v(-36.9, -4.86) * mm]});
            skFitSpline(sketch, "E2131", {"points": [v(-36.9, -4.86) * mm, v(-37.17, -4.71) * mm, v(-37.45, -4.58) * mm, v(-37.71, -4.42) * mm]});
            skFitSpline(sketch, "E2132", {"points": [v(-37.71, -4.42) * mm, v(-38.03, -4.22) * mm, v(-38.04, -3.8) * mm, v(-37.73, -3.6) * mm]});
            skFitSpline(sketch, "E2133", {"points": [v(-37.73, -3.6) * mm, v(-37.55, -3.49) * mm, v(-37.36, -3.5) * mm, v(-37.18, -3.6) * mm]});
            skFitSpline(sketch, "E2134", {"points": [v(-37.18, -3.6) * mm, v(-36.66, -3.86) * mm, v(-36.14, -4.14) * mm, v(-35.62, -4.42) * mm]});
            skFitSpline(sketch, "E2135", {"points": [v(-35.62, -4.42) * mm, v(-35.48, -4.49) * mm, v(-35.35, -4.56) * mm, v(-35.2, -4.65) * mm]});
            skFitSpline(sketch, "E2136", {"points": [v(-35.2, -4.65) * mm, v(-35.19, -4.5) * mm, v(-35.17, -4.36) * mm, v(-35.15, -4.22) * mm]});
            skFitSpline(sketch, "E2137", {"points": [v(-35.15, -4.22) * mm, v(-35.13, -3.95) * mm, v(-35.1, -3.68) * mm, v(-35.09, -3.4) * mm]});
            skFitSpline(sketch, "E2138", {"points": [v(-35.09, -3.4) * mm, v(-35.07, -3.18) * mm, v(-35.06, -2.95) * mm, v(-35.05, -2.72) * mm]});
            skFitSpline(sketch, "E2139", {"points": [v(-35.05, -2.72) * mm, v(-35.05, -2.66) * mm, v(-35.05, -2.59) * mm, v(-35.08, -2.54) * mm]});
            skFitSpline(sketch, "E2140", {"points": [v(-35.08, -2.54) * mm, v(-35.44, -2.02) * mm, v(-35.8, -1.5) * mm, v(-36.15, -0.98) * mm]});
            skFitSpline(sketch, "E2141", {"points": [v(-36.15, -0.98) * mm, v(-36.16, -0.96) * mm, v(-36.18, -0.96) * mm, v(-36.2, -0.93) * mm]});
            skFitSpline(sketch, "E2142", {"points": [v(-36.2, -0.93) * mm, v(-36.27, -1.04) * mm, v(-36.33, -1.14) * mm, v(-36.4, -1.25) * mm]});
            skFitSpline(sketch, "E2143", {"points": [v(-36.4, -1.25) * mm, v(-36.66, -1.65) * mm, v(-36.92, -2.05) * mm, v(-37.18, -2.45) * mm]});
            skFitSpline(sketch, "E2144", {"points": [v(-37.18, -2.45) * mm, v(-37.25, -2.56) * mm, v(-37.3, -2.67) * mm, v(-37.37, -2.79) * mm]});
            skFitSpline(sketch, "E2145", {"points": [v(-37.37, -2.79) * mm, v(-37.48, -3) * mm, v(-37.7, -3.12) * mm, v(-37.9, -3.09) * mm]});
            skFitSpline(sketch, "E2146", {"points": [v(-37.9, -3.09) * mm, v(-38.24, -3.04) * mm, v(-38.43, -2.68) * mm, v(-38.26, -2.36) * mm]});
            skFitSpline(sketch, "E2147", {"points": [v(-38.26, -2.36) * mm, v(-38.1, -2.1) * mm, v(-37.93, -1.83) * mm, v(-37.77, -1.57) * mm]});
            skFitSpline(sketch, "E2148", {"points": [v(-37.77, -1.57) * mm, v(-37.69, -1.44) * mm, v(-37.61, -1.3) * mm, v(-37.5, -1.13) * mm]});
            skFitSpline(sketch, "E2149", {"points": [v(-37.5, -1.13) * mm, v(-37.6, -1.17) * mm, v(-37.65, -1.18) * mm, v(-37.7, -1.2) * mm]});
            skFitSpline(sketch, "E2150", {"points": [v(-37.7, -1.2) * mm, v(-38.18, -1.48) * mm, v(-38.67, -1.76) * mm, v(-39.15, -2.05) * mm]});
            skFitSpline(sketch, "E2151", {"points": [v(-39.15, -2.05) * mm, v(-39.44, -2.22) * mm, v(-39.68, -2.2) * mm, v(-39.93, -1.99) * mm]});
            skFitSpline(sketch, "E2152", {"points": [v(-39.93, -1.99) * mm, v(-40.16, -1.78) * mm, v(-40.44, -1.63) * mm, v(-40.68, -1.43) * mm]});
            skFitSpline(sketch, "E2153", {"points": [v(-40.68, -1.43) * mm, v(-41.07, -1.12) * mm, v(-41.43, -0.79) * mm, v(-41.82, -0.47) * mm]});
            skFitSpline(sketch, "E2154", {"points": [v(-41.82, -0.47) * mm, v(-42.06, -0.27) * mm, v(-42.05, 0.26) * mm, v(-41.81, 0.48) * mm]});
            skFitSpline(sketch, "E2155", {"points": [v(-41.81, 0.48) * mm, v(-41.4, 0.86) * mm, v(-40.98, 1.25) * mm, v(-40.5, 1.57) * mm]});
            skFitSpline(sketch, "E2156", {"points": [v(-40.5, 1.57) * mm, v(-40.28, 1.71) * mm, v(-40.07, 1.87) * mm, v(-39.87, 2.04) * mm]});
            skFitSpline(sketch, "E2157", {"points": [v(-39.87, 2.04) * mm, v(-39.66, 2.2) * mm, v(-39.45, 2.22) * mm, v(-39.23, 2.09) * mm]});
            skFitSpline(sketch, "E2158", {"points": [v(-39.23, 2.09) * mm, v(-38.75, 1.81) * mm, v(-38.27, 1.54) * mm, v(-37.8, 1.26) * mm]});
            skFitSpline(sketch, "E2159", {"points": [v(-37.8, 1.26) * mm, v(-37.72, 1.22) * mm, v(-37.64, 1.18) * mm, v(-37.54, 1.18) * mm]});
            skFitSpline(sketch, "E2160", {"points": [v(-37.54, 1.18) * mm, v(-37.61, 1.3) * mm, v(-37.68, 1.43) * mm, v(-37.76, 1.56) * mm]});
            skFitSpline(sketch, "E2161", {"points": [v(-37.76, 1.56) * mm, v(-37.92, 1.82) * mm, v(-38.09, 2.07) * mm, v(-38.24, 2.33) * mm]});
            skFitSpline(sketch, "E2162", {"points": [v(-38.24, 2.33) * mm, v(-38.4, 2.6) * mm, v(-38.32, 2.88) * mm, v(-38.09, 3.02) * mm]});
            skFitSpline(sketch, "E2163", {"points": [v(-38.09, 3.02) * mm, v(-37.84, 3.17) * mm, v(-37.54, 3.08) * mm, v(-37.38, 2.82) * mm]});
            skFitSpline(sketch, "E2164", {"points": [v(-37.38, 2.82) * mm, v(-37.1, 2.36) * mm, v(-36.82, 1.91) * mm, v(-36.53, 1.46) * mm]});
            skFitSpline(sketch, "E2165", {"points": [v(-36.53, 1.46) * mm, v(-36.43, 1.3) * mm, v(-36.32, 1.12) * mm, v(-36.21, 0.94) * mm]});
            skFitSpline(sketch, "E2166", {"points": [v(-36.21, 0.94) * mm, v(-36.18, 0.97) * mm, v(-36.14, 1) * mm, v(-36.12, 1.03) * mm]});
            skFitSpline(sketch, "E2167", {"points": [v(-36.12, 1.03) * mm, v(-35.77, 1.53) * mm, v(-35.43, 2.03) * mm, v(-35.1, 2.53) * mm]});
            skFitSpline(sketch, "E2168", {"points": [v(-35.1, 2.53) * mm, v(-35.06, 2.57) * mm, v(-35.04, 2.63) * mm, v(-35.04, 2.68) * mm]});
            skFitSpline(sketch, "E2169", {"points": [v(-35.04, 2.68) * mm, v(-35.1, 3.33) * mm, v(-35.14, 3.98) * mm, v(-35.2, 4.64) * mm]});
            skFitSpline(sketch, "E2170", {"points": [v(-35.2, 4.64) * mm, v(-35.51, 4.48) * mm, v(-35.82, 4.33) * mm, v(-36.12, 4.17) * mm]});
            skFitSpline(sketch, "E2171", {"points": [v(-36.12, 4.17) * mm, v(-36.48, 3.98) * mm, v(-36.83, 3.78) * mm, v(-37.2, 3.59) * mm]});
            skFitSpline(sketch, "E2172", {"points": [v(-37.2, 3.59) * mm, v(-37.47, 3.44) * mm, v(-37.8, 3.55) * mm, v(-37.92, 3.83) * mm]});
            skFitSpline(sketch, "E2173", {"points": [v(-37.92, 3.83) * mm, v(-38.01, 4.05) * mm, v(-37.93, 4.29) * mm, v(-37.7, 4.42) * mm]});
            skFitSpline(sketch, "E2174", {"points": [v(-37.7, 4.42) * mm, v(-37.44, 4.58) * mm, v(-37.17, 4.71) * mm, v(-36.9, 4.86) * mm]});
            skFitSpline(sketch, "E2175", {"points": [v(-36.9, 4.86) * mm, v(-36.76, 4.93) * mm, v(-36.62, 5.02) * mm, v(-36.48, 5.14) * mm]});
            skFitSpline(sketch, "E2176", {"points": [v(-36.48, 5.14) * mm, v(-36.54, 5.14) * mm, v(-36.6, 5.15) * mm, v(-36.67, 5.15) * mm]});
            skFitSpline(sketch, "E2177", {"points": [v(-36.67, 5.15) * mm, v(-37.24, 5.16) * mm, v(-37.8, 5.15) * mm, v(-38.38, 5.16) * mm]});
            skFitSpline(sketch, "E2178", {"points": [v(-38.38, 5.16) * mm, v(-38.72, 5.16) * mm, v(-38.82, 5.24) * mm, v(-38.95, 5.55) * mm]});
            skFitSpline(sketch, "E2179", {"points": [v(-38.95, 5.55) * mm, v(-39.03, 5.77) * mm, v(-39.12, 5.98) * mm, v(-39.23, 6.19) * mm]});
            skFitSpline(sketch, "E2180", {"points": [v(-39.23, 6.19) * mm, v(-39.49, 6.7) * mm, v(-39.66, 7.23) * mm, v(-39.82, 7.78) * mm]});
            skFitSpline(sketch, "E2181", {"points": [v(-39.82, 7.78) * mm, v(-39.94, 8.16) * mm, v(-39.74, 8.57) * mm, v(-39.3, 8.68) * mm]});
            skFitSpline(sketch, "E2182", {"points": [v(-39.3, 8.68) * mm, v(-38.66, 8.83) * mm, v(-38, 8.93) * mm, v(-37.34, 8.97) * mm]});
            skFitSpline(sketch, "E2183", {"points": [v(-37.34, 8.97) * mm, v(-37.2, 8.98) * mm, v(-37.06, 9) * mm, v(-36.92, 9.03) * mm]});
            skFitSpline(sketch, "E2184", {"points": [v(-36.92, 9.03) * mm, v(-36.64, 9.08) * mm, v(-36.44, 8.98) * mm, v(-36.3, 8.73) * mm]});
            skFitSpline(sketch, "E2185", {"points": [v(-36.3, 8.73) * mm, v(-36.02, 8.23) * mm, v(-35.72, 7.73) * mm, v(-35.44, 7.24) * mm]});
            skFitSpline(sketch, "E2186", {"points": [v(-35.44, 7.24) * mm, v(-35.4, 7.19) * mm, v(-35.38, 7.14) * mm, v(-35.33, 7.06) * mm]});
            skFitSpline(sketch, "E2187", {"points": [v(-35.33, 7.06) * mm, v(-35.27, 7.24) * mm, v(-35.3, 7.38) * mm, v(-35.3, 7.53) * mm]});
            skFitSpline(sketch, "E2188", {"points": [v(-35.3, 7.53) * mm, v(-35.32, 7.86) * mm, v(-35.34, 8.2) * mm, v(-35.34, 8.53) * mm]});
            skFitSpline(sketch, "E2189", {"points": [v(-35.34, 8.53) * mm, v(-35.34, 8.81) * mm, v(-35.13, 9) * mm, v(-34.86, 9) * mm]});
            skFitSpline(sketch, "E2190", {"points": [v(-34.86, 9) * mm, v(-34.59, 9) * mm, v(-34.38, 8.8) * mm, v(-34.37, 8.51) * mm]});
            skFitSpline(sketch, "E2191", {"points": [v(-34.37, 8.51) * mm, v(-34.35, 8) * mm, v(-34.34, 7.48) * mm, v(-34.32, 6.96) * mm]});
            skFitSpline(sketch, "E2192", {"points": [v(-34.32, 6.96) * mm, v(-34.31, 6.73) * mm, v(-34.29, 6.5) * mm, v(-34.27, 6.25) * mm]});
            skFitSpline(sketch, "E2193", {"points": [v(-34.27, 6.25) * mm, v(-34.21, 6.27) * mm, v(-34.16, 6.3) * mm, v(-34.1, 6.32) * mm]});
            skFitSpline(sketch, "E2194", {"points": [v(-34.1, 6.32) * mm, v(-33.58, 6.57) * mm, v(-33.05, 6.82) * mm, v(-32.53, 7.07) * mm]});
            skFitSpline(sketch, "E2195", {"points": [v(-32.53, 7.07) * mm, v(-32.47, 7.1) * mm, v(-32.42, 7.15) * mm, v(-32.4, 7.2) * mm]});
            skFitSpline(sketch, "E2196", {"points": [v(-32.4, 7.2) * mm, v(-32.13, 7.74) * mm, v(-31.87, 8.29) * mm, v(-31.6, 8.84) * mm]});
            skFitSpline(sketch, "E2197", {"points": [v(-31.6, 8.84) * mm, v(-31.6, 8.87) * mm, v(-31.58, 8.9) * mm, v(-31.56, 8.95) * mm]});
            skFitSpline(sketch, "E2198", {"points": [v(-31.56, 8.95) * mm, v(-31.92, 8.98) * mm, v(-32.26, 9) * mm, v(-32.6, 9.02) * mm]});
            skFitSpline(sketch, "E2199", {"points": [v(-32.6, 9.02) * mm, v(-32.9, 9.04) * mm, v(-33.2, 9.05) * mm, v(-33.5, 9.06) * mm]});
            skFitSpline(sketch, "E2200", {"points": [v(-33.5, 9.06) * mm, v(-33.57, 9.07) * mm, v(-33.64, 9.04) * mm, v(-33.7, 9.05) * mm]});
            skFitSpline(sketch, "E2201", {"points": [v(-33.7, 9.05) * mm, v(-33.82, 9.06) * mm, v(-33.96, 9.07) * mm, v(-34.07, 9.12) * mm]});
            skFitSpline(sketch, "E2202", {"points": [v(-34.07, 9.12) * mm, v(-34.26, 9.21) * mm, v(-34.36, 9.44) * mm, v(-34.31, 9.64) * mm]});
            skFitSpline(sketch, "E2203", {"points": [v(-34.31, 9.64) * mm, v(-34.26, 9.86) * mm, v(-34.08, 10.02) * mm, v(-33.85, 10.02) * mm]});
            skFitSpline(sketch, "E2204", {"points": [v(-33.85, 10.02) * mm, v(-33.53, 10.03) * mm, v(-33.22, 10) * mm, v(-32.91, 10) * mm]});
            skFitSpline(sketch, "E2205", {"points": [v(-32.91, 10) * mm, v(-32.75, 9.99) * mm, v(-32.58, 10) * mm, v(-32.36, 10) * mm]});
            skFitSpline(sketch, "E2206", {"points": [v(-32.36, 10) * mm, v(-32.45, 10.05) * mm, v(-32.5, 10.09) * mm, v(-32.55, 10.12) * mm]});
            skFitSpline(sketch, "E2207", {"points": [v(-32.55, 10.12) * mm, v(-33.04, 10.4) * mm, v(-33.52, 10.67) * mm, v(-34, 10.95) * mm]});
            skFitSpline(sketch, "E2208", {"points": [v(-34, 10.95) * mm, v(-34.34, 11.15) * mm, v(-34.4, 11.27) * mm, v(-34.34, 11.66) * mm]});
            skFitSpline(sketch, "E2209", {"points": [v(-34.34, 11.66) * mm, v(-34.3, 11.96) * mm, v(-34.26, 12.26) * mm, v(-34.24, 12.56) * mm]});
            skFitSpline(sketch, "E2210", {"points": [v(-34.24, 12.56) * mm, v(-34.22, 13.07) * mm, v(-34.09, 13.55) * mm, v(-33.98, 14.04) * mm]});
            skFitSpline(sketch, "E2211", {"points": [v(-33.98, 14.04) * mm, v(-33.9, 14.38) * mm, v(-33.49, 14.61) * mm, v(-33.16, 14.52) * mm]});
            skFitSpline(sketch, "E2212", {"points": [v(-33.16, 14.52) * mm, v(-32.65, 14.37) * mm, v(-32.15, 14.22) * mm, v(-31.67, 13.99) * mm]});
            skFitSpline(sketch, "E2213", {"points": [v(-31.67, 13.99) * mm, v(-31.4, 13.85) * mm, v(-31.1, 13.73) * mm, v(-30.82, 13.61) * mm]});
            skFitSpline(sketch, "E2214", {"points": [v(-30.82, 13.61) * mm, v(-30.58, 13.51) * mm, v(-30.48, 13.38) * mm, v(-30.48, 13.12) * mm]});
            skFitSpline(sketch, "E2215", {"points": [v(-30.48, 13.12) * mm, v(-30.48, 12.46) * mm, v(-30.48, 11.8) * mm, v(-30.48, 11.1) * mm]});
            skFitSpline(sketch, "E2216", {"points": [v(-30.48, 11.1) * mm, v(-30.42, 11.17) * mm, v(-30.39, 11.2) * mm, v(-30.36, 11.24) * mm]});
            skFitSpline(sketch, "E2217", {"points": [v(-30.36, 11.24) * mm, v(-30.16, 11.62) * mm, v(-29.96, 12) * mm, v(-29.75, 12.38) * mm]});
            skFitSpline(sketch, "E2218", {"points": [v(-29.75, 12.38) * mm, v(-29.6, 12.65) * mm, v(-29.29, 12.71) * mm, v(-29.05, 12.54) * mm]});
            skFitSpline(sketch, "E2219", {"points": [v(-29.05, 12.54) * mm, v(-28.84, 12.4) * mm, v(-28.78, 12.1) * mm, v(-28.9, 11.87) * mm]});
            skFitSpline(sketch, "E2220", {"points": [v(-28.9, 11.87) * mm, v(-29.2, 11.32) * mm, v(-29.5, 10.76) * mm, v(-29.79, 10.2) * mm]});
            skFitSpline(sketch, "E2221", {"points": [v(-29.79, 10.2) * mm, v(-29.84, 10.1) * mm, v(-29.9, 10) * mm, v(-29.97, 9.87) * mm]});
            skFitSpline(sketch, "E2222", {"points": [v(-29.97, 9.87) * mm, v(-29.7, 9.85) * mm, v(-29.46, 9.83) * mm, v(-29.22, 9.81) * mm]});
            skFitSpline(sketch, "E2223", {"points": [v(-29.22, 9.81) * mm, v(-28.82, 9.78) * mm, v(-28.42, 9.75) * mm, v(-28.02, 9.73) * mm]});
            skFitSpline(sketch, "E2224", {"points": [v(-28.02, 9.73) * mm, v(-27.97, 9.72) * mm, v(-27.9, 9.74) * mm, v(-27.85, 9.77) * mm]});
            skFitSpline(sketch, "E2225", {"points": [v(-27.85, 9.77) * mm, v(-27.34, 10.11) * mm, v(-26.83, 10.46) * mm, v(-26.33, 10.81) * mm]});
            skFitSpline(sketch, "E2226", {"points": [v(-26.33, 10.81) * mm, v(-26.3, 10.83) * mm, v(-26.28, 10.85) * mm, v(-26.24, 10.88) * mm]});
            skFitSpline(sketch, "E2227", {"points": [v(-26.24, 10.88) * mm, v(-26.37, 10.96) * mm, v(-26.48, 11.02) * mm, v(-26.6, 11.1) * mm]});
            skFitSpline(sketch, "E2228", {"points": [v(-26.6, 11.1) * mm, v(-26.98, 11.35) * mm, v(-27.37, 11.6) * mm, v(-27.76, 11.85) * mm]});
            skFitSpline(sketch, "E2229", {"points": [v(-27.76, 11.85) * mm, v(-27.87, 11.92) * mm, v(-28, 11.99) * mm, v(-28.11, 12.05) * mm]});
            skFitSpline(sketch, "E2230", {"points": [v(-28.11, 12.05) * mm, v(-28.33, 12.17) * mm, v(-28.45, 12.4) * mm, v(-28.4, 12.6) * mm]});
            skFitSpline(sketch, "E2231", {"points": [v(-28.4, 12.6) * mm, v(-28.32, 12.95) * mm, v(-27.99, 13.1) * mm, v(-27.68, 12.94) * mm]});
            skFitSpline(sketch, "E2232", {"points": [v(-27.68, 12.94) * mm, v(-27.4, 12.78) * mm, v(-27.15, 12.6) * mm, v(-26.88, 12.44) * mm]});
            skFitSpline(sketch, "E2233", {"points": [v(-26.88, 12.44) * mm, v(-26.75, 12.36) * mm, v(-26.62, 12.28) * mm, v(-26.45, 12.23) * mm]});
            skFitSpline(sketch, "E2234", {"points": [v(-26.45, 12.23) * mm, v(-26.49, 12.3) * mm, v(-26.52, 12.37) * mm, v(-26.56, 12.43) * mm]});
            skFitSpline(sketch, "E2235", {"points": [v(-26.56, 12.43) * mm, v(-26.82, 12.89) * mm, v(-27.08, 13.35) * mm, v(-27.35, 13.8) * mm]});
            skFitSpline(sketch, "E2236", {"points": [v(-27.35, 13.8) * mm, v(-27.52, 14.09) * mm, v(-27.59, 14.3) * mm, v(-27.3, 14.62) * mm]});
            skFitSpline(sketch, "E2237", {"points": [v(-27.3, 14.62) * mm, v(-27.14, 14.8) * mm, v(-27.01, 14.99) * mm, v(-26.89, 15.18) * mm]});
            skFitSpline(sketch, "E2238", {"points": [v(-26.89, 15.18) * mm, v(-26.58, 15.65) * mm, v(-26.2, 16.07) * mm, v(-25.81, 16.47) * mm]});
            skFitSpline(sketch, "E2239", {"points": [v(-25.81, 16.47) * mm, v(-25.52, 16.77) * mm, v(-25.11, 16.76) * mm, v(-24.82, 16.46) * mm]});
            skFitSpline(sketch, "E2240", {"points": [v(-24.82, 16.46) * mm, v(-24.42, 16.06) * mm, v(-24.05, 15.64) * mm, v(-23.75, 15.17) * mm]});
            skFitSpline(sketch, "E2241", {"points": [v(-23.75, 15.17) * mm, v(-23.61, 14.96) * mm, v(-23.46, 14.77) * mm, v(-23.3, 14.57) * mm]});
            skFitSpline(sketch, "E2242", {"points": [v(-23.3, 14.57) * mm, v(-23.11, 14.32) * mm, v(-23.09, 14.17) * mm, v(-23.24, 13.9) * mm]});
            skFitSpline(sketch, "E2243", {"points": [v(-23.24, 13.9) * mm, v(-23.51, 13.41) * mm, v(-23.8, 12.94) * mm, v(-24.07, 12.46) * mm]});
            skFitSpline(sketch, "E2244", {"points": [v(-24.07, 12.46) * mm, v(-24.1, 12.4) * mm, v(-24.14, 12.32) * mm, v(-24.17, 12.26) * mm]});
            skFitSpline(sketch, "E2245", {"points": [v(-24.17, 12.26) * mm, v(-24.16, 12.24) * mm, v(-24.15, 12.23) * mm, v(-24.14, 12.22) * mm]});
            skFitSpline(sketch, "E2246", {"points": [v(-24.14, 12.22) * mm, v(-24, 12.3) * mm, v(-23.88, 12.37) * mm, v(-23.75, 12.45) * mm]});
            skFitSpline(sketch, "E2247", {"points": [v(-23.75, 12.45) * mm, v(-23.5, 12.6) * mm, v(-23.24, 12.77) * mm, v(-22.98, 12.92) * mm]});
            skFitSpline(sketch, "E2248", {"points": [v(-22.98, 12.92) * mm, v(-22.71, 13.08) * mm, v(-22.43, 13) * mm, v(-22.3, 12.76) * mm]});
            skFitSpline(sketch, "E2249", {"points": [v(-22.3, 12.76) * mm, v(-22.16, 12.52) * mm, v(-22.24, 12.23) * mm, v(-22.49, 12.07) * mm]});
            skFitSpline(sketch, "E2250", {"points": [v(-22.49, 12.07) * mm, v(-22.97, 11.77) * mm, v(-23.45, 11.47) * mm, v(-23.93, 11.17) * mm]});
            skFitSpline(sketch, "E2251", {"points": [v(-23.93, 11.17) * mm, v(-24.08, 11.08) * mm, v(-24.23, 10.99) * mm, v(-24.4, 10.88) * mm]});
            skFitSpline(sketch, "E2252", {"points": [v(-24.4, 10.88) * mm, v(-24.34, 10.84) * mm, v(-24.3, 10.8) * mm, v(-24.25, 10.77) * mm]});
            skFitSpline(sketch, "E2253", {"points": [v(-24.25, 10.77) * mm, v(-23.77, 10.44) * mm, v(-23.29, 10.1) * mm, v(-22.8, 9.78) * mm]});
            skFitSpline(sketch, "E2254", {"points": [v(-22.8, 9.78) * mm, v(-22.76, 9.75) * mm, v(-22.7, 9.72) * mm, v(-22.64, 9.72) * mm]});
            skFitSpline(sketch, "E2255", {"points": [v(-22.64, 9.72) * mm, v(-22, 9.77) * mm, v(-21.38, 9.81) * mm, v(-20.75, 9.86) * mm]});
            skFitSpline(sketch, "E2256", {"points": [v(-20.75, 9.86) * mm, v(-20.73, 9.86) * mm, v(-20.7, 9.88) * mm, v(-20.69, 9.89) * mm]});
            skFitSpline(sketch, "E2257", {"points": [v(-20.69, 9.89) * mm, v(-20.84, 10.2) * mm, v(-21, 10.5) * mm, v(-21.15, 10.8) * mm]});
            skFitSpline(sketch, "E2258", {"points": [v(-21.15, 10.8) * mm, v(-21.34, 11.17) * mm, v(-21.54, 11.52) * mm, v(-21.74, 11.88) * mm]});
            skFitSpline(sketch, "E2259", {"points": [v(-21.74, 11.88) * mm, v(-21.87, 12.13) * mm, v(-21.8, 12.43) * mm, v(-21.55, 12.57) * mm]});
            skFitSpline(sketch, "E2260", {"points": [v(-21.55, 12.57) * mm, v(-21.32, 12.7) * mm, v(-21.04, 12.63) * mm, v(-20.9, 12.38) * mm]});
            skFitSpline(sketch, "E2261", {"points": [v(-20.9, 12.38) * mm, v(-20.75, 12.13) * mm, v(-20.62, 11.88) * mm, v(-20.48, 11.62) * mm]});
            skFitSpline(sketch, "E2262", {"points": [v(-20.48, 11.62) * mm, v(-20.4, 11.46) * mm, v(-20.3, 11.3) * mm, v(-20.2, 11.08) * mm]});
            skFitSpline(sketch, "E2263", {"points": [v(-20.2, 11.08) * mm, v(-20.18, 11.2) * mm, v(-20.17, 11.25) * mm, v(-20.17, 11.3) * mm]});
            skFitSpline(sketch, "E2264", {"points": [v(-20.17, 11.3) * mm, v(-20.17, 11.9) * mm, v(-20.17, 12.47) * mm, v(-20.17, 13.06) * mm]});
            skFitSpline(sketch, "E2265", {"points": [v(-20.17, 13.06) * mm, v(-20.17, 13.4) * mm, v(-20.08, 13.5) * mm, v(-19.77, 13.63) * mm]});
            skFitSpline(sketch, "E2266", {"points": [v(-19.77, 13.63) * mm, v(-19.53, 13.72) * mm, v(-19.3, 13.83) * mm, v(-19.07, 13.94) * mm]});
            skFitSpline(sketch, "E2267", {"points": [v(-19.07, 13.94) * mm, v(-18.58, 14.18) * mm, v(-18.06, 14.34) * mm, v(-17.54, 14.5) * mm]});
            skFitSpline(sketch, "E2268", {"points": [v(-17.54, 14.5) * mm, v(-17.15, 14.63) * mm, v(-16.72, 14.36) * mm, v(-16.64, 13.99) * mm]});
            skFitSpline(sketch, "E2269", {"points": [v(-16.64, 13.99) * mm, v(-16.53, 13.42) * mm, v(-16.4, 12.85) * mm, v(-16.37, 12.26) * mm]});
            skFitSpline(sketch, "E2270", {"points": [v(-16.37, 12.26) * mm, v(-16.37, 12.06) * mm, v(-16.32, 11.85) * mm, v(-16.3, 11.65) * mm]});
            skFitSpline(sketch, "E2271", {"points": [v(-16.3, 11.65) * mm, v(-16.24, 11.28) * mm, v(-16.3, 11.15) * mm, v(-16.63, 10.96) * mm]});
            skFitSpline(sketch, "E2272", {"points": [v(-16.63, 10.96) * mm, v(-17.1, 10.68) * mm, v(-17.57, 10.42) * mm, v(-18.04, 10.14) * mm]});
            skFitSpline(sketch, "E2273", {"points": [v(-18.04, 10.14) * mm, v(-18.1, 10.1) * mm, v(-18.17, 10.06) * mm, v(-18.25, 10) * mm]});
            skFitSpline(sketch, "E2274", {"points": [v(-18.25, 10) * mm, v(-17.93, 10) * mm, v(-17.65, 10) * mm, v(-17.37, 10) * mm]});
            skFitSpline(sketch, "E2275", {"points": [v(-17.37, 10) * mm, v(-17.18, 10.01) * mm, v(-17, 10.03) * mm, v(-16.82, 10.03) * mm]});
            skFitSpline(sketch, "E2276", {"points": [v(-16.82, 10.03) * mm, v(-16.5, 10.02) * mm, v(-16.32, 9.81) * mm, v(-16.33, 9.52) * mm]});
            skFitSpline(sketch, "E2277", {"points": [v(-16.33, 9.52) * mm, v(-16.34, 9.24) * mm, v(-16.55, 9.05) * mm, v(-16.85, 9.04) * mm]});
            skFitSpline(sketch, "E2278", {"points": [v(-16.85, 9.04) * mm, v(-17.14, 9.04) * mm, v(-17.42, 9.03) * mm, v(-17.7, 9.02) * mm]});
            skFitSpline(sketch, "E2279", {"points": [v(-17.7, 9.02) * mm, v(-18.16, 9) * mm, v(-18.6, 8.98) * mm, v(-19.06, 8.96) * mm]});
            skFitSpline(sketch, "E2280", {"points": [v(-19.06, 8.96) * mm, v(-19.06, 8.93) * mm, v(-19.06, 8.9) * mm, v(-19.05, 8.87) * mm]});
            skFitSpline(sketch, "E2281", {"points": [v(-19.05, 8.87) * mm, v(-18.78, 8.31) * mm, v(-18.52, 7.75) * mm, v(-18.24, 7.19) * mm]});
            skFitSpline(sketch, "E2282", {"points": [v(-18.24, 7.19) * mm, v(-18.22, 7.14) * mm, v(-18.18, 7.1) * mm, v(-18.13, 7.08) * mm]});
            skFitSpline(sketch, "E2283", {"points": [v(-18.13, 7.08) * mm, v(-17.57, 6.8) * mm, v(-17, 6.54) * mm, v(-16.44, 6.27) * mm]});
            skFitSpline(sketch, "E2284", {"points": [v(-16.44, 6.27) * mm, v(-16.42, 6.26) * mm, v(-16.4, 6.26) * mm, v(-16.36, 6.25) * mm]});
            skFitSpline(sketch, "E2285", {"points": [v(-16.36, 6.25) * mm, v(-16.35, 6.3) * mm, v(-16.35, 6.33) * mm, v(-16.35, 6.36) * mm]});
            skFitSpline(sketch, "E2286", {"points": [v(-16.35, 6.36) * mm, v(-16.31, 6.98) * mm, v(-16.28, 7.59) * mm, v(-16.25, 8.2) * mm]});
            skFitSpline(sketch, "E2287", {"points": [v(-16.25, 8.2) * mm, v(-16.25, 8.28) * mm, v(-16.28, 8.36) * mm, v(-16.28, 8.44) * mm]});
            skFitSpline(sketch, "E2288", {"points": [v(-16.28, 8.44) * mm, v(-16.3, 8.7) * mm, v(-16.14, 8.91) * mm, v(-15.92, 8.98) * mm]});
            skFitSpline(sketch, "E2289", {"points": [v(-15.92, 8.98) * mm, v(-15.62, 9.06) * mm, v(-15.33, 8.88) * mm, v(-15.3, 8.56) * mm]});
            skFitSpline(sketch, "E2290", {"points": [v(-15.3, 8.56) * mm, v(-15.28, 8.38) * mm, v(-15.3, 8.2) * mm, v(-15.3, 8) * mm]});
            skFitSpline(sketch, "E2291", {"points": [v(-15.3, 8) * mm, v(-15.32, 7.7) * mm, v(-15.33, 7.4) * mm, v(-15.34, 7.11) * mm]});
            skFitSpline(sketch, "E2292", {"points": [v(-15.34, 7.11) * mm, v(-15.33, 7.1) * mm, v(-15.31, 7.1) * mm, v(-15.3, 7.1) * mm]});
            skFitSpline(sketch, "E2293", {"points": [v(-15.3, 7.1) * mm, v(-15.26, 7.15) * mm, v(-15.23, 7.2) * mm, v(-15.2, 7.25) * mm]});
            skFitSpline(sketch, "E2294", {"points": [v(-15.2, 7.25) * mm, v(-14.92, 7.73) * mm, v(-14.63, 8.21) * mm, v(-14.36, 8.7) * mm]});
            skFitSpline(sketch, "E2295", {"points": [v(-14.36, 8.7) * mm, v(-14.2, 8.98) * mm, v(-14, 9.07) * mm, v(-13.69, 9.03) * mm]});
            skFitSpline(sketch, "E2296", {"points": [v(-13.69, 9.03) * mm, v(-13.14, 8.95) * mm, v(-12.58, 8.9) * mm, v(-12.03, 8.82) * mm]});
            skFitSpline(sketch, "E2297", {"points": [v(-12.03, 8.82) * mm, v(-11.77, 8.79) * mm, v(-11.51, 8.72) * mm, v(-11.26, 8.64) * mm]});
            skFitSpline(sketch, "E2298", {"points": [v(-11.26, 8.64) * mm, v(-10.9, 8.55) * mm, v(-10.71, 8.22) * mm, v(-10.8, 7.86) * mm]});
            skFitSpline(sketch, "E2299", {"points": [v(-10.8, 7.86) * mm, v(-10.93, 7.35) * mm, v(-11.1, 6.85) * mm, v(-11.32, 6.37) * mm]});
            skFitSpline(sketch, "E2300", {"points": [v(-11.32, 6.37) * mm, v(-11.46, 6.1) * mm, v(-11.58, 5.8) * mm, v(-11.7, 5.52) * mm]});
            skFitSpline(sketch, "E2301", {"points": [v(-11.7, 5.52) * mm, v(-11.8, 5.26) * mm, v(-11.94, 5.16) * mm, v(-12.23, 5.16) * mm]});
            skFitSpline(sketch, "E2302", {"points": [v(-12.23, 5.16) * mm, v(-12.8, 5.15) * mm, v(-13.36, 5.16) * mm, v(-13.93, 5.16) * mm]});
            skLineSegment(sketch, "E2303", {"start": v(-13.93, 5.16) * mm, "end": v(-14.17, 5.16) * mm});
            skFitSpline(sketch, "E2304", {"points": [v(-14.17, 5.16) * mm, v(-14.17, 5.14) * mm, v(-14.18, 5.12) * mm, v(-14.18, 5.1) * mm]});
            skFitSpline(sketch, "E2305", {"points": [v(-14.18, 5.1) * mm, v(-14.04, 5.03) * mm, v(-13.9, 4.94) * mm, v(-13.76, 4.87) * mm]});
            skFitSpline(sketch, "E2306", {"points": [v(-13.76, 4.87) * mm, v(-13.5, 4.72) * mm, v(-13.22, 4.59) * mm, v(-12.96, 4.44) * mm]});
            skFitSpline(sketch, "E2307", {"points": [v(-12.96, 4.44) * mm, v(-12.69, 4.28) * mm, v(-12.61, 4.01) * mm, v(-12.76, 3.77) * mm]});
            skFitSpline(sketch, "E2308", {"points": [v(-12.76, 3.77) * mm, v(-12.9, 3.52) * mm, v(-13.2, 3.45) * mm, v(-13.47, 3.6) * mm]});
            skFitSpline(sketch, "E2309", {"points": [v(-13.47, 3.6) * mm, v(-13.98, 3.87) * mm, v(-14.5, 4.14) * mm, v(-15.01, 4.41) * mm]});
            skFitSpline(sketch, "E2310", {"points": [v(-15.01, 4.41) * mm, v(-15.15, 4.49) * mm, v(-15.29, 4.57) * mm, v(-15.44, 4.65) * mm]});
            skFitSpline(sketch, "E2311", {"points": [v(-15.44, 4.65) * mm, v(-15.47, 4.4) * mm, v(-15.5, 4.18) * mm, v(-15.51, 3.96) * mm]});
            skFitSpline(sketch, "E2312", {"points": [v(-15.51, 3.96) * mm, v(-15.54, 3.62) * mm, v(-15.55, 3.29) * mm, v(-15.58, 2.96) * mm]});
            skFitSpline(sketch, "E2313", {"points": [v(-15.58, 2.96) * mm, v(-15.58, 2.87) * mm, v(-15.6, 2.78) * mm, v(-15.6, 2.7) * mm]});
            skFitSpline(sketch, "E2314", {"points": [v(-15.6, 2.7) * mm, v(-15.6, 2.64) * mm, v(-15.59, 2.58) * mm, v(-15.56, 2.54) * mm]});
            skFitSpline(sketch, "E2315", {"points": [v(-15.56, 2.54) * mm, v(-15.2, 2.02) * mm, v(-14.85, 1.5) * mm, v(-14.5, 0.98) * mm]});
            skFitSpline(sketch, "E2316", {"points": [v(-14.5, 0.98) * mm, v(-14.48, 0.96) * mm, v(-14.46, 0.95) * mm, v(-14.44, 0.93) * mm]});
            skFitSpline(sketch, "E2317", {"points": [v(-14.44, 0.93) * mm, v(-14.24, 1.25) * mm, v(-14.03, 1.56) * mm, v(-13.83, 1.88) * mm]});
            skFitSpline(sketch, "E2318", {"points": [v(-13.83, 1.88) * mm, v(-13.63, 2.2) * mm, v(-13.44, 2.54) * mm, v(-13.23, 2.86) * mm]});
            skFitSpline(sketch, "E2319", {"points": [v(-13.23, 2.86) * mm, v(-13.08, 3.1) * mm, v(-12.78, 3.16) * mm, v(-12.55, 3.02) * mm]});
            skFitSpline(sketch, "E2320", {"points": [v(-12.55, 3.02) * mm, v(-12.32, 2.88) * mm, v(-12.24, 2.6) * mm, v(-12.39, 2.35) * mm]});
            skFitSpline(sketch, "E2321", {"points": [v(-12.39, 2.35) * mm, v(-12.53, 2.1) * mm, v(-12.69, 1.86) * mm, v(-12.84, 1.62) * mm]});
            skFitSpline(sketch, "E2322", {"points": [v(-12.84, 1.62) * mm, v(-12.93, 1.47) * mm, v(-13.02, 1.32) * mm, v(-13.15, 1.13) * mm]});
            skFitSpline(sketch, "E2323", {"points": [v(-13.15, 1.13) * mm, v(-13.05, 1.16) * mm, v(-13, 1.17) * mm, v(-12.96, 1.2) * mm]});
            skFitSpline(sketch, "E2324", {"points": [v(-12.96, 1.2) * mm, v(-12.47, 1.48) * mm, v(-11.98, 1.77) * mm, v(-11.49, 2.05) * mm]});
            skFitSpline(sketch, "E2325", {"points": [v(-11.49, 2.05) * mm, v(-11.4, 2.1) * mm, v(-11.29, 2.16) * mm, v(-11.18, 2.16) * mm]});
            skFitSpline(sketch, "E2326", {"points": [v(-11.18, 2.16) * mm, v(-11.07, 2.17) * mm, v(-10.93, 2.14) * mm, v(-10.84, 2.08) * mm]});
            skFitSpline(sketch, "E2327", {"points": [v(-10.84, 2.08) * mm, v(-10.42, 1.79) * mm, v(-10, 1.48) * mm, v(-9.59, 1.16) * mm]});
            skFitSpline(sketch, "E2328", {"points": [v(-9.59, 1.16) * mm, v(-9.33, 0.96) * mm, v(-9.1, 0.73) * mm, v(-8.86, 0.5) * mm]});
            skFitSpline(sketch, "E2329", {"points": [v(-8.86, 0.5) * mm, v(-8.56, 0.2) * mm, v(-8.56, -0.2) * mm, v(-8.85, -0.5) * mm]});
            skFitSpline(sketch, "E2330", {"points": [v(-8.85, -0.5) * mm, v(-9.25, -0.9) * mm, v(-9.67, -1.26) * mm, v(-10.14, -1.57) * mm]});
            skFitSpline(sketch, "E2331", {"points": [v(-10.14, -1.57) * mm, v(-10.35, -1.7) * mm, v(-10.55, -1.85) * mm, v(-10.74, -2) * mm]});
            skFitSpline(sketch, "E2332", {"points": [v(-10.74, -2) * mm, v(-11, -2.2) * mm, v(-11.16, -2.23) * mm, v(-11.44, -2.07) * mm]});
            skFitSpline(sketch, "E2333", {"points": [v(-11.44, -2.07) * mm, v(-11.93, -1.8) * mm, v(-12.4, -1.51) * mm, v(-12.9, -1.24) * mm]});
            skFitSpline(sketch, "E2334", {"points": [v(-12.9, -1.24) * mm, v(-12.95, -1.2) * mm, v(-13.02, -1.17) * mm, v(-13.12, -1.16) * mm]});
            skFitSpline(sketch, "E2335", {"points": [v(-13.12, -1.16) * mm, v(-13.04, -1.3) * mm, v(-12.96, -1.42) * mm, v(-12.88, -1.55) * mm]});
            skFitSpline(sketch, "E2336", {"points": [v(-12.88, -1.55) * mm, v(-12.72, -1.82) * mm, v(-12.55, -2.08) * mm, v(-12.4, -2.35) * mm]});
            skFitSpline(sketch, "E2337", {"points": [v(-12.4, -2.35) * mm, v(-12.24, -2.61) * mm, v(-12.32, -2.9) * mm, v(-12.57, -3.03) * mm]});
            skFitSpline(sketch, "E2338", {"points": [v(-12.57, -3.03) * mm, v(-12.8, -3.16) * mm, v(-13.1, -3.07) * mm, v(-13.25, -2.82) * mm]});
            skFitSpline(sketch, "E2339", {"points": [v(-13.25, -2.82) * mm, v(-13.56, -2.34) * mm, v(-13.86, -1.85) * mm, v(-14.17, -1.36) * mm]});
            skFitSpline(sketch, "E2340", {"points": [v(-14.17, -1.36) * mm, v(-14.26, -1.22) * mm, v(-14.34, -1.08) * mm, v(-14.44, -0.91) * mm]});
            skFitSpline(sketch, "E2341", {"points": [v(-14.44, -0.91) * mm, v(-14.51, -1.02) * mm, v(-14.58, -1.11) * mm, v(-14.65, -1.2) * mm]});
            skFitSpline(sketch, "E2342", {"points": [v(-14.65, -1.2) * mm, v(-14.95, -1.65) * mm, v(-15.25, -2.1) * mm, v(-15.55, -2.53) * mm]});
            skFitSpline(sketch, "E2343", {"points": [v(-15.55, -2.53) * mm, v(-15.59, -2.58) * mm, v(-15.6, -2.65) * mm, v(-15.6, -2.7) * mm]});
            skFitSpline(sketch, "E2344", {"points": [v(-15.6, -2.7) * mm, v(-15.57, -3.1) * mm, v(-15.54, -3.47) * mm, v(-15.51, -3.85) * mm]});
            skFitSpline(sketch, "E2345", {"points": [v(-15.51, -3.85) * mm, v(-15.5, -4.11) * mm, v(-15.47, -4.37) * mm, v(-15.45, -4.64) * mm]});
            skFitSpline(sketch, "E2346", {"points": [v(-15.45, -4.64) * mm, v(-15.14, -4.48) * mm, v(-14.84, -4.34) * mm, v(-14.55, -4.18) * mm]});
            skFitSpline(sketch, "E2347", {"points": [v(-14.55, -4.18) * mm, v(-14.18, -4) * mm, v(-13.82, -3.79) * mm, v(-13.45, -3.59) * mm]});
            skFitSpline(sketch, "E2348", {"points": [v(-13.45, -3.59) * mm, v(-13.2, -3.45) * mm, v(-12.9, -3.53) * mm, v(-12.76, -3.76) * mm]});
            skFitSpline(sketch, "E2349", {"points": [v(-12.76, -3.76) * mm, v(-12.61, -4) * mm, v(-12.68, -4.28) * mm, v(-12.96, -4.43) * mm]});
            skFitSpline(sketch, "E2350", {"points": [v(-12.96, -4.43) * mm, v(-13.32, -4.64) * mm, v(-13.7, -4.84) * mm, v(-14.07, -5.04) * mm]});
            skFitSpline(sketch, "E2351", {"points": [v(-14.07, -5.04) * mm, v(-14.11, -5.06) * mm, v(-14.15, -5.09) * mm, v(-14.23, -5.14) * mm]});
            skFitSpline(sketch, "E2352", {"points": [v(-14.23, -5.14) * mm, v(-14.1, -5.15) * mm, v(-14.03, -5.16) * mm, v(-13.95, -5.16) * mm]});
            skFitSpline(sketch, "E2353", {"points": [v(-13.95, -5.16) * mm, v(-13.38, -5.16) * mm, v(-12.81, -5.16) * mm, v(-12.25, -5.16) * mm]});
            skFitSpline(sketch, "E2354", {"points": [v(-12.25, -5.16) * mm, v(-11.92, -5.16) * mm, v(-11.81, -5.25) * mm, v(-11.7, -5.55) * mm]});
            skFitSpline(sketch, "E2355", {"points": [v(-11.7, -5.55) * mm, v(-11.6, -5.8) * mm, v(-11.49, -6.03) * mm, v(-11.37, -6.27) * mm]});
            skFitSpline(sketch, "E2356", {"points": [v(-11.37, -6.27) * mm, v(-11.13, -6.75) * mm, v(-10.98, -7.26) * mm, v(-10.82, -7.77) * mm]});
            skFitSpline(sketch, "E2357", {"points": [v(-10.82, -7.77) * mm, v(-10.7, -8.17) * mm, v(-10.93, -8.58) * mm, v(-11.35, -8.68) * mm]});
            skFitSpline(sketch, "E2358", {"points": [v(-11.35, -8.68) * mm, v(-11.98, -8.83) * mm, v(-12.6, -8.93) * mm, v(-13.24, -8.97) * mm]});
            skFitSpline(sketch, "E2359", {"points": [v(-13.24, -8.97) * mm, v(-13.4, -8.98) * mm, v(-13.56, -9) * mm, v(-13.72, -9.03) * mm]});
            skFitSpline(sketch, "E2360", {"points": [v(-13.72, -9.03) * mm, v(-14, -9.09) * mm, v(-14.2, -8.98) * mm, v(-14.34, -8.74) * mm]});
            skFitSpline(sketch, "E2361", {"points": [v(-14.34, -8.74) * mm, v(-14.62, -8.24) * mm, v(-14.91, -7.74) * mm, v(-15.2, -7.24) * mm]});
            skFitSpline(sketch, "E2362", {"points": [v(-15.2, -7.24) * mm, v(-15.23, -7.2) * mm, v(-15.26, -7.15) * mm, v(-15.3, -7.07) * mm]});
            skFitSpline(sketch, "E2363", {"points": [v(-15.3, -7.07) * mm, v(-15.32, -7.15) * mm, v(-15.34, -7.2) * mm, v(-15.34, -7.24) * mm]});
            skFitSpline(sketch, "E2364", {"points": [v(-15.34, -7.24) * mm, v(-15.32, -7.61) * mm, v(-15.3, -7.98) * mm, v(-15.29, -8.34) * mm]});
            skFitSpline(sketch, "E2365", {"points": [v(-15.29, -8.34) * mm, v(-15.29, -8.4) * mm, v(-15.29, -8.47) * mm, v(-15.3, -8.54) * mm]});
            skFitSpline(sketch, "E2366", {"points": [v(-15.3, -8.54) * mm, v(-15.32, -8.82) * mm, v(-15.53, -9.01) * mm, v(-15.8, -9) * mm]});
            skFitSpline(sketch, "E2367", {"points": [v(-15.8, -9) * mm, v(-16.07, -8.98) * mm, v(-16.27, -8.76) * mm, v(-16.28, -8.49) * mm]});
            skFitSpline(sketch, "E2368", {"points": [v(-16.28, -8.49) * mm, v(-16.29, -8.19) * mm, v(-16.29, -7.88) * mm, v(-16.3, -7.58) * mm]});
            skFitSpline(sketch, "E2369", {"points": [v(-16.3, -7.58) * mm, v(-16.31, -7.14) * mm, v(-16.34, -6.7) * mm, v(-16.35, -6.25) * mm]});
            skFitSpline(sketch, "E2370", {"points": [v(-16.35, -6.25) * mm, v(-16.4, -6.26) * mm, v(-16.43, -6.27) * mm, v(-16.47, -6.28) * mm]});
            skFitSpline(sketch, "E2371", {"points": [v(-16.47, -6.28) * mm, v(-17.02, -6.54) * mm, v(-17.58, -6.8) * mm, v(-18.13, -7.08) * mm]});
            skFitSpline(sketch, "E2372", {"points": [v(-18.13, -7.08) * mm, v(-18.17, -7.1) * mm, v(-18.22, -7.14) * mm, v(-18.24, -7.19) * mm]});
            skFitSpline(sketch, "E2373", {"points": [v(-18.24, -7.19) * mm, v(-18.51, -7.75) * mm, v(-18.78, -8.3) * mm, v(-19.05, -8.87) * mm]});
            skFitSpline(sketch, "E2374", {"points": [v(-19.05, -8.87) * mm, v(-19.06, -8.9) * mm, v(-19.06, -8.92) * mm, v(-19.07, -8.95) * mm]});
            skFitSpline(sketch, "E2375", {"points": [v(-19.07, -8.95) * mm, v(-18.75, -8.97) * mm, v(-18.45, -9) * mm, v(-18.14, -9.02) * mm]});
            skFitSpline(sketch, "E2376", {"points": [v(-18.14, -9.02) * mm, v(-17.71, -9.03) * mm, v(-17.28, -9.04) * mm, v(-16.85, -9.05) * mm]});
            skFitSpline(sketch, "E2377", {"points": [v(-16.85, -9.05) * mm, v(-16.55, -9.05) * mm, v(-16.34, -9.24) * mm, v(-16.33, -9.52) * mm]});
            skFitSpline(sketch, "E2378", {"points": [v(-16.33, -9.52) * mm, v(-16.32, -9.81) * mm, v(-16.51, -10.02) * mm, v(-16.82, -10.02) * mm]});
            skFitSpline(sketch, "E2379", {"points": [v(-16.82, -10.02) * mm, v(-17.14, -10.02) * mm, v(-17.45, -10) * mm, v(-17.77, -9.99) * mm]});
            skFitSpline(sketch, "E2380", {"points": [v(-17.77, -9.99) * mm, v(-17.92, -9.98) * mm, v(-18.07, -9.99) * mm, v(-18.27, -9.99) * mm]});
            skFitSpline(sketch, "E2381", {"points": [v(-18.27, -9.99) * mm, v(-18.18, -10.05) * mm, v(-18.13, -10.09) * mm, v(-18.08, -10.12) * mm]});
            skFitSpline(sketch, "E2382", {"points": [v(-18.08, -10.12) * mm, v(-17.6, -10.4) * mm, v(-17.13, -10.67) * mm, v(-16.65, -10.94) * mm]});
            skFitSpline(sketch, "E2383", {"points": [v(-16.65, -10.94) * mm, v(-16.3, -11.14) * mm, v(-16.25, -11.28) * mm, v(-16.3, -11.67) * mm]});
            skFitSpline(sketch, "E2384", {"points": [v(-16.3, -11.67) * mm, v(-16.35, -12.07) * mm, v(-16.37, -12.48) * mm, v(-16.43, -12.88) * mm]});
            skFitSpline(sketch, "E2385", {"points": [v(-16.43, -12.88) * mm, v(-16.5, -13.29) * mm, v(-16.58, -13.7) * mm, v(-16.69, -14.1) * mm]});
            skFitSpline(sketch, "E2386", {"points": [v(-16.69, -14.1) * mm, v(-16.77, -14.42) * mm, v(-17.13, -14.62) * mm, v(-17.47, -14.52) * mm]});
            skFitSpline(sketch, "E2387", {"points": [v(-17.47, -14.52) * mm, v(-17.9, -14.4) * mm, v(-18.34, -14.24) * mm, v(-18.76, -14.08) * mm]});
            skFitSpline(sketch, "E2388", {"points": [v(-18.76, -14.08) * mm, v(-19.13, -13.94) * mm, v(-19.5, -13.76) * mm, v(-19.85, -13.6) * mm]});
            skFitSpline(sketch, "E2389", {"points": [v(-19.85, -13.6) * mm, v(-20.07, -13.5) * mm, v(-20.17, -13.34) * mm, v(-20.17, -13.1) * mm]});
            skFitSpline(sketch, "E2390", {"points": [v(-20.17, -13.1) * mm, v(-20.16, -12.53) * mm, v(-20.17, -11.96) * mm, v(-20.17, -11.38) * mm]});
            skFitSpline(sketch, "E2391", {"points": [v(-20.17, -11.38) * mm, v(-20.17, -11.3) * mm, v(-20.17, -11.22) * mm, v(-20.17, -11.15) * mm]});
            skFitSpline(sketch, "E2392", {"points": [v(-20.17, -11.15) * mm, v(-20.18, -11.14) * mm, v(-20.2, -11.13) * mm, v(-20.21, -11.13) * mm]});
            skFitSpline(sketch, "E2393", {"points": [v(-20.21, -11.13) * mm, v(-20.3, -11.28) * mm, v(-20.38, -11.42) * mm, v(-20.46, -11.57) * mm]});
            skFitSpline(sketch, "E2394", {"points": [v(-20.46, -11.57) * mm, v(-20.6, -11.84) * mm, v(-20.74, -12.11) * mm, v(-20.9, -12.37) * mm]});
            skFitSpline(sketch, "E2395", {"points": [v(-20.9, -12.37) * mm, v(-21.04, -12.63) * mm, v(-21.3, -12.7) * mm, v(-21.55, -12.57) * mm]});
            skFitSpline(sketch, "E2396", {"points": [v(-21.55, -12.57) * mm, v(-21.79, -12.43) * mm, v(-21.87, -12.13) * mm, v(-21.74, -11.88) * mm]});
            skFitSpline(sketch, "E2397", {"points": [v(-21.74, -11.88) * mm, v(-21.47, -11.37) * mm, v(-21.2, -10.87) * mm, v(-20.93, -10.36) * mm]});
            skFitSpline(sketch, "E2398", {"points": [v(-20.93, -10.36) * mm, v(-20.85, -10.2) * mm, v(-20.77, -10.05) * mm, v(-20.67, -9.88) * mm]});
            skFitSpline(sketch, "E2399", {"points": [v(-20.67, -9.88) * mm, v(-20.79, -9.87) * mm, v(-20.88, -9.86) * mm, v(-20.97, -9.86) * mm]});
            skFitSpline(sketch, "E2400", {"points": [v(-20.97, -9.86) * mm, v(-21.53, -9.81) * mm, v(-22.08, -9.76) * mm, v(-22.64, -9.72) * mm]});
            skFitSpline(sketch, "E2401", {"points": [v(-22.64, -9.72) * mm, v(-22.69, -9.72) * mm, v(-22.75, -9.74) * mm, v(-22.8, -9.77) * mm]});
            skFitSpline(sketch, "E2402", {"points": [v(-22.8, -9.77) * mm, v(-23.3, -10.12) * mm, v(-23.8, -10.46) * mm, v(-24.32, -10.81) * mm]});
            skFitSpline(sketch, "E2403", {"points": [v(-24.32, -10.81) * mm, v(-24.34, -10.83) * mm, v(-24.36, -10.85) * mm, v(-24.39, -10.88) * mm]});
            skFitSpline(sketch, "E2404", {"points": [v(-24.39, -10.88) * mm, v(-24.1, -11.06) * mm, v(-23.83, -11.25) * mm, v(-23.55, -11.43) * mm]});
            skFitSpline(sketch, "E2405", {"points": [v(-23.55, -11.43) * mm, v(-23.2, -11.65) * mm, v(-22.84, -11.86) * mm, v(-22.48, -12.08) * mm]});
            skFitSpline(sketch, "E2406", {"points": [v(-22.48, -12.08) * mm, v(-22.24, -12.23) * mm, v(-22.16, -12.53) * mm, v(-22.3, -12.77) * mm]});
            skFitSpline(sketch, "E2407", {"points": [v(-22.3, -12.77) * mm, v(-22.44, -13) * mm, v(-22.72, -13.07) * mm, v(-22.99, -12.92) * mm]});
            skFitSpline(sketch, "E2408", {"points": [v(-22.99, -12.92) * mm, v(-23.25, -12.77) * mm, v(-23.5, -12.6) * mm, v(-23.76, -12.44) * mm]});
            skFitSpline(sketch, "E2409", {"points": [v(-23.76, -12.44) * mm, v(-23.9, -12.36) * mm, v(-24.03, -12.28) * mm, v(-24.16, -12.2) * mm]});
            skFitSpline(sketch, "E2410", {"points": [v(-24.16, -12.2) * mm, v(-24.17, -12.21) * mm, v(-24.18, -12.22) * mm, v(-24.19, -12.23) * mm]});
            skFitSpline(sketch, "E2411", {"points": [v(-58.3, -0.58) * mm, v(-58.67, -0.58) * mm, v(-58.98, -0.58) * mm, v(-59.3, -0.58) * mm]});
            skFitSpline(sketch, "E2412", {"points": [v(-59.3, -0.58) * mm, v(-59.74, -0.58) * mm, v(-60.18, -0.6) * mm, v(-60.61, -0.6) * mm]});
            skFitSpline(sketch, "E2413", {"points": [v(-60.61, -0.6) * mm, v(-60.9, -0.59) * mm, v(-61.17, -0.56) * mm, v(-61.45, -0.56) * mm]});
            skFitSpline(sketch, "E2414", {"points": [v(-61.45, -0.56) * mm, v(-62, -0.55) * mm, v(-62.53, -0.55) * mm, v(-63.08, -0.55) * mm]});
            skFitSpline(sketch, "E2415", {"points": [v(-63.08, -0.55) * mm, v(-63.23, -0.55) * mm, v(-63.38, -0.55) * mm, v(-63.53, -0.56) * mm]});
            skFitSpline(sketch, "E2416", {"points": [v(-63.53, -0.56) * mm, v(-63.7, -0.57) * mm, v(-63.86, -0.8) * mm, v(-63.86, -0.97) * mm]});
            skFitSpline(sketch, "E2417", {"points": [v(-63.86, -0.97) * mm, v(-63.86, -1.2) * mm, v(-63.75, -1.3) * mm, v(-63.57, -1.4) * mm]});
            skFitSpline(sketch, "E2418", {"points": [v(-63.57, -1.4) * mm, v(-63.5, -1.43) * mm, v(-63.43, -1.46) * mm, v(-63.36, -1.5) * mm]});
            skFitSpline(sketch, "E2419", {"points": [v(-63.36, -1.5) * mm, v(-62.76, -1.84) * mm, v(-62.17, -2.18) * mm, v(-61.57, -2.51) * mm]});
            skFitSpline(sketch, "E2420", {"points": [v(-61.57, -2.51) * mm, v(-61.4, -2.61) * mm, v(-61.21, -2.7) * mm, v(-61.04, -2.8) * mm]});
            skFitSpline(sketch, "E2421", {"points": [v(-61.04, -2.8) * mm, v(-60.52, -3.1) * mm, v(-60, -3.42) * mm, v(-59.48, -3.73) * mm]});
            skFitSpline(sketch, "E2422", {"points": [v(-59.48, -3.73) * mm, v(-59.4, -3.78) * mm, v(-59.3, -3.82) * mm, v(-59.19, -3.89) * mm]});
            skFitSpline(sketch, "E2423", {"points": [v(-59.19, -3.89) * mm, v(-59.26, -3.44) * mm, v(-59.31, -3.05) * mm, v(-59.4, -2.66) * mm]});
            skFitSpline(sketch, "E2424", {"points": [v(-59.4, -2.66) * mm, v(-59.48, -2.24) * mm, v(-59.38, -1.88) * mm, v(-59.1, -1.55) * mm]});
            skFitSpline(sketch, "E2425", {"points": [v(-59.1, -1.55) * mm, v(-58.84, -1.24) * mm, v(-58.59, -0.92) * mm, v(-58.3, -0.58) * mm]});
            skFitSpline(sketch, "E2426", {"points": [v(-74.95, -3.86) * mm, v(-73.4, -2.98) * mm, v(-71.86, -2.11) * mm, v(-70.34, -1.25) * mm]});
            skFitSpline(sketch, "E2427", {"points": [v(-70.34, -1.25) * mm, v(-70.32, -1.15) * mm, v(-70.3, -1.08) * mm, v(-70.28, -1) * mm]});
            skFitSpline(sketch, "E2428", {"points": [v(-70.28, -1) * mm, v(-70.26, -0.9) * mm, v(-70.3, -0.84) * mm, v(-70.34, -0.76) * mm]});
            skFitSpline(sketch, "E2429", {"points": [v(-70.34, -0.76) * mm, v(-70.44, -0.58) * mm, v(-70.6, -0.53) * mm, v(-70.78, -0.54) * mm]});
            skFitSpline(sketch, "E2430", {"points": [v(-70.78, -0.54) * mm, v(-71.27, -0.54) * mm, v(-71.75, -0.55) * mm, v(-72.24, -0.55) * mm]});
            skFitSpline(sketch, "E2431", {"points": [v(-72.24, -0.55) * mm, v(-72.76, -0.56) * mm, v(-73.28, -0.58) * mm, v(-73.8, -0.58) * mm]});
            skFitSpline(sketch, "E2432", {"points": [v(-73.8, -0.58) * mm, v(-74.35, -0.58) * mm, v(-74.9, -0.56) * mm, v(-75.47, -0.56) * mm]});
            skFitSpline(sketch, "E2433", {"points": [v(-75.47, -0.56) * mm, v(-75.58, -0.56) * mm, v(-75.7, -0.53) * mm, v(-75.82, -0.6) * mm]});
            skFitSpline(sketch, "E2434", {"points": [v(-75.82, -0.6) * mm, v(-75.78, -0.65) * mm, v(-75.75, -0.69) * mm, v(-75.72, -0.72) * mm]});
            skFitSpline(sketch, "E2435", {"points": [v(-75.72, -0.72) * mm, v(-75.5, -1) * mm, v(-75.27, -1.28) * mm, v(-75.03, -1.55) * mm]});
            skFitSpline(sketch, "E2436", {"points": [v(-75.03, -1.55) * mm, v(-74.82, -1.8) * mm, v(-74.7, -2.1) * mm, v(-74.73, -2.43) * mm]});
            skFitSpline(sketch, "E2437", {"points": [v(-74.73, -2.43) * mm, v(-74.76, -2.68) * mm, v(-74.8, -2.92) * mm, v(-74.84, -3.16) * mm]});
            skFitSpline(sketch, "E2438", {"points": [v(-74.84, -3.16) * mm, v(-74.87, -3.4) * mm, v(-74.9, -3.62) * mm, v(-74.95, -3.86) * mm]});
            skFitSpline(sketch, "E2439", {"points": [v(-67.63, 8.79) * mm, v(-68, 8.48) * mm, v(-68.32, 8.22) * mm, v(-68.64, 7.95) * mm]});
            skFitSpline(sketch, "E2440", {"points": [v(-68.64, 7.95) * mm, v(-68.92, 7.7) * mm, v(-69.25, 7.6) * mm, v(-69.62, 7.66) * mm]});
            skFitSpline(sketch, "E2441", {"points": [v(-69.62, 7.66) * mm, v(-69.82, 7.69) * mm, v(-70.03, 7.74) * mm, v(-70.23, 7.77) * mm]});
            skFitSpline(sketch, "E2442", {"points": [v(-70.23, 7.77) * mm, v(-70.46, 7.8) * mm, v(-70.69, 7.84) * mm, v(-70.96, 7.88) * mm]});
            skFitSpline(sketch, "E2443", {"points": [v(-70.96, 7.88) * mm, v(-70.86, 7.7) * mm, v(-70.8, 7.58) * mm, v(-70.72, 7.46) * mm]});
            skFitSpline(sketch, "E2444", {"points": [v(-70.72, 7.46) * mm, v(-70.1, 6.54) * mm, v(-69.63, 5.53) * mm, v(-69.07, 4.57) * mm]});
            skFitSpline(sketch, "E2445", {"points": [v(-69.07, 4.57) * mm, v(-68.84, 4.17) * mm, v(-68.61, 3.77) * mm, v(-68.38, 3.37) * mm]});
            skFitSpline(sketch, "E2446", {"points": [v(-68.38, 3.37) * mm, v(-68.28, 3.2) * mm, v(-68, 3.17) * mm, v(-67.83, 3.27) * mm]});
            skFitSpline(sketch, "E2447", {"points": [v(-67.83, 3.27) * mm, v(-67.64, 3.37) * mm, v(-67.6, 3.54) * mm, v(-67.61, 3.73) * mm]});
            skFitSpline(sketch, "E2448", {"points": [v(-67.61, 3.73) * mm, v(-67.61, 4.3) * mm, v(-67.62, 4.89) * mm, v(-67.63, 5.47) * mm]});
            skFitSpline(sketch, "E2449", {"points": [v(-67.63, 5.47) * mm, v(-67.63, 5.88) * mm, v(-67.61, 6.3) * mm, v(-67.65, 6.7) * mm]});
            skFitSpline(sketch, "E2450", {"points": [v(-67.65, 6.7) * mm, v(-67.7, 7.27) * mm, v(-67.63, 7.82) * mm, v(-67.63, 8.38) * mm]});
            skFitSpline(sketch, "E2451", {"points": [v(-67.63, 8.38) * mm, v(-67.63, 8.5) * mm, v(-67.63, 8.61) * mm, v(-67.63, 8.79) * mm]});
            skFitSpline(sketch, "E2452", {"points": [v(-74.38, 4.88) * mm, v(-74.25, 4.8) * mm, v(-74.15, 4.74) * mm, v(-74.05, 4.69) * mm]});
            skFitSpline(sketch, "E2453", {"points": [v(-74.05, 4.69) * mm, v(-73.02, 4.17) * mm, v(-72.06, 3.52) * mm, v(-71.06, 2.94) * mm]});
            skFitSpline(sketch, "E2454", {"points": [v(-71.06, 2.94) * mm, v(-70.7, 2.73) * mm, v(-70.34, 2.52) * mm, v(-69.99, 2.31) * mm]});
            skFitSpline(sketch, "E2455", {"points": [v(-69.99, 2.31) * mm, v(-69.85, 2.23) * mm, v(-69.73, 2.19) * mm, v(-69.56, 2.27) * mm]});
            skFitSpline(sketch, "E2456", {"points": [v(-69.56, 2.27) * mm, v(-69.34, 2.4) * mm, v(-69.23, 2.63) * mm, v(-69.36, 2.86) * mm]});
            skFitSpline(sketch, "E2457", {"points": [v(-69.36, 2.86) * mm, v(-69.54, 3.18) * mm, v(-69.72, 3.5) * mm, v(-69.92, 3.83) * mm]});
            skFitSpline(sketch, "E2458", {"points": [v(-69.92, 3.83) * mm, v(-70.25, 4.4) * mm, v(-70.6, 4.94) * mm, v(-70.93, 5.5) * mm]});
            skFitSpline(sketch, "E2459", {"points": [v(-70.93, 5.5) * mm, v(-71.23, 6.01) * mm, v(-71.5, 6.53) * mm, v(-71.79, 7.03) * mm]});
            skFitSpline(sketch, "E2460", {"points": [v(-71.79, 7.03) * mm, v(-71.83, 7.11) * mm, v(-71.88, 7.2) * mm, v(-71.95, 7.3) * mm]});
            skFitSpline(sketch, "E2461", {"points": [v(-71.95, 7.3) * mm, v(-71.99, 7.2) * mm, v(-72.01, 7.16) * mm, v(-72.03, 7.11) * mm]});
            skFitSpline(sketch, "E2462", {"points": [v(-72.03, 7.11) * mm, v(-72.15, 6.78) * mm, v(-72.28, 6.46) * mm, v(-72.4, 6.12) * mm]});
            skFitSpline(sketch, "E2463", {"points": [v(-72.4, 6.12) * mm, v(-72.53, 5.73) * mm, v(-72.8, 5.47) * mm, v(-73.2, 5.33) * mm]});
            skFitSpline(sketch, "E2464", {"points": [v(-73.2, 5.33) * mm, v(-73.58, 5.2) * mm, v(-73.95, 5.04) * mm, v(-74.38, 4.88) * mm]});
            skFitSpline(sketch, "E2465", {"points": [v(-67.65, -8.77) * mm, v(-67.65, -8.41) * mm, v(-67.65, -8.1) * mm, v(-67.65, -7.78) * mm]});
            skFitSpline(sketch, "E2466", {"points": [v(-67.65, -7.78) * mm, v(-67.65, -7.34) * mm, v(-67.67, -6.9) * mm, v(-67.67, -6.47) * mm]});
            skFitSpline(sketch, "E2467", {"points": [v(-67.67, -6.47) * mm, v(-67.67, -6.18) * mm, v(-67.63, -5.9) * mm, v(-67.63, -5.61) * mm]});
            skFitSpline(sketch, "E2468", {"points": [v(-67.63, -5.61) * mm, v(-67.62, -4.98) * mm, v(-67.61, -4.35) * mm, v(-67.61, -3.72) * mm]});
            skFitSpline(sketch, "E2469", {"points": [v(-67.61, -3.72) * mm, v(-67.61, -3.62) * mm, v(-67.6, -3.5) * mm, v(-67.66, -3.42) * mm]});
            skFitSpline(sketch, "E2470", {"points": [v(-67.66, -3.42) * mm, v(-67.85, -3.15) * mm, v(-68.26, -3.12) * mm, v(-68.42, -3.43) * mm]});
            skFitSpline(sketch, "E2471", {"points": [v(-68.42, -3.43) * mm, v(-68.6, -3.75) * mm, v(-68.79, -4.06) * mm, v(-68.97, -4.38) * mm]});
            skFitSpline(sketch, "E2472", {"points": [v(-68.97, -4.38) * mm, v(-69.29, -4.96) * mm, v(-69.6, -5.55) * mm, v(-69.93, -6.12) * mm]});
            skFitSpline(sketch, "E2473", {"points": [v(-69.93, -6.12) * mm, v(-70.2, -6.62) * mm, v(-70.51, -7.1) * mm, v(-70.8, -7.6) * mm]});
            skFitSpline(sketch, "E2474", {"points": [v(-70.8, -7.6) * mm, v(-70.85, -7.68) * mm, v(-70.9, -7.76) * mm, v(-70.95, -7.87) * mm]});
            skFitSpline(sketch, "E2475", {"points": [v(-70.95, -7.87) * mm, v(-70.86, -7.86) * mm, v(-70.8, -7.86) * mm, v(-70.75, -7.85) * mm]});
            skFitSpline(sketch, "E2476", {"points": [v(-70.75, -7.85) * mm, v(-70.41, -7.8) * mm, v(-70.07, -7.74) * mm, v(-69.73, -7.68) * mm]});
            skFitSpline(sketch, "E2477", {"points": [v(-69.73, -7.68) * mm, v(-69.3, -7.6) * mm, v(-68.93, -7.69) * mm, v(-68.6, -7.98) * mm]});
            skFitSpline(sketch, "E2478", {"points": [v(-68.6, -7.98) * mm, v(-68.3, -8.24) * mm, v(-67.99, -8.5) * mm, v(-67.65, -8.77) * mm]});
            skFitSpline(sketch, "E2479", {"points": [v(-62.2, 7.32) * mm, v(-62.28, 7.17) * mm, v(-62.34, 7.08) * mm, v(-62.39, 6.98) * mm]});
            skFitSpline(sketch, "E2480", {"points": [v(-62.39, 6.98) * mm, v(-62.9, 5.94) * mm, v(-63.56, 4.98) * mm, v(-64.14, 3.98) * mm]});
            skFitSpline(sketch, "E2481", {"points": [v(-64.14, 3.98) * mm, v(-64.34, 3.62) * mm, v(-64.56, 3.26) * mm, v(-64.76, 2.9) * mm]});
            skFitSpline(sketch, "E2482", {"points": [v(-64.76, 2.9) * mm, v(-64.8, 2.83) * mm, v(-64.86, 2.74) * mm, v(-64.85, 2.66) * mm]});
            skFitSpline(sketch, "E2483", {"points": [v(-64.85, 2.66) * mm, v(-64.82, 2.34) * mm, v(-64.47, 2.1) * mm, v(-64.18, 2.3) * mm]});
            skFitSpline(sketch, "E2484", {"points": [v(-64.18, 2.3) * mm, v(-63.87, 2.5) * mm, v(-63.54, 2.66) * mm, v(-63.23, 2.85) * mm]});
            skFitSpline(sketch, "E2485", {"points": [v(-63.23, 2.85) * mm, v(-62.68, 3.19) * mm, v(-62.13, 3.53) * mm, v(-61.57, 3.86) * mm]});
            skFitSpline(sketch, "E2486", {"points": [v(-61.57, 3.86) * mm, v(-61.07, 4.15) * mm, v(-60.55, 4.43) * mm, v(-60.05, 4.71) * mm]});
            skFitSpline(sketch, "E2487", {"points": [v(-60.05, 4.71) * mm, v(-59.96, 4.76) * mm, v(-59.88, 4.81) * mm, v(-59.76, 4.88) * mm]});
            skFitSpline(sketch, "E2488", {"points": [v(-59.76, 4.88) * mm, v(-60.19, 5.04) * mm, v(-60.56, 5.2) * mm, v(-60.95, 5.33) * mm]});
            skFitSpline(sketch, "E2489", {"points": [v(-60.95, 5.33) * mm, v(-61.34, 5.47) * mm, v(-61.6, 5.73) * mm, v(-61.74, 6.13) * mm]});
            skFitSpline(sketch, "E2490", {"points": [v(-61.74, 6.13) * mm, v(-61.88, 6.5) * mm, v(-62.03, 6.89) * mm, v(-62.2, 7.32) * mm]});
            skFitSpline(sketch, "E2491", {"points": [v(-71.95, -7.3) * mm, v(-71.87, -7.18) * mm, v(-71.82, -7.1) * mm, v(-71.77, -7) * mm]});
            skFitSpline(sketch, "E2492", {"points": [v(-71.77, -7) * mm, v(-71.24, -5.94) * mm, v(-70.57, -4.95) * mm, v(-69.97, -3.92) * mm]});
            skFitSpline(sketch, "E2493", {"points": [v(-69.97, -3.92) * mm, v(-69.78, -3.59) * mm, v(-69.58, -3.25) * mm, v(-69.38, -2.91) * mm]});
            skFitSpline(sketch, "E2494", {"points": [v(-69.38, -2.91) * mm, v(-69.3, -2.78) * mm, v(-69.26, -2.65) * mm, v(-69.35, -2.5) * mm]});
            skFitSpline(sketch, "E2495", {"points": [v(-69.35, -2.5) * mm, v(-69.47, -2.26) * mm, v(-69.7, -2.16) * mm, v(-69.93, -2.29) * mm]});
            skFitSpline(sketch, "E2496", {"points": [v(-69.93, -2.29) * mm, v(-70.26, -2.47) * mm, v(-70.58, -2.65) * mm, v(-70.9, -2.84) * mm]});
            skFitSpline(sketch, "E2497", {"points": [v(-70.9, -2.84) * mm, v(-71.46, -3.18) * mm, v(-72.02, -3.53) * mm, v(-72.58, -3.86) * mm]});
            skFitSpline(sketch, "E2498", {"points": [v(-72.58, -3.86) * mm, v(-73.05, -4.14) * mm, v(-73.53, -4.4) * mm, v(-74, -4.66) * mm]});
            skFitSpline(sketch, "E2499", {"points": [v(-74, -4.66) * mm, v(-74.12, -4.72) * mm, v(-74.23, -4.8) * mm, v(-74.37, -4.87) * mm]});
            skFitSpline(sketch, "E2500", {"points": [v(-74.37, -4.87) * mm, v(-74.28, -4.92) * mm, v(-74.21, -4.95) * mm, v(-74.15, -4.97) * mm]});
            skFitSpline(sketch, "E2501", {"points": [v(-74.15, -4.97) * mm, v(-73.82, -5.1) * mm, v(-73.5, -5.22) * mm, v(-73.16, -5.34) * mm]});
            skFitSpline(sketch, "E2502", {"points": [v(-73.16, -5.34) * mm, v(-72.82, -5.46) * mm, v(-72.57, -5.68) * mm, v(-72.44, -6.02) * mm]});
            skFitSpline(sketch, "E2503", {"points": [v(-72.44, -6.02) * mm, v(-72.37, -6.2) * mm, v(-72.3, -6.38) * mm, v(-72.24, -6.56) * mm]});
            skFitSpline(sketch, "E2504", {"points": [v(-72.24, -6.56) * mm, v(-72.15, -6.8) * mm, v(-72.06, -7.03) * mm, v(-71.95, -7.3) * mm]});
            skFitSpline(sketch, "E2505", {"points": [v(-59.76, -4.88) * mm, v(-59.89, -4.8) * mm, v(-59.97, -4.75) * mm, v(-60.05, -4.7) * mm]});
            skFitSpline(sketch, "E2506", {"points": [v(-60.05, -4.7) * mm, v(-60.53, -4.44) * mm, v(-61, -4.2) * mm, v(-61.47, -3.91) * mm]});
            skFitSpline(sketch, "E2507", {"points": [v(-61.47, -3.91) * mm, v(-62.1, -3.55) * mm, v(-62.7, -3.17) * mm, v(-63.32, -2.8) * mm]});
            skFitSpline(sketch, "E2508", {"points": [v(-63.32, -2.8) * mm, v(-63.6, -2.62) * mm, v(-63.9, -2.46) * mm, v(-64.19, -2.3) * mm]});
            skFitSpline(sketch, "E2509", {"points": [v(-64.19, -2.3) * mm, v(-64.26, -2.26) * mm, v(-64.34, -2.2) * mm, v(-64.4, -2.22) * mm]});
            skFitSpline(sketch, "E2510", {"points": [v(-64.4, -2.22) * mm, v(-64.74, -2.26) * mm, v(-64.97, -2.6) * mm, v(-64.78, -2.9) * mm]});
            skFitSpline(sketch, "E2511", {"points": [v(-64.78, -2.9) * mm, v(-64.58, -3.2) * mm, v(-64.42, -3.51) * mm, v(-64.23, -3.82) * mm]});
            skFitSpline(sketch, "E2512", {"points": [v(-64.23, -3.82) * mm, v(-63.9, -4.38) * mm, v(-63.55, -4.94) * mm, v(-63.22, -5.5) * mm]});
            skFitSpline(sketch, "E2513", {"points": [v(-63.22, -5.5) * mm, v(-62.92, -6.01) * mm, v(-62.64, -6.53) * mm, v(-62.35, -7.05) * mm]});
            skFitSpline(sketch, "E2514", {"points": [v(-62.35, -7.05) * mm, v(-62.3, -7.12) * mm, v(-62.25, -7.2) * mm, v(-62.19, -7.3) * mm]});
            skFitSpline(sketch, "E2515", {"points": [v(-62.19, -7.3) * mm, v(-62.02, -6.87) * mm, v(-61.88, -6.49) * mm, v(-61.73, -6.1) * mm]});
            skFitSpline(sketch, "E2516", {"points": [v(-61.73, -6.1) * mm, v(-61.6, -5.75) * mm, v(-61.38, -5.5) * mm, v(-61.03, -5.36) * mm]});
            skFitSpline(sketch, "E2517", {"points": [v(-61.03, -5.36) * mm, v(-60.85, -5.3) * mm, v(-60.67, -5.23) * mm, v(-60.5, -5.16) * mm]});
            skFitSpline(sketch, "E2518", {"points": [v(-60.5, -5.16) * mm, v(-60.26, -5.07) * mm, v(-60.03, -4.98) * mm, v(-59.76, -4.88) * mm]});
            skFitSpline(sketch, "E2519", {"points": [v(-66.52, 8.79) * mm, v(-66.52, 8.62) * mm, v(-66.53, 8.5) * mm, v(-66.52, 8.38) * mm]});
            skFitSpline(sketch, "E2520", {"points": [v(-66.52, 8.38) * mm, v(-66.5, 8) * mm, v(-66.48, 7.62) * mm, v(-66.48, 7.24) * mm]});
            skFitSpline(sketch, "E2521", {"points": [v(-66.48, 7.24) * mm, v(-66.48, 6.4) * mm, v(-66.51, 5.56) * mm, v(-66.52, 4.73) * mm]});
            skFitSpline(sketch, "E2522", {"points": [v(-66.52, 4.73) * mm, v(-66.53, 4.34) * mm, v(-66.53, 3.96) * mm, v(-66.52, 3.58) * mm]});
            skFitSpline(sketch, "E2523", {"points": [v(-66.52, 3.58) * mm, v(-66.52, 3.52) * mm, v(-66.52, 3.46) * mm, v(-66.49, 3.42) * mm]});
            skFitSpline(sketch, "E2524", {"points": [v(-66.49, 3.42) * mm, v(-66.27, 3.15) * mm, v(-65.88, 3.11) * mm, v(-65.7, 3.45) * mm]});
            skFitSpline(sketch, "E2525", {"points": [v(-65.7, 3.45) * mm, v(-65.54, 3.77) * mm, v(-65.35, 4.07) * mm, v(-65.18, 4.38) * mm]});
            skFitSpline(sketch, "E2526", {"points": [v(-65.18, 4.38) * mm, v(-64.85, 4.96) * mm, v(-64.55, 5.55) * mm, v(-64.22, 6.12) * mm]});
            skFitSpline(sketch, "E2527", {"points": [v(-64.22, 6.12) * mm, v(-63.93, 6.62) * mm, v(-63.63, 7.11) * mm, v(-63.34, 7.6) * mm]});
            skFitSpline(sketch, "E2528", {"points": [v(-63.34, 7.6) * mm, v(-63.29, 7.68) * mm, v(-63.25, 7.76) * mm, v(-63.2, 7.87) * mm]});
            skFitSpline(sketch, "E2529", {"points": [v(-63.2, 7.87) * mm, v(-63.28, 7.86) * mm, v(-63.33, 7.86) * mm, v(-63.38, 7.85) * mm]});
            skFitSpline(sketch, "E2530", {"points": [v(-63.38, 7.85) * mm, v(-63.75, 7.8) * mm, v(-64.12, 7.73) * mm, v(-64.49, 7.67) * mm]});
            skFitSpline(sketch, "E2531", {"points": [v(-64.49, 7.67) * mm, v(-64.84, 7.6) * mm, v(-65.17, 7.68) * mm, v(-65.45, 7.91) * mm]});
            skFitSpline(sketch, "E2532", {"points": [v(-65.45, 7.91) * mm, v(-65.6, 8.03) * mm, v(-65.74, 8.16) * mm, v(-65.9, 8.28) * mm]});
            skFitSpline(sketch, "E2533", {"points": [v(-65.9, 8.28) * mm, v(-66.09, 8.44) * mm, v(-66.28, 8.6) * mm, v(-66.52, 8.79) * mm]});
            skFitSpline(sketch, "E2534", {"points": [v(-63.24, -7.87) * mm, v(-63.23, -7.86) * mm, v(-63.22, -7.84) * mm, v(-63.2, -7.83) * mm]});
            skFitSpline(sketch, "E2535", {"points": [v(-63.2, -7.83) * mm, v(-63.28, -7.7) * mm, v(-63.34, -7.58) * mm, v(-63.42, -7.46) * mm]});
            skFitSpline(sketch, "E2536", {"points": [v(-63.42, -7.46) * mm, v(-64.04, -6.54) * mm, v(-64.51, -5.53) * mm, v(-65.07, -4.57) * mm]});
            skFitSpline(sketch, "E2537", {"points": [v(-65.07, -4.57) * mm, v(-65.3, -4.2) * mm, v(-65.5, -3.8) * mm, v(-65.72, -3.43) * mm]});
            skFitSpline(sketch, "E2538", {"points": [v(-65.72, -3.43) * mm, v(-65.87, -3.18) * mm, v(-66.13, -3.15) * mm, v(-66.37, -3.31) * mm]});
            skFitSpline(sketch, "E2539", {"points": [v(-66.37, -3.31) * mm, v(-66.53, -3.41) * mm, v(-66.53, -3.55) * mm, v(-66.53, -3.7) * mm]});
            skFitSpline(sketch, "E2540", {"points": [v(-66.53, -3.7) * mm, v(-66.53, -4.38) * mm, v(-66.53, -5.06) * mm, v(-66.52, -5.74) * mm]});
            skFitSpline(sketch, "E2541", {"points": [v(-66.52, -5.74) * mm, v(-66.52, -6.1) * mm, v(-66.48, -6.46) * mm, v(-66.48, -6.81) * mm]});
            skFitSpline(sketch, "E2542", {"points": [v(-66.48, -6.81) * mm, v(-66.48, -7.32) * mm, v(-66.5, -7.83) * mm, v(-66.52, -8.35) * mm]});
            skFitSpline(sketch, "E2543", {"points": [v(-66.52, -8.35) * mm, v(-66.52, -8.48) * mm, v(-66.52, -8.6) * mm, v(-66.52, -8.78) * mm]});
            skFitSpline(sketch, "E2544", {"points": [v(-66.52, -8.78) * mm, v(-66.41, -8.7) * mm, v(-66.35, -8.65) * mm, v(-66.3, -8.6) * mm]});
            skFitSpline(sketch, "E2545", {"points": [v(-66.3, -8.6) * mm, v(-66.03, -8.39) * mm, v(-65.76, -8.17) * mm, v(-65.5, -7.95) * mm]});
            skFitSpline(sketch, "E2546", {"points": [v(-65.5, -7.95) * mm, v(-65.21, -7.7) * mm, v(-64.88, -7.62) * mm, v(-64.52, -7.66) * mm]});
            skFitSpline(sketch, "E2547", {"points": [v(-64.52, -7.66) * mm, v(-64.32, -7.69) * mm, v(-64.12, -7.73) * mm, v(-63.93, -7.77) * mm]});
            skFitSpline(sketch, "E2548", {"points": [v(-63.93, -7.77) * mm, v(-63.7, -7.8) * mm, v(-63.47, -7.84) * mm, v(-63.24, -7.87) * mm]});
            skFitSpline(sketch, "E2549", {"points": [v(-58.29, 0.55) * mm, v(-58.38, 0.67) * mm, v(-58.43, 0.74) * mm, v(-58.48, 0.8) * mm]});
            skFitSpline(sketch, "E2550", {"points": [v(-58.48, 0.8) * mm, v(-58.7, 1.06) * mm, v(-58.9, 1.32) * mm, v(-59.13, 1.58) * mm]});
            skFitSpline(sketch, "E2551", {"points": [v(-59.13, 1.58) * mm, v(-59.36, 1.85) * mm, v(-59.46, 2.17) * mm, v(-59.42, 2.53) * mm]});
            skFitSpline(sketch, "E2552", {"points": [v(-59.42, 2.53) * mm, v(-59.4, 2.74) * mm, v(-59.34, 2.94) * mm, v(-59.3, 3.14) * mm]});
            skFitSpline(sketch, "E2553", {"points": [v(-59.3, 3.14) * mm, v(-59.27, 3.37) * mm, v(-59.23, 3.6) * mm, v(-59.19, 3.89) * mm]});
            skFitSpline(sketch, "E2554", {"points": [v(-59.19, 3.89) * mm, v(-59.34, 3.8) * mm, v(-59.46, 3.75) * mm, v(-59.57, 3.67) * mm]});
            skFitSpline(sketch, "E2555", {"points": [v(-59.57, 3.67) * mm, v(-60.5, 3.04) * mm, v(-61.53, 2.56) * mm, v(-62.5, 2) * mm]});
            skFitSpline(sketch, "E2556", {"points": [v(-62.5, 2) * mm, v(-62.9, 1.77) * mm, v(-63.3, 1.54) * mm, v(-63.7, 1.3) * mm]});
            skFitSpline(sketch, "E2557", {"points": [v(-63.7, 1.3) * mm, v(-63.86, 1.2) * mm, v(-63.9, 0.92) * mm, v(-63.8, 0.77) * mm]});
            skFitSpline(sketch, "E2558", {"points": [v(-63.8, 0.77) * mm, v(-63.7, 0.58) * mm, v(-63.55, 0.53) * mm, v(-63.35, 0.54) * mm]});
            skFitSpline(sketch, "E2559", {"points": [v(-63.35, 0.54) * mm, v(-62.71, 0.54) * mm, v(-62.07, 0.54) * mm, v(-61.44, 0.55) * mm]});
            skFitSpline(sketch, "E2560", {"points": [v(-61.44, 0.55) * mm, v(-61.08, 0.55) * mm, v(-60.72, 0.58) * mm, v(-60.36, 0.58) * mm]});
            skFitSpline(sketch, "E2561", {"points": [v(-60.36, 0.58) * mm, v(-59.8, 0.58) * mm, v(-59.26, 0.56) * mm, v(-58.71, 0.55) * mm]});
            skFitSpline(sketch, "E2562", {"points": [v(-58.71, 0.55) * mm, v(-58.59, 0.55) * mm, v(-58.46, 0.55) * mm, v(-58.29, 0.55) * mm]});
            skFitSpline(sketch, "E2563", {"points": [v(-75.86, 0.55) * mm, v(-75.7, 0.55) * mm, v(-75.58, 0.55) * mm, v(-75.47, 0.55) * mm]});
            skFitSpline(sketch, "E2564", {"points": [v(-75.47, 0.55) * mm, v(-75.06, 0.57) * mm, v(-74.65, 0.6) * mm, v(-74.23, 0.6) * mm]});
            skFitSpline(sketch, "E2565", {"points": [v(-74.23, 0.6) * mm, v(-73.5, 0.59) * mm, v(-72.75, 0.57) * mm, v(-72, 0.55) * mm]});
            skFitSpline(sketch, "E2566", {"points": [v(-72, 0.55) * mm, v(-71.93, 0.55) * mm, v(-71.85, 0.54) * mm, v(-71.77, 0.54) * mm]});
            skFitSpline(sketch, "E2567", {"points": [v(-71.77, 0.54) * mm, v(-71.4, 0.54) * mm, v(-71.04, 0.54) * mm, v(-70.67, 0.55) * mm]});
            skFitSpline(sketch, "E2568", {"points": [v(-70.67, 0.55) * mm, v(-70.6, 0.55) * mm, v(-70.52, 0.55) * mm, v(-70.5, 0.59) * mm]});
            skFitSpline(sketch, "E2569", {"points": [v(-70.5, 0.59) * mm, v(-70.38, 0.72) * mm, v(-70.23, 0.84) * mm, v(-70.3, 1.06) * mm]});
            skFitSpline(sketch, "E2570", {"points": [v(-70.3, 1.06) * mm, v(-70.33, 1.19) * mm, v(-70.37, 1.28) * mm, v(-70.48, 1.34) * mm]});
            skFitSpline(sketch, "E2571", {"points": [v(-70.48, 1.34) * mm, v(-70.58, 1.4) * mm, v(-70.68, 1.44) * mm, v(-70.78, 1.5) * mm]});
            skFitSpline(sketch, "E2572", {"points": [v(-70.78, 1.5) * mm, v(-71.38, 1.84) * mm, v(-71.98, 2.18) * mm, v(-72.59, 2.52) * mm]});
            skFitSpline(sketch, "E2573", {"points": [v(-72.59, 2.52) * mm, v(-72.76, 2.62) * mm, v(-72.94, 2.7) * mm, v(-73.11, 2.8) * mm]});
            skFitSpline(sketch, "E2574", {"points": [v(-73.11, 2.8) * mm, v(-73.63, 3.1) * mm, v(-74.14, 3.42) * mm, v(-74.65, 3.72) * mm]});
            skFitSpline(sketch, "E2575", {"points": [v(-74.65, 3.72) * mm, v(-74.74, 3.77) * mm, v(-74.83, 3.82) * mm, v(-74.94, 3.88) * mm]});
            skFitSpline(sketch, "E2576", {"points": [v(-74.94, 3.88) * mm, v(-74.93, 3.78) * mm, v(-74.93, 3.71) * mm, v(-74.92, 3.65) * mm]});
            skFitSpline(sketch, "E2577", {"points": [v(-74.92, 3.65) * mm, v(-74.86, 3.31) * mm, v(-74.8, 2.98) * mm, v(-74.75, 2.64) * mm]});
            skFitSpline(sketch, "E2578", {"points": [v(-74.75, 2.64) * mm, v(-74.69, 2.27) * mm, v(-74.73, 1.92) * mm, v(-74.98, 1.62) * mm]});
            skFitSpline(sketch, "E2579", {"points": [v(-74.98, 1.62) * mm, v(-75.1, 1.48) * mm, v(-75.21, 1.34) * mm, v(-75.33, 1.2) * mm]});
            skFitSpline(sketch, "E2580", {"points": [v(-75.33, 1.2) * mm, v(-75.5, 1) * mm, v(-75.66, 0.8) * mm, v(-75.86, 0.55) * mm]});
            skFitSpline(sketch, "E2581", {"points": [v(-66.59, -12.92) * mm, v(-66.59, -13.08) * mm, v(-66.59, -13.25) * mm, v(-66.59, -13.4) * mm]});
            skFitSpline(sketch, "E2582", {"points": [v(-66.59, -13.4) * mm, v(-66.58, -13.63) * mm, v(-66.58, -13.86) * mm, v(-66.57, -14.08) * mm]});
            skFitSpline(sketch, "E2583", {"points": [v(-66.57, -14.08) * mm, v(-66.55, -14.45) * mm, v(-66.51, -14.81) * mm, v(-66.5, -15.18) * mm]});
            skFitSpline(sketch, "E2584", {"points": [v(-66.5, -15.18) * mm, v(-66.5, -15.28) * mm, v(-66.45, -15.36) * mm, v(-66.37, -15.42) * mm]});
            skFitSpline(sketch, "E2585", {"points": [v(-66.37, -15.42) * mm, v(-65.98, -15.75) * mm, v(-65.58, -16.07) * mm, v(-65.18, -16.39) * mm]});
            skFitSpline(sketch, "E2586", {"points": [v(-65.18, -16.39) * mm, v(-65.1, -16.45) * mm, v(-65.02, -16.5) * mm, v(-64.95, -16.56) * mm]});
            skFitSpline(sketch, "E2587", {"points": [v(-64.95, -16.56) * mm, v(-64.74, -16.74) * mm, v(-64.7, -17.01) * mm, v(-64.86, -17.22) * mm]});
            skFitSpline(sketch, "E2588", {"points": [v(-64.86, -17.22) * mm, v(-65.02, -17.43) * mm, v(-65.3, -17.49) * mm, v(-65.53, -17.33) * mm]});
            skFitSpline(sketch, "E2589", {"points": [v(-65.53, -17.33) * mm, v(-65.78, -17.17) * mm, v(-66.02, -16.98) * mm, v(-66.26, -16.8) * mm]});
            skFitSpline(sketch, "E2590", {"points": [v(-66.26, -16.8) * mm, v(-66.53, -16.58) * mm, v(-66.8, -16.35) * mm, v(-67.07, -16.12) * mm]});
            skFitSpline(sketch, "E2591", {"points": [v(-67.07, -16.12) * mm, v(-67.34, -16.35) * mm, v(-67.6, -16.57) * mm, v(-67.87, -16.79) * mm]});
            skFitSpline(sketch, "E2592", {"points": [v(-67.87, -16.79) * mm, v(-68.1, -16.97) * mm, v(-68.34, -17.15) * mm, v(-68.58, -17.32) * mm]});
            skFitSpline(sketch, "E2593", {"points": [v(-68.58, -17.32) * mm, v(-68.83, -17.49) * mm, v(-69.13, -17.44) * mm, v(-69.29, -17.22) * mm]});
            skFitSpline(sketch, "E2594", {"points": [v(-69.29, -17.22) * mm, v(-69.44, -17) * mm, v(-69.39, -16.71) * mm, v(-69.15, -16.52) * mm]});
            skFitSpline(sketch, "E2595", {"points": [v(-69.15, -16.52) * mm, v(-68.73, -16.2) * mm, v(-68.32, -15.87) * mm, v(-67.9, -15.55) * mm]});
            skFitSpline(sketch, "E2596", {"points": [v(-67.9, -15.55) * mm, v(-67.7, -15.4) * mm, v(-67.62, -15.22) * mm, v(-67.62, -14.98) * mm]});
            skFitSpline(sketch, "E2597", {"points": [v(-67.62, -14.98) * mm, v(-67.62, -14.52) * mm, v(-67.6, -14.07) * mm, v(-67.58, -13.61) * mm]});
            skFitSpline(sketch, "E2598", {"points": [v(-67.58, -13.61) * mm, v(-67.57, -13.43) * mm, v(-67.56, -13.25) * mm, v(-67.55, -13.06) * mm]});
            skFitSpline(sketch, "E2599", {"points": [v(-67.55, -13.06) * mm, v(-67.55, -13.02) * mm, v(-67.56, -12.98) * mm, v(-67.6, -12.92) * mm]});
            skFitSpline(sketch, "E2600", {"points": [v(-67.6, -12.92) * mm, v(-67.63, -12.98) * mm, v(-67.66, -13.02) * mm, v(-67.69, -13.08) * mm]});
            skFitSpline(sketch, "E2601", {"points": [v(-67.69, -13.08) * mm, v(-67.92, -13.62) * mm, v(-68.15, -14.16) * mm, v(-68.38, -14.7) * mm]});
            skFitSpline(sketch, "E2602", {"points": [v(-68.38, -14.7) * mm, v(-68.47, -14.9) * mm, v(-68.6, -15.03) * mm, v(-68.83, -15.04) * mm]});
            skFitSpline(sketch, "E2603", {"points": [v(-68.83, -15.04) * mm, v(-69.2, -15.05) * mm, v(-69.45, -14.7) * mm, v(-69.3, -14.37) * mm]});
            skFitSpline(sketch, "E2604", {"points": [v(-69.3, -14.37) * mm, v(-69, -13.64) * mm, v(-68.67, -12.9) * mm, v(-68.35, -12.18) * mm]});
            skFitSpline(sketch, "E2605", {"points": [v(-68.35, -12.18) * mm, v(-68.3, -12.09) * mm, v(-68.26, -12) * mm, v(-68.24, -11.87) * mm]});
            skFitSpline(sketch, "E2606", {"points": [v(-68.24, -11.87) * mm, v(-68.4, -12.03) * mm, v(-68.55, -12.18) * mm, v(-68.7, -12.33) * mm]});
            skFitSpline(sketch, "E2607", {"points": [v(-68.7, -12.33) * mm, v(-68.78, -12.42) * mm, v(-68.85, -12.51) * mm, v(-68.93, -12.6) * mm]});
            skFitSpline(sketch, "E2608", {"points": [v(-68.93, -12.6) * mm, v(-69, -12.67) * mm, v(-69.06, -12.75) * mm, v(-69.13, -12.8) * mm]});
            skFitSpline(sketch, "E2609", {"points": [v(-69.13, -12.8) * mm, v(-69.34, -12.97) * mm, v(-69.6, -12.97) * mm, v(-69.79, -12.8) * mm]});
            skFitSpline(sketch, "E2610", {"points": [v(-69.79, -12.8) * mm, v(-69.96, -12.62) * mm, v(-69.98, -12.34) * mm, v(-69.82, -12.14) * mm]});
            skFitSpline(sketch, "E2611", {"points": [v(-69.82, -12.14) * mm, v(-69.68, -11.96) * mm, v(-69.52, -11.78) * mm, v(-69.36, -11.61) * mm]});
            skFitSpline(sketch, "E2612", {"points": [v(-69.36, -11.61) * mm, v(-68.97, -11.2) * mm, v(-68.58, -10.77) * mm, v(-68.19, -10.35) * mm]});
            skFitSpline(sketch, "E2613", {"points": [v(-68.19, -10.35) * mm, v(-68.06, -10.22) * mm, v(-67.93, -10.09) * mm, v(-67.8, -9.94) * mm]});
            skFitSpline(sketch, "E2614", {"points": [v(-67.8, -9.94) * mm, v(-67.93, -9.82) * mm, v(-68.05, -9.7) * mm, v(-68.19, -9.59) * mm]});
            skFitSpline(sketch, "E2615", {"points": [v(-68.19, -9.59) * mm, v(-68.53, -9.3) * mm, v(-68.88, -9.03) * mm, v(-69.22, -8.74) * mm]});
            skFitSpline(sketch, "E2616", {"points": [v(-69.22, -8.74) * mm, v(-69.34, -8.64) * mm, v(-69.45, -8.62) * mm, v(-69.6, -8.64) * mm]});
            skFitSpline(sketch, "E2617", {"points": [v(-69.6, -8.64) * mm, v(-70.14, -8.74) * mm, v(-70.68, -8.83) * mm, v(-71.22, -8.93) * mm]});
            skFitSpline(sketch, "E2618", {"points": [v(-71.22, -8.93) * mm, v(-71.28, -8.94) * mm, v(-71.34, -8.96) * mm, v(-71.41, -8.98) * mm]});
            skFitSpline(sketch, "E2619", {"points": [v(-71.41, -8.98) * mm, v(-71.36, -9.2) * mm, v(-71.31, -9.42) * mm, v(-71.26, -9.63) * mm]});
            skFitSpline(sketch, "E2620", {"points": [v(-71.26, -9.63) * mm, v(-71.17, -10.04) * mm, v(-71.08, -10.44) * mm, v(-70.99, -10.85) * mm]});
            skFitSpline(sketch, "E2621", {"points": [v(-70.99, -10.85) * mm, v(-70.92, -11.15) * mm, v(-70.85, -11.45) * mm, v(-70.79, -11.76) * mm]});
            skFitSpline(sketch, "E2622", {"points": [v(-70.79, -11.76) * mm, v(-70.77, -11.83) * mm, v(-70.76, -11.9) * mm, v(-70.76, -11.97) * mm]});
            skFitSpline(sketch, "E2623", {"points": [v(-70.76, -11.97) * mm, v(-70.76, -12.21) * mm, v(-70.9, -12.39) * mm, v(-71.13, -12.44) * mm]});
            skFitSpline(sketch, "E2624", {"points": [v(-71.13, -12.44) * mm, v(-71.36, -12.48) * mm, v(-71.57, -12.39) * mm, v(-71.67, -12.17) * mm]});
            skFitSpline(sketch, "E2625", {"points": [v(-71.67, -12.17) * mm, v(-71.71, -12.07) * mm, v(-71.73, -11.95) * mm, v(-71.76, -11.83) * mm]});
            skFitSpline(sketch, "E2626", {"points": [v(-71.76, -11.83) * mm, v(-71.83, -11.53) * mm, v(-71.9, -11.22) * mm, v(-71.98, -10.92) * mm]});
            skFitSpline(sketch, "E2627", {"points": [v(-71.98, -10.92) * mm, v(-71.98, -10.9) * mm, v(-72, -10.89) * mm, v(-72.03, -10.85) * mm]});
            skFitSpline(sketch, "E2628", {"points": [v(-72.03, -10.85) * mm, v(-72.06, -11.25) * mm, v(-72.1, -11.62) * mm, v(-72.14, -12) * mm]});
            skFitSpline(sketch, "E2629", {"points": [v(-72.14, -12) * mm, v(-72.2, -12.53) * mm, v(-72.26, -13.06) * mm, v(-72.33, -13.59) * mm]});
            skFitSpline(sketch, "E2630", {"points": [v(-72.33, -13.59) * mm, v(-72.36, -13.83) * mm, v(-72.58, -14) * mm, v(-72.83, -13.99) * mm]});
            skFitSpline(sketch, "E2631", {"points": [v(-72.83, -13.99) * mm, v(-73.07, -13.98) * mm, v(-73.27, -13.8) * mm, v(-73.28, -13.55) * mm]});
            skFitSpline(sketch, "E2632", {"points": [v(-73.28, -13.55) * mm, v(-73.29, -13.43) * mm, v(-73.27, -13.31) * mm, v(-73.26, -13.2) * mm]});
            skFitSpline(sketch, "E2633", {"points": [v(-73.26, -13.2) * mm, v(-73.2, -12.69) * mm, v(-73.13, -12.18) * mm, v(-73.07, -11.68) * mm]});
            skFitSpline(sketch, "E2634", {"points": [v(-73.07, -11.68) * mm, v(-73.06, -11.6) * mm, v(-73.07, -11.53) * mm, v(-73.07, -11.42) * mm]});
            skFitSpline(sketch, "E2635", {"points": [v(-73.07, -11.42) * mm, v(-73.2, -11.59) * mm, v(-73.29, -11.75) * mm, v(-73.37, -11.9) * mm]});
            skFitSpline(sketch, "E2636", {"points": [v(-73.37, -11.9) * mm, v(-73.48, -12.11) * mm, v(-73.6, -12.31) * mm, v(-73.7, -12.52) * mm]});
            skFitSpline(sketch, "E2637", {"points": [v(-73.7, -12.52) * mm, v(-73.86, -12.83) * mm, v(-74.03, -13.14) * mm, v(-74.18, -13.46) * mm]});
            skFitSpline(sketch, "E2638", {"points": [v(-74.18, -13.46) * mm, v(-74.2, -13.52) * mm, v(-74.2, -13.62) * mm, v(-74.18, -13.69) * mm]});
            skFitSpline(sketch, "E2639", {"points": [v(-74.18, -13.69) * mm, v(-74, -14.17) * mm, v(-73.82, -14.64) * mm, v(-73.64, -15.12) * mm]});
            skFitSpline(sketch, "E2640", {"points": [v(-73.64, -15.12) * mm, v(-73.6, -15.2) * mm, v(-73.55, -15.3) * mm, v(-73.52, -15.38) * mm]});
            skFitSpline(sketch, "E2641", {"points": [v(-73.52, -15.38) * mm, v(-73.42, -15.65) * mm, v(-73.52, -15.9) * mm, v(-73.78, -16.02) * mm]});
            skFitSpline(sketch, "E2642", {"points": [v(-73.78, -16.02) * mm, v(-74, -16.13) * mm, v(-74.27, -16.04) * mm, v(-74.4, -15.78) * mm]});
            skFitSpline(sketch, "E2643", {"points": [v(-74.4, -15.78) * mm, v(-74.53, -15.54) * mm, v(-74.64, -15.28) * mm, v(-74.74, -15.02) * mm]});
            skFitSpline(sketch, "E2644", {"points": [v(-74.74, -15.02) * mm, v(-74.87, -14.68) * mm, v(-75, -14.33) * mm, v(-75.13, -13.97) * mm]});
            skFitSpline(sketch, "E2645", {"points": [v(-75.13, -13.97) * mm, v(-75.18, -13.97) * mm, v(-75.23, -13.97) * mm, v(-75.28, -13.98) * mm]});
            skFitSpline(sketch, "E2646", {"points": [v(-75.28, -13.98) * mm, v(-75.84, -14.07) * mm, v(-76.4, -14.16) * mm, v(-76.96, -14.24) * mm]});
            skFitSpline(sketch, "E2647", {"points": [v(-76.96, -14.24) * mm, v(-77.07, -14.25) * mm, v(-77.19, -14.24) * mm, v(-77.29, -14.2) * mm]});
            skFitSpline(sketch, "E2648", {"points": [v(-77.29, -14.2) * mm, v(-77.5, -14.13) * mm, v(-77.62, -13.92) * mm, v(-77.6, -13.71) * mm]});
            skFitSpline(sketch, "E2649", {"points": [v(-77.6, -13.71) * mm, v(-77.57, -13.49) * mm, v(-77.42, -13.32) * mm, v(-77.18, -13.29) * mm]});
            skFitSpline(sketch, "E2650", {"points": [v(-77.18, -13.29) * mm, v(-76.74, -13.22) * mm, v(-76.3, -13.14) * mm, v(-75.85, -13.1) * mm]});
            skFitSpline(sketch, "E2651", {"points": [v(-75.85, -13.1) * mm, v(-75.43, -13.07) * mm, v(-75.1, -12.92) * mm, v(-74.92, -12.52) * mm]});
            skFitSpline(sketch, "E2652", {"points": [v(-74.92, -12.52) * mm, v(-74.85, -12.38) * mm, v(-74.75, -12.25) * mm, v(-74.66, -12.12) * mm]});
            skFitSpline(sketch, "E2653", {"points": [v(-74.66, -12.12) * mm, v(-74.46, -11.78) * mm, v(-74.25, -11.43) * mm, v(-74.05, -11.1) * mm]});
            skFitSpline(sketch, "E2654", {"points": [v(-74.05, -11.1) * mm, v(-74.02, -11.05) * mm, v(-74, -11) * mm, v(-74, -10.92) * mm]});
            skFitSpline(sketch, "E2655", {"points": [v(-74, -10.92) * mm, v(-74.17, -11.04) * mm, v(-74.33, -11.15) * mm, v(-74.5, -11.28) * mm]});
            skFitSpline(sketch, "E2656", {"points": [v(-74.5, -11.28) * mm, v(-74.85, -11.54) * mm, v(-75.2, -11.81) * mm, v(-75.57, -12.08) * mm]});
            skFitSpline(sketch, "E2657", {"points": [v(-75.57, -12.08) * mm, v(-75.69, -12.17) * mm, v(-75.81, -12.23) * mm, v(-75.97, -12.2) * mm]});
            skFitSpline(sketch, "E2658", {"points": [v(-75.97, -12.2) * mm, v(-76.17, -12.17) * mm, v(-76.3, -12.05) * mm, v(-76.36, -11.86) * mm]});
            skFitSpline(sketch, "E2659", {"points": [v(-76.36, -11.86) * mm, v(-76.41, -11.66) * mm, v(-76.37, -11.47) * mm, v(-76.2, -11.34) * mm]});
            skFitSpline(sketch, "E2660", {"points": [v(-76.2, -11.34) * mm, v(-76, -11.18) * mm, v(-75.78, -11.02) * mm, v(-75.57, -10.87) * mm]});
            skFitSpline(sketch, "E2661", {"points": [v(-75.57, -10.87) * mm, v(-75.05, -10.48) * mm, v(-74.53, -10.1) * mm, v(-74.02, -9.69) * mm]});
            skFitSpline(sketch, "E2662", {"points": [v(-74.02, -9.69) * mm, v(-74.32, -9.78) * mm, v(-74.62, -9.87) * mm, v(-74.92, -9.96) * mm]});
            skFitSpline(sketch, "E2663", {"points": [v(-74.92, -9.96) * mm, v(-75.02, -10) * mm, v(-75.12, -10.03) * mm, v(-75.22, -10.05) * mm]});
            skFitSpline(sketch, "E2664", {"points": [v(-75.22, -10.05) * mm, v(-75.5, -10.12) * mm, v(-75.74, -9.98) * mm, v(-75.82, -9.72) * mm]});
            skFitSpline(sketch, "E2665", {"points": [v(-75.82, -9.72) * mm, v(-75.9, -9.5) * mm, v(-75.76, -9.22) * mm, v(-75.5, -9.13) * mm]});
            skFitSpline(sketch, "E2666", {"points": [v(-75.5, -9.13) * mm, v(-75.3, -9.05) * mm, v(-75.1, -8.98) * mm, v(-74.89, -8.92) * mm]});
            skFitSpline(sketch, "E2667", {"points": [v(-74.89, -8.92) * mm, v(-74.53, -8.8) * mm, v(-74.16, -8.69) * mm, v(-73.8, -8.58) * mm]});
            skFitSpline(sketch, "E2668", {"points": [v(-73.8, -8.58) * mm, v(-73.52, -8.5) * mm, v(-73.24, -8.42) * mm, v(-72.97, -8.34) * mm]});
            skFitSpline(sketch, "E2669", {"points": [v(-72.97, -8.34) * mm, v(-72.87, -8.31) * mm, v(-72.77, -8.28) * mm, v(-72.66, -8.24) * mm]});
            skFitSpline(sketch, "E2670", {"points": [v(-72.66, -8.24) * mm, v(-72.75, -8) * mm, v(-72.83, -7.76) * mm, v(-72.91, -7.53) * mm]});
            skFitSpline(sketch, "E2671", {"points": [v(-72.91, -7.53) * mm, v(-73.04, -7.18) * mm, v(-73.18, -6.83) * mm, v(-73.3, -6.47) * mm]});
            skFitSpline(sketch, "E2672", {"points": [v(-73.3, -6.47) * mm, v(-73.35, -6.36) * mm, v(-73.41, -6.28) * mm, v(-73.53, -6.24) * mm]});
            skFitSpline(sketch, "E2673", {"points": [v(-73.53, -6.24) * mm, v(-74.11, -6.03) * mm, v(-74.7, -5.81) * mm, v(-75.3, -5.59) * mm]});
            skFitSpline(sketch, "E2674", {"points": [v(-75.3, -5.59) * mm, v(-75.33, -5.66) * mm, v(-75.36, -5.72) * mm, v(-75.38, -5.79) * mm]});
            skFitSpline(sketch, "E2675", {"points": [v(-75.38, -5.79) * mm, v(-75.65, -6.65) * mm, v(-75.9, -7.51) * mm, v(-76.18, -8.37) * mm]});
            skFitSpline(sketch, "E2676", {"points": [v(-76.18, -8.37) * mm, v(-76.21, -8.47) * mm, v(-76.28, -8.58) * mm, v(-76.36, -8.65) * mm]});
            skFitSpline(sketch, "E2677", {"points": [v(-76.36, -8.65) * mm, v(-76.5, -8.78) * mm, v(-76.68, -8.82) * mm, v(-76.86, -8.72) * mm]});
            skFitSpline(sketch, "E2678", {"points": [v(-76.86, -8.72) * mm, v(-77.04, -8.63) * mm, v(-77.15, -8.49) * mm, v(-77.14, -8.28) * mm]});
            skFitSpline(sketch, "E2679", {"points": [v(-77.14, -8.28) * mm, v(-77.13, -8.17) * mm, v(-77.1, -8.06) * mm, v(-77.07, -7.95) * mm]});
            skFitSpline(sketch, "E2680", {"points": [v(-77.07, -7.95) * mm, v(-76.98, -7.66) * mm, v(-76.89, -7.36) * mm, v(-76.8, -7.06) * mm]});
            skFitSpline(sketch, "E2681", {"points": [v(-76.8, -7.06) * mm, v(-76.78, -7.03) * mm, v(-76.78, -7) * mm, v(-76.77, -6.95) * mm]});
            skFitSpline(sketch, "E2682", {"points": [v(-76.77, -6.95) * mm, v(-76.8, -6.96) * mm, v(-76.82, -6.96) * mm, v(-76.83, -6.97) * mm]});
            skFitSpline(sketch, "E2683", {"points": [v(-76.83, -6.97) * mm, v(-77.2, -7.5) * mm, v(-77.59, -8.02) * mm, v(-77.97, -8.55) * mm]});
            skFitSpline(sketch, "E2684", {"points": [v(-77.97, -8.55) * mm, v(-78.1, -8.73) * mm, v(-78.24, -8.92) * mm, v(-78.39, -9.1) * mm]});
            skFitSpline(sketch, "E2685", {"points": [v(-78.39, -9.1) * mm, v(-78.57, -9.34) * mm, v(-78.86, -9.38) * mm, v(-79.09, -9.21) * mm]});
            skFitSpline(sketch, "E2686", {"points": [v(-79.09, -9.21) * mm, v(-79.3, -9.04) * mm, v(-79.35, -8.77) * mm, v(-79.18, -8.53) * mm]});
            skFitSpline(sketch, "E2687", {"points": [v(-79.18, -8.53) * mm, v(-78.91, -8.16) * mm, v(-78.63, -7.8) * mm, v(-78.36, -7.44) * mm]});
            skFitSpline(sketch, "E2688", {"points": [v(-78.36, -7.44) * mm, v(-78.24, -7.27) * mm, v(-78.11, -7.1) * mm, v(-78, -6.94) * mm]});
            skFitSpline(sketch, "E2689", {"points": [v(-78, -6.94) * mm, v(-78, -6.93) * mm, v(-78.01, -6.91) * mm, v(-78.02, -6.9) * mm]});
            skFitSpline(sketch, "E2690", {"points": [v(-78.02, -6.9) * mm, v(-78.17, -6.98) * mm, v(-78.32, -7.06) * mm, v(-78.47, -7.15) * mm]});
            skFitSpline(sketch, "E2691", {"points": [v(-78.47, -7.15) * mm, v(-78.68, -7.28) * mm, v(-78.9, -7.4) * mm, v(-79.1, -7.54) * mm]});
            skFitSpline(sketch, "E2692", {"points": [v(-79.1, -7.54) * mm, v(-79.38, -7.72) * mm, v(-79.67, -7.9) * mm, v(-79.94, -8.1) * mm]});
            skFitSpline(sketch, "E2693", {"points": [v(-79.94, -8.1) * mm, v(-80, -8.14) * mm, v(-80.06, -8.25) * mm, v(-80.08, -8.33) * mm]});
            skFitSpline(sketch, "E2694", {"points": [v(-80.08, -8.33) * mm, v(-80.16, -8.73) * mm, v(-80.23, -9.13) * mm, v(-80.3, -9.53) * mm]});
            skFitSpline(sketch, "E2695", {"points": [v(-80.3, -9.53) * mm, v(-80.32, -9.7) * mm, v(-80.33, -9.88) * mm, v(-80.35, -10.05) * mm]});
            skFitSpline(sketch, "E2696", {"points": [v(-80.35, -10.05) * mm, v(-80.38, -10.35) * mm, v(-80.58, -10.54) * mm, v(-80.85, -10.53) * mm]});
            skFitSpline(sketch, "E2697", {"points": [v(-80.85, -10.53) * mm, v(-81.12, -10.51) * mm, v(-81.34, -10.3) * mm, v(-81.31, -10) * mm]});
            skFitSpline(sketch, "E2698", {"points": [v(-81.31, -10) * mm, v(-81.27, -9.56) * mm, v(-81.2, -9.12) * mm, v(-81.14, -8.7) * mm]});
            skFitSpline(sketch, "E2699", {"points": [v(-81.14, -8.7) * mm, v(-81.11, -8.49) * mm, v(-81.07, -8.28) * mm, v(-81.03, -8.06) * mm]});
            skFitSpline(sketch, "E2700", {"points": [v(-81.03, -8.06) * mm, v(-81.11, -8.03) * mm, v(-81.2, -8) * mm, v(-81.27, -7.97) * mm]});
            skFitSpline(sketch, "E2701", {"points": [v(-81.27, -7.97) * mm, v(-81.78, -7.77) * mm, v(-82.29, -7.58) * mm, v(-82.79, -7.37) * mm]});
            skFitSpline(sketch, "E2702", {"points": [v(-82.79, -7.37) * mm, v(-83.09, -7.24) * mm, v(-83.2, -6.97) * mm, v(-83.1, -6.7) * mm]});
            skFitSpline(sketch, "E2703", {"points": [v(-83.1, -6.7) * mm, v(-82.98, -6.45) * mm, v(-82.72, -6.34) * mm, v(-82.44, -6.46) * mm]});
            skFitSpline(sketch, "E2704", {"points": [v(-82.44, -6.46) * mm, v(-82.11, -6.59) * mm, v(-81.8, -6.73) * mm, v(-81.46, -6.86) * mm]});
            skFitSpline(sketch, "E2705", {"points": [v(-81.46, -6.86) * mm, v(-81.23, -6.95) * mm, v(-81, -7.03) * mm, v(-80.76, -7.1) * mm]});
            skFitSpline(sketch, "E2706", {"points": [v(-80.76, -7.1) * mm, v(-80.68, -7.14) * mm, v(-80.6, -7.15) * mm, v(-80.51, -7.1) * mm]});
            skFitSpline(sketch, "E2707", {"points": [v(-80.51, -7.1) * mm, v(-79.92, -6.78) * mm, v(-79.31, -6.47) * mm, v(-78.71, -6.15) * mm]});
            skFitSpline(sketch, "E2708", {"points": [v(-78.71, -6.15) * mm, v(-78.65, -6.12) * mm, v(-78.59, -6.07) * mm, v(-78.54, -5.99) * mm]});
            skFitSpline(sketch, "E2709", {"points": [v(-78.54, -5.99) * mm, v(-78.73, -6) * mm, v(-78.93, -6.02) * mm, v(-79.12, -6.05) * mm]});
            skFitSpline(sketch, "E2710", {"points": [v(-79.12, -6.05) * mm, v(-79.56, -6.1) * mm, v(-80, -6.16) * mm, v(-80.43, -6.21) * mm]});
            skFitSpline(sketch, "E2711", {"points": [v(-80.43, -6.21) * mm, v(-80.44, -6.21) * mm, v(-80.46, -6.21) * mm, v(-80.48, -6.21) * mm]});
            skFitSpline(sketch, "E2712", {"points": [v(-80.48, -6.21) * mm, v(-80.8, -6.23) * mm, v(-81.03, -6.06) * mm, v(-81.06, -5.78) * mm]});
            skFitSpline(sketch, "E2713", {"points": [v(-81.06, -5.78) * mm, v(-81.08, -5.5) * mm, v(-80.9, -5.3) * mm, v(-80.57, -5.25) * mm]});
            skFitSpline(sketch, "E2714", {"points": [v(-80.57, -5.25) * mm, v(-79.76, -5.16) * mm, v(-78.95, -5.07) * mm, v(-78.14, -4.99) * mm]});
            skFitSpline(sketch, "E2715", {"points": [v(-78.14, -4.99) * mm, v(-78.08, -4.98) * mm, v(-78.02, -4.97) * mm, v(-77.91, -4.95) * mm]});
            skFitSpline(sketch, "E2716", {"points": [v(-77.91, -4.95) * mm, v(-77.98, -4.92) * mm, v(-78.01, -4.9) * mm, v(-78.05, -4.89) * mm]});
            skFitSpline(sketch, "E2717", {"points": [v(-78.05, -4.89) * mm, v(-78.36, -4.82) * mm, v(-78.67, -4.75) * mm, v(-78.98, -4.68) * mm]});
            skFitSpline(sketch, "E2718", {"points": [v(-78.98, -4.68) * mm, v(-79.09, -4.65) * mm, v(-79.2, -4.62) * mm, v(-79.3, -4.57) * mm]});
            skFitSpline(sketch, "E2719", {"points": [v(-79.3, -4.57) * mm, v(-79.48, -4.46) * mm, v(-79.56, -4.25) * mm, v(-79.5, -4.05) * mm]});
            skFitSpline(sketch, "E2720", {"points": [v(-79.5, -4.05) * mm, v(-79.45, -3.83) * mm, v(-79.28, -3.68) * mm, v(-79.06, -3.7) * mm]});
            skFitSpline(sketch, "E2721", {"points": [v(-79.06, -3.7) * mm, v(-78.8, -3.72) * mm, v(-78.55, -3.77) * mm, v(-78.3, -3.82) * mm]});
            skFitSpline(sketch, "E2722", {"points": [v(-78.3, -3.82) * mm, v(-77.72, -3.95) * mm, v(-77.14, -4.08) * mm, v(-76.55, -4.22) * mm]});
            skFitSpline(sketch, "E2723", {"points": [v(-76.55, -4.22) * mm, v(-76.4, -4.26) * mm, v(-76.23, -4.3) * mm, v(-76.05, -4.35) * mm]});
            skFitSpline(sketch, "E2724", {"points": [v(-76.05, -4.35) * mm, v(-76, -4.17) * mm, v(-75.96, -4) * mm, v(-75.93, -3.83) * mm]});
            skFitSpline(sketch, "E2725", {"points": [v(-75.93, -3.83) * mm, v(-75.85, -3.38) * mm, v(-75.78, -2.92) * mm, v(-75.7, -2.46) * mm]});
            skFitSpline(sketch, "E2726", {"points": [v(-75.7, -2.46) * mm, v(-75.69, -2.37) * mm, v(-75.7, -2.3) * mm, v(-75.75, -2.22) * mm]});
            skFitSpline(sketch, "E2727", {"points": [v(-75.75, -2.22) * mm, v(-76.17, -1.72) * mm, v(-76.58, -1.22) * mm, v(-77, -0.71) * mm]});
            skFitSpline(sketch, "E2728", {"points": [v(-77, -0.71) * mm, v(-77.17, -0.87) * mm, v(-77.33, -1.02) * mm, v(-77.48, -1.17) * mm]});
            skFitSpline(sketch, "E2729", {"points": [v(-77.48, -1.17) * mm, v(-77.82, -1.48) * mm, v(-78.15, -1.78) * mm, v(-78.49, -2.1) * mm]});
            skFitSpline(sketch, "E2730", {"points": [v(-78.49, -2.1) * mm, v(-78.72, -2.3) * mm, v(-78.94, -2.52) * mm, v(-79.18, -2.72) * mm]});
            skFitSpline(sketch, "E2731", {"points": [v(-79.18, -2.72) * mm, v(-79.48, -2.98) * mm, v(-79.9, -2.85) * mm, v(-79.99, -2.48) * mm]});
            skFitSpline(sketch, "E2732", {"points": [v(-79.99, -2.48) * mm, v(-80.02, -2.33) * mm, v(-79.99, -2.2) * mm, v(-79.89, -2.08) * mm]});
            skFitSpline(sketch, "E2733", {"points": [v(-79.89, -2.08) * mm, v(-79.82, -1.99) * mm, v(-79.73, -1.92) * mm, v(-79.65, -1.84) * mm]});
            skFitSpline(sketch, "E2734", {"points": [v(-79.65, -1.84) * mm, v(-79.42, -1.62) * mm, v(-79.18, -1.4) * mm, v(-78.97, -1.16) * mm]});
            skFitSpline(sketch, "E2735", {"points": [v(-78.97, -1.16) * mm, v(-79.02, -1.18) * mm, v(-79.07, -1.19) * mm, v(-79.11, -1.2) * mm]});
            skFitSpline(sketch, "E2736", {"points": [v(-79.11, -1.2) * mm, v(-79.88, -1.54) * mm, v(-80.65, -1.88) * mm, v(-81.4, -2.23) * mm]});
            skFitSpline(sketch, "E2737", {"points": [v(-81.4, -2.23) * mm, v(-81.69, -2.35) * mm, v(-81.99, -2.2) * mm, v(-82.08, -1.98) * mm]});
            skFitSpline(sketch, "E2738", {"points": [v(-82.08, -1.98) * mm, v(-82.19, -1.72) * mm, v(-82.09, -1.45) * mm, v(-81.8, -1.33) * mm]});
            skFitSpline(sketch, "E2739", {"points": [v(-81.8, -1.33) * mm, v(-81.27, -1.1) * mm, v(-80.72, -0.86) * mm, v(-80.18, -0.63) * mm]});
            skFitSpline(sketch, "E2740", {"points": [v(-80.18, -0.63) * mm, v(-80.12, -0.6) * mm, v(-80.06, -0.57) * mm, v(-80, -0.51) * mm]});
            skFitSpline(sketch, "E2741", {"points": [v(-80, -0.51) * mm, v(-80.15, -0.46) * mm, v(-80.3, -0.48) * mm, v(-80.46, -0.48) * mm]});
            skFitSpline(sketch, "E2742", {"points": [v(-80.46, -0.48) * mm, v(-80.7, -0.48) * mm, v(-80.93, -0.5) * mm, v(-81.17, -0.5) * mm]});
            skFitSpline(sketch, "E2743", {"points": [v(-81.17, -0.5) * mm, v(-81.54, -0.53) * mm, v(-81.9, -0.55) * mm, v(-82.27, -0.58) * mm]});
            skFitSpline(sketch, "E2744", {"points": [v(-82.27, -0.58) * mm, v(-82.35, -0.59) * mm, v(-82.44, -0.64) * mm, v(-82.5, -0.7) * mm]});
            skFitSpline(sketch, "E2745", {"points": [v(-82.5, -0.7) * mm, v(-82.82, -1.1) * mm, v(-83.14, -1.5) * mm, v(-83.46, -1.89) * mm]});
            skFitSpline(sketch, "E2746", {"points": [v(-83.46, -1.89) * mm, v(-83.5, -1.95) * mm, v(-83.55, -2.02) * mm, v(-83.6, -2.08) * mm]});
            skFitSpline(sketch, "E2747", {"points": [v(-83.6, -2.08) * mm, v(-83.8, -2.32) * mm, v(-84.07, -2.37) * mm, v(-84.3, -2.2) * mm]});
            skFitSpline(sketch, "E2748", {"points": [v(-84.3, -2.2) * mm, v(-84.51, -2.05) * mm, v(-84.55, -1.75) * mm, v(-84.38, -1.5) * mm]});
            skFitSpline(sketch, "E2749", {"points": [v(-84.38, -1.5) * mm, v(-84.21, -1.26) * mm, v(-84.03, -1.02) * mm, v(-83.85, -0.8) * mm]});
            skFitSpline(sketch, "E2750", {"points": [v(-83.85, -0.8) * mm, v(-83.64, -0.53) * mm, v(-83.42, -0.28) * mm, v(-83.2, 0) * mm]});
            skFitSpline(sketch, "E2751", {"points": [v(-83.2, 0) * mm, v(-83.24, 0.06) * mm, v(-83.29, 0.12) * mm, v(-83.34, 0.18) * mm]});
            skFitSpline(sketch, "E2752", {"points": [v(-83.34, 0.18) * mm, v(-83.67, 0.6) * mm, v(-84.02, 1.03) * mm, v(-84.34, 1.46) * mm]});
            skFitSpline(sketch, "E2753", {"points": [v(-84.34, 1.46) * mm, v(-84.42, 1.55) * mm, v(-84.46, 1.69) * mm, v(-84.48, 1.8) * mm]});
            skFitSpline(sketch, "E2754", {"points": [v(-84.48, 1.8) * mm, v(-84.5, 2.02) * mm, v(-84.39, 2.18) * mm, v(-84.2, 2.26) * mm]});
            skFitSpline(sketch, "E2755", {"points": [v(-84.2, 2.26) * mm, v(-84.02, 2.34) * mm, v(-83.82, 2.3) * mm, v(-83.67, 2.16) * mm]});
            skFitSpline(sketch, "E2756", {"points": [v(-83.67, 2.16) * mm, v(-83.6, 2.1) * mm, v(-83.56, 2.03) * mm, v(-83.5, 1.96) * mm]});
            skFitSpline(sketch, "E2757", {"points": [v(-83.5, 1.96) * mm, v(-83.19, 1.56) * mm, v(-82.87, 1.16) * mm, v(-82.55, 0.76) * mm]});
            skFitSpline(sketch, "E2758", {"points": [v(-82.55, 0.76) * mm, v(-82.46, 0.64) * mm, v(-82.35, 0.57) * mm, v(-82.19, 0.57) * mm]});
            skFitSpline(sketch, "E2759", {"points": [v(-82.19, 0.57) * mm, v(-81.82, 0.56) * mm, v(-81.45, 0.52) * mm, v(-81.09, 0.5) * mm]});
            skFitSpline(sketch, "E2760", {"points": [v(-81.09, 0.5) * mm, v(-80.78, 0.49) * mm, v(-80.48, 0.49) * mm, v(-80.18, 0.48) * mm]});
            skFitSpline(sketch, "E2761", {"points": [v(-80.18, 0.48) * mm, v(-80.12, 0.48) * mm, v(-80.06, 0.49) * mm, v(-80, 0.51) * mm]});
            skFitSpline(sketch, "E2762", {"points": [v(-80, 0.51) * mm, v(-80.15, 0.63) * mm, v(-80.33, 0.7) * mm, v(-80.51, 0.78) * mm]});
            skFitSpline(sketch, "E2763", {"points": [v(-80.51, 0.78) * mm, v(-80.94, 0.96) * mm, v(-81.36, 1.14) * mm, v(-81.79, 1.32) * mm]});
            skFitSpline(sketch, "E2764", {"points": [v(-81.79, 1.32) * mm, v(-81.97, 1.4) * mm, v(-82.1, 1.52) * mm, v(-82.11, 1.73) * mm]});
            skFitSpline(sketch, "E2765", {"points": [v(-82.11, 1.73) * mm, v(-82.15, 2.1) * mm, v(-81.8, 2.37) * mm, v(-81.43, 2.23) * mm]});
            skFitSpline(sketch, "E2766", {"points": [v(-81.43, 2.23) * mm, v(-81.22, 2.15) * mm, v(-81.02, 2.06) * mm, v(-80.81, 1.97) * mm]});
            skFitSpline(sketch, "E2767", {"points": [v(-80.81, 1.97) * mm, v(-80.22, 1.7) * mm, v(-79.63, 1.44) * mm, v(-79.04, 1.18) * mm]});
            skFitSpline(sketch, "E2768", {"points": [v(-79.04, 1.18) * mm, v(-79.02, 1.17) * mm, v(-79, 1.17) * mm, v(-78.95, 1.2) * mm]});
            skFitSpline(sketch, "E2769", {"points": [v(-78.95, 1.2) * mm, v(-79.18, 1.4) * mm, v(-79.4, 1.62) * mm, v(-79.64, 1.83) * mm]});
            skFitSpline(sketch, "E2770", {"points": [v(-79.64, 1.83) * mm, v(-79.71, 1.9) * mm, v(-79.8, 1.97) * mm, v(-79.86, 2.04) * mm]});
            skFitSpline(sketch, "E2771", {"points": [v(-79.86, 2.04) * mm, v(-80.05, 2.26) * mm, v(-80.05, 2.53) * mm, v(-79.86, 2.72) * mm]});
            skFitSpline(sketch, "E2772", {"points": [v(-79.86, 2.72) * mm, v(-79.69, 2.9) * mm, v(-79.4, 2.9) * mm, v(-79.19, 2.73) * mm]});
            skFitSpline(sketch, "E2773", {"points": [v(-79.19, 2.73) * mm, v(-79.01, 2.6) * mm, v(-78.85, 2.44) * mm, v(-78.68, 2.3) * mm]});
            skFitSpline(sketch, "E2774", {"points": [v(-78.68, 2.3) * mm, v(-78.28, 1.92) * mm, v(-77.88, 1.54) * mm, v(-77.47, 1.16) * mm]});
            skFitSpline(sketch, "E2775", {"points": [v(-77.47, 1.16) * mm, v(-77.32, 1.02) * mm, v(-77.17, 0.88) * mm, v(-77, 0.71) * mm]});
            skFitSpline(sketch, "E2776", {"points": [v(-77, 0.71) * mm, v(-76.76, 1) * mm, v(-76.53, 1.28) * mm, v(-76.3, 1.56) * mm]});
            skFitSpline(sketch, "E2777", {"points": [v(-76.3, 1.56) * mm, v(-76.12, 1.77) * mm, v(-75.95, 1.98) * mm, v(-75.78, 2.19) * mm]});
            skFitSpline(sketch, "E2778", {"points": [v(-75.78, 2.19) * mm, v(-75.72, 2.26) * mm, v(-75.68, 2.33) * mm, v(-75.7, 2.43) * mm]});
            skFitSpline(sketch, "E2779", {"points": [v(-75.7, 2.43) * mm, v(-75.8, 3.02) * mm, v(-75.9, 3.6) * mm, v(-76, 4.2) * mm]});
            skFitSpline(sketch, "E2780", {"points": [v(-76, 4.2) * mm, v(-76.02, 4.24) * mm, v(-76.03, 4.28) * mm, v(-76.05, 4.34) * mm]});
            skFitSpline(sketch, "E2781", {"points": [v(-76.05, 4.34) * mm, v(-76.27, 4.3) * mm, v(-76.48, 4.24) * mm, v(-76.68, 4.2) * mm]});
            skFitSpline(sketch, "E2782", {"points": [v(-76.68, 4.2) * mm, v(-77.09, 4.1) * mm, v(-77.5, 4.01) * mm, v(-77.9, 3.92) * mm]});
            skFitSpline(sketch, "E2783", {"points": [v(-77.9, 3.92) * mm, v(-78.23, 3.85) * mm, v(-78.55, 3.77) * mm, v(-78.88, 3.7) * mm]});
            skFitSpline(sketch, "E2784", {"points": [v(-78.88, 3.7) * mm, v(-78.98, 3.68) * mm, v(-79.09, 3.68) * mm, v(-79.18, 3.7) * mm]});
            skFitSpline(sketch, "E2785", {"points": [v(-79.18, 3.7) * mm, v(-79.38, 3.76) * mm, v(-79.51, 3.94) * mm, v(-79.52, 4.13) * mm]});
            skFitSpline(sketch, "E2786", {"points": [v(-79.52, 4.13) * mm, v(-79.53, 4.33) * mm, v(-79.45, 4.5) * mm, v(-79.27, 4.58) * mm]});
            skFitSpline(sketch, "E2787", {"points": [v(-79.27, 4.58) * mm, v(-79.18, 4.63) * mm, v(-79.07, 4.65) * mm, v(-78.97, 4.67) * mm]});
            skFitSpline(sketch, "E2788", {"points": [v(-78.97, 4.67) * mm, v(-78.64, 4.75) * mm, v(-78.3, 4.83) * mm, v(-77.96, 4.95) * mm]});
            skFitSpline(sketch, "E2789", {"points": [v(-77.96, 4.95) * mm, v(-78.04, 4.96) * mm, v(-78.11, 4.98) * mm, v(-78.2, 4.99) * mm]});
            skFitSpline(sketch, "E2790", {"points": [v(-78.2, 4.99) * mm, v(-78.56, 5.03) * mm, v(-78.94, 5.05) * mm, v(-79.31, 5.1) * mm]});
            skFitSpline(sketch, "E2791", {"points": [v(-79.31, 5.1) * mm, v(-79.72, 5.14) * mm, v(-80.12, 5.19) * mm, v(-80.52, 5.24) * mm]});
            skFitSpline(sketch, "E2792", {"points": [v(-80.52, 5.24) * mm, v(-80.59, 5.25) * mm, v(-80.65, 5.25) * mm, v(-80.71, 5.27) * mm]});
            skFitSpline(sketch, "E2793", {"points": [v(-80.71, 5.27) * mm, v(-80.94, 5.34) * mm, v(-81.1, 5.57) * mm, v(-81.06, 5.8) * mm]});
            skFitSpline(sketch, "E2794", {"points": [v(-81.06, 5.8) * mm, v(-81.02, 6.04) * mm, v(-80.84, 6.2) * mm, v(-80.6, 6.2) * mm]});
            skFitSpline(sketch, "E2795", {"points": [v(-80.6, 6.2) * mm, v(-80.44, 6.21) * mm, v(-80.3, 6.2) * mm, v(-80.14, 6.18) * mm]});
            skFitSpline(sketch, "E2796", {"points": [v(-80.14, 6.18) * mm, v(-79.7, 6.13) * mm, v(-79.27, 6.07) * mm, v(-78.84, 6.01) * mm]});
            skFitSpline(sketch, "E2797", {"points": [v(-78.84, 6.01) * mm, v(-78.74, 6) * mm, v(-78.64, 6) * mm, v(-78.53, 6.04) * mm]});
            skFitSpline(sketch, "E2798", {"points": [v(-78.53, 6.04) * mm, v(-78.65, 6.11) * mm, v(-78.76, 6.19) * mm, v(-78.89, 6.25) * mm]});
            skFitSpline(sketch, "E2799", {"points": [v(-78.89, 6.25) * mm, v(-79.4, 6.53) * mm, v(-79.92, 6.79) * mm, v(-80.44, 7.07) * mm]});
            skFitSpline(sketch, "E2800", {"points": [v(-80.44, 7.07) * mm, v(-80.56, 7.13) * mm, v(-80.67, 7.15) * mm, v(-80.8, 7.1) * mm]});
            skFitSpline(sketch, "E2801", {"points": [v(-80.8, 7.1) * mm, v(-81.28, 6.91) * mm, v(-81.77, 6.73) * mm, v(-82.25, 6.54) * mm]});
            skFitSpline(sketch, "E2802", {"points": [v(-82.25, 6.54) * mm, v(-82.34, 6.5) * mm, v(-82.42, 6.46) * mm, v(-82.51, 6.43) * mm]});
            skFitSpline(sketch, "E2803", {"points": [v(-82.51, 6.43) * mm, v(-82.74, 6.37) * mm, v(-82.96, 6.46) * mm, v(-83.07, 6.65) * mm]});
            skFitSpline(sketch, "E2804", {"points": [v(-83.07, 6.65) * mm, v(-83.18, 6.85) * mm, v(-83.15, 7.08) * mm, v(-82.98, 7.24) * mm]});
            skFitSpline(sketch, "E2805", {"points": [v(-82.98, 7.24) * mm, v(-82.91, 7.3) * mm, v(-82.84, 7.35) * mm, v(-82.75, 7.38) * mm]});
            skFitSpline(sketch, "E2806", {"points": [v(-82.75, 7.38) * mm, v(-82.24, 7.59) * mm, v(-81.73, 7.79) * mm, v(-81.22, 7.99) * mm]});
            skFitSpline(sketch, "E2807", {"points": [v(-81.22, 7.99) * mm, v(-81.16, 8) * mm, v(-81.1, 8.03) * mm, v(-81.03, 8.06) * mm]});
            skFitSpline(sketch, "E2808", {"points": [v(-81.03, 8.06) * mm, v(-81.1, 8.45) * mm, v(-81.17, 8.83) * mm, v(-81.23, 9.22) * mm]});
            skFitSpline(sketch, "E2809", {"points": [v(-81.23, 9.22) * mm, v(-81.27, 9.49) * mm, v(-81.3, 9.76) * mm, v(-81.31, 10.03) * mm]});
            skFitSpline(sketch, "E2810", {"points": [v(-81.31, 10.03) * mm, v(-81.32, 10.33) * mm, v(-81.08, 10.54) * mm, v(-80.8, 10.52) * mm]});
            skFitSpline(sketch, "E2811", {"points": [v(-80.8, 10.52) * mm, v(-80.55, 10.5) * mm, v(-80.39, 10.33) * mm, v(-80.35, 10.07) * mm]});
            skFitSpline(sketch, "E2812", {"points": [v(-80.35, 10.07) * mm, v(-80.27, 9.54) * mm, v(-80.19, 9.01) * mm, v(-80.12, 8.49) * mm]});
            skFitSpline(sketch, "E2813", {"points": [v(-80.12, 8.49) * mm, v(-80.09, 8.26) * mm, v(-80, 8.1) * mm, v(-79.8, 8) * mm]});
            skFitSpline(sketch, "E2814", {"points": [v(-79.8, 8) * mm, v(-79.24, 7.66) * mm, v(-78.7, 7.3) * mm, v(-78.15, 6.97) * mm]});
            skFitSpline(sketch, "E2815", {"points": [v(-78.15, 6.97) * mm, v(-78.11, 6.94) * mm, v(-78.07, 6.93) * mm, v(-78, 6.94) * mm]});
            skFitSpline(sketch, "E2816", {"points": [v(-78, 6.94) * mm, v(-78.11, 7.1) * mm, v(-78.23, 7.27) * mm, v(-78.35, 7.43) * mm]});
            skFitSpline(sketch, "E2817", {"points": [v(-78.35, 7.43) * mm, v(-78.62, 7.79) * mm, v(-78.89, 8.14) * mm, v(-79.16, 8.5) * mm]});
            skFitSpline(sketch, "E2818", {"points": [v(-79.16, 8.5) * mm, v(-79.25, 8.63) * mm, v(-79.31, 8.76) * mm, v(-79.27, 8.92) * mm]});
            skFitSpline(sketch, "E2819", {"points": [v(-79.27, 8.92) * mm, v(-79.22, 9.12) * mm, v(-79.1, 9.25) * mm, v(-78.9, 9.3) * mm]});
            skFitSpline(sketch, "E2820", {"points": [v(-78.9, 9.3) * mm, v(-78.71, 9.34) * mm, v(-78.53, 9.3) * mm, v(-78.4, 9.13) * mm]});
            skFitSpline(sketch, "E2821", {"points": [v(-78.4, 9.13) * mm, v(-78.25, 8.92) * mm, v(-78.1, 8.7) * mm, v(-77.94, 8.5) * mm]});
            skFitSpline(sketch, "E2822", {"points": [v(-77.94, 8.5) * mm, v(-77.56, 7.98) * mm, v(-77.18, 7.47) * mm, v(-76.77, 6.97) * mm]});
            skFitSpline(sketch, "E2823", {"points": [v(-76.77, 6.97) * mm, v(-76.84, 7.2) * mm, v(-76.9, 7.42) * mm, v(-76.96, 7.65) * mm]});
            skFitSpline(sketch, "E2824", {"points": [v(-76.96, 7.65) * mm, v(-76.99, 7.74) * mm, v(-77.03, 7.83) * mm, v(-77.06, 7.92) * mm]});
            skFitSpline(sketch, "E2825", {"points": [v(-77.06, 7.92) * mm, v(-77.09, 8.01) * mm, v(-77.12, 8.1) * mm, v(-77.13, 8.2) * mm]});
            skFitSpline(sketch, "E2826", {"points": [v(-77.13, 8.2) * mm, v(-77.17, 8.46) * mm, v(-77.03, 8.68) * mm, v(-76.8, 8.74) * mm]});
            skFitSpline(sketch, "E2827", {"points": [v(-76.8, 8.74) * mm, v(-76.54, 8.8) * mm, v(-76.3, 8.7) * mm, v(-76.2, 8.44) * mm]});
            skFitSpline(sketch, "E2828", {"points": [v(-76.2, 8.44) * mm, v(-76.12, 8.24) * mm, v(-76.06, 8.03) * mm, v(-76, 7.83) * mm]});
            skFitSpline(sketch, "E2829", {"points": [v(-76, 7.83) * mm, v(-75.87, 7.45) * mm, v(-75.75, 7.07) * mm, v(-75.64, 6.69) * mm]});
            skFitSpline(sketch, "E2830", {"points": [v(-75.64, 6.69) * mm, v(-75.56, 6.42) * mm, v(-75.48, 6.15) * mm, v(-75.4, 5.88) * mm]});
            skFitSpline(sketch, "E2831", {"points": [v(-75.4, 5.88) * mm, v(-75.38, 5.8) * mm, v(-75.35, 5.7) * mm, v(-75.32, 5.59) * mm]});
            skFitSpline(sketch, "E2832", {"points": [v(-75.32, 5.59) * mm, v(-74.95, 5.72) * mm, v(-74.6, 5.84) * mm, v(-74.27, 5.97) * mm]});
            skFitSpline(sketch, "E2833", {"points": [v(-74.27, 5.97) * mm, v(-74.02, 6.06) * mm, v(-73.77, 6.15) * mm, v(-73.53, 6.25) * mm]});
            skFitSpline(sketch, "E2834", {"points": [v(-73.53, 6.25) * mm, v(-73.45, 6.28) * mm, v(-73.37, 6.34) * mm, v(-73.34, 6.41) * mm]});
            skFitSpline(sketch, "E2835", {"points": [v(-73.34, 6.41) * mm, v(-73.1, 7.01) * mm, v(-72.88, 7.62) * mm, v(-72.65, 8.24) * mm]});
            skFitSpline(sketch, "E2836", {"points": [v(-72.65, 8.24) * mm, v(-72.86, 8.3) * mm, v(-73.06, 8.36) * mm, v(-73.24, 8.42) * mm]});
            skFitSpline(sketch, "E2837", {"points": [v(-73.24, 8.42) * mm, v(-73.7, 8.56) * mm, v(-74.16, 8.7) * mm, v(-74.61, 8.85) * mm]});
            skFitSpline(sketch, "E2838", {"points": [v(-74.61, 8.85) * mm, v(-74.9, 8.94) * mm, v(-75.2, 9.02) * mm, v(-75.48, 9.12) * mm]});
            skFitSpline(sketch, "E2839", {"points": [v(-75.48, 9.12) * mm, v(-75.8, 9.23) * mm, v(-75.93, 9.56) * mm, v(-75.77, 9.83) * mm]});
            skFitSpline(sketch, "E2840", {"points": [v(-75.77, 9.83) * mm, v(-75.68, 10) * mm, v(-75.48, 10.1) * mm, v(-75.29, 10.07) * mm]});
            skFitSpline(sketch, "E2841", {"points": [v(-75.29, 10.07) * mm, v(-75.17, 10.05) * mm, v(-75.06, 10) * mm, v(-74.94, 9.97) * mm]});
            skFitSpline(sketch, "E2842", {"points": [v(-74.94, 9.97) * mm, v(-74.64, 9.88) * mm, v(-74.34, 9.78) * mm, v(-74.01, 9.72) * mm]});
            skFitSpline(sketch, "E2843", {"points": [v(-74.01, 9.72) * mm, v(-74.06, 9.76) * mm, v(-74.11, 9.8) * mm, v(-74.16, 9.84) * mm]});
            skFitSpline(sketch, "E2844", {"points": [v(-74.16, 9.84) * mm, v(-74.55, 10.13) * mm, v(-74.95, 10.42) * mm, v(-75.34, 10.7) * mm]});
            skFitSpline(sketch, "E2845", {"points": [v(-75.34, 10.7) * mm, v(-75.6, 10.9) * mm, v(-75.87, 11.1) * mm, v(-76.13, 11.28) * mm]});
            skFitSpline(sketch, "E2846", {"points": [v(-76.13, 11.28) * mm, v(-76.26, 11.37) * mm, v(-76.35, 11.47) * mm, v(-76.37, 11.63) * mm]});
            skFitSpline(sketch, "E2847", {"points": [v(-76.37, 11.63) * mm, v(-76.4, 11.83) * mm, v(-76.34, 12.01) * mm, v(-76.16, 12.13) * mm]});
            skFitSpline(sketch, "E2848", {"points": [v(-76.16, 12.13) * mm, v(-75.97, 12.25) * mm, v(-75.78, 12.24) * mm, v(-75.6, 12.1) * mm]});
            skFitSpline(sketch, "E2849", {"points": [v(-75.6, 12.1) * mm, v(-75.25, 11.85) * mm, v(-74.9, 11.58) * mm, v(-74.54, 11.32) * mm]});
            skFitSpline(sketch, "E2850", {"points": [v(-74.54, 11.32) * mm, v(-74.37, 11.18) * mm, v(-74.19, 11.05) * mm, v(-74, 10.92) * mm]});
            skFitSpline(sketch, "E2851", {"points": [v(-74, 10.92) * mm, v(-74, 10.93) * mm, v(-73.98, 10.93) * mm, v(-73.97, 10.94) * mm]});
            skFitSpline(sketch, "E2852", {"points": [v(-73.97, 10.94) * mm, v(-74.05, 11.09) * mm, v(-74.12, 11.23) * mm, v(-74.2, 11.37) * mm]});
            skFitSpline(sketch, "E2853", {"points": [v(-74.2, 11.37) * mm, v(-74.36, 11.63) * mm, v(-74.52, 11.9) * mm, v(-74.7, 12.16) * mm]});
            skFitSpline(sketch, "E2854", {"points": [v(-74.7, 12.16) * mm, v(-74.85, 12.4) * mm, v(-75, 12.65) * mm, v(-75.17, 12.88) * mm]});
            skFitSpline(sketch, "E2855", {"points": [v(-75.17, 12.88) * mm, v(-75.21, 12.94) * mm, v(-75.3, 12.99) * mm, v(-75.37, 13) * mm]});
            skFitSpline(sketch, "E2856", {"points": [v(-75.37, 13) * mm, v(-75.93, 13.1) * mm, v(-76.5, 13.2) * mm, v(-77.07, 13.26) * mm]});
            skFitSpline(sketch, "E2857", {"points": [v(-77.07, 13.26) * mm, v(-77.42, 13.3) * mm, v(-77.66, 13.55) * mm, v(-77.59, 13.86) * mm]});
            skFitSpline(sketch, "E2858", {"points": [v(-77.59, 13.86) * mm, v(-77.53, 14.09) * mm, v(-77.38, 14.23) * mm, v(-77.14, 14.22) * mm]});
            skFitSpline(sketch, "E2859", {"points": [v(-77.14, 14.22) * mm, v(-76.8, 14.2) * mm, v(-76.46, 14.17) * mm, v(-76.12, 14.13) * mm]});
            skFitSpline(sketch, "E2860", {"points": [v(-76.12, 14.13) * mm, v(-75.8, 14.09) * mm, v(-75.48, 14.02) * mm, v(-75.13, 13.96) * mm]});
            skFitSpline(sketch, "E2861", {"points": [v(-75.13, 13.96) * mm, v(-75.1, 14.03) * mm, v(-75.08, 14.1) * mm, v(-75.05, 14.18) * mm]});
            skFitSpline(sketch, "E2862", {"points": [v(-75.05, 14.18) * mm, v(-74.85, 14.68) * mm, v(-74.65, 15.19) * mm, v(-74.45, 15.7) * mm]});
            skFitSpline(sketch, "E2863", {"points": [v(-74.45, 15.7) * mm, v(-74.42, 15.77) * mm, v(-74.37, 15.85) * mm, v(-74.3, 15.91) * mm]});
            skFitSpline(sketch, "E2864", {"points": [v(-74.3, 15.91) * mm, v(-74.15, 16.08) * mm, v(-73.93, 16.11) * mm, v(-73.74, 16) * mm]});
            skFitSpline(sketch, "E2865", {"points": [v(-73.74, 16) * mm, v(-73.54, 15.9) * mm, v(-73.44, 15.68) * mm, v(-73.5, 15.46) * mm]});
            skFitSpline(sketch, "E2866", {"points": [v(-73.5, 15.46) * mm, v(-73.51, 15.38) * mm, v(-73.55, 15.31) * mm, v(-73.58, 15.24) * mm]});
            skFitSpline(sketch, "E2867", {"points": [v(-73.58, 15.24) * mm, v(-73.77, 14.75) * mm, v(-73.96, 14.27) * mm, v(-74.15, 13.8) * mm]});
            skFitSpline(sketch, "E2868", {"points": [v(-74.15, 13.8) * mm, v(-74.22, 13.63) * mm, v(-74.2, 13.5) * mm, v(-74.12, 13.34) * mm]});
            skFitSpline(sketch, "E2869", {"points": [v(-74.12, 13.34) * mm, v(-73.81, 12.78) * mm, v(-73.52, 12.2) * mm, v(-73.23, 11.64) * mm]});
            skFitSpline(sketch, "E2870", {"points": [v(-73.23, 11.64) * mm, v(-73.19, 11.58) * mm, v(-73.14, 11.52) * mm, v(-73.06, 11.47) * mm]});
            skFitSpline(sketch, "E2871", {"points": [v(-73.06, 11.47) * mm, v(-73.08, 11.64) * mm, v(-73.09, 11.82) * mm, v(-73.11, 12) * mm]});
            skFitSpline(sketch, "E2872", {"points": [v(-73.11, 12) * mm, v(-73.17, 12.45) * mm, v(-73.23, 12.9) * mm, v(-73.28, 13.35) * mm]});
            skFitSpline(sketch, "E2873", {"points": [v(-73.28, 13.35) * mm, v(-73.29, 13.4) * mm, v(-73.29, 13.45) * mm, v(-73.29, 13.5) * mm]});
            skFitSpline(sketch, "E2874", {"points": [v(-73.29, 13.5) * mm, v(-73.28, 13.78) * mm, v(-73.1, 13.97) * mm, v(-72.84, 13.98) * mm]});
            skFitSpline(sketch, "E2875", {"points": [v(-72.84, 13.98) * mm, v(-72.56, 14) * mm, v(-72.36, 13.83) * mm, v(-72.33, 13.55) * mm]});
            skFitSpline(sketch, "E2876", {"points": [v(-72.33, 13.55) * mm, v(-72.23, 12.69) * mm, v(-72.14, 11.82) * mm, v(-72.04, 10.96) * mm]});
            skFitSpline(sketch, "E2877", {"points": [v(-72.04, 10.96) * mm, v(-72.04, 10.93) * mm, v(-72.04, 10.9) * mm, v(-72.03, 10.85) * mm]});
            skFitSpline(sketch, "E2878", {"points": [v(-72.03, 10.85) * mm, v(-72, 10.89) * mm, v(-71.98, 10.9) * mm, v(-71.98, 10.92) * mm]});
            skFitSpline(sketch, "E2879", {"points": [v(-71.98, 10.92) * mm, v(-71.9, 11.22) * mm, v(-71.83, 11.52) * mm, v(-71.76, 11.83) * mm]});
            skFitSpline(sketch, "E2880", {"points": [v(-71.76, 11.83) * mm, v(-71.74, 11.93) * mm, v(-71.72, 12.03) * mm, v(-71.69, 12.13) * mm]});
            skFitSpline(sketch, "E2881", {"points": [v(-71.69, 12.13) * mm, v(-71.6, 12.37) * mm, v(-71.38, 12.48) * mm, v(-71.13, 12.44) * mm]});
            skFitSpline(sketch, "E2882", {"points": [v(-71.13, 12.44) * mm, v(-70.9, 12.4) * mm, v(-70.74, 12.2) * mm, v(-70.77, 11.95) * mm]});
            skFitSpline(sketch, "E2883", {"points": [v(-70.77, 11.95) * mm, v(-70.79, 11.7) * mm, v(-70.84, 11.45) * mm, v(-70.9, 11.2) * mm]});
            skFitSpline(sketch, "E2884", {"points": [v(-70.9, 11.2) * mm, v(-71.02, 10.63) * mm, v(-71.15, 10.06) * mm, v(-71.29, 9.5) * mm]});
            skFitSpline(sketch, "E2885", {"points": [v(-71.29, 9.5) * mm, v(-71.33, 9.33) * mm, v(-71.37, 9.16) * mm, v(-71.42, 8.97) * mm]});
            skFitSpline(sketch, "E2886", {"points": [v(-71.42, 8.97) * mm, v(-71.23, 8.93) * mm, v(-71.05, 8.88) * mm, v(-70.87, 8.85) * mm]});
            skFitSpline(sketch, "E2887", {"points": [v(-70.87, 8.85) * mm, v(-70.43, 8.78) * mm, v(-69.98, 8.7) * mm, v(-69.53, 8.63) * mm]});
            skFitSpline(sketch, "E2888", {"points": [v(-69.53, 8.63) * mm, v(-69.43, 8.62) * mm, v(-69.36, 8.63) * mm, v(-69.28, 8.69) * mm]});
            skFitSpline(sketch, "E2889", {"points": [v(-69.28, 8.69) * mm, v(-68.8, 9.1) * mm, v(-68.3, 9.5) * mm, v(-67.8, 9.92) * mm]});
            skFitSpline(sketch, "E2890", {"points": [v(-67.8, 9.92) * mm, v(-67.84, 9.98) * mm, v(-67.86, 10.02) * mm, v(-67.9, 10.06) * mm]});
            skFitSpline(sketch, "E2891", {"points": [v(-67.9, 10.06) * mm, v(-68.31, 10.5) * mm, v(-68.73, 10.95) * mm, v(-69.14, 11.4) * mm]});
            skFitSpline(sketch, "E2892", {"points": [v(-69.14, 11.4) * mm, v(-69.35, 11.62) * mm, v(-69.56, 11.84) * mm, v(-69.76, 12.06) * mm]});
            skFitSpline(sketch, "E2893", {"points": [v(-69.76, 12.06) * mm, v(-69.81, 12.13) * mm, v(-69.87, 12.2) * mm, v(-69.9, 12.28) * mm]});
            skFitSpline(sketch, "E2894", {"points": [v(-69.9, 12.28) * mm, v(-69.98, 12.48) * mm, v(-69.91, 12.7) * mm, v(-69.75, 12.82) * mm]});
            skFitSpline(sketch, "E2895", {"points": [v(-69.75, 12.82) * mm, v(-69.6, 12.95) * mm, v(-69.36, 12.97) * mm, v(-69.2, 12.85) * mm]});
            skFitSpline(sketch, "E2896", {"points": [v(-69.2, 12.85) * mm, v(-69.1, 12.78) * mm, v(-69, 12.68) * mm, v(-68.92, 12.58) * mm]});
            skFitSpline(sketch, "E2897", {"points": [v(-68.92, 12.58) * mm, v(-68.7, 12.35) * mm, v(-68.47, 12.1) * mm, v(-68.22, 11.89) * mm]});
            skFitSpline(sketch, "E2898", {"points": [v(-68.22, 11.89) * mm, v(-68.24, 11.95) * mm, v(-68.27, 12) * mm, v(-68.3, 12.07) * mm]});
            skFitSpline(sketch, "E2899", {"points": [v(-68.3, 12.07) * mm, v(-68.5, 12.53) * mm, v(-68.7, 13) * mm, v(-68.9, 13.45) * mm]});
            skFitSpline(sketch, "E2900", {"points": [v(-68.9, 13.45) * mm, v(-69.03, 13.75) * mm, v(-69.16, 14.06) * mm, v(-69.3, 14.35) * mm]});
            skFitSpline(sketch, "E2901", {"points": [v(-69.3, 14.35) * mm, v(-69.45, 14.64) * mm, v(-69.22, 15.08) * mm, v(-68.8, 15.04) * mm]});
            skFitSpline(sketch, "E2902", {"points": [v(-68.8, 15.04) * mm, v(-68.6, 15.02) * mm, v(-68.47, 14.91) * mm, v(-68.4, 14.73) * mm]});
            skFitSpline(sketch, "E2903", {"points": [v(-68.4, 14.73) * mm, v(-68.22, 14.32) * mm, v(-68.05, 13.9) * mm, v(-67.87, 13.5) * mm]});
            skFitSpline(sketch, "E2904", {"points": [v(-67.87, 13.5) * mm, v(-67.79, 13.3) * mm, v(-67.7, 13.12) * mm, v(-67.58, 12.93) * mm]});
            skFitSpline(sketch, "E2905", {"points": [v(-67.58, 12.93) * mm, v(-67.57, 12.98) * mm, v(-67.55, 13.02) * mm, v(-67.55, 13.07) * mm]});
            skFitSpline(sketch, "E2906", {"points": [v(-67.55, 13.07) * mm, v(-67.56, 13.6) * mm, v(-67.58, 14.15) * mm, v(-67.6, 14.7) * mm]});
            skFitSpline(sketch, "E2907", {"points": [v(-67.6, 14.7) * mm, v(-67.6, 14.83) * mm, v(-67.64, 14.96) * mm, v(-67.63, 15.1) * mm]});
            skFitSpline(sketch, "E2908", {"points": [v(-67.63, 15.1) * mm, v(-67.63, 15.26) * mm, v(-67.7, 15.37) * mm, v(-67.82, 15.47) * mm]});
            skFitSpline(sketch, "E2909", {"points": [v(-67.82, 15.47) * mm, v(-68.21, 15.78) * mm, v(-68.61, 16.1) * mm, v(-69.01, 16.42) * mm]});
            skFitSpline(sketch, "E2910", {"points": [v(-69.01, 16.42) * mm, v(-69.06, 16.46) * mm, v(-69.12, 16.5) * mm, v(-69.17, 16.54) * mm]});
            skFitSpline(sketch, "E2911", {"points": [v(-69.17, 16.54) * mm, v(-69.4, 16.72) * mm, v(-69.44, 17) * mm, v(-69.28, 17.22) * mm]});
            skFitSpline(sketch, "E2912", {"points": [v(-69.28, 17.22) * mm, v(-69.13, 17.43) * mm, v(-68.84, 17.49) * mm, v(-68.6, 17.33) * mm]});
            skFitSpline(sketch, "E2913", {"points": [v(-68.6, 17.33) * mm, v(-68.36, 17.16) * mm, v(-68.12, 16.98) * mm, v(-67.89, 16.8) * mm]});
            skFitSpline(sketch, "E2914", {"points": [v(-67.89, 16.8) * mm, v(-67.61, 16.58) * mm, v(-67.35, 16.35) * mm, v(-67.07, 16.12) * mm]});
            skFitSpline(sketch, "E2915", {"points": [v(-67.07, 16.12) * mm, v(-66.8, 16.34) * mm, v(-66.55, 16.57) * mm, v(-66.28, 16.78) * mm]});
            skFitSpline(sketch, "E2916", {"points": [v(-66.28, 16.78) * mm, v(-66.05, 16.96) * mm, v(-65.8, 17.14) * mm, v(-65.57, 17.31) * mm]});
            skFitSpline(sketch, "E2917", {"points": [v(-65.57, 17.31) * mm, v(-65.38, 17.44) * mm, v(-65.18, 17.47) * mm, v(-64.98, 17.34) * mm]});
            skFitSpline(sketch, "E2918", {"points": [v(-64.98, 17.34) * mm, v(-64.73, 17.17) * mm, v(-64.7, 16.83) * mm, v(-64.9, 16.6) * mm]});
            skFitSpline(sketch, "E2919", {"points": [v(-64.9, 16.6) * mm, v(-64.95, 16.55) * mm, v(-65.02, 16.5) * mm, v(-65.08, 16.46) * mm]});
            skFitSpline(sketch, "E2920", {"points": [v(-65.08, 16.46) * mm, v(-65.47, 16.15) * mm, v(-65.86, 15.84) * mm, v(-66.25, 15.54) * mm]});
            skFitSpline(sketch, "E2921", {"points": [v(-66.25, 15.54) * mm, v(-66.42, 15.4) * mm, v(-66.51, 15.25) * mm, v(-66.52, 15.03) * mm]});
            skFitSpline(sketch, "E2922", {"points": [v(-66.52, 15.03) * mm, v(-66.54, 14.35) * mm, v(-66.56, 13.66) * mm, v(-66.58, 12.98) * mm]});
            skFitSpline(sketch, "E2923", {"points": [v(-66.58, 12.98) * mm, v(-66.59, 12.96) * mm, v(-66.57, 12.94) * mm, v(-66.55, 12.87) * mm]});
            skFitSpline(sketch, "E2924", {"points": [v(-66.55, 12.87) * mm, v(-66.45, 13.1) * mm, v(-66.36, 13.28) * mm, v(-66.28, 13.47) * mm]});
            skFitSpline(sketch, "E2925", {"points": [v(-66.28, 13.47) * mm, v(-66.1, 13.89) * mm, v(-65.93, 14.3) * mm, v(-65.75, 14.72) * mm]});
            skFitSpline(sketch, "E2926", {"points": [v(-65.75, 14.72) * mm, v(-65.61, 15.03) * mm, v(-65.28, 15.14) * mm, v(-65.02, 14.97) * mm]});
            skFitSpline(sketch, "E2927", {"points": [v(-65.02, 14.97) * mm, v(-64.82, 14.83) * mm, v(-64.74, 14.6) * mm, v(-64.85, 14.35) * mm]});
            skFitSpline(sketch, "E2928", {"points": [v(-64.85, 14.35) * mm, v(-65.16, 13.62) * mm, v(-65.49, 12.89) * mm, v(-65.8, 12.16) * mm]});
            skFitSpline(sketch, "E2929", {"points": [v(-65.8, 12.16) * mm, v(-65.84, 12.08) * mm, v(-65.88, 12) * mm, v(-65.91, 11.92) * mm]});
            skFitSpline(sketch, "E2930", {"points": [v(-65.91, 11.92) * mm, v(-65.9, 11.91) * mm, v(-65.88, 11.9) * mm, v(-65.87, 11.9) * mm]});
            skFitSpline(sketch, "E2931", {"points": [v(-65.87, 11.9) * mm, v(-65.66, 12.12) * mm, v(-65.45, 12.34) * mm, v(-65.25, 12.56) * mm]});
            skFitSpline(sketch, "E2932", {"points": [v(-65.25, 12.56) * mm, v(-65.18, 12.63) * mm, v(-65.11, 12.72) * mm, v(-65.04, 12.79) * mm]});
            skFitSpline(sketch, "E2933", {"points": [v(-65.04, 12.79) * mm, v(-64.83, 12.97) * mm, v(-64.55, 12.97) * mm, v(-64.36, 12.8) * mm]});
            skFitSpline(sketch, "E2934", {"points": [v(-64.36, 12.8) * mm, v(-64.17, 12.62) * mm, v(-64.16, 12.32) * mm, v(-64.35, 12.1) * mm]});
            skFitSpline(sketch, "E2935", {"points": [v(-64.35, 12.1) * mm, v(-64.6, 11.82) * mm, v(-64.87, 11.54) * mm, v(-65.13, 11.26) * mm]});
            skFitSpline(sketch, "E2936", {"points": [v(-65.13, 11.26) * mm, v(-65.53, 10.83) * mm, v(-65.92, 10.39) * mm, v(-66.34, 9.94) * mm]});
            skFitSpline(sketch, "E2937", {"points": [v(-66.34, 9.94) * mm, v(-66.22, 9.83) * mm, v(-66.1, 9.71) * mm, v(-65.98, 9.6) * mm]});
            skFitSpline(sketch, "E2938", {"points": [v(-65.98, 9.6) * mm, v(-65.62, 9.3) * mm, v(-65.25, 9.01) * mm, v(-64.89, 8.71) * mm]});
            skFitSpline(sketch, "E2939", {"points": [v(-64.89, 8.71) * mm, v(-64.81, 8.65) * mm, v(-64.74, 8.6) * mm, v(-64.63, 8.63) * mm]});
            skFitSpline(sketch, "E2940", {"points": [v(-64.63, 8.63) * mm, v(-64.02, 8.74) * mm, v(-63.42, 8.84) * mm, v(-62.81, 8.94) * mm]});
            skFitSpline(sketch, "E2941", {"points": [v(-62.81, 8.94) * mm, v(-62.8, 8.95) * mm, v(-62.77, 8.96) * mm, v(-62.74, 8.98) * mm]});
            skFitSpline(sketch, "E2942", {"points": [v(-62.74, 8.98) * mm, v(-62.75, 9.03) * mm, v(-62.75, 9.09) * mm, v(-62.76, 9.14) * mm]});
            skFitSpline(sketch, "E2943", {"points": [v(-62.76, 9.14) * mm, v(-62.9, 9.72) * mm, v(-63.03, 10.3) * mm, v(-63.16, 10.89) * mm]});
            skFitSpline(sketch, "E2944", {"points": [v(-63.16, 10.89) * mm, v(-63.24, 11.2) * mm, v(-63.3, 11.5) * mm, v(-63.37, 11.82) * mm]});
            skFitSpline(sketch, "E2945", {"points": [v(-63.37, 11.82) * mm, v(-63.43, 12.1) * mm, v(-63.3, 12.36) * mm, v(-63.05, 12.43) * mm]});
            skFitSpline(sketch, "E2946", {"points": [v(-63.05, 12.43) * mm, v(-62.77, 12.5) * mm, v(-62.52, 12.37) * mm, v(-62.44, 12.07) * mm]});
            skFitSpline(sketch, "E2947", {"points": [v(-62.44, 12.07) * mm, v(-62.35, 11.76) * mm, v(-62.29, 11.44) * mm, v(-62.21, 11.12) * mm]});
            skFitSpline(sketch, "E2948", {"points": [v(-62.21, 11.12) * mm, v(-62.2, 11.04) * mm, v(-62.17, 10.95) * mm, v(-62.12, 10.87) * mm]});
            skFitSpline(sketch, "E2949", {"points": [v(-62.12, 10.87) * mm, v(-62.1, 11) * mm, v(-62.1, 11.13) * mm, v(-62.08, 11.26) * mm]});
            skFitSpline(sketch, "E2950", {"points": [v(-62.08, 11.26) * mm, v(-62.04, 11.64) * mm, v(-62, 12.03) * mm, v(-61.95, 12.42) * mm]});
            skFitSpline(sketch, "E2951", {"points": [v(-61.95, 12.42) * mm, v(-61.92, 12.74) * mm, v(-61.87, 13.07) * mm, v(-61.84, 13.4) * mm]});
            skFitSpline(sketch, "E2952", {"points": [v(-61.84, 13.4) * mm, v(-61.83, 13.46) * mm, v(-61.83, 13.54) * mm, v(-61.81, 13.6) * mm]});
            skFitSpline(sketch, "E2953", {"points": [v(-61.81, 13.6) * mm, v(-61.76, 13.85) * mm, v(-61.54, 14) * mm, v(-61.27, 13.98) * mm]});
            skFitSpline(sketch, "E2954", {"points": [v(-61.27, 13.98) * mm, v(-61.04, 13.96) * mm, v(-60.83, 13.73) * mm, v(-60.86, 13.5) * mm]});
            skFitSpline(sketch, "E2955", {"points": [v(-60.86, 13.5) * mm, v(-60.88, 13.34) * mm, v(-60.89, 13.17) * mm, v(-60.9, 13) * mm]});
            skFitSpline(sketch, "E2956", {"points": [v(-60.9, 13) * mm, v(-60.97, 12.49) * mm, v(-61.03, 11.97) * mm, v(-61.05, 11.43) * mm]});
            skFitSpline(sketch, "E2957", {"points": [v(-61.05, 11.43) * mm, v(-60.96, 11.58) * mm, v(-60.86, 11.73) * mm, v(-60.78, 11.9) * mm]});
            skFitSpline(sketch, "E2958", {"points": [v(-60.78, 11.9) * mm, v(-60.66, 12.1) * mm, v(-60.54, 12.32) * mm, v(-60.43, 12.54) * mm]});
            skFitSpline(sketch, "E2959", {"points": [v(-60.43, 12.54) * mm, v(-60.27, 12.84) * mm, v(-60.11, 13.14) * mm, v(-59.97, 13.44) * mm]});
            skFitSpline(sketch, "E2960", {"points": [v(-59.97, 13.44) * mm, v(-59.94, 13.52) * mm, v(-59.94, 13.63) * mm, v(-59.97, 13.72) * mm]});
            skFitSpline(sketch, "E2961", {"points": [v(-59.97, 13.72) * mm, v(-60.14, 14.19) * mm, v(-60.33, 14.66) * mm, v(-60.5, 15.13) * mm]});
            skFitSpline(sketch, "E2962", {"points": [v(-60.5, 15.13) * mm, v(-60.54, 15.22) * mm, v(-60.6, 15.31) * mm, v(-60.63, 15.41) * mm]});
            skFitSpline(sketch, "E2963", {"points": [v(-60.63, 15.41) * mm, v(-60.72, 15.66) * mm, v(-60.61, 15.9) * mm, v(-60.39, 16.02) * mm]});
            skFitSpline(sketch, "E2964", {"points": [v(-60.39, 16.02) * mm, v(-60.17, 16.12) * mm, v(-59.92, 16.06) * mm, v(-59.78, 15.84) * mm]});
            skFitSpline(sketch, "E2965", {"points": [v(-59.78, 15.84) * mm, v(-59.69, 15.7) * mm, v(-59.62, 15.55) * mm, v(-59.56, 15.4) * mm]});
            skFitSpline(sketch, "E2966", {"points": [v(-59.56, 15.4) * mm, v(-59.4, 15) * mm, v(-59.25, 14.59) * mm, v(-59.1, 14.18) * mm]});
            skFitSpline(sketch, "E2967", {"points": [v(-59.1, 14.18) * mm, v(-59.07, 14.12) * mm, v(-59.05, 14.05) * mm, v(-59.02, 13.96) * mm]});
            skFitSpline(sketch, "E2968", {"points": [v(-59.02, 13.96) * mm, v(-58.95, 13.97) * mm, v(-58.88, 13.98) * mm, v(-58.8, 13.99) * mm]});
            skFitSpline(sketch, "E2969", {"points": [v(-58.8, 13.99) * mm, v(-58.37, 14.06) * mm, v(-57.93, 14.14) * mm, v(-57.49, 14.2) * mm]});
            skFitSpline(sketch, "E2970", {"points": [v(-57.49, 14.2) * mm, v(-57.33, 14.22) * mm, v(-57.17, 14.21) * mm, v(-57, 14.22) * mm]});
            skFitSpline(sketch, "E2971", {"points": [v(-57, 14.22) * mm, v(-56.77, 14.24) * mm, v(-56.6, 14.04) * mm, v(-56.56, 13.87) * mm]});
            skFitSpline(sketch, "E2972", {"points": [v(-56.56, 13.87) * mm, v(-56.5, 13.64) * mm, v(-56.6, 13.43) * mm, v(-56.81, 13.33) * mm]});
            skFitSpline(sketch, "E2973", {"points": [v(-56.81, 13.33) * mm, v(-56.88, 13.3) * mm, v(-56.96, 13.28) * mm, v(-57.04, 13.27) * mm]});
            skFitSpline(sketch, "E2974", {"points": [v(-57.04, 13.27) * mm, v(-57.6, 13.18) * mm, v(-58.16, 13.1) * mm, v(-58.72, 13.01) * mm]});
            skFitSpline(sketch, "E2975", {"points": [v(-58.72, 13.01) * mm, v(-58.86, 13) * mm, v(-58.95, 12.93) * mm, v(-59.02, 12.8) * mm]});
            skFitSpline(sketch, "E2976", {"points": [v(-59.02, 12.8) * mm, v(-59.36, 12.26) * mm, v(-59.71, 11.71) * mm, v(-60.05, 11.17) * mm]});
            skFitSpline(sketch, "E2977", {"points": [v(-60.05, 11.17) * mm, v(-60.1, 11.1) * mm, v(-60.12, 11.03) * mm, v(-60.12, 10.93) * mm]});
            skFitSpline(sketch, "E2978", {"points": [v(-60.12, 10.93) * mm, v(-59.96, 11.05) * mm, v(-59.8, 11.16) * mm, v(-59.65, 11.27) * mm]});
            skFitSpline(sketch, "E2979", {"points": [v(-59.65, 11.27) * mm, v(-59.29, 11.55) * mm, v(-58.93, 11.83) * mm, v(-58.56, 12.1) * mm]});
            skFitSpline(sketch, "E2980", {"points": [v(-58.56, 12.1) * mm, v(-58.3, 12.28) * mm, v(-57.98, 12.23) * mm, v(-57.83, 11.97) * mm]});
            skFitSpline(sketch, "E2981", {"points": [v(-57.83, 11.97) * mm, v(-57.7, 11.75) * mm, v(-57.75, 11.48) * mm, v(-57.97, 11.31) * mm]});
            skFitSpline(sketch, "E2982", {"points": [v(-57.97, 11.31) * mm, v(-58.62, 10.83) * mm, v(-59.27, 10.36) * mm, v(-59.92, 9.88) * mm]});
            skFitSpline(sketch, "E2983", {"points": [v(-59.92, 9.88) * mm, v(-60, 9.83) * mm, v(-60.06, 9.78) * mm, v(-60.12, 9.69) * mm]});
            skFitSpline(sketch, "E2984", {"points": [v(-60.12, 9.69) * mm, v(-59.82, 9.78) * mm, v(-59.51, 9.87) * mm, v(-59.21, 9.96) * mm]});
            skFitSpline(sketch, "E2985", {"points": [v(-59.21, 9.96) * mm, v(-59.11, 10) * mm, v(-59.02, 10.03) * mm, v(-58.92, 10.05) * mm]});
            skFitSpline(sketch, "E2986", {"points": [v(-58.92, 10.05) * mm, v(-58.65, 10.11) * mm, v(-58.4, 9.99) * mm, v(-58.34, 9.76) * mm]});
            skFitSpline(sketch, "E2987", {"points": [v(-58.34, 9.76) * mm, v(-58.27, 9.49) * mm, v(-58.32, 9.26) * mm, v(-58.63, 9.13) * mm]});
            skFitSpline(sketch, "E2988", {"points": [v(-58.63, 9.13) * mm, v(-58.87, 9.03) * mm, v(-59.12, 8.97) * mm, v(-59.36, 8.89) * mm]});
            skFitSpline(sketch, "E2989", {"points": [v(-59.36, 8.89) * mm, v(-59.59, 8.82) * mm, v(-59.82, 8.75) * mm, v(-60.05, 8.68) * mm]});
            skFitSpline(sketch, "E2990", {"points": [v(-60.05, 8.68) * mm, v(-60.44, 8.56) * mm, v(-60.84, 8.44) * mm, v(-61.24, 8.32) * mm]});
            skFitSpline(sketch, "E2991", {"points": [v(-61.24, 8.32) * mm, v(-61.31, 8.3) * mm, v(-61.39, 8.27) * mm, v(-61.49, 8.25) * mm]});
            skFitSpline(sketch, "E2992", {"points": [v(-61.49, 8.25) * mm, v(-61.36, 7.9) * mm, v(-61.24, 7.56) * mm, v(-61.11, 7.22) * mm]});
            skFitSpline(sketch, "E2993", {"points": [v(-61.11, 7.22) * mm, v(-61.02, 6.97) * mm, v(-60.93, 6.71) * mm, v(-60.82, 6.46) * mm]});
            skFitSpline(sketch, "E2994", {"points": [v(-60.82, 6.46) * mm, v(-60.8, 6.4) * mm, v(-60.73, 6.3) * mm, v(-60.67, 6.27) * mm]});
            skFitSpline(sketch, "E2995", {"points": [v(-60.67, 6.27) * mm, v(-60.06, 6.04) * mm, v(-59.46, 5.82) * mm, v(-58.83, 5.58) * mm]});
            skFitSpline(sketch, "E2996", {"points": [v(-58.83, 5.58) * mm, v(-58.76, 5.83) * mm, v(-58.7, 6.04) * mm, v(-58.62, 6.26) * mm]});
            skFitSpline(sketch, "E2997", {"points": [v(-58.62, 6.26) * mm, v(-58.5, 6.67) * mm, v(-58.37, 7.07) * mm, v(-58.24, 7.47) * mm]});
            skFitSpline(sketch, "E2998", {"points": [v(-58.24, 7.47) * mm, v(-58.15, 7.78) * mm, v(-58.06, 8.08) * mm, v(-57.96, 8.39) * mm]});
            skFitSpline(sketch, "E2999", {"points": [v(-57.96, 8.39) * mm, v(-57.87, 8.65) * mm, v(-57.7, 8.77) * mm, v(-57.44, 8.75) * mm]});
            skFitSpline(sketch, "E3000", {"points": [v(-57.44, 8.75) * mm, v(-57.17, 8.74) * mm, v(-56.96, 8.5) * mm, v(-57, 8.23) * mm]});
            skFitSpline(sketch, "E3001", {"points": [v(-57, 8.23) * mm, v(-57.02, 8.1) * mm, v(-57.07, 7.99) * mm, v(-57.1, 7.87) * mm]});
            skFitSpline(sketch, "E3002", {"points": [v(-57.1, 7.87) * mm, v(-57.2, 7.57) * mm, v(-57.29, 7.27) * mm, v(-57.38, 6.98) * mm]});
            skFitSpline(sketch, "E3003", {"points": [v(-57.38, 6.98) * mm, v(-57.36, 6.97) * mm, v(-57.35, 6.96) * mm, v(-57.33, 6.95) * mm]});
            skFitSpline(sketch, "E3004", {"points": [v(-57.33, 6.95) * mm, v(-57.3, 7) * mm, v(-57.25, 7.07) * mm, v(-57.2, 7.13) * mm]});
            skFitSpline(sketch, "E3005", {"points": [v(-57.2, 7.13) * mm, v(-56.72, 7.78) * mm, v(-56.25, 8.44) * mm, v(-55.76, 9.1) * mm]});
            skFitSpline(sketch, "E3006", {"points": [v(-55.76, 9.1) * mm, v(-55.58, 9.34) * mm, v(-55.29, 9.38) * mm, v(-55.06, 9.22) * mm]});
            skFitSpline(sketch, "E3007", {"points": [v(-55.06, 9.22) * mm, v(-54.84, 9.05) * mm, v(-54.8, 8.76) * mm, v(-54.98, 8.52) * mm]});
            skFitSpline(sketch, "E3008", {"points": [v(-54.98, 8.52) * mm, v(-55.32, 8.05) * mm, v(-55.67, 7.58) * mm, v(-56.02, 7.12) * mm]});
            skFitSpline(sketch, "E3009", {"points": [v(-56.02, 7.12) * mm, v(-56.07, 7.06) * mm, v(-56.1, 6.99) * mm, v(-56.12, 6.9) * mm]});
            skFitSpline(sketch, "E3010", {"points": [v(-56.12, 6.9) * mm, v(-55.97, 6.98) * mm, v(-55.8, 7.07) * mm, v(-55.65, 7.16) * mm]});
            skFitSpline(sketch, "E3011", {"points": [v(-55.65, 7.16) * mm, v(-55.46, 7.28) * mm, v(-55.27, 7.4) * mm, v(-55.08, 7.52) * mm]});
            skFitSpline(sketch, "E3012", {"points": [v(-55.08, 7.52) * mm, v(-54.79, 7.7) * mm, v(-54.5, 7.9) * mm, v(-54.2, 8.1) * mm]});
            skFitSpline(sketch, "E3013", {"points": [v(-54.2, 8.1) * mm, v(-54.14, 8.14) * mm, v(-54.08, 8.23) * mm, v(-54.07, 8.3) * mm]});
            skFitSpline(sketch, "E3014", {"points": [v(-54.07, 8.3) * mm, v(-53.96, 8.87) * mm, v(-53.83, 9.43) * mm, v(-53.8, 10) * mm]});
            skFitSpline(sketch, "E3015", {"points": [v(-53.8, 10) * mm, v(-53.8, 10.23) * mm, v(-53.7, 10.41) * mm, v(-53.49, 10.5) * mm]});
            skFitSpline(sketch, "E3016", {"points": [v(-53.49, 10.5) * mm, v(-53.3, 10.56) * mm, v(-53.12, 10.53) * mm, v(-52.97, 10.39) * mm]});
            skFitSpline(sketch, "E3017", {"points": [v(-52.97, 10.39) * mm, v(-52.88, 10.3) * mm, v(-52.85, 10.2) * mm, v(-52.85, 10.06) * mm]});
            skFitSpline(sketch, "E3018", {"points": [v(-52.85, 10.06) * mm, v(-52.84, 9.65) * mm, v(-52.9, 9.25) * mm, v(-52.97, 8.85) * mm]});
            skFitSpline(sketch, "E3019", {"points": [v(-52.97, 8.85) * mm, v(-53.02, 8.6) * mm, v(-53.06, 8.34) * mm, v(-53.11, 8.06) * mm]});
            skFitSpline(sketch, "E3020", {"points": [v(-53.11, 8.06) * mm, v(-53.02, 8.02) * mm, v(-52.94, 8) * mm, v(-52.86, 7.97) * mm]});
            skFitSpline(sketch, "E3021", {"points": [v(-52.86, 7.97) * mm, v(-52.36, 7.77) * mm, v(-51.86, 7.58) * mm, v(-51.37, 7.37) * mm]});
            skFitSpline(sketch, "E3022", {"points": [v(-51.37, 7.37) * mm, v(-51.26, 7.33) * mm, v(-51.16, 7.23) * mm, v(-51.08, 7.13) * mm]});
            skFitSpline(sketch, "E3023", {"points": [v(-51.08, 7.13) * mm, v(-50.96, 6.97) * mm, v(-50.98, 6.79) * mm, v(-51.1, 6.62) * mm]});
            skFitSpline(sketch, "E3024", {"points": [v(-51.1, 6.62) * mm, v(-51.2, 6.46) * mm, v(-51.4, 6.38) * mm, v(-51.6, 6.42) * mm]});
            skFitSpline(sketch, "E3025", {"points": [v(-51.6, 6.42) * mm, v(-51.68, 6.44) * mm, v(-51.76, 6.48) * mm, v(-51.84, 6.52) * mm]});
            skFitSpline(sketch, "E3026", {"points": [v(-51.84, 6.52) * mm, v(-52.32, 6.7) * mm, v(-52.8, 6.9) * mm, v(-53.29, 7.08) * mm]});
            skFitSpline(sketch, "E3027", {"points": [v(-53.29, 7.08) * mm, v(-53.45, 7.15) * mm, v(-53.59, 7.14) * mm, v(-53.74, 7.05) * mm]});
            skFitSpline(sketch, "E3028", {"points": [v(-53.74, 7.05) * mm, v(-54.24, 6.77) * mm, v(-54.76, 6.51) * mm, v(-55.27, 6.25) * mm]});
            skFitSpline(sketch, "E3029", {"points": [v(-55.27, 6.25) * mm, v(-55.38, 6.18) * mm, v(-55.5, 6.11) * mm, v(-55.6, 6.04) * mm]});
            skFitSpline(sketch, "E3030", {"points": [v(-55.6, 6.04) * mm, v(-55.6, 6.03) * mm, v(-55.6, 6.01) * mm, v(-55.6, 6) * mm]});
            skFitSpline(sketch, "E3031", {"points": [v(-55.6, 6) * mm, v(-55.45, 6) * mm, v(-55.3, 6.01) * mm, v(-55.16, 6.03) * mm]});
            skFitSpline(sketch, "E3032", {"points": [v(-55.16, 6.03) * mm, v(-54.69, 6.09) * mm, v(-54.21, 6.15) * mm, v(-53.74, 6.2) * mm]});
            skFitSpline(sketch, "E3033", {"points": [v(-53.74, 6.2) * mm, v(-53.68, 6.2) * mm, v(-53.62, 6.21) * mm, v(-53.57, 6.21) * mm]});
            skFitSpline(sketch, "E3034", {"points": [v(-53.57, 6.21) * mm, v(-53.3, 6.2) * mm, v(-53.12, 6.05) * mm, v(-53.1, 5.8) * mm]});
            skFitSpline(sketch, "E3035", {"points": [v(-53.1, 5.8) * mm, v(-53.06, 5.53) * mm, v(-53.22, 5.3) * mm, v(-53.48, 5.26) * mm]});
            skFitSpline(sketch, "E3036", {"points": [v(-53.48, 5.26) * mm, v(-53.73, 5.22) * mm, v(-53.99, 5.19) * mm, v(-54.24, 5.16) * mm]});
            skFitSpline(sketch, "E3037", {"points": [v(-54.24, 5.16) * mm, v(-54.66, 5.1) * mm, v(-55.08, 5.06) * mm, v(-55.5, 5.02) * mm]});
            skFitSpline(sketch, "E3038", {"points": [v(-55.5, 5.02) * mm, v(-55.69, 5) * mm, v(-55.87, 5) * mm, v(-56.05, 4.98) * mm]});
            skFitSpline(sketch, "E3039", {"points": [v(-56.05, 4.98) * mm, v(-56.09, 4.97) * mm, v(-56.13, 4.96) * mm, v(-56.17, 4.9) * mm]});
            skFitSpline(sketch, "E3040", {"points": [v(-56.17, 4.9) * mm, v(-55.89, 4.84) * mm, v(-55.6, 4.77) * mm, v(-55.31, 4.7) * mm]});
            skFitSpline(sketch, "E3041", {"points": [v(-55.31, 4.7) * mm, v(-55.2, 4.67) * mm, v(-55.08, 4.66) * mm, v(-54.97, 4.62) * mm]});
            skFitSpline(sketch, "E3042", {"points": [v(-54.97, 4.62) * mm, v(-54.7, 4.53) * mm, v(-54.57, 4.3) * mm, v(-54.64, 4.04) * mm]});
            skFitSpline(sketch, "E3043", {"points": [v(-54.64, 4.04) * mm, v(-54.7, 3.8) * mm, v(-54.95, 3.64) * mm, v(-55.22, 3.7) * mm]});
            skFitSpline(sketch, "E3044", {"points": [v(-55.22, 3.7) * mm, v(-55.61, 3.77) * mm, v(-56, 3.87) * mm, v(-56.4, 3.96) * mm]});
            skFitSpline(sketch, "E3045", {"points": [v(-56.4, 3.96) * mm, v(-56.93, 4.08) * mm, v(-57.46, 4.2) * mm, v(-58, 4.32) * mm]});
            skFitSpline(sketch, "E3046", {"points": [v(-58, 4.32) * mm, v(-58.02, 4.33) * mm, v(-58.05, 4.33) * mm, v(-58.11, 4.33) * mm]});
            skFitSpline(sketch, "E3047", {"points": [v(-58.11, 4.33) * mm, v(-58.16, 4.05) * mm, v(-58.22, 3.77) * mm, v(-58.27, 3.5) * mm]});
            skFitSpline(sketch, "E3048", {"points": [v(-58.27, 3.5) * mm, v(-58.33, 3.15) * mm, v(-58.37, 2.81) * mm, v(-58.44, 2.48) * mm]});
            skFitSpline(sketch, "E3049", {"points": [v(-58.44, 2.48) * mm, v(-58.46, 2.36) * mm, v(-58.44, 2.28) * mm, v(-58.37, 2.2) * mm]});
            skFitSpline(sketch, "E3050", {"points": [v(-58.37, 2.2) * mm, v(-57.97, 1.7) * mm, v(-57.56, 1.22) * mm, v(-57.15, 0.72) * mm]});
            skFitSpline(sketch, "E3051", {"points": [v(-57.15, 0.72) * mm, v(-57.1, 0.76) * mm, v(-57.05, 0.79) * mm, v(-57.01, 0.83) * mm]});
            skFitSpline(sketch, "E3052", {"points": [v(-57.01, 0.83) * mm, v(-56.57, 1.24) * mm, v(-56.12, 1.65) * mm, v(-55.68, 2.07) * mm]});
            skFitSpline(sketch, "E3053", {"points": [v(-55.68, 2.07) * mm, v(-55.46, 2.27) * mm, v(-55.24, 2.48) * mm, v(-55.01, 2.68) * mm]});
            skFitSpline(sketch, "E3054", {"points": [v(-55.01, 2.68) * mm, v(-54.94, 2.74) * mm, v(-54.86, 2.8) * mm, v(-54.77, 2.83) * mm]});
            skFitSpline(sketch, "E3055", {"points": [v(-54.77, 2.83) * mm, v(-54.56, 2.9) * mm, v(-54.34, 2.82) * mm, v(-54.22, 2.64) * mm]});
            skFitSpline(sketch, "E3056", {"points": [v(-54.22, 2.64) * mm, v(-54.1, 2.47) * mm, v(-54.12, 2.24) * mm, v(-54.26, 2.06) * mm]});
            skFitSpline(sketch, "E3057", {"points": [v(-54.26, 2.06) * mm, v(-54.33, 1.98) * mm, v(-54.42, 1.9) * mm, v(-54.5, 1.83) * mm]});
            skFitSpline(sketch, "E3058", {"points": [v(-54.5, 1.83) * mm, v(-54.73, 1.62) * mm, v(-54.96, 1.4) * mm, v(-55.17, 1.15) * mm]});
            skFitSpline(sketch, "E3059", {"points": [v(-55.17, 1.15) * mm, v(-55.1, 1.18) * mm, v(-55.04, 1.2) * mm, v(-54.98, 1.23) * mm]});
            skFitSpline(sketch, "E3060", {"points": [v(-54.98, 1.23) * mm, v(-54.56, 1.42) * mm, v(-54.13, 1.6) * mm, v(-53.71, 1.8) * mm]});
            skFitSpline(sketch, "E3061", {"points": [v(-53.71, 1.8) * mm, v(-53.41, 1.92) * mm, v(-53.11, 2.06) * mm, v(-52.81, 2.18) * mm]});
            skFitSpline(sketch, "E3062", {"points": [v(-52.81, 2.18) * mm, v(-52.73, 2.22) * mm, v(-52.65, 2.25) * mm, v(-52.56, 2.26) * mm]});
            skFitSpline(sketch, "E3063", {"points": [v(-52.56, 2.26) * mm, v(-52.34, 2.3) * mm, v(-52.1, 2.16) * mm, v(-52.05, 1.95) * mm]});
            skFitSpline(sketch, "E3064", {"points": [v(-52.05, 1.95) * mm, v(-52, 1.74) * mm, v(-52.01, 1.53) * mm, v(-52.24, 1.38) * mm]});
            skFitSpline(sketch, "E3065", {"points": [v(-52.24, 1.38) * mm, v(-52.3, 1.34) * mm, v(-52.35, 1.32) * mm, v(-52.41, 1.3) * mm]});
            skFitSpline(sketch, "E3066", {"points": [v(-52.41, 1.3) * mm, v(-52.93, 1.07) * mm, v(-53.45, 0.85) * mm, v(-53.97, 0.63) * mm]});
            skFitSpline(sketch, "E3067", {"points": [v(-53.97, 0.63) * mm, v(-54.04, 0.6) * mm, v(-54.1, 0.56) * mm, v(-54.15, 0.49) * mm]});
            skFitSpline(sketch, "E3068", {"points": [v(-54.15, 0.49) * mm, v(-53.99, 0.49) * mm, v(-53.82, 0.48) * mm, v(-53.65, 0.48) * mm]});
            skFitSpline(sketch, "E3069", {"points": [v(-53.65, 0.48) * mm, v(-53.49, 0.49) * mm, v(-53.33, 0.5) * mm, v(-53.17, 0.5) * mm]});
            skFitSpline(sketch, "E3070", {"points": [v(-53.17, 0.5) * mm, v(-52.76, 0.53) * mm, v(-52.34, 0.56) * mm, v(-51.93, 0.57) * mm]});
            skFitSpline(sketch, "E3071", {"points": [v(-51.93, 0.57) * mm, v(-51.8, 0.58) * mm, v(-51.71, 0.62) * mm, v(-51.64, 0.7) * mm]});
            skFitSpline(sketch, "E3072", {"points": [v(-51.64, 0.7) * mm, v(-51.32, 1.1) * mm, v(-51, 1.5) * mm, v(-50.67, 1.9) * mm]});
            skFitSpline(sketch, "E3073", {"points": [v(-50.67, 1.9) * mm, v(-50.62, 1.96) * mm, v(-50.58, 2.03) * mm, v(-50.53, 2.1) * mm]});
            skFitSpline(sketch, "E3074", {"points": [v(-50.53, 2.1) * mm, v(-50.35, 2.33) * mm, v(-50.08, 2.37) * mm, v(-49.86, 2.21) * mm]});
            skFitSpline(sketch, "E3075", {"points": [v(-49.86, 2.21) * mm, v(-49.64, 2.06) * mm, v(-49.58, 1.78) * mm, v(-49.74, 1.53) * mm]});
            skFitSpline(sketch, "E3076", {"points": [v(-49.74, 1.53) * mm, v(-49.9, 1.3) * mm, v(-50.07, 1.06) * mm, v(-50.25, 0.84) * mm]});
            skFitSpline(sketch, "E3077", {"points": [v(-50.25, 0.84) * mm, v(-50.48, 0.56) * mm, v(-50.71, 0.29) * mm, v(-50.95, 0) * mm]});
            skFitSpline(sketch, "E3078", {"points": [v(-50.95, 0) * mm, v(-50.77, -0.22) * mm, v(-50.59, -0.43) * mm, v(-50.41, -0.65) * mm]});
            skFitSpline(sketch, "E3079", {"points": [v(-50.41, -0.65) * mm, v(-50.2, -0.92) * mm, v(-49.98, -1.2) * mm, v(-49.77, -1.48) * mm]});
            skFitSpline(sketch, "E3080", {"points": [v(-49.77, -1.48) * mm, v(-49.69, -1.6) * mm, v(-49.64, -1.72) * mm, v(-49.65, -1.86) * mm]});
            skFitSpline(sketch, "E3081", {"points": [v(-49.65, -1.86) * mm, v(-49.68, -2.05) * mm, v(-49.77, -2.2) * mm, v(-49.95, -2.27) * mm]});
            skFitSpline(sketch, "E3082", {"points": [v(-49.95, -2.27) * mm, v(-50.14, -2.34) * mm, v(-50.32, -2.3) * mm, v(-50.46, -2.17) * mm]});
            skFitSpline(sketch, "E3083", {"points": [v(-50.46, -2.17) * mm, v(-50.53, -2.1) * mm, v(-50.58, -2.02) * mm, v(-50.64, -1.95) * mm]});
            skFitSpline(sketch, "E3084", {"points": [v(-50.64, -1.95) * mm, v(-50.96, -1.55) * mm, v(-51.28, -1.15) * mm, v(-51.6, -0.75) * mm]});
            skFitSpline(sketch, "E3085", {"points": [v(-51.6, -0.75) * mm, v(-51.7, -0.63) * mm, v(-51.8, -0.57) * mm, v(-51.96, -0.56) * mm]});
            skFitSpline(sketch, "E3086", {"points": [v(-51.96, -0.56) * mm, v(-52.38, -0.56) * mm, v(-52.8, -0.52) * mm, v(-53.2, -0.5) * mm]});
            skFitSpline(sketch, "E3087", {"points": [v(-53.2, -0.5) * mm, v(-53.52, -0.5) * mm, v(-53.83, -0.5) * mm, v(-54.17, -0.5) * mm]});
            skFitSpline(sketch, "E3088", {"points": [v(-54.17, -0.5) * mm, v(-54.1, -0.55) * mm, v(-54.06, -0.59) * mm, v(-54.01, -0.6) * mm]});
            skFitSpline(sketch, "E3089", {"points": [v(-54.01, -0.6) * mm, v(-53.46, -0.84) * mm, v(-52.91, -1.08) * mm, v(-52.36, -1.31) * mm]});
            skFitSpline(sketch, "E3090", {"points": [v(-52.36, -1.31) * mm, v(-52.15, -1.4) * mm, v(-52.04, -1.55) * mm, v(-52.03, -1.79) * mm]});
            skFitSpline(sketch, "E3091", {"points": [v(-52.03, -1.79) * mm, v(-52.01, -2.08) * mm, v(-52.35, -2.38) * mm, v(-52.68, -2.24) * mm]});
            skFitSpline(sketch, "E3092", {"points": [v(-52.68, -2.24) * mm, v(-52.91, -2.15) * mm, v(-53.14, -2.05) * mm, v(-53.36, -1.95) * mm]});
            skFitSpline(sketch, "E3093", {"points": [v(-53.36, -1.95) * mm, v(-53.95, -1.69) * mm, v(-54.54, -1.42) * mm, v(-55.13, -1.16) * mm]});
            skFitSpline(sketch, "E3094", {"points": [v(-55.13, -1.16) * mm, v(-55.15, -1.16) * mm, v(-55.16, -1.16) * mm, v(-55.21, -1.17) * mm]});
            skFitSpline(sketch, "E3095", {"points": [v(-55.21, -1.17) * mm, v(-54.97, -1.4) * mm, v(-54.74, -1.61) * mm, v(-54.5, -1.83) * mm]});
            skFitSpline(sketch, "E3096", {"points": [v(-54.5, -1.83) * mm, v(-54.43, -1.9) * mm, v(-54.34, -1.97) * mm, v(-54.27, -2.06) * mm]});
            skFitSpline(sketch, "E3097", {"points": [v(-54.27, -2.06) * mm, v(-54.1, -2.26) * mm, v(-54.1, -2.53) * mm, v(-54.28, -2.71) * mm]});
            skFitSpline(sketch, "E3098", {"points": [v(-54.28, -2.71) * mm, v(-54.44, -2.89) * mm, v(-54.73, -2.91) * mm, v(-54.93, -2.75) * mm]});
            skFitSpline(sketch, "E3099", {"points": [v(-54.93, -2.75) * mm, v(-55.12, -2.6) * mm, v(-55.3, -2.44) * mm, v(-55.47, -2.28) * mm]});
            skFitSpline(sketch, "E3100", {"points": [v(-55.47, -2.28) * mm, v(-55.89, -1.9) * mm, v(-56.3, -1.5) * mm, v(-56.72, -1.12) * mm]});
            skFitSpline(sketch, "E3101", {"points": [v(-56.72, -1.12) * mm, v(-56.86, -0.99) * mm, v(-57, -0.86) * mm, v(-57.14, -0.71) * mm]});
            skFitSpline(sketch, "E3102", {"points": [v(-57.14, -0.71) * mm, v(-57.4, -1.03) * mm, v(-57.65, -1.32) * mm, v(-57.9, -1.61) * mm]});
            skFitSpline(sketch, "E3103", {"points": [v(-57.9, -1.61) * mm, v(-58.04, -1.8) * mm, v(-58.18, -1.98) * mm, v(-58.33, -2.15) * mm]});
            skFitSpline(sketch, "E3104", {"points": [v(-58.33, -2.15) * mm, v(-58.43, -2.26) * mm, v(-58.46, -2.36) * mm, v(-58.43, -2.52) * mm]});
            skFitSpline(sketch, "E3105", {"points": [v(-58.43, -2.52) * mm, v(-58.32, -3.1) * mm, v(-58.23, -3.68) * mm, v(-58.13, -4.26) * mm]});
            skFitSpline(sketch, "E3106", {"points": [v(-58.13, -4.26) * mm, v(-58.12, -4.28) * mm, v(-58.11, -4.3) * mm, v(-58.1, -4.34) * mm]});
            skFitSpline(sketch, "E3107", {"points": [v(-58.1, -4.34) * mm, v(-57.89, -4.3) * mm, v(-57.68, -4.24) * mm, v(-57.47, -4.2) * mm]});
            skFitSpline(sketch, "E3108", {"points": [v(-57.47, -4.2) * mm, v(-57.07, -4.1) * mm, v(-56.68, -4.02) * mm, v(-56.28, -3.93) * mm]});
            skFitSpline(sketch, "E3109", {"points": [v(-56.28, -3.93) * mm, v(-55.96, -3.86) * mm, v(-55.64, -3.78) * mm, v(-55.32, -3.72) * mm]});
            skFitSpline(sketch, "E3110", {"points": [v(-55.32, -3.72) * mm, v(-55.25, -3.7) * mm, v(-55.16, -3.7) * mm, v(-55.09, -3.7) * mm]});
            skFitSpline(sketch, "E3111", {"points": [v(-55.09, -3.7) * mm, v(-54.87, -3.7) * mm, v(-54.7, -3.83) * mm, v(-54.64, -4.03) * mm]});
            skFitSpline(sketch, "E3112", {"points": [v(-54.64, -4.03) * mm, v(-54.58, -4.25) * mm, v(-54.66, -4.48) * mm, v(-54.87, -4.58) * mm]});
            skFitSpline(sketch, "E3113", {"points": [v(-54.87, -4.58) * mm, v(-55, -4.64) * mm, v(-55.14, -4.66) * mm, v(-55.28, -4.7) * mm]});
            skFitSpline(sketch, "E3114", {"points": [v(-55.28, -4.7) * mm, v(-55.58, -4.77) * mm, v(-55.88, -4.84) * mm, v(-56.19, -4.95) * mm]});
            skFitSpline(sketch, "E3115", {"points": [v(-56.19, -4.95) * mm, v(-56.13, -4.96) * mm, v(-56.08, -4.98) * mm, v(-56.02, -4.98) * mm]});
            skFitSpline(sketch, "E3116", {"points": [v(-56.02, -4.98) * mm, v(-55.4, -5.05) * mm, v(-54.78, -5.1) * mm, v(-54.16, -5.17) * mm]});
            skFitSpline(sketch, "E3117", {"points": [v(-54.16, -5.17) * mm, v(-53.94, -5.2) * mm, v(-53.72, -5.22) * mm, v(-53.5, -5.26) * mm]});
            skFitSpline(sketch, "E3118", {"points": [v(-53.5, -5.26) * mm, v(-53.23, -5.3) * mm, v(-53.07, -5.5) * mm, v(-53.1, -5.79) * mm]});
            skFitSpline(sketch, "E3119", {"points": [v(-53.1, -5.79) * mm, v(-53.1, -6.03) * mm, v(-53.3, -6.2) * mm, v(-53.55, -6.21) * mm]});
            skFitSpline(sketch, "E3120", {"points": [v(-53.55, -6.21) * mm, v(-53.7, -6.21) * mm, v(-53.86, -6.2) * mm, v(-54, -6.18) * mm]});
            skFitSpline(sketch, "E3121", {"points": [v(-54, -6.18) * mm, v(-54.47, -6.12) * mm, v(-54.92, -6.06) * mm, v(-55.38, -6) * mm]});
            skFitSpline(sketch, "E3122", {"points": [v(-55.38, -6) * mm, v(-55.45, -6) * mm, v(-55.53, -6) * mm, v(-55.62, -6) * mm]});
            skFitSpline(sketch, "E3123", {"points": [v(-55.62, -6) * mm, v(-55.54, -6.11) * mm, v(-55.43, -6.16) * mm, v(-55.33, -6.2) * mm]});
            skFitSpline(sketch, "E3124", {"points": [v(-55.33, -6.2) * mm, v(-54.77, -6.5) * mm, v(-54.2, -6.8) * mm, v(-53.64, -7.1) * mm]});
            skFitSpline(sketch, "E3125", {"points": [v(-53.64, -7.1) * mm, v(-53.55, -7.15) * mm, v(-53.47, -7.14) * mm, v(-53.39, -7.11) * mm]});
            skFitSpline(sketch, "E3126", {"points": [v(-53.39, -7.11) * mm, v(-52.9, -6.93) * mm, v(-52.43, -6.75) * mm, v(-51.95, -6.57) * mm]});
            skFitSpline(sketch, "E3127", {"points": [v(-51.95, -6.57) * mm, v(-51.87, -6.53) * mm, v(-51.78, -6.48) * mm, v(-51.7, -6.45) * mm]});
            skFitSpline(sketch, "E3128", {"points": [v(-51.7, -6.45) * mm, v(-51.42, -6.35) * mm, v(-51.16, -6.45) * mm, v(-51.05, -6.7) * mm]});
            skFitSpline(sketch, "E3129", {"points": [v(-51.05, -6.7) * mm, v(-50.94, -6.93) * mm, v(-51.03, -7.2) * mm, v(-51.28, -7.33) * mm]});
            skFitSpline(sketch, "E3130", {"points": [v(-51.28, -7.33) * mm, v(-51.56, -7.47) * mm, v(-51.85, -7.59) * mm, v(-52.14, -7.7) * mm]});
            skFitSpline(sketch, "E3131", {"points": [v(-52.14, -7.7) * mm, v(-52.45, -7.83) * mm, v(-52.77, -7.93) * mm, v(-53.09, -8.05) * mm]});
            skFitSpline(sketch, "E3132", {"points": [v(-53.09, -8.05) * mm, v(-53.09, -8.12) * mm, v(-53.1, -8.18) * mm, v(-53.09, -8.24) * mm]});
            skFitSpline(sketch, "E3133", {"points": [v(-53.09, -8.24) * mm, v(-53.02, -8.67) * mm, v(-52.94, -9.1) * mm, v(-52.87, -9.53) * mm]});
            skFitSpline(sketch, "E3134", {"points": [v(-52.87, -9.53) * mm, v(-52.85, -9.7) * mm, v(-52.85, -9.89) * mm, v(-52.85, -10.06) * mm]});
            skFitSpline(sketch, "E3135", {"points": [v(-52.85, -10.06) * mm, v(-52.85, -10.29) * mm, v(-52.97, -10.45) * mm, v(-53.18, -10.5) * mm]});
            skFitSpline(sketch, "E3136", {"points": [v(-53.18, -10.5) * mm, v(-53.38, -10.56) * mm, v(-53.6, -10.5) * mm, v(-53.7, -10.32) * mm]});
            skFitSpline(sketch, "E3137", {"points": [v(-53.7, -10.32) * mm, v(-53.76, -10.23) * mm, v(-53.8, -10.12) * mm, v(-53.8, -10) * mm]});
            skFitSpline(sketch, "E3138", {"points": [v(-53.8, -10) * mm, v(-53.84, -9.43) * mm, v(-53.96, -8.87) * mm, v(-54.07, -8.3) * mm]});
            skFitSpline(sketch, "E3139", {"points": [v(-54.07, -8.3) * mm, v(-54.08, -8.23) * mm, v(-54.14, -8.14) * mm, v(-54.2, -8.1) * mm]});
            skFitSpline(sketch, "E3140", {"points": [v(-54.2, -8.1) * mm, v(-54.8, -7.71) * mm, v(-55.4, -7.34) * mm, v(-56, -6.96) * mm]});
            skFitSpline(sketch, "E3141", {"points": [v(-56, -6.96) * mm, v(-56.04, -6.94) * mm, v(-56.09, -6.92) * mm, v(-56.15, -6.93) * mm]});
            skFitSpline(sketch, "E3142", {"points": [v(-56.15, -6.93) * mm, v(-56.04, -7.09) * mm, v(-55.94, -7.24) * mm, v(-55.82, -7.39) * mm]});
            skFitSpline(sketch, "E3143", {"points": [v(-55.82, -7.39) * mm, v(-55.55, -7.75) * mm, v(-55.27, -8.11) * mm, v(-55, -8.48) * mm]});
            skFitSpline(sketch, "E3144", {"points": [v(-55, -8.48) * mm, v(-54.95, -8.56) * mm, v(-54.9, -8.64) * mm, v(-54.88, -8.73) * mm]});
            skFitSpline(sketch, "E3145", {"points": [v(-54.88, -8.73) * mm, v(-54.82, -8.95) * mm, v(-54.94, -9.17) * mm, v(-55.15, -9.27) * mm]});
            skFitSpline(sketch, "E3146", {"points": [v(-55.15, -9.27) * mm, v(-55.35, -9.36) * mm, v(-55.59, -9.31) * mm, v(-55.73, -9.13) * mm]});
            skFitSpline(sketch, "E3147", {"points": [v(-55.73, -9.13) * mm, v(-55.9, -8.93) * mm, v(-56.05, -8.7) * mm, v(-56.2, -8.5) * mm]});
            skFitSpline(sketch, "E3148", {"points": [v(-56.2, -8.5) * mm, v(-56.58, -7.98) * mm, v(-56.96, -7.47) * mm, v(-57.37, -6.97) * mm]});
            skFitSpline(sketch, "E3149", {"points": [v(-57.37, -6.97) * mm, v(-57.3, -7.21) * mm, v(-57.24, -7.46) * mm, v(-57.16, -7.7) * mm]});
            skFitSpline(sketch, "E3150", {"points": [v(-57.16, -7.7) * mm, v(-57.12, -7.85) * mm, v(-57.06, -8) * mm, v(-57.02, -8.14) * mm]});
            skFitSpline(sketch, "E3151", {"points": [v(-57.02, -8.14) * mm, v(-56.95, -8.44) * mm, v(-57.09, -8.67) * mm, v(-57.37, -8.76) * mm]});
            skFitSpline(sketch, "E3152", {"points": [v(-57.37, -8.76) * mm, v(-57.6, -8.83) * mm, v(-57.86, -8.68) * mm, v(-57.95, -8.42) * mm]});
            skFitSpline(sketch, "E3153", {"points": [v(-57.95, -8.42) * mm, v(-58.07, -8.05) * mm, v(-58.18, -7.69) * mm, v(-58.29, -7.32) * mm]});
            skFitSpline(sketch, "E3154", {"points": [v(-58.29, -7.32) * mm, v(-58.45, -6.79) * mm, v(-58.62, -6.25) * mm, v(-58.78, -5.72) * mm]});
            skFitSpline(sketch, "E3155", {"points": [v(-58.78, -5.72) * mm, v(-58.8, -5.68) * mm, v(-58.81, -5.65) * mm, v(-58.84, -5.6) * mm]});
            skFitSpline(sketch, "E3156", {"points": [v(-58.84, -5.6) * mm, v(-59.19, -5.72) * mm, v(-59.53, -5.84) * mm, v(-59.87, -5.97) * mm]});
            skFitSpline(sketch, "E3157", {"points": [v(-59.87, -5.97) * mm, v(-60.12, -6.06) * mm, v(-60.37, -6.15) * mm, v(-60.61, -6.24) * mm]});
            skFitSpline(sketch, "E3158", {"points": [v(-60.61, -6.24) * mm, v(-60.7, -6.28) * mm, v(-60.78, -6.33) * mm, v(-60.82, -6.43) * mm]});
            skFitSpline(sketch, "E3159", {"points": [v(-60.82, -6.43) * mm, v(-61.04, -7.03) * mm, v(-61.26, -7.62) * mm, v(-61.49, -8.24) * mm]});
            skFitSpline(sketch, "E3160", {"points": [v(-61.49, -8.24) * mm, v(-61.25, -8.31) * mm, v(-61.03, -8.38) * mm, v(-60.81, -8.45) * mm]});
            skFitSpline(sketch, "E3161", {"points": [v(-60.81, -8.45) * mm, v(-60.42, -8.57) * mm, v(-60.04, -8.7) * mm, v(-59.65, -8.81) * mm]});
            skFitSpline(sketch, "E3162", {"points": [v(-59.65, -8.81) * mm, v(-59.33, -8.91) * mm, v(-59, -9) * mm, v(-58.69, -9.11) * mm]});
            skFitSpline(sketch, "E3163", {"points": [v(-58.69, -9.11) * mm, v(-58.43, -9.2) * mm, v(-58.33, -9.35) * mm, v(-58.32, -9.6) * mm]});
            skFitSpline(sketch, "E3164", {"points": [v(-58.32, -9.6) * mm, v(-58.3, -9.85) * mm, v(-58.54, -10.1) * mm, v(-58.83, -10.07) * mm]});
            skFitSpline(sketch, "E3165", {"points": [v(-58.83, -10.07) * mm, v(-58.95, -10.05) * mm, v(-59.07, -10) * mm, v(-59.18, -9.97) * mm]});
            skFitSpline(sketch, "E3166", {"points": [v(-59.18, -9.97) * mm, v(-59.5, -9.88) * mm, v(-59.8, -9.78) * mm, v(-60.13, -9.73) * mm]});
            skFitSpline(sketch, "E3167", {"points": [v(-60.13, -9.73) * mm, v(-60.06, -9.78) * mm, v(-59.99, -9.83) * mm, v(-59.92, -9.88) * mm]});
            skFitSpline(sketch, "E3168", {"points": [v(-59.92, -9.88) * mm, v(-59.58, -10.13) * mm, v(-59.24, -10.37) * mm, v(-58.9, -10.62) * mm]});
            skFitSpline(sketch, "E3169", {"points": [v(-58.9, -10.62) * mm, v(-58.63, -10.83) * mm, v(-58.34, -11.04) * mm, v(-58.06, -11.25) * mm]});
            skFitSpline(sketch, "E3170", {"points": [v(-58.06, -11.25) * mm, v(-58, -11.3) * mm, v(-57.93, -11.34) * mm, v(-57.88, -11.4) * mm]});
            skFitSpline(sketch, "E3171", {"points": [v(-57.88, -11.4) * mm, v(-57.72, -11.58) * mm, v(-57.72, -11.85) * mm, v(-57.88, -12.04) * mm]});
            skFitSpline(sketch, "E3172", {"points": [v(-57.88, -12.04) * mm, v(-58.03, -12.21) * mm, v(-58.27, -12.26) * mm, v(-58.48, -12.14) * mm]});
            skFitSpline(sketch, "E3173", {"points": [v(-58.48, -12.14) * mm, v(-58.53, -12.12) * mm, v(-58.58, -12.08) * mm, v(-58.62, -12.05) * mm]});
            skFitSpline(sketch, "E3174", {"points": [v(-58.62, -12.05) * mm, v(-59.08, -11.7) * mm, v(-59.53, -11.37) * mm, v(-59.98, -11.03) * mm]});
            skFitSpline(sketch, "E3175", {"points": [v(-59.98, -11.03) * mm, v(-60.03, -11) * mm, v(-60.08, -10.97) * mm, v(-60.16, -10.9) * mm]});
            skFitSpline(sketch, "E3176", {"points": [v(-60.16, -10.9) * mm, v(-60.13, -11) * mm, v(-60.12, -11.05) * mm, v(-60.1, -11.09) * mm]});
            skFitSpline(sketch, "E3177", {"points": [v(-60.1, -11.09) * mm, v(-59.73, -11.68) * mm, v(-59.36, -12.28) * mm, v(-58.98, -12.87) * mm]});
            skFitSpline(sketch, "E3178", {"points": [v(-58.98, -12.87) * mm, v(-58.93, -12.93) * mm, v(-58.84, -12.99) * mm, v(-58.76, -13) * mm]});
            skFitSpline(sketch, "E3179", {"points": [v(-58.76, -13) * mm, v(-58.22, -13.1) * mm, v(-57.68, -13.18) * mm, v(-57.13, -13.27) * mm]});
            skFitSpline(sketch, "E3180", {"points": [v(-57.13, -13.27) * mm, v(-57.1, -13.27) * mm, v(-57.05, -13.27) * mm, v(-57.01, -13.28) * mm]});
            skFitSpline(sketch, "E3181", {"points": [v(-57.01, -13.28) * mm, v(-56.7, -13.32) * mm, v(-56.52, -13.52) * mm, v(-56.55, -13.8) * mm]});
            skFitSpline(sketch, "E3182", {"points": [v(-56.55, -13.8) * mm, v(-56.57, -14.07) * mm, v(-56.8, -14.27) * mm, v(-57.1, -14.24) * mm]});
            skFitSpline(sketch, "E3183", {"points": [v(-57.1, -14.24) * mm, v(-57.42, -14.22) * mm, v(-57.74, -14.17) * mm, v(-58.05, -14.12) * mm]});
            skFitSpline(sketch, "E3184", {"points": [v(-58.05, -14.12) * mm, v(-58.37, -14.08) * mm, v(-58.68, -14.02) * mm, v(-59, -13.96) * mm]});
            skFitSpline(sketch, "E3185", {"points": [v(-59, -13.96) * mm, v(-59.1, -14.2) * mm, v(-59.18, -14.44) * mm, v(-59.28, -14.68) * mm]});
            skFitSpline(sketch, "E3186", {"points": [v(-59.28, -14.68) * mm, v(-59.41, -15.02) * mm, v(-59.55, -15.36) * mm, v(-59.7, -15.7) * mm]});
            skFitSpline(sketch, "E3187", {"points": [v(-59.7, -15.7) * mm, v(-59.74, -15.8) * mm, v(-59.82, -15.9) * mm, v(-59.91, -15.97) * mm]});
            skFitSpline(sketch, "E3188", {"points": [v(-59.91, -15.97) * mm, v(-60.09, -16.11) * mm, v(-60.29, -16.1) * mm, v(-60.47, -15.97) * mm]});
            skFitSpline(sketch, "E3189", {"points": [v(-60.47, -15.97) * mm, v(-60.63, -15.85) * mm, v(-60.7, -15.63) * mm, v(-60.64, -15.44) * mm]});
            skFitSpline(sketch, "E3190", {"points": [v(-60.64, -15.44) * mm, v(-60.6, -15.3) * mm, v(-60.52, -15.18) * mm, v(-60.47, -15.04) * mm]});
            skFitSpline(sketch, "E3191", {"points": [v(-60.47, -15.04) * mm, v(-60.3, -14.6) * mm, v(-60.14, -14.18) * mm, v(-59.97, -13.74) * mm]});
            skFitSpline(sketch, "E3192", {"points": [v(-59.97, -13.74) * mm, v(-59.92, -13.6) * mm, v(-59.94, -13.49) * mm, v(-60, -13.36) * mm]});
            skFitSpline(sketch, "E3193", {"points": [v(-60, -13.36) * mm, v(-60.28, -12.85) * mm, v(-60.54, -12.34) * mm, v(-60.81, -11.83) * mm]});
            skFitSpline(sketch, "E3194", {"points": [v(-60.81, -11.83) * mm, v(-60.87, -11.71) * mm, v(-60.95, -11.6) * mm, v(-61.05, -11.49) * mm]});
            skFitSpline(sketch, "E3195", {"points": [v(-61.05, -11.49) * mm, v(-61.06, -11.55) * mm, v(-61.07, -11.62) * mm, v(-61.07, -11.68) * mm]});
            skFitSpline(sketch, "E3196", {"points": [v(-61.07, -11.68) * mm, v(-61.01, -12.13) * mm, v(-60.96, -12.57) * mm, v(-60.9, -13.01) * mm]});
            skFitSpline(sketch, "E3197", {"points": [v(-60.9, -13.01) * mm, v(-60.89, -13.18) * mm, v(-60.87, -13.35) * mm, v(-60.86, -13.51) * mm]});
            skFitSpline(sketch, "E3198", {"points": [v(-60.86, -13.51) * mm, v(-60.86, -13.78) * mm, v(-61.04, -13.97) * mm, v(-61.3, -13.99) * mm]});
            skFitSpline(sketch, "E3199", {"points": [v(-61.3, -13.99) * mm, v(-61.55, -14) * mm, v(-61.78, -13.83) * mm, v(-61.82, -13.58) * mm]});
            skFitSpline(sketch, "E3200", {"points": [v(-61.82, -13.58) * mm, v(-61.86, -13.33) * mm, v(-61.89, -13.07) * mm, v(-61.92, -12.82) * mm]});
            skFitSpline(sketch, "E3201", {"points": [v(-61.92, -12.82) * mm, v(-61.96, -12.42) * mm, v(-62, -12.01) * mm, v(-62.05, -11.6) * mm]});
            skFitSpline(sketch, "E3202", {"points": [v(-62.05, -11.6) * mm, v(-62.07, -11.4) * mm, v(-62.09, -11.18) * mm, v(-62.1, -10.97) * mm]});
            skFitSpline(sketch, "E3203", {"points": [v(-62.1, -10.97) * mm, v(-62.11, -10.94) * mm, v(-62.12, -10.9) * mm, v(-62.16, -10.87) * mm]});
            skFitSpline(sketch, "E3204", {"points": [v(-62.16, -10.87) * mm, v(-62.24, -11.21) * mm, v(-62.32, -11.55) * mm, v(-62.4, -11.9) * mm]});
            skFitSpline(sketch, "E3205", {"points": [v(-62.4, -11.9) * mm, v(-62.42, -11.99) * mm, v(-62.43, -12.08) * mm, v(-62.47, -12.17) * mm]});
            skFitSpline(sketch, "E3206", {"points": [v(-62.47, -12.17) * mm, v(-62.58, -12.4) * mm, v(-62.84, -12.5) * mm, v(-63.08, -12.42) * mm]});
            skFitSpline(sketch, "E3207", {"points": [v(-63.08, -12.42) * mm, v(-63.3, -12.34) * mm, v(-63.44, -12.1) * mm, v(-63.38, -11.86) * mm]});
            skFitSpline(sketch, "E3208", {"points": [v(-63.38, -11.86) * mm, v(-63.3, -11.46) * mm, v(-63.2, -11.05) * mm, v(-63.1, -10.65) * mm]});
            skFitSpline(sketch, "E3209", {"points": [v(-63.1, -10.65) * mm, v(-62.98, -10.1) * mm, v(-62.86, -9.55) * mm, v(-62.74, -8.97) * mm]});
            skFitSpline(sketch, "E3210", {"points": [v(-62.74, -8.97) * mm, v(-62.9, -8.94) * mm, v(-63.06, -8.9) * mm, v(-63.22, -8.86) * mm]});
            skFitSpline(sketch, "E3211", {"points": [v(-63.22, -8.86) * mm, v(-63.68, -8.78) * mm, v(-64.15, -8.71) * mm, v(-64.61, -8.63) * mm]});
            skFitSpline(sketch, "E3212", {"points": [v(-64.61, -8.63) * mm, v(-64.71, -8.61) * mm, v(-64.8, -8.64) * mm, v(-64.88, -8.7) * mm]});
            skFitSpline(sketch, "E3213", {"points": [v(-64.88, -8.7) * mm, v(-65.36, -9.1) * mm, v(-65.85, -9.5) * mm, v(-66.35, -9.92) * mm]});
            skFitSpline(sketch, "E3214", {"points": [v(-66.35, -9.92) * mm, v(-66.3, -9.97) * mm, v(-66.28, -10.02) * mm, v(-66.25, -10.06) * mm]});
            skFitSpline(sketch, "E3215", {"points": [v(-66.25, -10.06) * mm, v(-65.83, -10.5) * mm, v(-65.42, -10.94) * mm, v(-65, -11.39) * mm]});
            skFitSpline(sketch, "E3216", {"points": [v(-65, -11.39) * mm, v(-64.8, -11.6) * mm, v(-64.59, -11.83) * mm, v(-64.39, -12.06) * mm]});
            skFitSpline(sketch, "E3217", {"points": [v(-64.39, -12.06) * mm, v(-64.32, -12.13) * mm, v(-64.26, -12.23) * mm, v(-64.23, -12.32) * mm]});
            skFitSpline(sketch, "E3218", {"points": [v(-64.23, -12.32) * mm, v(-64.17, -12.53) * mm, v(-64.26, -12.73) * mm, v(-64.42, -12.85) * mm]});
            skFitSpline(sketch, "E3219", {"points": [v(-64.42, -12.85) * mm, v(-64.6, -12.96) * mm, v(-64.83, -12.95) * mm, v(-65, -12.81) * mm]});
            skFitSpline(sketch, "E3220", {"points": [v(-65, -12.81) * mm, v(-65.09, -12.74) * mm, v(-65.16, -12.65) * mm, v(-65.24, -12.57) * mm]});
            skFitSpline(sketch, "E3221", {"points": [v(-65.24, -12.57) * mm, v(-65.45, -12.34) * mm, v(-65.66, -12.12) * mm, v(-65.9, -11.91) * mm]});
            skFitSpline(sketch, "E3222", {"points": [v(-65.9, -11.91) * mm, v(-65.89, -11.97) * mm, v(-65.87, -12.02) * mm, v(-65.85, -12.08) * mm]});
            skFitSpline(sketch, "E3223", {"points": [v(-65.85, -12.08) * mm, v(-65.64, -12.54) * mm, v(-65.44, -13) * mm, v(-65.24, -13.46) * mm]});
            skFitSpline(sketch, "E3224", {"points": [v(-65.24, -13.46) * mm, v(-65.12, -13.73) * mm, v(-64.99, -14) * mm, v(-64.88, -14.3) * mm]});
            skFitSpline(sketch, "E3225", {"points": [v(-64.88, -14.3) * mm, v(-64.83, -14.4) * mm, v(-64.8, -14.54) * mm, v(-64.82, -14.66) * mm]});
            skFitSpline(sketch, "E3226", {"points": [v(-64.82, -14.66) * mm, v(-64.84, -14.85) * mm, v(-64.97, -14.99) * mm, v(-65.17, -15.03) * mm]});
            skFitSpline(sketch, "E3227", {"points": [v(-65.17, -15.03) * mm, v(-65.38, -15.07) * mm, v(-65.56, -15.02) * mm, v(-65.68, -14.84) * mm]});
            skFitSpline(sketch, "E3228", {"points": [v(-65.68, -14.84) * mm, v(-65.72, -14.8) * mm, v(-65.74, -14.73) * mm, v(-65.77, -14.67) * mm]});
            skFitSpline(sketch, "E3229", {"points": [v(-65.77, -14.67) * mm, v(-66, -14.15) * mm, v(-66.21, -13.63) * mm, v(-66.44, -13.11) * mm]});
            skFitSpline(sketch, "E3230", {"points": [v(-66.44, -13.11) * mm, v(-66.47, -13.04) * mm, v(-66.5, -12.98) * mm, v(-66.54, -12.9) * mm]});
            skFitSpline(sketch, "E3231", {"points": [v(-66.54, -12.9) * mm, v(-66.56, -12.91) * mm, v(-66.57, -12.92) * mm, v(-66.59, -12.92) * mm]});
            skFitSpline(sketch, "E3232", {"points": [v(-95.08, -6.4) * mm, v(-94.57, -6.24) * mm, v(-94.08, -6.09) * mm, v(-93.57, -5.93) * mm]});
            skFitSpline(sketch, "E3233", {"points": [v(-93.57, -5.93) * mm, v(-93.82, -5.45) * mm, v(-94.06, -5) * mm, v(-94.3, -4.53) * mm]});
            skFitSpline(sketch, "E3234", {"points": [v(-94.3, -4.53) * mm, v(-94.84, -4.67) * mm, v(-95.35, -4.8) * mm, v(-95.87, -4.99) * mm]});
            skFitSpline(sketch, "E3235", {"points": [v(-95.87, -4.99) * mm, v(-95.6, -5.47) * mm, v(-95.34, -5.93) * mm, v(-95.08, -6.4) * mm]});
            skFitSpline(sketch, "E3236", {"points": [v(-121.46, 4.52) * mm, v(-120.93, 4.68) * mm, v(-120.43, 4.82) * mm, v(-119.9, 4.97) * mm]});
            skFitSpline(sketch, "E3237", {"points": [v(-119.9, 4.97) * mm, v(-120.17, 5.47) * mm, v(-120.42, 5.93) * mm, v(-120.68, 6.4) * mm]});
            skFitSpline(sketch, "E3238", {"points": [v(-120.68, 6.4) * mm, v(-121.2, 6.24) * mm, v(-121.69, 6.09) * mm, v(-122.2, 5.93) * mm]});
            skFitSpline(sketch, "E3239", {"points": [v(-122.2, 5.93) * mm, v(-121.95, 5.45) * mm, v(-121.7, 5) * mm, v(-121.46, 4.52) * mm]});
            skFitSpline(sketch, "E3240", {"points": [v(-101.95, 14.31) * mm, v(-102.44, 14.06) * mm, v(-102.9, 13.82) * mm, v(-103.34, 13.59) * mm]});
            skFitSpline(sketch, "E3241", {"points": [v(-103.34, 13.59) * mm, v(-103.24, 13.03) * mm, v(-102.98, 12.2) * mm, v(-102.86, 12.03) * mm]});
            skFitSpline(sketch, "E3242", {"points": [v(-102.86, 12.03) * mm, v(-102.4, 12.29) * mm, v(-101.95, 12.54) * mm, v(-101.48, 12.8) * mm]});
            skFitSpline(sketch, "E3243", {"points": [v(-101.48, 12.8) * mm, v(-101.64, 13.31) * mm, v(-101.8, 13.8) * mm, v(-101.95, 14.31) * mm]});
            skFitSpline(sketch, "E3244", {"points": [v(-114.29, -12.8) * mm, v(-114.12, -13.32) * mm, v(-113.97, -13.8) * mm, v(-113.8, -14.31) * mm]});
            skFitSpline(sketch, "E3245", {"points": [v(-113.8, -14.31) * mm, v(-113.33, -14.06) * mm, v(-112.87, -13.82) * mm, v(-112.41, -13.58) * mm]});
            skFitSpline(sketch, "E3246", {"points": [v(-112.41, -13.58) * mm, v(-112.56, -13.05) * mm, v(-112.7, -12.54) * mm, v(-112.87, -12.01) * mm]});
            skFitSpline(sketch, "E3247", {"points": [v(-112.87, -12.01) * mm, v(-113.36, -12.28) * mm, v(-113.81, -12.54) * mm, v(-114.29, -12.8) * mm]});
            skFitSpline(sketch, "E3248", {"points": [v(-122.2, -5.93) * mm, v(-121.68, -6.09) * mm, v(-121.19, -6.24) * mm, v(-120.69, -6.4) * mm]});
            skFitSpline(sketch, "E3249", {"points": [v(-120.69, -6.4) * mm, v(-120.41, -5.92) * mm, v(-120.15, -5.47) * mm, v(-119.9, -4.97) * mm]});
            skFitSpline(sketch, "E3250", {"points": [v(-119.9, -4.97) * mm, v(-120.44, -4.82) * mm, v(-120.95, -4.67) * mm, v(-121.46, -4.53) * mm]});
            skFitSpline(sketch, "E3251", {"points": [v(-121.46, -4.53) * mm, v(-121.71, -5) * mm, v(-121.95, -5.46) * mm, v(-122.2, -5.93) * mm]});
            skFitSpline(sketch, "E3252", {"points": [v(-94.3, 4.53) * mm, v(-94.05, 5.01) * mm, v(-93.82, 5.46) * mm, v(-93.57, 5.93) * mm]});
            skFitSpline(sketch, "E3253", {"points": [v(-93.57, 5.93) * mm, v(-94.09, 6.1) * mm, v(-94.58, 6.24) * mm, v(-95.08, 6.4) * mm]});
            skFitSpline(sketch, "E3254", {"points": [v(-95.08, 6.4) * mm, v(-95.35, 5.92) * mm, v(-95.62, 5.47) * mm, v(-95.86, 4.97) * mm]});
            skFitSpline(sketch, "E3255", {"points": [v(-95.86, 4.97) * mm, v(-95.33, 4.82) * mm, v(-94.82, 4.67) * mm, v(-94.3, 4.53) * mm]});
            skFitSpline(sketch, "E3256", {"points": [v(-101.95, -14.31) * mm, v(-101.8, -13.8) * mm, v(-101.64, -13.3) * mm, v(-101.48, -12.8) * mm]});
            skFitSpline(sketch, "E3257", {"points": [v(-101.48, -12.8) * mm, v(-101.96, -12.53) * mm, v(-102.42, -12.28) * mm, v(-102.9, -12) * mm]});
            skFitSpline(sketch, "E3258", {"points": [v(-102.9, -12) * mm, v(-103.06, -12.55) * mm, v(-103.2, -13.06) * mm, v(-103.36, -13.58) * mm]});
            skFitSpline(sketch, "E3259", {"points": [v(-103.36, -13.58) * mm, v(-102.89, -13.82) * mm, v(-102.44, -14.06) * mm, v(-101.95, -14.31) * mm]});
            skFitSpline(sketch, "E3260", {"points": [v(-114.28, 12.8) * mm, v(-113.8, 12.54) * mm, v(-113.35, 12.26) * mm, v(-112.85, 12.02) * mm]});
            skFitSpline(sketch, "E3261", {"points": [v(-112.85, 12.02) * mm, v(-112.7, 12.56) * mm, v(-112.56, 13.07) * mm, v(-112.4, 13.58) * mm]});
            skFitSpline(sketch, "E3262", {"points": [v(-112.4, 13.58) * mm, v(-112.89, 13.83) * mm, v(-113.35, 14.07) * mm, v(-113.81, 14.31) * mm]});
            skFitSpline(sketch, "E3263", {"points": [v(-113.81, 14.31) * mm, v(-113.97, 13.8) * mm, v(-114.12, 13.32) * mm, v(-114.28, 12.8) * mm]});
            skFitSpline(sketch, "E3264", {"points": [v(-103.15, 5.75) * mm, v(-103.15, 5.77) * mm, v(-103.15, 5.8) * mm, v(-103.16, 5.82) * mm]});
            skFitSpline(sketch, "E3265", {"points": [v(-103.16, 5.82) * mm, v(-103.82, 5.95) * mm, v(-104.48, 6.08) * mm, v(-105.15, 6.21) * mm]});
            skFitSpline(sketch, "E3266", {"points": [v(-105.15, 6.21) * mm, v(-105.25, 6.24) * mm, v(-105.36, 6.28) * mm, v(-105.45, 6.34) * mm]});
            skFitSpline(sketch, "E3267", {"points": [v(-105.45, 6.34) * mm, v(-105.83, 6.6) * mm, v(-106.21, 6.86) * mm, v(-106.6, 7.11) * mm]});
            skFitSpline(sketch, "E3268", {"points": [v(-106.6, 7.11) * mm, v(-106.77, 7.23) * mm, v(-106.96, 7.33) * mm, v(-107.18, 7.46) * mm]});
            skFitSpline(sketch, "E3269", {"points": [v(-107.18, 7.46) * mm, v(-106.8, 6.4) * mm, v(-106.43, 5.4) * mm, v(-106.06, 4.39) * mm]});
            skFitSpline(sketch, "E3270", {"points": [v(-106.06, 4.39) * mm, v(-105.07, 4.85) * mm, v(-104.11, 5.3) * mm, v(-103.15, 5.75) * mm]});
            skFitSpline(sketch, "E3271", {"points": [v(-108.6, 7.44) * mm, v(-108.65, 7.42) * mm, v(-108.68, 7.41) * mm, v(-108.7, 7.4) * mm]});
            skFitSpline(sketch, "E3272", {"points": [v(-108.7, 7.4) * mm, v(-109.23, 7.05) * mm, v(-109.76, 6.7) * mm, v(-110.3, 6.36) * mm]});
            skFitSpline(sketch, "E3273", {"points": [v(-110.3, 6.36) * mm, v(-110.41, 6.29) * mm, v(-110.54, 6.23) * mm, v(-110.67, 6.2) * mm]});
            skFitSpline(sketch, "E3274", {"points": [v(-110.67, 6.2) * mm, v(-111.22, 6.08) * mm, v(-111.78, 5.97) * mm, v(-112.33, 5.86) * mm]});
            skFitSpline(sketch, "E3275", {"points": [v(-112.33, 5.86) * mm, v(-112.42, 5.84) * mm, v(-112.52, 5.81) * mm, v(-112.66, 5.77) * mm]});
            skFitSpline(sketch, "E3276", {"points": [v(-112.66, 5.77) * mm, v(-111.65, 5.3) * mm, v(-110.68, 4.85) * mm, v(-109.7, 4.39) * mm]});
            skFitSpline(sketch, "E3277", {"points": [v(-109.7, 4.39) * mm, v(-109.33, 5.42) * mm, v(-108.97, 6.41) * mm, v(-108.6, 7.44) * mm]});
            skFitSpline(sketch, "E3278", {"points": [v(-112.27, -1.82) * mm, v(-113.3, -1.44) * mm, v(-114.3, -1.08) * mm, v(-115.33, -0.7) * mm]});
            skFitSpline(sketch, "E3279", {"points": [v(-115.33, -0.7) * mm, v(-115.3, -0.76) * mm, v(-115.3, -0.79) * mm, v(-115.3, -0.8) * mm]});
            skFitSpline(sketch, "E3280", {"points": [v(-115.3, -0.8) * mm, v(-114.94, -1.34) * mm, v(-114.6, -1.87) * mm, v(-114.24, -2.4) * mm]});
            skFitSpline(sketch, "E3281", {"points": [v(-114.24, -2.4) * mm, v(-114.16, -2.53) * mm, v(-114.1, -2.65) * mm, v(-114.08, -2.8) * mm]});
            skFitSpline(sketch, "E3282", {"points": [v(-114.08, -2.8) * mm, v(-113.96, -3.44) * mm, v(-113.83, -4.08) * mm, v(-113.7, -4.73) * mm]});
            skFitSpline(sketch, "E3283", {"points": [v(-113.7, -4.73) * mm, v(-113.68, -4.73) * mm, v(-113.66, -4.73) * mm, v(-113.64, -4.73) * mm]});
            skFitSpline(sketch, "E3284", {"points": [v(-113.64, -4.73) * mm, v(-113.19, -3.77) * mm, v(-112.74, -2.81) * mm, v(-112.27, -1.82) * mm]});
            skFitSpline(sketch, "E3285", {"points": [v(-100.43, 0.7) * mm, v(-100.47, 0.78) * mm, v(-100.48, 0.8) * mm, v(-100.5, 0.83) * mm]});
            skFitSpline(sketch, "E3286", {"points": [v(-100.5, 0.83) * mm, v(-100.84, 1.36) * mm, v(-101.19, 1.89) * mm, v(-101.52, 2.42) * mm]});
            skFitSpline(sketch, "E3287", {"points": [v(-101.52, 2.42) * mm, v(-101.6, 2.52) * mm, v(-101.64, 2.64) * mm, v(-101.67, 2.76) * mm]});
            skFitSpline(sketch, "E3288", {"points": [v(-101.67, 2.76) * mm, v(-101.77, 3.21) * mm, v(-101.85, 3.67) * mm, v(-101.94, 4.12) * mm]});
            skFitSpline(sketch, "E3289", {"points": [v(-101.94, 4.12) * mm, v(-101.99, 4.32) * mm, v(-102.05, 4.53) * mm, v(-102.1, 4.78) * mm]});
            skFitSpline(sketch, "E3290", {"points": [v(-102.1, 4.78) * mm, v(-102.58, 3.77) * mm, v(-103.03, 2.8) * mm, v(-103.5, 1.82) * mm]});
            skFitSpline(sketch, "E3291", {"points": [v(-103.5, 1.82) * mm, v(-102.47, 1.45) * mm, v(-101.47, 1.08) * mm, v(-100.43, 0.7) * mm]});
            skFitSpline(sketch, "E3292", {"points": [v(-100.43, -0.76) * mm, v(-100.45, -0.75) * mm, v(-100.46, -0.74) * mm, v(-100.47, -0.72) * mm]});
            skFitSpline(sketch, "E3293", {"points": [v(-100.47, -0.72) * mm, v(-101.47, -1.08) * mm, v(-102.47, -1.45) * mm, v(-103.5, -1.82) * mm]});
            skFitSpline(sketch, "E3294", {"points": [v(-103.5, -1.82) * mm, v(-103.03, -2.8) * mm, v(-102.58, -3.77) * mm, v(-102.13, -4.73) * mm]});
            skFitSpline(sketch, "E3295", {"points": [v(-102.13, -4.73) * mm, v(-102.11, -4.73) * mm, v(-102.1, -4.73) * mm, v(-102.07, -4.72) * mm]});
            skFitSpline(sketch, "E3296", {"points": [v(-102.07, -4.72) * mm, v(-101.95, -4.15) * mm, v(-101.82, -3.57) * mm, v(-101.72, -3) * mm]});
            skFitSpline(sketch, "E3297", {"points": [v(-101.72, -3) * mm, v(-101.67, -2.71) * mm, v(-101.57, -2.47) * mm, v(-101.4, -2.24) * mm]});
            skFitSpline(sketch, "E3298", {"points": [v(-101.4, -2.24) * mm, v(-101.07, -1.76) * mm, v(-100.76, -1.25) * mm, v(-100.43, -0.76) * mm]});
            skFitSpline(sketch, "E3299", {"points": [v(-112.27, 1.82) * mm, v(-112.75, 2.81) * mm, v(-113.17, 3.79) * mm, v(-113.67, 4.78) * mm]});
            skFitSpline(sketch, "E3300", {"points": [v(-113.67, 4.78) * mm, v(-113.7, 4.6) * mm, v(-113.73, 4.5) * mm, v(-113.76, 4.37) * mm]});
            skFitSpline(sketch, "E3301", {"points": [v(-113.76, 4.37) * mm, v(-113.85, 3.9) * mm, v(-113.96, 3.44) * mm, v(-114.05, 2.97) * mm]});
            skFitSpline(sketch, "E3302", {"points": [v(-114.05, 2.97) * mm, v(-114.1, 2.74) * mm, v(-114.15, 2.52) * mm, v(-114.3, 2.31) * mm]});
            skFitSpline(sketch, "E3303", {"points": [v(-114.3, 2.31) * mm, v(-114.56, 1.97) * mm, v(-114.79, 1.6) * mm, v(-115.02, 1.24) * mm]});
            skFitSpline(sketch, "E3304", {"points": [v(-115.02, 1.24) * mm, v(-115.13, 1.08) * mm, v(-115.22, 0.91) * mm, v(-115.34, 0.7) * mm]});
            skFitSpline(sketch, "E3305", {"points": [v(-115.34, 0.7) * mm, v(-114.3, 1.08) * mm, v(-113.3, 1.45) * mm, v(-112.27, 1.82) * mm]});
            skFitSpline(sketch, "E3306", {"points": [v(-108.66, -7.45) * mm, v(-108.64, -7.43) * mm, v(-108.62, -7.42) * mm, v(-108.6, -7.4) * mm]});
            skFitSpline(sketch, "E3307", {"points": [v(-108.6, -7.4) * mm, v(-108.97, -6.4) * mm, v(-109.33, -5.4) * mm, v(-109.7, -4.39) * mm]});
            skFitSpline(sketch, "E3308", {"points": [v(-109.7, -4.39) * mm, v(-110.7, -4.85) * mm, v(-111.66, -5.3) * mm, v(-112.63, -5.76) * mm]});
            skFitSpline(sketch, "E3309", {"points": [v(-112.63, -5.76) * mm, v(-112.63, -5.78) * mm, v(-112.62, -5.8) * mm, v(-112.62, -5.81) * mm]});
            skFitSpline(sketch, "E3310", {"points": [v(-112.62, -5.81) * mm, v(-111.98, -5.94) * mm, v(-111.34, -6.07) * mm, v(-110.7, -6.2) * mm]});
            skFitSpline(sketch, "E3311", {"points": [v(-110.7, -6.2) * mm, v(-110.54, -6.22) * mm, v(-110.4, -6.28) * mm, v(-110.27, -6.37) * mm]});
            skFitSpline(sketch, "E3312", {"points": [v(-110.27, -6.37) * mm, v(-109.73, -6.74) * mm, v(-109.2, -7.1) * mm, v(-108.66, -7.45) * mm]});
            skFitSpline(sketch, "E3313", {"points": [v(-103.14, -5.81) * mm, v(-103.14, -5.8) * mm, v(-103.14, -5.77) * mm, v(-103.14, -5.75) * mm]});
            skFitSpline(sketch, "E3314", {"points": [v(-103.14, -5.75) * mm, v(-104.1, -5.3) * mm, v(-105.07, -4.85) * mm, v(-106.07, -4.39) * mm]});
            skFitSpline(sketch, "E3315", {"points": [v(-106.07, -4.39) * mm, v(-106.43, -5.41) * mm, v(-106.81, -6.4) * mm, v(-107.13, -7.43) * mm]});
            skFitSpline(sketch, "E3316", {"points": [v(-107.13, -7.43) * mm, v(-106.58, -7.1) * mm, v(-106.04, -6.75) * mm, v(-105.52, -6.39) * mm]});
            skFitSpline(sketch, "E3317", {"points": [v(-105.52, -6.39) * mm, v(-105.38, -6.29) * mm, v(-105.23, -6.22) * mm, v(-105.06, -6.2) * mm]});
            skFitSpline(sketch, "E3318", {"points": [v(-105.06, -6.2) * mm, v(-104.42, -6.07) * mm, v(-103.78, -5.94) * mm, v(-103.14, -5.81) * mm]});
            skFitSpline(sketch, "E3319", {"points": [v(-118.46, 4.38) * mm, v(-117.77, 3.2) * mm, v(-117.1, 2.06) * mm, v(-116.43, 0.9) * mm]});
            skFitSpline(sketch, "E3320", {"points": [v(-116.43, 0.9) * mm, v(-116.37, 0.97) * mm, v(-116.33, 1.02) * mm, v(-116.3, 1.07) * mm]});
            skFitSpline(sketch, "E3321", {"points": [v(-116.3, 1.07) * mm, v(-115.9, 1.67) * mm, v(-115.5, 2.27) * mm, v(-115.11, 2.87) * mm]});
            skFitSpline(sketch, "E3322", {"points": [v(-115.11, 2.87) * mm, v(-115.06, 2.96) * mm, v(-115.03, 3.08) * mm, v(-115, 3.18) * mm]});
            skFitSpline(sketch, "E3323", {"points": [v(-115, 3.18) * mm, v(-114.94, 3.49) * mm, v(-114.9, 3.8) * mm, v(-114.83, 4.1) * mm]});
            skFitSpline(sketch, "E3324", {"points": [v(-114.83, 4.1) * mm, v(-114.75, 4.47) * mm, v(-114.66, 4.83) * mm, v(-114.58, 5.2) * mm]});
            skFitSpline(sketch, "E3325", {"points": [v(-114.58, 5.2) * mm, v(-114.57, 5.25) * mm, v(-114.58, 5.31) * mm, v(-114.58, 5.4) * mm]});
            skFitSpline(sketch, "E3326", {"points": [v(-114.58, 5.4) * mm, v(-115.87, 5.06) * mm, v(-117.14, 4.73) * mm, v(-118.46, 4.38) * mm]});
            skFitSpline(sketch, "E3327", {"points": [v(-102.47, -6.65) * mm, v(-102.8, -6.72) * mm, v(-103.08, -6.79) * mm, v(-103.35, -6.84) * mm]});
            skFitSpline(sketch, "E3328", {"points": [v(-103.35, -6.84) * mm, v(-103.8, -6.94) * mm, v(-104.24, -7.04) * mm, v(-104.69, -7.12) * mm]});
            skFitSpline(sketch, "E3329", {"points": [v(-104.69, -7.12) * mm, v(-104.84, -7.15) * mm, v(-104.97, -7.2) * mm, v(-105.1, -7.3) * mm]});
            skFitSpline(sketch, "E3330", {"points": [v(-105.1, -7.3) * mm, v(-105.37, -7.48) * mm, v(-105.64, -7.66) * mm, v(-105.92, -7.83) * mm]});
            skFitSpline(sketch, "E3331", {"points": [v(-105.92, -7.83) * mm, v(-106.27, -8.06) * mm, v(-106.62, -8.28) * mm, v(-106.97, -8.5) * mm]});
            skFitSpline(sketch, "E3332", {"points": [v(-106.97, -8.5) * mm, v(-106.77, -8.7) * mm, v(-103.72, -10.47) * mm, v(-103.5, -10.53) * mm]});
            skFitSpline(sketch, "E3333", {"points": [v(-103.5, -10.53) * mm, v(-103.15, -9.25) * mm, v(-102.82, -7.98) * mm, v(-102.47, -6.65) * mm]});
            skFitSpline(sketch, "E3334", {"points": [v(-108.78, -8.53) * mm, v(-108.85, -8.49) * mm, v(-108.88, -8.46) * mm, v(-108.92, -8.43) * mm]});
            skFitSpline(sketch, "E3335", {"points": [v(-108.92, -8.43) * mm, v(-109.54, -8.03) * mm, v(-110.15, -7.62) * mm, v(-110.76, -7.22) * mm]});
            skFitSpline(sketch, "E3336", {"points": [v(-110.76, -7.22) * mm, v(-110.84, -7.18) * mm, v(-110.92, -7.15) * mm, v(-111, -7.13) * mm]});
            skFitSpline(sketch, "E3337", {"points": [v(-111, -7.13) * mm, v(-111.52, -7.02) * mm, v(-112.04, -6.91) * mm, v(-112.55, -6.8) * mm]});
            skFitSpline(sketch, "E3338", {"points": [v(-112.55, -6.8) * mm, v(-112.78, -6.76) * mm, v(-113.01, -6.71) * mm, v(-113.28, -6.66) * mm]});
            skFitSpline(sketch, "E3339", {"points": [v(-113.28, -6.66) * mm, v(-112.96, -7.99) * mm, v(-112.6, -9.26) * mm, v(-112.26, -10.57) * mm]});
            skFitSpline(sketch, "E3340", {"points": [v(-112.26, -10.57) * mm, v(-111.1, -9.88) * mm, v(-109.93, -9.24) * mm, v(-108.78, -8.53) * mm]});
            skFitSpline(sketch, "E3341", {"points": [v(-99.38, 0.9) * mm, v(-99.15, 1.17) * mm, v(-97.41, 4.17) * mm, v(-97.36, 4.38) * mm]});
            skFitSpline(sketch, "E3342", {"points": [v(-97.36, 4.38) * mm, v(-97.39, 4.4) * mm, v(-97.42, 4.4) * mm, v(-97.45, 4.41) * mm]});
            skFitSpline(sketch, "E3343", {"points": [v(-97.45, 4.41) * mm, v(-97.92, 4.54) * mm, v(-98.38, 4.67) * mm, v(-98.85, 4.8) * mm]});
            skFitSpline(sketch, "E3344", {"points": [v(-98.85, 4.8) * mm, v(-99.58, 4.99) * mm, v(-100.3, 5.17) * mm, v(-101.03, 5.36) * mm]});
            skFitSpline(sketch, "E3345", {"points": [v(-101.03, 5.36) * mm, v(-101.09, 5.37) * mm, v(-101.15, 5.36) * mm, v(-101.21, 5.36) * mm]});
            skFitSpline(sketch, "E3346", {"points": [v(-101.21, 5.36) * mm, v(-101.19, 5.23) * mm, v(-101.17, 5.12) * mm, v(-101.15, 5.01) * mm]});
            skFitSpline(sketch, "E3347", {"points": [v(-101.15, 5.01) * mm, v(-101.02, 4.4) * mm, v(-100.88, 3.8) * mm, v(-100.76, 3.19) * mm]});
            skFitSpline(sketch, "E3348", {"points": [v(-100.76, 3.19) * mm, v(-100.73, 3.03) * mm, v(-100.68, 2.9) * mm, v(-100.59, 2.78) * mm]});
            skFitSpline(sketch, "E3349", {"points": [v(-100.59, 2.78) * mm, v(-100.4, 2.51) * mm, v(-100.23, 2.25) * mm, v(-100.06, 1.98) * mm]});
            skFitSpline(sketch, "E3350", {"points": [v(-100.06, 1.98) * mm, v(-99.83, 1.63) * mm, v(-99.61, 1.28) * mm, v(-99.38, 0.9) * mm]});
            skFitSpline(sketch, "E3351", {"points": [v(-114.56, -5.36) * mm, v(-114.57, -5.31) * mm, v(-114.57, -5.26) * mm, v(-114.57, -5.22) * mm]});
            skFitSpline(sketch, "E3352", {"points": [v(-114.57, -5.22) * mm, v(-114.72, -4.51) * mm, v(-114.87, -3.8) * mm, v(-115.02, -3.1) * mm]});
            skFitSpline(sketch, "E3353", {"points": [v(-115.02, -3.1) * mm, v(-115.04, -3) * mm, v(-115.09, -2.91) * mm, v(-115.14, -2.83) * mm]});
            skFitSpline(sketch, "E3354", {"points": [v(-115.14, -2.83) * mm, v(-115.42, -2.39) * mm, v(-115.71, -1.95) * mm, v(-116, -1.5) * mm]});
            skFitSpline(sketch, "E3355", {"points": [v(-116, -1.5) * mm, v(-116.13, -1.3) * mm, v(-116.26, -1.11) * mm, v(-116.4, -0.9) * mm]});
            skFitSpline(sketch, "E3356", {"points": [v(-116.4, -0.9) * mm, v(-116.6, -1.16) * mm, v(-118.35, -4.17) * mm, v(-118.4, -4.37) * mm]});
            skFitSpline(sketch, "E3357", {"points": [v(-118.4, -4.37) * mm, v(-117.92, -4.55) * mm, v(-114.8, -5.36) * mm, v(-114.56, -5.36) * mm]});
            skFitSpline(sketch, "E3358", {"points": [v(-101.23, -5.36) * mm, v(-100.95, -5.36) * mm, v(-97.56, -4.47) * mm, v(-97.33, -4.34) * mm]});
            skFitSpline(sketch, "E3359", {"points": [v(-97.33, -4.34) * mm, v(-98, -3.2) * mm, v(-98.66, -2.06) * mm, v(-99.34, -0.9) * mm]});
            skFitSpline(sketch, "E3360", {"points": [v(-99.34, -0.9) * mm, v(-99.4, -0.96) * mm, v(-99.43, -1) * mm, v(-99.45, -1.04) * mm]});
            skFitSpline(sketch, "E3361", {"points": [v(-99.45, -1.04) * mm, v(-99.85, -1.65) * mm, v(-100.26, -2.26) * mm, v(-100.66, -2.88) * mm]});
            skFitSpline(sketch, "E3362", {"points": [v(-100.66, -2.88) * mm, v(-100.7, -2.96) * mm, v(-100.73, -3.07) * mm, v(-100.75, -3.17) * mm]});
            skFitSpline(sketch, "E3363", {"points": [v(-100.75, -3.17) * mm, v(-100.83, -3.5) * mm, v(-100.89, -3.84) * mm, v(-100.96, -4.17) * mm]});
            skFitSpline(sketch, "E3364", {"points": [v(-100.96, -4.17) * mm, v(-101.04, -4.56) * mm, v(-101.13, -4.95) * mm, v(-101.23, -5.36) * mm]});
            skFitSpline(sketch, "E3365", {"points": [v(-107, 8.54) * mm, v(-106.3, 8.08) * mm, v(-105.65, 7.64) * mm, v(-105, 7.22) * mm]});
            skFitSpline(sketch, "E3366", {"points": [v(-105, 7.22) * mm, v(-104.91, 7.17) * mm, v(-104.82, 7.15) * mm, v(-104.72, 7.13) * mm]});
            skFitSpline(sketch, "E3367", {"points": [v(-104.72, 7.13) * mm, v(-104.22, 7.02) * mm, v(-103.7, 6.9) * mm, v(-103.2, 6.8) * mm]});
            skFitSpline(sketch, "E3368", {"points": [v(-103.2, 6.8) * mm, v(-102.97, 6.76) * mm, v(-102.74, 6.69) * mm, v(-102.48, 6.68) * mm]});
            skFitSpline(sketch, "E3369", {"points": [v(-102.48, 6.68) * mm, v(-102.82, 7.98) * mm, v(-103.16, 9.26) * mm, v(-103.5, 10.57) * mm]});
            skFitSpline(sketch, "E3370", {"points": [v(-103.5, 10.57) * mm, v(-104.67, 9.9) * mm, v(-105.82, 9.22) * mm, v(-107, 8.54) * mm]});
            skFitSpline(sketch, "E3371", {"points": [v(-113.29, 6.7) * mm, v(-113.23, 6.68) * mm, v(-113.21, 6.68) * mm, v(-113.2, 6.68) * mm]});
            skFitSpline(sketch, "E3372", {"points": [v(-113.2, 6.68) * mm, v(-112.45, 6.83) * mm, v(-111.7, 6.99) * mm, v(-110.95, 7.15) * mm]});
            skFitSpline(sketch, "E3373", {"points": [v(-110.95, 7.15) * mm, v(-110.86, 7.17) * mm, v(-110.78, 7.22) * mm, v(-110.7, 7.27) * mm]});
            skFitSpline(sketch, "E3374", {"points": [v(-110.7, 7.27) * mm, v(-110.27, 7.54) * mm, v(-109.85, 7.82) * mm, v(-109.43, 8.1) * mm]});
            skFitSpline(sketch, "E3375", {"points": [v(-109.43, 8.1) * mm, v(-109.22, 8.23) * mm, v(-109.01, 8.37) * mm, v(-108.76, 8.53) * mm]});
            skFitSpline(sketch, "E3376", {"points": [v(-108.76, 8.53) * mm, v(-109.95, 9.22) * mm, v(-111.1, 9.89) * mm, v(-112.26, 10.57) * mm]});
            skFitSpline(sketch, "E3377", {"points": [v(-112.26, 10.57) * mm, v(-112.6, 9.26) * mm, v(-112.95, 7.98) * mm, v(-113.29, 6.7) * mm]});
            skFitSpline(sketch, "E3378", {"points": [v(-101.4, -15.63) * mm, v(-101.46, -15.75) * mm, v(-101.51, -15.86) * mm, v(-101.55, -15.97) * mm]});
            skFitSpline(sketch, "E3379", {"points": [v(-101.55, -15.97) * mm, v(-101.72, -16.42) * mm, v(-101.88, -16.88) * mm, v(-102.05, -17.34) * mm]});
            skFitSpline(sketch, "E3380", {"points": [v(-102.05, -17.34) * mm, v(-102.17, -17.65) * mm, v(-102.28, -17.95) * mm, v(-102.4, -18.25) * mm]});
            skFitSpline(sketch, "E3381", {"points": [v(-102.4, -18.25) * mm, v(-102.5, -18.46) * mm, v(-102.65, -18.57) * mm, v(-102.88, -18.56) * mm]});
            skFitSpline(sketch, "E3382", {"points": [v(-102.88, -18.56) * mm, v(-103.08, -18.56) * mm, v(-103.23, -18.46) * mm, v(-103.3, -18.28) * mm]});
            skFitSpline(sketch, "E3383", {"points": [v(-103.3, -18.28) * mm, v(-103.38, -18.11) * mm, v(-103.34, -17.95) * mm, v(-103.28, -17.79) * mm]});
            skFitSpline(sketch, "E3384", {"points": [v(-103.28, -17.79) * mm, v(-103.16, -17.48) * mm, v(-103.04, -17.18) * mm, v(-102.93, -16.87) * mm]});
            skFitSpline(sketch, "E3385", {"points": [v(-102.93, -16.87) * mm, v(-102.75, -16.4) * mm, v(-102.58, -15.94) * mm, v(-102.4, -15.48) * mm]});
            skFitSpline(sketch, "E3386", {"points": [v(-102.4, -15.48) * mm, v(-102.37, -15.4) * mm, v(-102.34, -15.32) * mm, v(-102.3, -15.23) * mm]});
            skFitSpline(sketch, "E3387", {"points": [v(-102.3, -15.23) * mm, v(-102.76, -15) * mm, v(-103.19, -14.77) * mm, v(-103.64, -14.53) * mm]});
            skFitSpline(sketch, "E3388", {"points": [v(-103.64, -14.53) * mm, v(-103.7, -14.74) * mm, v(-103.77, -14.92) * mm, v(-103.82, -15.11) * mm]});
            skFitSpline(sketch, "E3389", {"points": [v(-103.82, -15.11) * mm, v(-103.88, -15.3) * mm, v(-103.92, -15.48) * mm, v(-103.97, -15.67) * mm]});
            skFitSpline(sketch, "E3390", {"points": [v(-103.97, -15.67) * mm, v(-104.04, -15.92) * mm, v(-104.33, -16.08) * mm, v(-104.6, -16.01) * mm]});
            skFitSpline(sketch, "E3391", {"points": [v(-104.6, -16.01) * mm, v(-104.84, -15.95) * mm, v(-105, -15.7) * mm, v(-104.93, -15.44) * mm]});
            skFitSpline(sketch, "E3392", {"points": [v(-104.93, -15.44) * mm, v(-104.89, -15.25) * mm, v(-104.83, -15.07) * mm, v(-104.78, -14.88) * mm]});
            skFitSpline(sketch, "E3393", {"points": [v(-104.78, -14.88) * mm, v(-104.6, -14.33) * mm, v(-104.44, -13.79) * mm, v(-104.28, -13.24) * mm]});
            skFitSpline(sketch, "E3394", {"points": [v(-104.28, -13.24) * mm, v(-104.17, -12.88) * mm, v(-104.07, -12.51) * mm, v(-103.97, -12.15) * mm]});
            skFitSpline(sketch, "E3395", {"points": [v(-103.97, -12.15) * mm, v(-103.9, -11.95) * mm, v(-103.85, -11.76) * mm, v(-103.79, -11.54) * mm]});
            skFitSpline(sketch, "E3396", {"points": [v(-103.79, -11.54) * mm, v(-105.15, -10.74) * mm, v(-106.5, -9.95) * mm, v(-107.88, -9.15) * mm]});
            skFitSpline(sketch, "E3397", {"points": [v(-107.88, -9.15) * mm, v(-109.23, -9.94) * mm, v(-110.6, -10.73) * mm, v(-111.97, -11.54) * mm]});
            skFitSpline(sketch, "E3398", {"points": [v(-111.97, -11.54) * mm, v(-111.95, -11.63) * mm, v(-111.93, -11.72) * mm, v(-111.9, -11.8) * mm]});
            skFitSpline(sketch, "E3399", {"points": [v(-111.9, -11.8) * mm, v(-111.8, -12.15) * mm, v(-111.7, -12.5) * mm, v(-111.6, -12.84) * mm]});
            skFitSpline(sketch, "E3400", {"points": [v(-111.6, -12.84) * mm, v(-111.44, -13.38) * mm, v(-111.28, -13.91) * mm, v(-111.12, -14.45) * mm]});
            skFitSpline(sketch, "E3401", {"points": [v(-111.12, -14.45) * mm, v(-111.03, -14.75) * mm, v(-110.93, -15.06) * mm, v(-110.85, -15.36) * mm]});
            skFitSpline(sketch, "E3402", {"points": [v(-110.85, -15.36) * mm, v(-110.76, -15.67) * mm, v(-110.9, -15.95) * mm, v(-111.17, -16.02) * mm]});
            skFitSpline(sketch, "E3403", {"points": [v(-111.17, -16.02) * mm, v(-111.46, -16.09) * mm, v(-111.73, -15.9) * mm, v(-111.81, -15.6) * mm]});
            skFitSpline(sketch, "E3404", {"points": [v(-111.81, -15.6) * mm, v(-111.9, -15.24) * mm, v(-112.01, -14.9) * mm, v(-112.11, -14.53) * mm]});
            skFitSpline(sketch, "E3405", {"points": [v(-112.11, -14.53) * mm, v(-112.58, -14.77) * mm, v(-113, -15) * mm, v(-113.45, -15.22) * mm]});
            skFitSpline(sketch, "E3406", {"points": [v(-113.45, -15.22) * mm, v(-113.43, -15.28) * mm, v(-113.42, -15.34) * mm, v(-113.4, -15.39) * mm]});
            skFitSpline(sketch, "E3407", {"points": [v(-113.4, -15.39) * mm, v(-113.13, -16.1) * mm, v(-112.86, -16.82) * mm, v(-112.6, -17.54) * mm]});
            skFitSpline(sketch, "E3408", {"points": [v(-112.6, -17.54) * mm, v(-112.54, -17.68) * mm, v(-112.48, -17.82) * mm, v(-112.44, -17.96) * mm]});
            skFitSpline(sketch, "E3409", {"points": [v(-112.44, -17.96) * mm, v(-112.37, -18.22) * mm, v(-112.5, -18.46) * mm, v(-112.74, -18.54) * mm]});
            skFitSpline(sketch, "E3410", {"points": [v(-112.74, -18.54) * mm, v(-112.97, -18.62) * mm, v(-113.24, -18.52) * mm, v(-113.34, -18.28) * mm]});
            skFitSpline(sketch, "E3411", {"points": [v(-113.34, -18.28) * mm, v(-113.47, -18) * mm, v(-113.58, -17.69) * mm, v(-113.7, -17.4) * mm]});
            skFitSpline(sketch, "E3412", {"points": [v(-113.7, -17.4) * mm, v(-113.9, -16.86) * mm, v(-114.09, -16.33) * mm, v(-114.29, -15.8) * mm]});
            skFitSpline(sketch, "E3413", {"points": [v(-114.29, -15.8) * mm, v(-114.3, -15.75) * mm, v(-114.33, -15.7) * mm, v(-114.36, -15.64) * mm]});
            skFitSpline(sketch, "E3414", {"points": [v(-114.36, -15.64) * mm, v(-114.43, -15.66) * mm, v(-114.49, -15.68) * mm, v(-114.54, -15.7) * mm]});
            skFitSpline(sketch, "E3415", {"points": [v(-114.54, -15.7) * mm, v(-115.04, -15.93) * mm, v(-115.53, -16.16) * mm, v(-116.02, -16.38) * mm]});
            skFitSpline(sketch, "E3416", {"points": [v(-116.02, -16.38) * mm, v(-116.3, -16.5) * mm, v(-116.6, -16.64) * mm, v(-116.88, -16.76) * mm]});
            skFitSpline(sketch, "E3417", {"points": [v(-116.88, -16.76) * mm, v(-116.94, -16.78) * mm, v(-117, -16.8) * mm, v(-117.06, -16.81) * mm]});
            skFitSpline(sketch, "E3418", {"points": [v(-117.06, -16.81) * mm, v(-117.28, -16.84) * mm, v(-117.49, -16.72) * mm, v(-117.57, -16.53) * mm]});
            skFitSpline(sketch, "E3419", {"points": [v(-117.57, -16.53) * mm, v(-117.65, -16.32) * mm, v(-117.6, -16.07) * mm, v(-117.4, -15.95) * mm]});
            skFitSpline(sketch, "E3420", {"points": [v(-117.4, -15.95) * mm, v(-117.22, -15.84) * mm, v(-117, -15.76) * mm, v(-116.8, -15.66) * mm]});
            skFitSpline(sketch, "E3421", {"points": [v(-116.8, -15.66) * mm, v(-116.4, -15.48) * mm, v(-116.02, -15.3) * mm, v(-115.63, -15.13) * mm]});
            skFitSpline(sketch, "E3422", {"points": [v(-115.63, -15.13) * mm, v(-115.33, -15) * mm, v(-115.03, -14.85) * mm, v(-114.71, -14.7) * mm]});
            skFitSpline(sketch, "E3423", {"points": [v(-114.71, -14.7) * mm, v(-114.86, -14.24) * mm, v(-115, -13.77) * mm, v(-115.16, -13.29) * mm]});
            skFitSpline(sketch, "E3424", {"points": [v(-115.16, -13.29) * mm, v(-115.51, -13.42) * mm, v(-115.82, -13.63) * mm, v(-116.13, -13.8) * mm]});
            skFitSpline(sketch, "E3425", {"points": [v(-116.13, -13.8) * mm, v(-116.27, -13.89) * mm, v(-116.4, -13.94) * mm, v(-116.57, -13.89) * mm]});
            skFitSpline(sketch, "E3426", {"points": [v(-116.57, -13.89) * mm, v(-116.78, -13.82) * mm, v(-116.91, -13.69) * mm, v(-116.94, -13.47) * mm]});
            skFitSpline(sketch, "E3427", {"points": [v(-116.94, -13.47) * mm, v(-116.97, -13.26) * mm, v(-116.88, -13.1) * mm, v(-116.7, -12.99) * mm]});
            skFitSpline(sketch, "E3428", {"points": [v(-116.7, -12.99) * mm, v(-116.47, -12.86) * mm, v(-116.25, -12.74) * mm, v(-116.02, -12.62) * mm]});
            skFitSpline(sketch, "E3429", {"points": [v(-116.02, -12.62) * mm, v(-115.73, -12.46) * mm, v(-115.44, -12.3) * mm, v(-115.14, -12.13) * mm]});
            skFitSpline(sketch, "E3430", {"points": [v(-115.14, -12.13) * mm, v(-114.57, -11.83) * mm, v(-114, -11.52) * mm, v(-113.43, -11.21) * mm]});
            skFitSpline(sketch, "E3431", {"points": [v(-113.43, -11.21) * mm, v(-113.34, -11.17) * mm, v(-113.25, -11.11) * mm, v(-113.16, -11.06) * mm]});
            skFitSpline(sketch, "E3432", {"points": [v(-113.16, -11.06) * mm, v(-113.17, -11) * mm, v(-113.17, -10.94) * mm, v(-113.18, -10.89) * mm]});
            skFitSpline(sketch, "E3433", {"points": [v(-113.18, -10.89) * mm, v(-113.3, -10.45) * mm, v(-113.4, -10) * mm, v(-113.52, -9.57) * mm]});
            skFitSpline(sketch, "E3434", {"points": [v(-113.52, -9.57) * mm, v(-113.6, -9.24) * mm, v(-113.7, -8.92) * mm, v(-113.79, -8.6) * mm]});
            skFitSpline(sketch, "E3435", {"points": [v(-113.79, -8.6) * mm, v(-113.97, -7.94) * mm, v(-114.14, -7.27) * mm, v(-114.3, -6.6) * mm]});
            skFitSpline(sketch, "E3436", {"points": [v(-114.3, -6.6) * mm, v(-114.34, -6.5) * mm, v(-114.37, -6.45) * mm, v(-114.48, -6.42) * mm]});
            skFitSpline(sketch, "E3437", {"points": [v(-114.48, -6.42) * mm, v(-115.31, -6.22) * mm, v(-116.14, -6) * mm, v(-116.96, -5.79) * mm]});
            skFitSpline(sketch, "E3438", {"points": [v(-116.96, -5.79) * mm, v(-117.61, -5.62) * mm, v(-118.26, -5.44) * mm, v(-118.92, -5.27) * mm]});
            skFitSpline(sketch, "E3439", {"points": [v(-118.92, -5.27) * mm, v(-118.97, -5.33) * mm, v(-119.01, -5.4) * mm, v(-119.05, -5.46) * mm]});
            skFitSpline(sketch, "E3440", {"points": [v(-119.05, -5.46) * mm, v(-119.27, -5.86) * mm, v(-119.5, -6.25) * mm, v(-119.7, -6.65) * mm]});
            skFitSpline(sketch, "E3441", {"points": [v(-119.7, -6.65) * mm, v(-120.08, -7.34) * mm, v(-120.44, -8.02) * mm, v(-120.8, -8.7) * mm]});
            skFitSpline(sketch, "E3442", {"points": [v(-120.8, -8.7) * mm, v(-120.82, -8.74) * mm, v(-120.84, -8.77) * mm, v(-120.86, -8.8) * mm]});
            skFitSpline(sketch, "E3443", {"points": [v(-120.86, -8.8) * mm, v(-121.03, -9.06) * mm, v(-121.3, -9.14) * mm, v(-121.55, -9) * mm]});
            skFitSpline(sketch, "E3444", {"points": [v(-121.55, -9) * mm, v(-121.78, -8.85) * mm, v(-121.85, -8.53) * mm, v(-121.7, -8.28) * mm]});
            skFitSpline(sketch, "E3445", {"points": [v(-121.7, -8.28) * mm, v(-121.55, -8) * mm, v(-121.4, -7.72) * mm, v(-121.24, -7.44) * mm]});
            skFitSpline(sketch, "E3446", {"points": [v(-121.24, -7.44) * mm, v(-121.21, -7.4) * mm, v(-121.2, -7.34) * mm, v(-121.17, -7.27) * mm]});
            skFitSpline(sketch, "E3447", {"points": [v(-121.17, -7.27) * mm, v(-121.65, -7.12) * mm, v(-122.1, -6.98) * mm, v(-122.57, -6.83) * mm]});
            skFitSpline(sketch, "E3448", {"points": [v(-122.57, -6.83) * mm, v(-122.6, -6.87) * mm, v(-122.62, -6.88) * mm, v(-122.62, -6.9) * mm]});
            skFitSpline(sketch, "E3449", {"points": [v(-122.62, -6.9) * mm, v(-122.99, -7.7) * mm, v(-123.35, -8.51) * mm, v(-123.72, -9.32) * mm]});
            skFitSpline(sketch, "E3450", {"points": [v(-123.72, -9.32) * mm, v(-123.79, -9.48) * mm, v(-123.87, -9.63) * mm, v(-124.04, -9.69) * mm]});
            skFitSpline(sketch, "E3451", {"points": [v(-124.04, -9.69) * mm, v(-124.23, -9.75) * mm, v(-124.4, -9.73) * mm, v(-124.55, -9.59) * mm]});
            skFitSpline(sketch, "E3452", {"points": [v(-124.55, -9.59) * mm, v(-124.72, -9.43) * mm, v(-124.74, -9.23) * mm, v(-124.66, -9.03) * mm]});
            skFitSpline(sketch, "E3453", {"points": [v(-124.66, -9.03) * mm, v(-124.55, -8.75) * mm, v(-124.42, -8.47) * mm, v(-124.3, -8.2) * mm]});
            skFitSpline(sketch, "E3454", {"points": [v(-124.3, -8.2) * mm, v(-124.07, -7.7) * mm, v(-123.84, -7.21) * mm, v(-123.61, -6.72) * mm]});
            skFitSpline(sketch, "E3455", {"points": [v(-123.61, -6.72) * mm, v(-123.58, -6.65) * mm, v(-123.55, -6.57) * mm, v(-123.51, -6.47) * mm]});
            skFitSpline(sketch, "E3456", {"points": [v(-123.51, -6.47) * mm, v(-123.75, -6.38) * mm, v(-123.98, -6.28) * mm, v(-124.2, -6.2) * mm]});
            skFitSpline(sketch, "E3457", {"points": [v(-124.2, -6.2) * mm, v(-124.83, -5.97) * mm, v(-125.45, -5.74) * mm, v(-126.07, -5.5) * mm]});
            skFitSpline(sketch, "E3458", {"points": [v(-126.07, -5.5) * mm, v(-126.15, -5.47) * mm, v(-126.24, -5.42) * mm, v(-126.3, -5.35) * mm]});
            skFitSpline(sketch, "E3459", {"points": [v(-126.3, -5.35) * mm, v(-126.46, -5.21) * mm, v(-126.5, -5) * mm, v(-126.41, -4.82) * mm]});
            skFitSpline(sketch, "E3460", {"points": [v(-126.41, -4.82) * mm, v(-126.33, -4.64) * mm, v(-126.16, -4.53) * mm, v(-125.95, -4.54) * mm]});
            skFitSpline(sketch, "E3461", {"points": [v(-125.95, -4.54) * mm, v(-125.86, -4.55) * mm, v(-125.76, -4.57) * mm, v(-125.67, -4.6) * mm]});
            skFitSpline(sketch, "E3462", {"points": [v(-125.67, -4.6) * mm, v(-125.5, -4.67) * mm, v(-125.32, -4.76) * mm, v(-125.14, -4.82) * mm]});
            skFitSpline(sketch, "E3463", {"points": [v(-125.14, -4.82) * mm, v(-124.48, -5.07) * mm, v(-123.8, -5.31) * mm, v(-123.1, -5.56) * mm]});
            skFitSpline(sketch, "E3464", {"points": [v(-123.1, -5.56) * mm, v(-122.89, -5.14) * mm, v(-122.66, -4.7) * mm, v(-122.42, -4.24) * mm]});
            skFitSpline(sketch, "E3465", {"points": [v(-122.42, -4.24) * mm, v(-122.6, -4.18) * mm, v(-122.77, -4.12) * mm, v(-122.94, -4.07) * mm]});
            skFitSpline(sketch, "E3466", {"points": [v(-122.94, -4.07) * mm, v(-123.13, -4.02) * mm, v(-123.33, -3.97) * mm, v(-123.52, -3.92) * mm]});
            skFitSpline(sketch, "E3467", {"points": [v(-123.52, -3.92) * mm, v(-123.8, -3.85) * mm, v(-123.97, -3.56) * mm, v(-123.9, -3.29) * mm]});
            skFitSpline(sketch, "E3468", {"points": [v(-123.9, -3.29) * mm, v(-123.83, -3.02) * mm, v(-123.57, -2.88) * mm, v(-123.28, -2.96) * mm]});
            skFitSpline(sketch, "E3469", {"points": [v(-123.28, -2.96) * mm, v(-123.03, -3.02) * mm, v(-122.79, -3.1) * mm, v(-122.54, -3.17) * mm]});
            skFitSpline(sketch, "E3470", {"points": [v(-122.54, -3.17) * mm, v(-122.24, -3.26) * mm, v(-121.95, -3.35) * mm, v(-121.65, -3.44) * mm]});
            skFitSpline(sketch, "E3471", {"points": [v(-121.65, -3.44) * mm, v(-121, -3.63) * mm, v(-120.36, -3.82) * mm, v(-119.72, -4.01) * mm]});
            skFitSpline(sketch, "E3472", {"points": [v(-119.72, -4.01) * mm, v(-119.62, -4.04) * mm, v(-119.52, -4.06) * mm, v(-119.42, -4.09) * mm]});
            skFitSpline(sketch, "E3473", {"points": [v(-119.42, -4.09) * mm, v(-118.62, -2.72) * mm, v(-117.83, -1.36) * mm, v(-117.03, 0) * mm]});
            skFitSpline(sketch, "E3474", {"points": [v(-117.03, 0) * mm, v(-117.82, 1.35) * mm, v(-118.61, 2.7) * mm, v(-119.42, 4.09) * mm]});
            skFitSpline(sketch, "E3475", {"points": [v(-119.42, 4.09) * mm, v(-119.5, 4.07) * mm, v(-119.6, 4.05) * mm, v(-119.69, 4.02) * mm]});
            skFitSpline(sketch, "E3476", {"points": [v(-119.69, 4.02) * mm, v(-120.29, 3.84) * mm, v(-120.9, 3.66) * mm, v(-121.5, 3.48) * mm]});
            skFitSpline(sketch, "E3477", {"points": [v(-121.5, 3.48) * mm, v(-122.06, 3.3) * mm, v(-122.63, 3.14) * mm, v(-123.2, 2.98) * mm]});
            skFitSpline(sketch, "E3478", {"points": [v(-123.2, 2.98) * mm, v(-123.3, 2.95) * mm, v(-123.42, 2.93) * mm, v(-123.52, 2.94) * mm]});
            skFitSpline(sketch, "E3479", {"points": [v(-123.52, 2.94) * mm, v(-123.75, 2.98) * mm, v(-123.9, 3.17) * mm, v(-123.91, 3.4) * mm]});
            skFitSpline(sketch, "E3480", {"points": [v(-123.91, 3.4) * mm, v(-123.92, 3.65) * mm, v(-123.76, 3.86) * mm, v(-123.51, 3.93) * mm]});
            skFitSpline(sketch, "E3481", {"points": [v(-123.51, 3.93) * mm, v(-123.21, 4) * mm, v(-122.91, 4.1) * mm, v(-122.61, 4.18) * mm]});
            skFitSpline(sketch, "E3482", {"points": [v(-122.61, 4.18) * mm, v(-122.55, 4.2) * mm, v(-122.5, 4.22) * mm, v(-122.42, 4.25) * mm]});
            skFitSpline(sketch, "E3483", {"points": [v(-122.42, 4.25) * mm, v(-122.65, 4.7) * mm, v(-122.87, 5.12) * mm, v(-123.1, 5.54) * mm]});
            skFitSpline(sketch, "E3484", {"points": [v(-123.1, 5.54) * mm, v(-123.12, 5.55) * mm, v(-123.14, 5.56) * mm, v(-123.15, 5.56) * mm]});
            skFitSpline(sketch, "E3485", {"points": [v(-123.15, 5.56) * mm, v(-123.99, 5.24) * mm, v(-124.82, 4.93) * mm, v(-125.66, 4.61) * mm]});
            skFitSpline(sketch, "E3486", {"points": [v(-125.66, 4.61) * mm, v(-125.73, 4.59) * mm, v(-125.8, 4.56) * mm, v(-125.87, 4.55) * mm]});
            skFitSpline(sketch, "E3487", {"points": [v(-125.87, 4.55) * mm, v(-126.14, 4.5) * mm, v(-126.35, 4.63) * mm, v(-126.43, 4.88) * mm]});
            skFitSpline(sketch, "E3488", {"points": [v(-126.43, 4.88) * mm, v(-126.5, 5.11) * mm, v(-126.4, 5.36) * mm, v(-126.15, 5.47) * mm]});
            skFitSpline(sketch, "E3489", {"points": [v(-126.15, 5.47) * mm, v(-125.86, 5.6) * mm, v(-125.57, 5.7) * mm, v(-125.28, 5.8) * mm]});
            skFitSpline(sketch, "E3490", {"points": [v(-125.28, 5.8) * mm, v(-124.74, 6.01) * mm, v(-124.2, 6.2) * mm, v(-123.66, 6.4) * mm]});
            skFitSpline(sketch, "E3491", {"points": [v(-123.66, 6.4) * mm, v(-123.62, 6.43) * mm, v(-123.58, 6.45) * mm, v(-123.51, 6.48) * mm]});
            skFitSpline(sketch, "E3492", {"points": [v(-123.51, 6.48) * mm, v(-123.6, 6.7) * mm, v(-123.7, 6.91) * mm, v(-123.8, 7.12) * mm]});
            skFitSpline(sketch, "E3493", {"points": [v(-123.8, 7.12) * mm, v(-124.07, 7.74) * mm, v(-124.36, 8.36) * mm, v(-124.63, 8.97) * mm]});
            skFitSpline(sketch, "E3494", {"points": [v(-124.63, 8.97) * mm, v(-124.67, 9.06) * mm, v(-124.69, 9.16) * mm, v(-124.7, 9.25) * mm]});
            skFitSpline(sketch, "E3495", {"points": [v(-124.7, 9.25) * mm, v(-124.7, 9.46) * mm, v(-124.6, 9.6) * mm, v(-124.4, 9.68) * mm]});
            skFitSpline(sketch, "E3496", {"points": [v(-124.4, 9.68) * mm, v(-124.22, 9.77) * mm, v(-123.99, 9.71) * mm, v(-123.86, 9.56) * mm]});
            skFitSpline(sketch, "E3497", {"points": [v(-123.86, 9.56) * mm, v(-123.8, 9.48) * mm, v(-123.75, 9.4) * mm, v(-123.71, 9.31) * mm]});
            skFitSpline(sketch, "E3498", {"points": [v(-123.71, 9.31) * mm, v(-123.64, 9.14) * mm, v(-123.57, 8.96) * mm, v(-123.5, 8.78) * mm]});
            skFitSpline(sketch, "E3499", {"points": [v(-123.5, 8.78) * mm, v(-123.2, 8.16) * mm, v(-122.92, 7.53) * mm, v(-122.63, 6.91) * mm]});
            skFitSpline(sketch, "E3500", {"points": [v(-122.63, 6.91) * mm, v(-122.62, 6.89) * mm, v(-122.6, 6.87) * mm, v(-122.58, 6.83) * mm]});
            skFitSpline(sketch, "E3501", {"points": [v(-122.58, 6.83) * mm, v(-122.12, 6.98) * mm, v(-121.66, 7.12) * mm, v(-121.18, 7.27) * mm]});
            skFitSpline(sketch, "E3502", {"points": [v(-121.18, 7.27) * mm, v(-121.23, 7.46) * mm, v(-121.33, 7.62) * mm, v(-121.42, 7.79) * mm]});
            skFitSpline(sketch, "E3503", {"points": [v(-121.42, 7.79) * mm, v(-121.51, 7.96) * mm, v(-121.62, 8.12) * mm, v(-121.71, 8.28) * mm]});
            skFitSpline(sketch, "E3504", {"points": [v(-121.71, 8.28) * mm, v(-121.86, 8.53) * mm, v(-121.78, 8.85) * mm, v(-121.54, 9) * mm]});
            skFitSpline(sketch, "E3505", {"points": [v(-121.54, 9) * mm, v(-121.3, 9.14) * mm, v(-121.02, 9.06) * mm, v(-120.86, 8.8) * mm]});
            skFitSpline(sketch, "E3506", {"points": [v(-120.86, 8.8) * mm, v(-120.76, 8.64) * mm, v(-120.68, 8.47) * mm, v(-120.59, 8.3) * mm]});
            skFitSpline(sketch, "E3507", {"points": [v(-120.59, 8.3) * mm, v(-120.32, 7.8) * mm, v(-120.06, 7.3) * mm, v(-119.79, 6.8) * mm]});
            skFitSpline(sketch, "E3508", {"points": [v(-119.79, 6.8) * mm, v(-119.52, 6.31) * mm, v(-119.25, 5.83) * mm, v(-118.99, 5.35) * mm]});
            skFitSpline(sketch, "E3509", {"points": [v(-118.99, 5.35) * mm, v(-118.97, 5.32) * mm, v(-118.95, 5.3) * mm, v(-118.92, 5.27) * mm]});
            skFitSpline(sketch, "E3510", {"points": [v(-118.92, 5.27) * mm, v(-117.4, 5.67) * mm, v(-115.88, 6.07) * mm, v(-114.35, 6.47) * mm]});
            skFitSpline(sketch, "E3511", {"points": [v(-114.35, 6.47) * mm, v(-113.95, 7.98) * mm, v(-113.55, 9.5) * mm, v(-113.15, 11.05) * mm]});
            skFitSpline(sketch, "E3512", {"points": [v(-113.15, 11.05) * mm, v(-113.23, 11.1) * mm, v(-113.31, 11.15) * mm, v(-113.4, 11.2) * mm]});
            skFitSpline(sketch, "E3513", {"points": [v(-113.4, 11.2) * mm, v(-113.72, 11.38) * mm, v(-114.05, 11.56) * mm, v(-114.38, 11.74) * mm]});
            skFitSpline(sketch, "E3514", {"points": [v(-114.38, 11.74) * mm, v(-114.83, 11.99) * mm, v(-115.28, 12.23) * mm, v(-115.73, 12.47) * mm]});
            skFitSpline(sketch, "E3515", {"points": [v(-115.73, 12.47) * mm, v(-116.04, 12.64) * mm, v(-116.35, 12.8) * mm, v(-116.66, 12.96) * mm]});
            skFitSpline(sketch, "E3516", {"points": [v(-116.66, 12.96) * mm, v(-116.88, 13.08) * mm, v(-116.98, 13.27) * mm, v(-116.94, 13.47) * mm]});
            skFitSpline(sketch, "E3517", {"points": [v(-116.94, 13.47) * mm, v(-116.9, 13.7) * mm, v(-116.75, 13.84) * mm, v(-116.51, 13.9) * mm]});
            skFitSpline(sketch, "E3518", {"points": [v(-116.51, 13.9) * mm, v(-116.37, 13.93) * mm, v(-116.25, 13.87) * mm, v(-116.13, 13.8) * mm]});
            skFitSpline(sketch, "E3519", {"points": [v(-116.13, 13.8) * mm, v(-115.82, 13.63) * mm, v(-115.5, 13.45) * mm, v(-115.17, 13.26) * mm]});
            skFitSpline(sketch, "E3520", {"points": [v(-115.17, 13.26) * mm, v(-115, 13.76) * mm, v(-114.86, 14.23) * mm, v(-114.7, 14.7) * mm]});
            skFitSpline(sketch, "E3521", {"points": [v(-114.7, 14.7) * mm, v(-114.8, 14.75) * mm, v(-114.88, 14.79) * mm, v(-114.95, 14.82) * mm]});
            skFitSpline(sketch, "E3522", {"points": [v(-114.95, 14.82) * mm, v(-115.48, 15.06) * mm, v(-116, 15.3) * mm, v(-116.52, 15.54) * mm]});
            skFitSpline(sketch, "E3523", {"points": [v(-116.52, 15.54) * mm, v(-116.75, 15.64) * mm, v(-116.98, 15.73) * mm, v(-117.2, 15.83) * mm]});
            skFitSpline(sketch, "E3524", {"points": [v(-117.2, 15.83) * mm, v(-117.4, 15.92) * mm, v(-117.56, 16.02) * mm, v(-117.6, 16.25) * mm]});
            skFitSpline(sketch, "E3525", {"points": [v(-117.6, 16.25) * mm, v(-117.65, 16.66) * mm, v(-117.3, 16.93) * mm, v(-116.9, 16.77) * mm]});
            skFitSpline(sketch, "E3526", {"points": [v(-116.9, 16.77) * mm, v(-116.6, 16.65) * mm, v(-116.3, 16.5) * mm, v(-116.02, 16.38) * mm]});
            skFitSpline(sketch, "E3527", {"points": [v(-116.02, 16.38) * mm, v(-115.47, 16.13) * mm, v(-114.93, 15.88) * mm, v(-114.36, 15.62) * mm]});
            skFitSpline(sketch, "E3528", {"points": [v(-114.36, 15.62) * mm, v(-114.26, 15.86) * mm, v(-114.17, 16.1) * mm, v(-114.08, 16.32) * mm]});
            skFitSpline(sketch, "E3529", {"points": [v(-114.08, 16.32) * mm, v(-113.85, 16.94) * mm, v(-113.62, 17.56) * mm, v(-113.39, 18.18) * mm]});
            skFitSpline(sketch, "E3530", {"points": [v(-113.39, 18.18) * mm, v(-113.37, 18.23) * mm, v(-113.35, 18.28) * mm, v(-113.32, 18.33) * mm]});
            skFitSpline(sketch, "E3531", {"points": [v(-113.32, 18.33) * mm, v(-113.19, 18.53) * mm, v(-112.95, 18.62) * mm, v(-112.73, 18.54) * mm]});
            skFitSpline(sketch, "E3532", {"points": [v(-112.73, 18.54) * mm, v(-112.5, 18.45) * mm, v(-112.37, 18.23) * mm, v(-112.44, 17.98) * mm]});
            skFitSpline(sketch, "E3533", {"points": [v(-112.44, 17.98) * mm, v(-112.5, 17.76) * mm, v(-112.6, 17.55) * mm, v(-112.68, 17.33) * mm]});
            skFitSpline(sketch, "E3534", {"points": [v(-112.68, 17.33) * mm, v(-112.93, 16.64) * mm, v(-113.19, 15.94) * mm, v(-113.45, 15.23) * mm]});
            skFitSpline(sketch, "E3535", {"points": [v(-113.45, 15.23) * mm, v(-113.02, 15) * mm, v(-112.6, 14.78) * mm, v(-112.13, 14.53) * mm]});
            skFitSpline(sketch, "E3536", {"points": [v(-112.13, 14.53) * mm, v(-112.06, 14.73) * mm, v(-112, 14.9) * mm, v(-111.94, 15.1) * mm]});
            skFitSpline(sketch, "E3537", {"points": [v(-111.94, 15.1) * mm, v(-111.9, 15.27) * mm, v(-111.85, 15.45) * mm, v(-111.8, 15.63) * mm]});
            skFitSpline(sketch, "E3538", {"points": [v(-111.8, 15.63) * mm, v(-111.73, 15.92) * mm, v(-111.44, 16.1) * mm, v(-111.16, 16.01) * mm]});
            skFitSpline(sketch, "E3539", {"points": [v(-111.16, 16.01) * mm, v(-110.9, 15.94) * mm, v(-110.76, 15.67) * mm, v(-110.84, 15.38) * mm]});
            skFitSpline(sketch, "E3540", {"points": [v(-110.84, 15.38) * mm, v(-110.9, 15.14) * mm, v(-110.98, 14.9) * mm, v(-111.05, 14.67) * mm]});
            skFitSpline(sketch, "E3541", {"points": [v(-111.05, 14.67) * mm, v(-111.15, 14.35) * mm, v(-111.24, 14.04) * mm, v(-111.33, 13.73) * mm]});
            skFitSpline(sketch, "E3542", {"points": [v(-111.33, 13.73) * mm, v(-111.52, 13.1) * mm, v(-111.7, 12.46) * mm, v(-111.9, 11.82) * mm]});
            skFitSpline(sketch, "E3543", {"points": [v(-111.9, 11.82) * mm, v(-111.92, 11.73) * mm, v(-111.95, 11.64) * mm, v(-111.98, 11.54) * mm]});
            skFitSpline(sketch, "E3544", {"points": [v(-111.98, 11.54) * mm, v(-110.6, 10.74) * mm, v(-109.24, 9.94) * mm, v(-107.88, 9.15) * mm]});
            skFitSpline(sketch, "E3545", {"points": [v(-107.88, 9.15) * mm, v(-106.52, 9.94) * mm, v(-105.16, 10.74) * mm, v(-103.8, 11.54) * mm]});
            skFitSpline(sketch, "E3546", {"points": [v(-103.8, 11.54) * mm, v(-103.82, 11.63) * mm, v(-103.84, 11.71) * mm, v(-103.86, 11.8) * mm]});
            skFitSpline(sketch, "E3547", {"points": [v(-103.86, 11.8) * mm, v(-103.97, 12.16) * mm, v(-104.07, 12.53) * mm, v(-104.18, 12.9) * mm]});
            skFitSpline(sketch, "E3548", {"points": [v(-104.18, 12.9) * mm, v(-104.33, 13.43) * mm, v(-104.5, 13.95) * mm, v(-104.65, 14.48) * mm]});
            skFitSpline(sketch, "E3549", {"points": [v(-104.65, 14.48) * mm, v(-104.74, 14.77) * mm, v(-104.83, 15.06) * mm, v(-104.91, 15.35) * mm]});
            skFitSpline(sketch, "E3550", {"points": [v(-104.91, 15.35) * mm, v(-104.94, 15.44) * mm, v(-104.95, 15.54) * mm, v(-104.94, 15.63) * mm]});
            skFitSpline(sketch, "E3551", {"points": [v(-104.94, 15.63) * mm, v(-104.9, 15.87) * mm, v(-104.72, 16.02) * mm, v(-104.5, 16.03) * mm]});
            skFitSpline(sketch, "E3552", {"points": [v(-104.5, 16.03) * mm, v(-104.24, 16.04) * mm, v(-104.03, 15.88) * mm, v(-103.96, 15.64) * mm]});
            skFitSpline(sketch, "E3553", {"points": [v(-103.96, 15.64) * mm, v(-103.86, 15.28) * mm, v(-103.76, 14.92) * mm, v(-103.66, 14.53) * mm]});
            skFitSpline(sketch, "E3554", {"points": [v(-103.66, 14.53) * mm, v(-103.2, 14.77) * mm, v(-102.76, 15) * mm, v(-102.32, 15.23) * mm]});
            skFitSpline(sketch, "E3555", {"points": [v(-102.32, 15.23) * mm, v(-102.34, 15.29) * mm, v(-102.35, 15.33) * mm, v(-102.36, 15.38) * mm]});
            skFitSpline(sketch, "E3556", {"points": [v(-102.36, 15.38) * mm, v(-102.63, 16.09) * mm, v(-102.9, 16.8) * mm, v(-103.16, 17.5) * mm]});
            skFitSpline(sketch, "E3557", {"points": [v(-103.16, 17.5) * mm, v(-103.2, 17.6) * mm, v(-103.24, 17.7) * mm, v(-103.28, 17.8) * mm]});
            skFitSpline(sketch, "E3558", {"points": [v(-103.28, 17.8) * mm, v(-103.34, 17.94) * mm, v(-103.38, 18.1) * mm, v(-103.32, 18.26) * mm]});
            skFitSpline(sketch, "E3559", {"points": [v(-103.32, 18.26) * mm, v(-103.24, 18.45) * mm, v(-103.1, 18.56) * mm, v(-102.9, 18.57) * mm]});
            skFitSpline(sketch, "E3560", {"points": [v(-102.9, 18.57) * mm, v(-102.67, 18.58) * mm, v(-102.5, 18.47) * mm, v(-102.42, 18.27) * mm]});
            skFitSpline(sketch, "E3561", {"points": [v(-102.42, 18.27) * mm, v(-102.3, 18) * mm, v(-102.2, 17.7) * mm, v(-102.09, 17.42) * mm]});
            skFitSpline(sketch, "E3562", {"points": [v(-102.09, 17.42) * mm, v(-101.88, 16.87) * mm, v(-101.67, 16.32) * mm, v(-101.47, 15.76) * mm]});
            skFitSpline(sketch, "E3563", {"points": [v(-101.47, 15.76) * mm, v(-101.45, 15.73) * mm, v(-101.43, 15.7) * mm, v(-101.4, 15.63) * mm]});
            skFitSpline(sketch, "E3564", {"points": [v(-101.4, 15.63) * mm, v(-101.19, 15.72) * mm, v(-100.98, 15.8) * mm, v(-100.77, 15.9) * mm]});
            skFitSpline(sketch, "E3565", {"points": [v(-100.77, 15.9) * mm, v(-100.15, 16.18) * mm, v(-99.54, 16.47) * mm, v(-98.92, 16.75) * mm]});
            skFitSpline(sketch, "E3566", {"points": [v(-98.92, 16.75) * mm, v(-98.87, 16.77) * mm, v(-98.82, 16.8) * mm, v(-98.76, 16.8) * mm]});
            skFitSpline(sketch, "E3567", {"points": [v(-98.76, 16.8) * mm, v(-98.5, 16.85) * mm, v(-98.28, 16.74) * mm, v(-98.2, 16.51) * mm]});
            skFitSpline(sketch, "E3568", {"points": [v(-98.2, 16.51) * mm, v(-98.1, 16.29) * mm, v(-98.18, 16.05) * mm, v(-98.41, 15.92) * mm]});
            skFitSpline(sketch, "E3569", {"points": [v(-98.41, 15.92) * mm, v(-98.6, 15.82) * mm, v(-98.79, 15.74) * mm, v(-98.98, 15.66) * mm]});
            skFitSpline(sketch, "E3570", {"points": [v(-98.98, 15.66) * mm, v(-99.64, 15.35) * mm, v(-100.31, 15.05) * mm, v(-100.98, 14.74) * mm]});
            skFitSpline(sketch, "E3571", {"points": [v(-100.98, 14.74) * mm, v(-101, 14.74) * mm, v(-101.02, 14.72) * mm, v(-101.05, 14.7) * mm]});
            skFitSpline(sketch, "E3572", {"points": [v(-101.05, 14.7) * mm, v(-100.9, 14.23) * mm, v(-100.76, 13.77) * mm, v(-100.6, 13.28) * mm]});
            skFitSpline(sketch, "E3573", {"points": [v(-100.6, 13.28) * mm, v(-100.42, 13.37) * mm, v(-100.25, 13.45) * mm, v(-100.09, 13.54) * mm]});
            skFitSpline(sketch, "E3574", {"points": [v(-100.09, 13.54) * mm, v(-99.92, 13.63) * mm, v(-99.76, 13.74) * mm, v(-99.6, 13.83) * mm]});
            skFitSpline(sketch, "E3575", {"points": [v(-99.6, 13.83) * mm, v(-99.35, 13.97) * mm, v(-99.03, 13.9) * mm, v(-98.88, 13.65) * mm]});
            skFitSpline(sketch, "E3576", {"points": [v(-98.88, 13.65) * mm, v(-98.74, 13.41) * mm, v(-98.83, 13.13) * mm, v(-99.09, 12.98) * mm]});
            skFitSpline(sketch, "E3577", {"points": [v(-99.09, 12.98) * mm, v(-99.24, 12.89) * mm, v(-99.4, 12.8) * mm, v(-99.55, 12.73) * mm]});
            skFitSpline(sketch, "E3578", {"points": [v(-99.55, 12.73) * mm, v(-100.06, 12.45) * mm, v(-100.57, 12.18) * mm, v(-101.07, 11.91) * mm]});
            skFitSpline(sketch, "E3579", {"points": [v(-101.07, 11.91) * mm, v(-101.56, 11.64) * mm, v(-102.05, 11.37) * mm, v(-102.54, 11.1) * mm]});
            skFitSpline(sketch, "E3580", {"points": [v(-102.54, 11.1) * mm, v(-102.56, 11.09) * mm, v(-102.59, 11.06) * mm, v(-102.62, 11.03) * mm]});
            skFitSpline(sketch, "E3581", {"points": [v(-102.62, 11.03) * mm, v(-102.59, 10.92) * mm, v(-102.56, 10.8) * mm, v(-102.53, 10.69) * mm]});
            skFitSpline(sketch, "E3582", {"points": [v(-102.53, 10.69) * mm, v(-102.45, 10.4) * mm, v(-102.37, 10.1) * mm, v(-102.29, 9.81) * mm]});
            skFitSpline(sketch, "E3583", {"points": [v(-102.29, 9.81) * mm, v(-102.18, 9.4) * mm, v(-102.07, 8.98) * mm, v(-101.96, 8.56) * mm]});
            skFitSpline(sketch, "E3584", {"points": [v(-101.96, 8.56) * mm, v(-101.8, 7.91) * mm, v(-101.63, 7.26) * mm, v(-101.46, 6.62) * mm]});
            skFitSpline(sketch, "E3585", {"points": [v(-101.46, 6.62) * mm, v(-101.44, 6.51) * mm, v(-101.4, 6.45) * mm, v(-101.29, 6.43) * mm]});
            skFitSpline(sketch, "E3586", {"points": [v(-101.29, 6.43) * mm, v(-100.46, 6.22) * mm, v(-99.63, 6) * mm, v(-98.8, 5.79) * mm]});
            skFitSpline(sketch, "E3587", {"points": [v(-98.8, 5.79) * mm, v(-98.25, 5.64) * mm, v(-97.69, 5.48) * mm, v(-97.12, 5.33) * mm]});
            skFitSpline(sketch, "E3588", {"points": [v(-97.12, 5.33) * mm, v(-97.03, 5.3) * mm, v(-96.94, 5.3) * mm, v(-96.83, 5.27) * mm]});
            skFitSpline(sketch, "E3589", {"points": [v(-96.83, 5.27) * mm, v(-96.66, 5.56) * mm, v(-96.5, 5.85) * mm, v(-96.34, 6.15) * mm]});
            skFitSpline(sketch, "E3590", {"points": [v(-96.34, 6.15) * mm, v(-96.1, 6.6) * mm, v(-95.84, 7.06) * mm, v(-95.6, 7.51) * mm]});
            skFitSpline(sketch, "E3591", {"points": [v(-95.6, 7.51) * mm, v(-95.4, 7.88) * mm, v(-95.2, 8.26) * mm, v(-95, 8.63) * mm]});
            skFitSpline(sketch, "E3592", {"points": [v(-95, 8.63) * mm, v(-94.96, 8.7) * mm, v(-94.92, 8.78) * mm, v(-94.88, 8.84) * mm]});
            skFitSpline(sketch, "E3593", {"points": [v(-94.88, 8.84) * mm, v(-94.72, 9.07) * mm, v(-94.45, 9.13) * mm, v(-94.23, 9) * mm]});
            skFitSpline(sketch, "E3594", {"points": [v(-94.23, 9) * mm, v(-94, 8.86) * mm, v(-93.91, 8.56) * mm, v(-94.03, 8.33) * mm]});
            skFitSpline(sketch, "E3595", {"points": [v(-94.03, 8.33) * mm, v(-94.12, 8.16) * mm, v(-94.23, 8) * mm, v(-94.32, 7.83) * mm]});
            skFitSpline(sketch, "E3596", {"points": [v(-94.32, 7.83) * mm, v(-94.42, 7.65) * mm, v(-94.5, 7.48) * mm, v(-94.6, 7.28) * mm]});
            skFitSpline(sketch, "E3597", {"points": [v(-94.6, 7.28) * mm, v(-94.12, 7.13) * mm, v(-93.66, 6.98) * mm, v(-93.19, 6.83) * mm]});
            skFitSpline(sketch, "E3598", {"points": [v(-93.19, 6.83) * mm, v(-93.16, 6.88) * mm, v(-93.13, 6.93) * mm, v(-93.1, 6.98) * mm]});
            skFitSpline(sketch, "E3599", {"points": [v(-93.1, 6.98) * mm, v(-92.78, 7.68) * mm, v(-92.46, 8.39) * mm, v(-92.14, 9.1) * mm]});
            skFitSpline(sketch, "E3600", {"points": [v(-92.14, 9.1) * mm, v(-92.08, 9.21) * mm, v(-92.04, 9.34) * mm, v(-91.98, 9.46) * mm]});
            skFitSpline(sketch, "E3601", {"points": [v(-91.98, 9.46) * mm, v(-91.84, 9.7) * mm, v(-91.57, 9.78) * mm, v(-91.34, 9.68) * mm]});
            skFitSpline(sketch, "E3602", {"points": [v(-91.34, 9.68) * mm, v(-91.1, 9.57) * mm, v(-91, 9.3) * mm, v(-91.1, 9.04) * mm]});
            skFitSpline(sketch, "E3603", {"points": [v(-91.1, 9.04) * mm, v(-91.22, 8.76) * mm, v(-91.34, 8.49) * mm, v(-91.47, 8.2) * mm]});
            skFitSpline(sketch, "E3604", {"points": [v(-91.47, 8.2) * mm, v(-91.7, 7.7) * mm, v(-91.94, 7.18) * mm, v(-92.18, 6.66) * mm]});
            skFitSpline(sketch, "E3605", {"points": [v(-92.18, 6.66) * mm, v(-92.2, 6.6) * mm, v(-92.22, 6.55) * mm, v(-92.25, 6.48) * mm]});
            skFitSpline(sketch, "E3606", {"points": [v(-92.25, 6.48) * mm, v(-92.1, 6.41) * mm, v(-91.96, 6.35) * mm, v(-91.82, 6.3) * mm]});
            skFitSpline(sketch, "E3607", {"points": [v(-91.82, 6.3) * mm, v(-91.41, 6.14) * mm, v(-91, 6) * mm, v(-90.59, 5.84) * mm]});
            skFitSpline(sketch, "E3608", {"points": [v(-90.59, 5.84) * mm, v(-90.27, 5.73) * mm, v(-89.96, 5.6) * mm, v(-89.65, 5.48) * mm]});
            skFitSpline(sketch, "E3609", {"points": [v(-89.65, 5.48) * mm, v(-89.48, 5.42) * mm, v(-89.37, 5.3) * mm, v(-89.33, 5.12) * mm]});
            skFitSpline(sketch, "E3610", {"points": [v(-89.33, 5.12) * mm, v(-89.26, 4.78) * mm, v(-89.52, 4.48) * mm, v(-89.87, 4.55) * mm]});
            skFitSpline(sketch, "E3611", {"points": [v(-89.87, 4.55) * mm, v(-90.1, 4.6) * mm, v(-90.3, 4.7) * mm, v(-90.52, 4.78) * mm]});
            skFitSpline(sketch, "E3612", {"points": [v(-90.52, 4.78) * mm, v(-91.22, 5.04) * mm, v(-91.93, 5.3) * mm, v(-92.66, 5.57) * mm]});
            skFitSpline(sketch, "E3613", {"points": [v(-92.66, 5.57) * mm, v(-92.88, 5.14) * mm, v(-93.1, 4.7) * mm, v(-93.35, 4.24) * mm]});
            skFitSpline(sketch, "E3614", {"points": [v(-93.35, 4.24) * mm, v(-93.14, 4.17) * mm, v(-92.94, 4.1) * mm, v(-92.75, 4.05) * mm]});
            skFitSpline(sketch, "E3615", {"points": [v(-92.75, 4.05) * mm, v(-92.58, 4) * mm, v(-92.4, 3.97) * mm, v(-92.24, 3.92) * mm]});
            skFitSpline(sketch, "E3616", {"points": [v(-92.24, 3.92) * mm, v(-91.96, 3.84) * mm, v(-91.8, 3.57) * mm, v(-91.87, 3.28) * mm]});
            skFitSpline(sketch, "E3617", {"points": [v(-91.87, 3.28) * mm, v(-91.93, 3.03) * mm, v(-92.2, 2.88) * mm, v(-92.48, 2.95) * mm]});
            skFitSpline(sketch, "E3618", {"points": [v(-92.48, 2.95) * mm, v(-92.67, 3) * mm, v(-92.86, 3.06) * mm, v(-93.05, 3.12) * mm]});
            skFitSpline(sketch, "E3619", {"points": [v(-93.05, 3.12) * mm, v(-93.6, 3.29) * mm, v(-94.13, 3.46) * mm, v(-94.67, 3.62) * mm]});
            skFitSpline(sketch, "E3620", {"points": [v(-94.67, 3.62) * mm, v(-95.22, 3.78) * mm, v(-95.78, 3.93) * mm, v(-96.34, 4.1) * mm]});
            skFitSpline(sketch, "E3621", {"points": [v(-96.34, 4.1) * mm, v(-97.14, 2.73) * mm, v(-97.93, 1.37) * mm, v(-98.74, 0) * mm]});
            skFitSpline(sketch, "E3622", {"points": [v(-98.74, 0) * mm, v(-97.95, -1.34) * mm, v(-97.16, -2.7) * mm, v(-96.35, -4.08) * mm]});
            skFitSpline(sketch, "E3623", {"points": [v(-96.35, -4.08) * mm, v(-96.27, -4.06) * mm, v(-96.18, -4.05) * mm, v(-96.1, -4.03) * mm]});
            skFitSpline(sketch, "E3624", {"points": [v(-96.1, -4.03) * mm, v(-95.49, -3.85) * mm, v(-94.89, -3.66) * mm, v(-94.28, -3.48) * mm]});
            skFitSpline(sketch, "E3625", {"points": [v(-94.28, -3.48) * mm, v(-93.71, -3.31) * mm, v(-93.14, -3.14) * mm, v(-92.56, -2.98) * mm]});
            skFitSpline(sketch, "E3626", {"points": [v(-92.56, -2.98) * mm, v(-92.46, -2.95) * mm, v(-92.34, -2.93) * mm, v(-92.23, -2.95) * mm]});
            skFitSpline(sketch, "E3627", {"points": [v(-92.23, -2.95) * mm, v(-92, -2.99) * mm, v(-91.87, -3.17) * mm, v(-91.86, -3.4) * mm]});
            skFitSpline(sketch, "E3628", {"points": [v(-91.86, -3.4) * mm, v(-91.86, -3.67) * mm, v(-92.01, -3.86) * mm, v(-92.27, -3.93) * mm]});
            skFitSpline(sketch, "E3629", {"points": [v(-92.27, -3.93) * mm, v(-92.57, -4) * mm, v(-92.87, -4.1) * mm, v(-93.16, -4.18) * mm]});
            skFitSpline(sketch, "E3630", {"points": [v(-93.16, -4.18) * mm, v(-93.22, -4.2) * mm, v(-93.27, -4.22) * mm, v(-93.35, -4.25) * mm]});
            skFitSpline(sketch, "E3631", {"points": [v(-93.35, -4.25) * mm, v(-93.11, -4.7) * mm, v(-92.89, -5.13) * mm, v(-92.66, -5.57) * mm]});
            skFitSpline(sketch, "E3632", {"points": [v(-92.66, -5.57) * mm, v(-92.28, -5.43) * mm, v(-91.92, -5.3) * mm, v(-91.57, -5.17) * mm]});
            skFitSpline(sketch, "E3633", {"points": [v(-91.57, -5.17) * mm, v(-91.17, -5.03) * mm, v(-90.77, -4.87) * mm, v(-90.38, -4.72) * mm]});
            skFitSpline(sketch, "E3634", {"points": [v(-90.38, -4.72) * mm, v(-90.3, -4.7) * mm, v(-90.22, -4.65) * mm, v(-90.14, -4.62) * mm]});
            skFitSpline(sketch, "E3635", {"points": [v(-90.14, -4.62) * mm, v(-90.06, -4.6) * mm, v(-89.99, -4.57) * mm, v(-89.9, -4.55) * mm]});
            skFitSpline(sketch, "E3636", {"points": [v(-89.9, -4.55) * mm, v(-89.63, -4.5) * mm, v(-89.4, -4.63) * mm, v(-89.34, -4.87) * mm]});
            skFitSpline(sketch, "E3637", {"points": [v(-89.34, -4.87) * mm, v(-89.26, -5.12) * mm, v(-89.38, -5.37) * mm, v(-89.64, -5.47) * mm]});
            skFitSpline(sketch, "E3638", {"points": [v(-89.64, -5.47) * mm, v(-89.91, -5.6) * mm, v(-90.2, -5.7) * mm, v(-90.48, -5.8) * mm]});
            skFitSpline(sketch, "E3639", {"points": [v(-90.48, -5.8) * mm, v(-91.03, -6.01) * mm, v(-91.59, -6.22) * mm, v(-92.14, -6.43) * mm]});
            skFitSpline(sketch, "E3640", {"points": [v(-92.14, -6.43) * mm, v(-92.17, -6.44) * mm, v(-92.2, -6.45) * mm, v(-92.25, -6.48) * mm]});
            skFitSpline(sketch, "E3641", {"points": [v(-92.25, -6.48) * mm, v(-92.17, -6.68) * mm, v(-92.08, -6.89) * mm, v(-92, -7.09) * mm]});
            skFitSpline(sketch, "E3642", {"points": [v(-92, -7.09) * mm, v(-91.7, -7.71) * mm, v(-91.42, -8.34) * mm, v(-91.14, -8.96) * mm]});
            skFitSpline(sketch, "E3643", {"points": [v(-91.14, -8.96) * mm, v(-91.12, -9) * mm, v(-91.1, -9.05) * mm, v(-91.09, -9.1) * mm]});
            skFitSpline(sketch, "E3644", {"points": [v(-91.09, -9.1) * mm, v(-91.02, -9.32) * mm, v(-91.12, -9.56) * mm, v(-91.32, -9.67) * mm]});
            skFitSpline(sketch, "E3645", {"points": [v(-91.32, -9.67) * mm, v(-91.54, -9.78) * mm, v(-91.8, -9.72) * mm, v(-91.94, -9.51) * mm]});
            skFitSpline(sketch, "E3646", {"points": [v(-91.94, -9.51) * mm, v(-92.05, -9.33) * mm, v(-92.12, -9.13) * mm, v(-92.21, -8.93) * mm]});
            skFitSpline(sketch, "E3647", {"points": [v(-92.21, -8.93) * mm, v(-92.52, -8.25) * mm, v(-92.83, -7.58) * mm, v(-93.14, -6.9) * mm]});
            skFitSpline(sketch, "E3648", {"points": [v(-93.14, -6.9) * mm, v(-93.15, -6.88) * mm, v(-93.17, -6.87) * mm, v(-93.2, -6.83) * mm]});
            skFitSpline(sketch, "E3649", {"points": [v(-93.2, -6.83) * mm, v(-93.65, -6.98) * mm, v(-94.11, -7.12) * mm, v(-94.6, -7.28) * mm]});
            skFitSpline(sketch, "E3650", {"points": [v(-94.6, -7.28) * mm, v(-94.5, -7.47) * mm, v(-94.42, -7.64) * mm, v(-94.33, -7.81) * mm]});
            skFitSpline(sketch, "E3651", {"points": [v(-94.33, -7.81) * mm, v(-94.24, -7.98) * mm, v(-94.14, -8.13) * mm, v(-94.05, -8.29) * mm]});
            skFitSpline(sketch, "E3652", {"points": [v(-94.05, -8.29) * mm, v(-93.9, -8.54) * mm, v(-94, -8.86) * mm, v(-94.23, -9) * mm]});
            skFitSpline(sketch, "E3653", {"points": [v(-94.23, -9) * mm, v(-94.47, -9.14) * mm, v(-94.75, -9.06) * mm, v(-94.9, -8.8) * mm]});
            skFitSpline(sketch, "E3654", {"points": [v(-94.9, -8.8) * mm, v(-95, -8.63) * mm, v(-95.09, -8.47) * mm, v(-95.17, -8.3) * mm]});
            skFitSpline(sketch, "E3655", {"points": [v(-95.17, -8.3) * mm, v(-95.44, -7.8) * mm, v(-95.7, -7.3) * mm, v(-95.97, -6.8) * mm]});
            skFitSpline(sketch, "E3656", {"points": [v(-95.97, -6.8) * mm, v(-96.25, -6.3) * mm, v(-96.54, -5.8) * mm, v(-96.83, -5.27) * mm]});
            skFitSpline(sketch, "E3657", {"points": [v(-96.83, -5.27) * mm, v(-96.93, -5.3) * mm, v(-97.03, -5.3) * mm, v(-97.13, -5.33) * mm]});
            skFitSpline(sketch, "E3658", {"points": [v(-97.13, -5.33) * mm, v(-97.51, -5.43) * mm, v(-97.89, -5.53) * mm, v(-98.27, -5.63) * mm]});
            skFitSpline(sketch, "E3659", {"points": [v(-98.27, -5.63) * mm, v(-98.8, -5.77) * mm, v(-99.34, -5.92) * mm, v(-99.88, -6.07) * mm]});
            skFitSpline(sketch, "E3660", {"points": [v(-99.88, -6.07) * mm, v(-100.34, -6.19) * mm, v(-100.8, -6.31) * mm, v(-101.27, -6.42) * mm]});
            skFitSpline(sketch, "E3661", {"points": [v(-101.27, -6.42) * mm, v(-101.38, -6.45) * mm, v(-101.43, -6.49) * mm, v(-101.46, -6.6) * mm]});
            skFitSpline(sketch, "E3662", {"points": [v(-101.46, -6.6) * mm, v(-101.69, -7.5) * mm, v(-101.92, -8.41) * mm, v(-102.15, -9.31) * mm]});
            skFitSpline(sketch, "E3663", {"points": [v(-102.15, -9.31) * mm, v(-102.3, -9.88) * mm, v(-102.46, -10.45) * mm, v(-102.62, -11.04) * mm]});
            skFitSpline(sketch, "E3664", {"points": [v(-102.62, -11.04) * mm, v(-102.56, -11.08) * mm, v(-102.5, -11.13) * mm, v(-102.43, -11.17) * mm]});
            skFitSpline(sketch, "E3665", {"points": [v(-102.43, -11.17) * mm, v(-102.03, -11.39) * mm, v(-101.63, -11.6) * mm, v(-101.23, -11.82) * mm]});
            skFitSpline(sketch, "E3666", {"points": [v(-101.23, -11.82) * mm, v(-100.55, -12.2) * mm, v(-99.87, -12.55) * mm, v(-99.19, -12.92) * mm]});
            skFitSpline(sketch, "E3667", {"points": [v(-99.19, -12.92) * mm, v(-99.15, -12.94) * mm, v(-99.11, -12.96) * mm, v(-99.08, -12.98) * mm]});
            skFitSpline(sketch, "E3668", {"points": [v(-99.08, -12.98) * mm, v(-98.83, -13.14) * mm, v(-98.74, -13.43) * mm, v(-98.89, -13.66) * mm]});
            skFitSpline(sketch, "E3669", {"points": [v(-98.89, -13.66) * mm, v(-99.03, -13.9) * mm, v(-99.35, -13.97) * mm, v(-99.6, -13.83) * mm]});
            skFitSpline(sketch, "E3670", {"points": [v(-99.6, -13.83) * mm, v(-99.89, -13.67) * mm, v(-100.17, -13.5) * mm, v(-100.46, -13.35) * mm]});
            skFitSpline(sketch, "E3671", {"points": [v(-100.46, -13.35) * mm, v(-100.5, -13.33) * mm, v(-100.54, -13.31) * mm, v(-100.6, -13.28) * mm]});
            skFitSpline(sketch, "E3672", {"points": [v(-100.6, -13.28) * mm, v(-100.76, -13.76) * mm, v(-100.9, -14.22) * mm, v(-101.05, -14.68) * mm]});
            skFitSpline(sketch, "E3673", {"points": [v(-101.05, -14.68) * mm, v(-101.02, -14.7) * mm, v(-101.01, -14.73) * mm, v(-101, -14.74) * mm]});
            skFitSpline(sketch, "E3674", {"points": [v(-101, -14.74) * mm, v(-100.6, -14.91) * mm, v(-100.22, -15.08) * mm, v(-99.84, -15.26) * mm]});
            skFitSpline(sketch, "E3675", {"points": [v(-99.84, -15.26) * mm, v(-99.5, -15.41) * mm, v(-99.17, -15.57) * mm, v(-98.84, -15.72) * mm]});
            skFitSpline(sketch, "E3676", {"points": [v(-98.84, -15.72) * mm, v(-98.7, -15.78) * mm, v(-98.57, -15.83) * mm, v(-98.44, -15.9) * mm]});
            skFitSpline(sketch, "E3677", {"points": [v(-98.44, -15.9) * mm, v(-98.29, -15.97) * mm, v(-98.18, -16.1) * mm, v(-98.16, -16.29) * mm]});
            skFitSpline(sketch, "E3678", {"points": [v(-98.16, -16.29) * mm, v(-98.13, -16.67) * mm, v(-98.48, -16.92) * mm, v(-98.86, -16.77) * mm]});
            skFitSpline(sketch, "E3679", {"points": [v(-98.86, -16.77) * mm, v(-99.14, -16.66) * mm, v(-99.42, -16.53) * mm, v(-99.7, -16.4) * mm]});
            skFitSpline(sketch, "E3680", {"points": [v(-99.7, -16.4) * mm, v(-100.2, -16.17) * mm, v(-100.72, -15.93) * mm, v(-101.24, -15.7) * mm]});
            skFitSpline(sketch, "E3681", {"points": [v(-101.24, -15.7) * mm, v(-101.29, -15.67) * mm, v(-101.34, -15.66) * mm, v(-101.4, -15.63) * mm]});
            skSolve(sketch);
        }
        {
            var Q0;
            Q0=makeQuery(id+"F0.imprint","IMPRINT",FACE,{"disambiguationData":[TD([[makeQuery(id+"F0.imprint","IMPRINT",EDGE,{"derivedFrom":sQuery(id+"F0.wireOp",EDGE,"E3232")}),-1.0]])]});
            var Q1;
            Q1=makeQuery(id+"F0.imprint","IMPRINT",FACE,{"disambiguationData":[TD([[makeQuery(id+"F0.imprint","IMPRINT",EDGE,{"derivedFrom":sQuery(id+"F0.wireOp",EDGE,"E2411")}),-1.0]])]});
            var Q2;
            Q2=makeQuery(id+"F0.imprint","IMPRINT",FACE,{"disambiguationData":[TD([[makeQuery(id+"F0.imprint","IMPRINT",EDGE,{"derivedFrom":sQuery(id+"F0.wireOp",EDGE,"E1834")}),-1.0]])]});
            var Q3;
            Q3=makeQuery(id+"F0.imprint","IMPRINT",FACE,{"disambiguationData":[TD([[makeQuery(id+"F0.imprint","IMPRINT",EDGE,{"derivedFrom":sQuery(id+"F0.wireOp",EDGE,"E0")}),-1.0]])]});
            var Q4;
            Q4=makeQuery(id+"F0.imprint","IMPRINT",FACE,{"disambiguationData":[TD([[makeQuery(id+"F0.imprint","IMPRINT",EDGE,{"derivedFrom":sQuery(id+"F0.wireOp",EDGE,"E1384")}),-1.0]])]});
            extrude(context, id + "F1", {"entities" : qUnion([Q0, Q1, Q2, Q3, Q4]), "depth" : 0.8 * mm});
        }
    });
